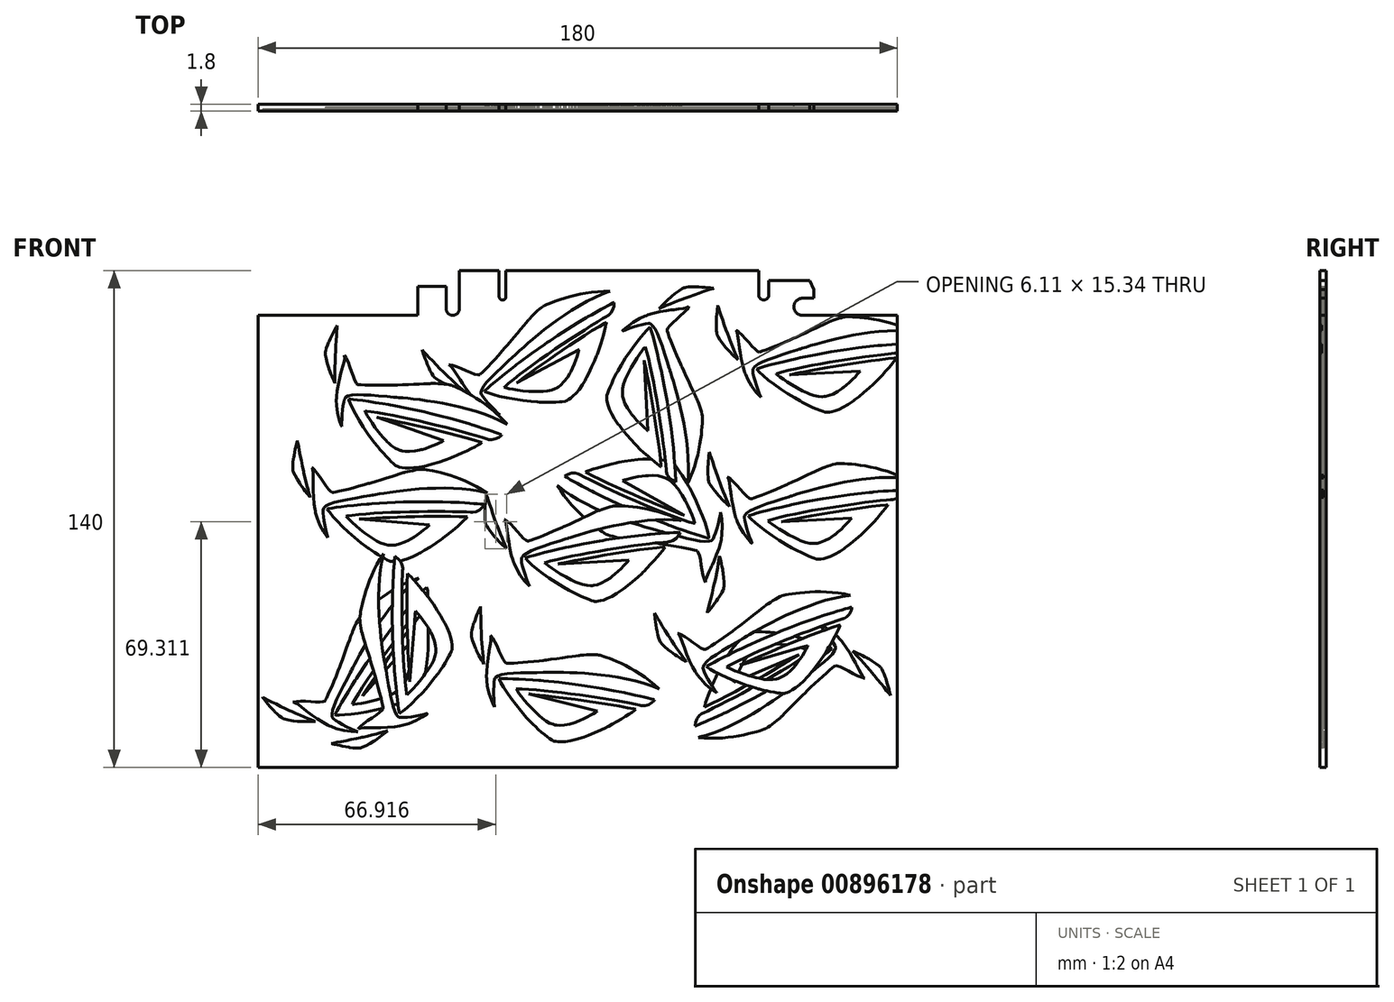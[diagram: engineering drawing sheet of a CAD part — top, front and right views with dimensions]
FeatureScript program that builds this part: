
annotation { "Feature Type Name" : "Feature", "Feature Type Description" : "" }
export const myFeature = defineFeature(function(context is Context, id is Id, definition is map)
    precondition{}
    {
        {
            var Q0;
            Q0=qCreatedBy(makeId("Front.planeOp"),FACE);
            var sketch = newSketch(context, id + "F0", { "sketchPlane" : qUnion([Q0])});
            skLineSegment(sketch, "E0", {"start": v(0, -8.2) * mm, "end": v(0, 0) * mm});
            skLineSegment(sketch, "E1", {"start": v(0, 0) * mm, "end": v(8, 0) * mm});
            skLineSegment(sketch, "E2", {"start": v(8, 0) * mm, "end": v(8, -6.35) * mm});
            skLineSegment(sketch, "E3", {"start": v(9.85, -8.2) * mm, "end": v(9.85, -8.2) * mm});
            skLineSegment(sketch, "E4", {"start": v(11.7, -6.35) * mm, "end": v(11.7, 4.4) * mm});
            skLineSegment(sketch, "E5", {"start": v(11.7, 4.4) * mm, "end": v(22.9, 4.4) * mm});
            skLineSegment(sketch, "E6", {"start": v(22.9, 4.4) * mm, "end": v(22.9, -2.95) * mm});
            skLineSegment(sketch, "E7", {"start": v(23.85, -3.9) * mm, "end": v(23.85, -3.9) * mm});
            skLineSegment(sketch, "E8", {"start": v(24.8, -2.95) * mm, "end": v(24.8, 4.4) * mm});
            skLineSegment(sketch, "E9", {"start": v(24.8, 4.4) * mm, "end": v(96, 4.4) * mm});
            skLineSegment(sketch, "E10", {"start": v(96, 4.4) * mm, "end": v(96, -2.5) * mm});
            skLineSegment(sketch, "E11", {"start": v(97.4, -3.9) * mm, "end": v(97.4, -3.9) * mm});
            skLineSegment(sketch, "E12", {"start": v(98.8, -2.5) * mm, "end": v(98.8, 1.6) * mm});
            skLineSegment(sketch, "E13", {"start": v(98.8, 1.6) * mm, "end": v(110.3, 1.6) * mm});
            skLineSegment(sketch, "E14", {"start": v(110.3, 1.6) * mm, "end": v(111.5, -0.9) * mm});
            skLineSegment(sketch, "E15", {"start": v(111.5, -0.9) * mm, "end": v(111.5, -3.4) * mm});
            skLineSegment(sketch, "E16", {"start": v(111.5, -3.4) * mm, "end": v(108.3, -3.4) * mm});
            skLineSegment(sketch, "E17", {"start": v(105.9, -5.8) * mm, "end": v(105.9, -5.8) * mm});
            skLineSegment(sketch, "E18", {"start": v(108.3, -8.2) * mm, "end": v(135, -8.2) * mm});
            skLineSegment(sketch, "E19", {"start": v(135, -8.2) * mm, "end": v(135, -135.6) * mm});
            skLineSegment(sketch, "E20", {"start": v(135, -135.6) * mm, "end": v(-45, -135.6) * mm});
            skLineSegment(sketch, "E21", {"start": v(-45, -135.6) * mm, "end": v(-45, -8.2) * mm});
            skLineSegment(sketch, "E22", {"start": v(-45, -8.2) * mm, "end": v(0, -8.2) * mm});
            skPoint(sketch, "E23.visualSharp", {"position": v(98.8, -3.9) * mm});
            skArc(sketch, "E23.filletArc", {"start": v(97.4, -3.9) * mm, "mid": v(98.39, -3.49) * mm, "end": v(98.8, -2.5) * mm});
            skPoint(sketch, "E24.visualSharp", {"position": v(96, -3.9) * mm});
            skArc(sketch, "E24.filletArc", {"start": v(96, -2.5) * mm, "mid": v(96.41, -3.49) * mm, "end": v(97.4, -3.9) * mm});
            skPoint(sketch, "E25.visualSharp", {"position": v(24.8, -3.9) * mm});
            skArc(sketch, "E25.filletArc", {"start": v(23.85, -3.9) * mm, "mid": v(24.52, -3.62) * mm, "end": v(24.8, -2.95) * mm});
            skPoint(sketch, "E26.visualSharp", {"position": v(22.9, -3.9) * mm});
            skArc(sketch, "E26.filletArc", {"start": v(22.9, -2.95) * mm, "mid": v(23.18, -3.62) * mm, "end": v(23.85, -3.9) * mm});
            skPoint(sketch, "E27.visualSharp", {"position": v(11.7, -8.2) * mm});
            skArc(sketch, "E27.filletArc", {"start": v(9.85, -8.2) * mm, "mid": v(11.16, -7.66) * mm, "end": v(11.7, -6.35) * mm});
            skPoint(sketch, "E28.visualSharp", {"position": v(8, -8.2) * mm});
            skArc(sketch, "E28.filletArc", {"start": v(8, -6.35) * mm, "mid": v(8.54, -7.66) * mm, "end": v(9.85, -8.2) * mm});
            skPoint(sketch, "E29.visualSharp", {"position": v(105.9, -3.4) * mm});
            skArc(sketch, "E29.filletArc", {"start": v(108.3, -3.4) * mm, "mid": v(106.6, -4.1) * mm, "end": v(105.9, -5.8) * mm});
            skPoint(sketch, "E30.visualSharp", {"position": v(105.9, -8.2) * mm});
            skArc(sketch, "E30.filletArc", {"start": v(105.9, -5.8) * mm, "mid": v(106.6, -7.5) * mm, "end": v(108.3, -8.2) * mm});
            skSolve(sketch);
        }
        {
            var Q0;
            Q0=makeQuery(id+"F0.imprint","IMPRINT",FACE,{"disambiguationData":[TD([[makeQuery(id+"F0.imprint","IMPRINT",EDGE,{"derivedFrom":sQuery(id+"F0.wireOp",EDGE,"E0")}),-1.0]])]});
            extrude(context, id + "F1", {"entities" : qUnion([Q0]), "depth" : 1.8 * mm, "offsetDistance" : 25 * mm});
        }
        {
            var Q0;
            Q0=makeQuery(id+"F1.opExtrude","CAP_FACE",FACE,{"disambiguationData":[OSD([sQuery(id+"F0.wireOp",EDGE,"E0"),sQuery(id+"F0.wireOp",EDGE,"E1"),sQuery(id+"F0.wireOp",EDGE,"E2"),sQuery(id+"F0.wireOp",EDGE,"E4"),sQuery(id+"F0.wireOp",EDGE,"E5"),sQuery(id+"F0.wireOp",EDGE,"E6"),sQuery(id+"F0.wireOp",EDGE,"E8"),sQuery(id+"F0.wireOp",EDGE,"E9"),sQuery(id+"F0.wireOp",EDGE,"E10"),sQuery(id+"F0.wireOp",EDGE,"E12"),sQuery(id+"F0.wireOp",EDGE,"E13"),sQuery(id+"F0.wireOp",EDGE,"E14"),sQuery(id+"F0.wireOp",EDGE,"E15"),sQuery(id+"F0.wireOp",EDGE,"E16"),sQuery(id+"F0.wireOp",EDGE,"E18"),sQuery(id+"F0.wireOp",EDGE,"E19"),sQuery(id+"F0.wireOp",EDGE,"E20"),sQuery(id+"F0.wireOp",EDGE,"E21"),sQuery(id+"F0.wireOp",EDGE,"E22"),sQuery(id+"F0.wireOp",EDGE,"E23.filletArc"),sQuery(id+"F0.wireOp",EDGE,"E24.filletArc"),sQuery(id+"F0.wireOp",EDGE,"E25.filletArc"),sQuery(id+"F0.wireOp",EDGE,"E26.filletArc"),sQuery(id+"F0.wireOp",EDGE,"E27.filletArc"),sQuery(id+"F0.wireOp",EDGE,"E28.filletArc"),sQuery(id+"F0.wireOp",EDGE,"E29.filletArc"),sQuery(id+"F0.wireOp",EDGE,"E30.filletArc")])],"isStart":false});
            var sketch = newSketch(context, id + "F2", { "sketchPlane" : qUnion([Q0])});
            skLineSegment(sketch, "E31", {"start": v(86.64, -17.14) * mm, "end": v(86.89, -17.43) * mm});
            skLineSegment(sketch, "E32", {"start": v(85.92, -16.26) * mm, "end": v(86.64, -17.14) * mm});
            skLineSegment(sketch, "E33", {"start": v(85.12, -15.18) * mm, "end": v(85.92, -16.26) * mm});
            skLineSegment(sketch, "E34", {"start": v(84.55, -14.28) * mm, "end": v(85.12, -15.18) * mm});
            skLineSegment(sketch, "E35", {"start": v(84.3, -13.81) * mm, "end": v(84.55, -14.28) * mm});
            skLineSegment(sketch, "E36", {"start": v(84.27, -13.67) * mm, "end": v(84.3, -13.81) * mm});
            skLineSegment(sketch, "E37", {"start": v(84.24, -13.55) * mm, "end": v(84.27, -13.67) * mm});
            skLineSegment(sketch, "E38", {"start": v(84.17, -13.18) * mm, "end": v(84.24, -13.55) * mm});
            skLineSegment(sketch, "E39", {"start": v(84.08, -12.47) * mm, "end": v(84.17, -13.18) * mm});
            skLineSegment(sketch, "E40", {"start": v(84.03, -11.56) * mm, "end": v(84.08, -12.47) * mm});
            skLineSegment(sketch, "E41", {"start": v(84.02, -10.76) * mm, "end": v(84.03, -11.56) * mm});
            skLineSegment(sketch, "E42", {"start": v(84.03, -10.5) * mm, "end": v(84.02, -10.76) * mm});
            skLineSegment(sketch, "E43", {"start": v(84.04, -10.27) * mm, "end": v(84.03, -10.5) * mm});
            skLineSegment(sketch, "E44", {"start": v(84.07, -9.6) * mm, "end": v(84.04, -10.27) * mm});
            skLineSegment(sketch, "E45", {"start": v(84.12, -8.71) * mm, "end": v(84.07, -9.6) * mm});
            skLineSegment(sketch, "E46", {"start": v(84.19, -7.85) * mm, "end": v(84.12, -8.71) * mm});
            skLineSegment(sketch, "E47", {"start": v(84.26, -7.06) * mm, "end": v(84.19, -7.85) * mm});
            skLineSegment(sketch, "E48", {"start": v(84.32, -6.38) * mm, "end": v(84.26, -7.06) * mm});
            skLineSegment(sketch, "E49", {"start": v(84.38, -5.84) * mm, "end": v(84.32, -6.38) * mm});
            skLineSegment(sketch, "E50", {"start": v(84.42, -5.5) * mm, "end": v(84.38, -5.84) * mm});
            skLineSegment(sketch, "E51", {"start": v(84.43, -5.37) * mm, "end": v(84.42, -5.5) * mm});
            skLineSegment(sketch, "E52", {"start": v(84.5, -5.57) * mm, "end": v(84.43, -5.37) * mm});
            skLineSegment(sketch, "E53", {"start": v(84.69, -6.14) * mm, "end": v(84.5, -5.57) * mm});
            skLineSegment(sketch, "E54", {"start": v(84.98, -7.02) * mm, "end": v(84.69, -6.14) * mm});
            skLineSegment(sketch, "E55", {"start": v(85.35, -8.13) * mm, "end": v(84.98, -7.02) * mm});
            skLineSegment(sketch, "E56", {"start": v(85.79, -9.42) * mm, "end": v(85.35, -8.13) * mm});
            skLineSegment(sketch, "E57", {"start": v(86.27, -10.83) * mm, "end": v(85.79, -9.42) * mm});
            skLineSegment(sketch, "E58", {"start": v(86.79, -12.28) * mm, "end": v(86.27, -10.83) * mm});
            skLineSegment(sketch, "E59", {"start": v(87.18, -13.36) * mm, "end": v(86.79, -12.28) * mm});
            skLineSegment(sketch, "E60", {"start": v(87.31, -13.72) * mm, "end": v(87.18, -13.36) * mm});
            skLineSegment(sketch, "E61", {"start": v(87.44, -14.08) * mm, "end": v(87.31, -13.72) * mm});
            skLineSegment(sketch, "E62", {"start": v(87.85, -15.14) * mm, "end": v(87.44, -14.08) * mm});
            skLineSegment(sketch, "E63", {"start": v(88.36, -16.46) * mm, "end": v(87.85, -15.14) * mm});
            skLineSegment(sketch, "E64", {"start": v(88.84, -17.64) * mm, "end": v(88.36, -16.46) * mm});
            skLineSegment(sketch, "E65", {"start": v(89.27, -18.67) * mm, "end": v(88.84, -17.64) * mm});
            skLineSegment(sketch, "E66", {"start": v(89.62, -19.52) * mm, "end": v(89.27, -18.67) * mm});
            skLineSegment(sketch, "E67", {"start": v(89.9, -20.16) * mm, "end": v(89.62, -19.52) * mm});
            skLineSegment(sketch, "E68", {"start": v(90.07, -20.56) * mm, "end": v(89.9, -20.16) * mm});
            skLineSegment(sketch, "E69", {"start": v(90.13, -20.7) * mm, "end": v(90.07, -20.56) * mm});
            skLineSegment(sketch, "E70", {"start": v(90.05, -20.63) * mm, "end": v(90.13, -20.7) * mm});
            skLineSegment(sketch, "E71", {"start": v(89.83, -20.42) * mm, "end": v(90.05, -20.63) * mm});
            skLineSegment(sketch, "E72", {"start": v(89.5, -20.1) * mm, "end": v(89.83, -20.42) * mm});
            skLineSegment(sketch, "E73", {"start": v(89.06, -19.69) * mm, "end": v(89.5, -20.1) * mm});
            skLineSegment(sketch, "E74", {"start": v(88.56, -19.2) * mm, "end": v(89.06, -19.69) * mm});
            skLineSegment(sketch, "E75", {"start": v(88.01, -18.64) * mm, "end": v(88.56, -19.2) * mm});
            skLineSegment(sketch, "E76", {"start": v(87.45, -18.04) * mm, "end": v(88.01, -18.64) * mm});
            skLineSegment(sketch, "E77", {"start": v(87.03, -17.58) * mm, "end": v(87.45, -18.04) * mm});
            skLineSegment(sketch, "E78", {"start": v(86.89, -17.43) * mm, "end": v(87.03, -17.58) * mm});
            skLineSegment(sketch, "E79", {"start": v(106.83, -17.95) * mm, "end": v(107.42, -17.75) * mm});
            skLineSegment(sketch, "E80", {"start": v(105.06, -18.52) * mm, "end": v(106.83, -17.95) * mm});
            skLineSegment(sketch, "E81", {"start": v(102.8, -19.24) * mm, "end": v(105.06, -18.52) * mm});
            skLineSegment(sketch, "E82", {"start": v(100.69, -19.92) * mm, "end": v(102.8, -19.24) * mm});
            skLineSegment(sketch, "E83", {"start": v(98.8, -20.59) * mm, "end": v(100.69, -19.92) * mm});
            skLineSegment(sketch, "E84", {"start": v(97.16, -21.25) * mm, "end": v(98.8, -20.59) * mm});
            skLineSegment(sketch, "E85", {"start": v(95.84, -21.91) * mm, "end": v(97.16, -21.25) * mm});
            skLineSegment(sketch, "E86", {"start": v(94.89, -22.6) * mm, "end": v(95.84, -21.91) * mm});
            skLineSegment(sketch, "E87", {"start": v(94.44, -23.13) * mm, "end": v(94.89, -22.6) * mm});
            skLineSegment(sketch, "E88", {"start": v(94.36, -23.33) * mm, "end": v(94.44, -23.13) * mm});
            skLineSegment(sketch, "E89", {"start": v(94.31, -23.44) * mm, "end": v(94.36, -23.33) * mm});
            skLineSegment(sketch, "E90", {"start": v(94.31, -23.83) * mm, "end": v(94.31, -23.44) * mm});
            skLineSegment(sketch, "E91", {"start": v(94.41, -24.61) * mm, "end": v(94.31, -23.83) * mm});
            skLineSegment(sketch, "E92", {"start": v(94.63, -25.62) * mm, "end": v(94.41, -24.61) * mm});
            skLineSegment(sketch, "E93", {"start": v(94.95, -26.77) * mm, "end": v(94.63, -25.62) * mm});
            skLineSegment(sketch, "E94", {"start": v(95.33, -27.98) * mm, "end": v(94.95, -26.77) * mm});
            skLineSegment(sketch, "E95", {"start": v(95.75, -29.18) * mm, "end": v(95.33, -27.98) * mm});
            skLineSegment(sketch, "E96", {"start": v(96.18, -30.29) * mm, "end": v(95.75, -29.18) * mm});
            skLineSegment(sketch, "E97", {"start": v(96.48, -31) * mm, "end": v(96.18, -30.29) * mm});
            skLineSegment(sketch, "E98", {"start": v(96.6, -31.24) * mm, "end": v(96.48, -31) * mm});
            skLineSegment(sketch, "E99", {"start": v(96.24, -30.91) * mm, "end": v(96.6, -31.24) * mm});
            skLineSegment(sketch, "E100", {"start": v(95.27, -29.84) * mm, "end": v(96.24, -30.91) * mm});
            skLineSegment(sketch, "E101", {"start": v(94.02, -28.15) * mm, "end": v(95.27, -29.84) * mm});
            skLineSegment(sketch, "E102", {"start": v(92.93, -26.28) * mm, "end": v(94.02, -28.15) * mm});
            skLineSegment(sketch, "E103", {"start": v(92.27, -24.86) * mm, "end": v(92.93, -26.28) * mm});
            skLineSegment(sketch, "E104", {"start": v(92.09, -24.37) * mm, "end": v(92.27, -24.86) * mm});
            skLineSegment(sketch, "E105", {"start": v(91.92, -23.9) * mm, "end": v(92.09, -24.37) * mm});
            skLineSegment(sketch, "E106", {"start": v(91.5, -22.48) * mm, "end": v(91.92, -23.9) * mm});
            skLineSegment(sketch, "E107", {"start": v(91.07, -20.55) * mm, "end": v(91.5, -22.48) * mm});
            skLineSegment(sketch, "E108", {"start": v(90.74, -18.7) * mm, "end": v(91.07, -20.55) * mm});
            skLineSegment(sketch, "E109", {"start": v(90.56, -17.46) * mm, "end": v(90.74, -18.7) * mm});
            skLineSegment(sketch, "E110", {"start": v(90.5, -17.05) * mm, "end": v(90.56, -17.46) * mm});
            skLineSegment(sketch, "E111", {"start": v(90.45, -16.6) * mm, "end": v(90.5, -17.05) * mm});
            skLineSegment(sketch, "E112", {"start": v(90.28, -15.26) * mm, "end": v(90.45, -16.6) * mm});
            skLineSegment(sketch, "E113", {"start": v(90.09, -13.9) * mm, "end": v(90.28, -15.26) * mm});
            skLineSegment(sketch, "E114", {"start": v(89.85, -12.95) * mm, "end": v(90.09, -13.9) * mm});
            skLineSegment(sketch, "E115", {"start": v(89.61, -12.5) * mm, "end": v(89.85, -12.95) * mm});
            skLineSegment(sketch, "E116", {"start": v(89.5, -12.4) * mm, "end": v(89.61, -12.5) * mm});
            skLineSegment(sketch, "E117", {"start": v(89.72, -12.49) * mm, "end": v(89.5, -12.4) * mm});
            skLineSegment(sketch, "E118", {"start": v(90.34, -12.92) * mm, "end": v(89.72, -12.49) * mm});
            skLineSegment(sketch, "E119", {"start": v(91.26, -13.75) * mm, "end": v(90.34, -12.92) * mm});
            skLineSegment(sketch, "E120", {"start": v(92.21, -14.77) * mm, "end": v(91.26, -13.75) * mm});
            skLineSegment(sketch, "E121", {"start": v(93.16, -15.85) * mm, "end": v(92.21, -14.77) * mm});
            skLineSegment(sketch, "E122", {"start": v(94.08, -16.88) * mm, "end": v(93.16, -15.85) * mm});
            skLineSegment(sketch, "E123", {"start": v(94.92, -17.75) * mm, "end": v(94.08, -16.88) * mm});
            skLineSegment(sketch, "E124", {"start": v(95.66, -18.33) * mm, "end": v(94.92, -17.75) * mm});
            skLineSegment(sketch, "E125", {"start": v(96.1, -18.53) * mm, "end": v(95.66, -18.33) * mm});
            skLineSegment(sketch, "E126", {"start": v(96.25, -18.52) * mm, "end": v(96.1, -18.53) * mm});
            skLineSegment(sketch, "E127", {"start": v(96.46, -18.46) * mm, "end": v(96.25, -18.52) * mm});
            skLineSegment(sketch, "E128", {"start": v(97.08, -18.26) * mm, "end": v(96.46, -18.46) * mm});
            skLineSegment(sketch, "E129", {"start": v(98.08, -17.91) * mm, "end": v(97.08, -18.26) * mm});
            skLineSegment(sketch, "E130", {"start": v(99.23, -17.48) * mm, "end": v(98.08, -17.91) * mm});
            skLineSegment(sketch, "E131", {"start": v(100.5, -16.97) * mm, "end": v(99.23, -17.48) * mm});
            skLineSegment(sketch, "E132", {"start": v(101.85, -16.41) * mm, "end": v(100.5, -16.97) * mm});
            skLineSegment(sketch, "E133", {"start": v(103.28, -15.81) * mm, "end": v(101.85, -16.41) * mm});
            skLineSegment(sketch, "E134", {"start": v(104.73, -15.18) * mm, "end": v(103.28, -15.81) * mm});
            skLineSegment(sketch, "E135", {"start": v(105.83, -14.69) * mm, "end": v(104.73, -15.18) * mm});
            skLineSegment(sketch, "E136", {"start": v(106.2, -14.52) * mm, "end": v(105.83, -14.69) * mm});
            skLineSegment(sketch, "E137", {"start": v(106.6, -14.34) * mm, "end": v(106.2, -14.52) * mm});
            skLineSegment(sketch, "E138", {"start": v(107.79, -13.8) * mm, "end": v(106.6, -14.34) * mm});
            skLineSegment(sketch, "E139", {"start": v(109.32, -13.1) * mm, "end": v(107.79, -13.8) * mm});
            skLineSegment(sketch, "E140", {"start": v(110.75, -12.43) * mm, "end": v(109.32, -13.1) * mm});
            skLineSegment(sketch, "E141", {"start": v(112.06, -11.81) * mm, "end": v(110.75, -12.43) * mm});
            skLineSegment(sketch, "E142", {"start": v(130.44, -19.3) * mm, "end": v(132.47, -19.06) * mm});
            skLineSegment(sketch, "E143", {"start": v(128.25, -19.57) * mm, "end": v(130.44, -19.3) * mm});
            skLineSegment(sketch, "E144", {"start": v(138.93, -16.33) * mm, "end": v(139.01, -16.1) * mm});
            skLineSegment(sketch, "E145", {"start": v(139.01, -16.1) * mm, "end": v(138.9, -16.1) * mm});
            skLineSegment(sketch, "E146", {"start": v(138.9, -16.1) * mm, "end": v(138.6, -16.1) * mm});
            skLineSegment(sketch, "E147", {"start": v(138.6, -16.1) * mm, "end": v(137.97, -16.11) * mm});
            skLineSegment(sketch, "E148", {"start": v(137.97, -16.11) * mm, "end": v(137.11, -16.15) * mm});
            skLineSegment(sketch, "E149", {"start": v(137.11, -16.15) * mm, "end": v(136.07, -16.2) * mm});
            skLineSegment(sketch, "E150", {"start": v(136.07, -16.2) * mm, "end": v(134.84, -16.28) * mm});
            skLineSegment(sketch, "E151", {"start": v(134.84, -16.28) * mm, "end": v(133.45, -16.38) * mm});
            skLineSegment(sketch, "E152", {"start": v(133.45, -16.38) * mm, "end": v(131.92, -16.51) * mm});
            skLineSegment(sketch, "E153", {"start": v(131.92, -16.51) * mm, "end": v(130.68, -16.62) * mm});
            skLineSegment(sketch, "E154", {"start": v(130.68, -16.62) * mm, "end": v(130.26, -16.66) * mm});
            skLineSegment(sketch, "E155", {"start": v(130.26, -16.66) * mm, "end": v(129.52, -16.73) * mm});
            skLineSegment(sketch, "E156", {"start": v(129.52, -16.73) * mm, "end": v(127.28, -16.97) * mm});
            skLineSegment(sketch, "E157", {"start": v(127.28, -16.97) * mm, "end": v(124.08, -17.36) * mm});
            skLineSegment(sketch, "E158", {"start": v(124.08, -17.36) * mm, "end": v(120.72, -17.82) * mm});
            skLineSegment(sketch, "E159", {"start": v(120.72, -17.82) * mm, "end": v(118.13, -18.22) * mm});
            skLineSegment(sketch, "E160", {"start": v(118.13, -18.22) * mm, "end": v(117.27, -18.36) * mm});
            skLineSegment(sketch, "E161", {"start": v(117.27, -18.36) * mm, "end": v(116.34, -18.5) * mm});
            skLineSegment(sketch, "E162", {"start": v(116.34, -18.5) * mm, "end": v(111.9, -19.31) * mm});
            skLineSegment(sketch, "E163", {"start": v(111.9, -19.31) * mm, "end": v(107.65, -20.17) * mm});
            skLineSegment(sketch, "E164", {"start": v(107.65, -20.17) * mm, "end": v(106.82, -20.35) * mm});
            skLineSegment(sketch, "E165", {"start": v(107.42, -17.75) * mm, "end": v(107.62, -17.69) * mm});
            skLineSegment(sketch, "E166", {"start": v(107.62, -17.69) * mm, "end": v(108.23, -17.49) * mm});
            skLineSegment(sketch, "E167", {"start": v(108.23, -17.49) * mm, "end": v(109.32, -17.14) * mm});
            skLineSegment(sketch, "E168", {"start": v(109.32, -17.14) * mm, "end": v(110.65, -16.73) * mm});
            skLineSegment(sketch, "E169", {"start": v(110.65, -16.73) * mm, "end": v(112.22, -16.27) * mm});
            skLineSegment(sketch, "E170", {"start": v(112.22, -16.27) * mm, "end": v(113.98, -15.78) * mm});
            skLineSegment(sketch, "E171", {"start": v(113.98, -15.78) * mm, "end": v(115.92, -15.27) * mm});
            skLineSegment(sketch, "E172", {"start": v(115.92, -15.27) * mm, "end": v(118, -14.76) * mm});
            skLineSegment(sketch, "E173", {"start": v(118, -14.76) * mm, "end": v(120.22, -14.27) * mm});
            skLineSegment(sketch, "E174", {"start": v(120.22, -14.27) * mm, "end": v(122.53, -13.8) * mm});
            skLineSegment(sketch, "E175", {"start": v(122.53, -13.8) * mm, "end": v(124.91, -13.39) * mm});
            skLineSegment(sketch, "E176", {"start": v(124.91, -13.39) * mm, "end": v(127.34, -13.03) * mm});
            skLineSegment(sketch, "E177", {"start": v(127.34, -13.03) * mm, "end": v(129.8, -12.76) * mm});
            skLineSegment(sketch, "E178", {"start": v(129.8, -12.76) * mm, "end": v(132.25, -12.58) * mm});
            skLineSegment(sketch, "E179", {"start": v(132.25, -12.58) * mm, "end": v(134.68, -12.5) * mm});
            skLineSegment(sketch, "E180", {"start": v(134.68, -12.5) * mm, "end": v(137.05, -12.56) * mm});
            skLineSegment(sketch, "E181", {"start": v(137.05, -12.56) * mm, "end": v(138.77, -12.7) * mm});
            skLineSegment(sketch, "E182", {"start": v(138.77, -12.7) * mm, "end": v(139.34, -12.76) * mm});
            skLineSegment(sketch, "E183", {"start": v(139.34, -12.76) * mm, "end": v(138.95, -12.56) * mm});
            skLineSegment(sketch, "E184", {"start": v(138.95, -12.56) * mm, "end": v(137.76, -12) * mm});
            skLineSegment(sketch, "E185", {"start": v(137.76, -12) * mm, "end": v(136.16, -11.35) * mm});
            skLineSegment(sketch, "E186", {"start": v(136.16, -11.35) * mm, "end": v(134.55, -10.79) * mm});
            skLineSegment(sketch, "E187", {"start": v(134.55, -10.79) * mm, "end": v(132.95, -10.3) * mm});
            skLineSegment(sketch, "E188", {"start": v(132.95, -10.3) * mm, "end": v(131.38, -9.9) * mm});
            skLineSegment(sketch, "E189", {"start": v(131.38, -9.9) * mm, "end": v(129.85, -9.55) * mm});
            skLineSegment(sketch, "E190", {"start": v(129.85, -9.55) * mm, "end": v(128.38, -9.27) * mm});
            skLineSegment(sketch, "E191", {"start": v(128.38, -9.27) * mm, "end": v(126.98, -9.05) * mm});
            skLineSegment(sketch, "E192", {"start": v(126.98, -9.05) * mm, "end": v(125.67, -8.89) * mm});
            skLineSegment(sketch, "E193", {"start": v(125.67, -8.89) * mm, "end": v(124.48, -8.76) * mm});
            skLineSegment(sketch, "E194", {"start": v(117.72, -9.36) * mm, "end": v(116.97, -9.63) * mm});
            skLineSegment(sketch, "E195", {"start": v(116.97, -9.63) * mm, "end": v(116.29, -9.88) * mm});
            skLineSegment(sketch, "E196", {"start": v(116.29, -9.88) * mm, "end": v(115.72, -10.1) * mm});
            skLineSegment(sketch, "E197", {"start": v(115.72, -10.1) * mm, "end": v(115.43, -10.22) * mm});
            skLineSegment(sketch, "E198", {"start": v(97.78, -22.58) * mm, "end": v(96.66, -22.9) * mm});
            skLineSegment(sketch, "E199", {"start": v(96.66, -22.9) * mm, "end": v(95.85, -23.15) * mm});
            skLineSegment(sketch, "E200", {"start": v(95.85, -23.15) * mm, "end": v(95.5, -23.27) * mm});
            skLineSegment(sketch, "E201", {"start": v(104.68, -20.84) * mm, "end": v(102.66, -21.32) * mm});
            skLineSegment(sketch, "E202", {"start": v(115.22, -10.31) * mm, "end": v(114.88, -10.47) * mm});
            skLineSegment(sketch, "E203", {"start": v(95.5, -23.27) * mm, "end": v(95.38, -23.32) * mm});
            skLineSegment(sketch, "E204", {"start": v(102.66, -21.32) * mm, "end": v(100.82, -21.78) * mm});
            skLineSegment(sketch, "E205", {"start": v(114.88, -10.47) * mm, "end": v(114.16, -10.81) * mm});
            skLineSegment(sketch, "E206", {"start": v(95.38, -23.32) * mm, "end": v(95.57, -23.55) * mm});
            skLineSegment(sketch, "E207", {"start": v(100.82, -21.78) * mm, "end": v(99.18, -22.2) * mm});
            skLineSegment(sketch, "E208", {"start": v(114.16, -10.81) * mm, "end": v(113.2, -11.27) * mm});
            skLineSegment(sketch, "E209", {"start": v(95.57, -23.55) * mm, "end": v(96.18, -24.2) * mm});
            skLineSegment(sketch, "E210", {"start": v(99.18, -22.2) * mm, "end": v(97.78, -22.58) * mm});
            skLineSegment(sketch, "E211", {"start": v(113.2, -11.27) * mm, "end": v(112.06, -11.81) * mm});
            skLineSegment(sketch, "E212", {"start": v(106.82, -20.35) * mm, "end": v(106.29, -20.47) * mm});
            skLineSegment(sketch, "E213", {"start": v(96.18, -24.2) * mm, "end": v(97.3, -25.24) * mm});
            skLineSegment(sketch, "E214", {"start": v(97.3, -25.24) * mm, "end": v(98.71, -26.4) * mm});
            skLineSegment(sketch, "E215", {"start": v(108.17, -32.63) * mm, "end": v(108.42, -32.76) * mm});
            skLineSegment(sketch, "E216", {"start": v(108.42, -32.76) * mm, "end": v(109.18, -33.15) * mm});
            skLineSegment(sketch, "E217", {"start": v(109.18, -33.15) * mm, "end": v(110.24, -33.66) * mm});
            skLineSegment(sketch, "E218", {"start": v(110.24, -33.66) * mm, "end": v(111.3, -34.15) * mm});
            skLineSegment(sketch, "E219", {"start": v(107.65, -32.35) * mm, "end": v(108.17, -32.63) * mm});
            skLineSegment(sketch, "E220", {"start": v(106.13, -31.48) * mm, "end": v(107.65, -32.35) * mm});
            skLineSegment(sketch, "E221", {"start": v(104.1, -30.23) * mm, "end": v(106.13, -31.48) * mm});
            skLineSegment(sketch, "E222", {"start": v(102.16, -28.95) * mm, "end": v(104.1, -30.23) * mm});
            skLineSegment(sketch, "E223", {"start": v(100.35, -27.66) * mm, "end": v(102.16, -28.95) * mm});
            skLineSegment(sketch, "E224", {"start": v(98.71, -26.4) * mm, "end": v(100.35, -27.66) * mm});
            skLineSegment(sketch, "E225", {"start": v(115.33, -10.26) * mm, "end": v(115.22, -10.31) * mm});
            skLineSegment(sketch, "E226", {"start": v(106.29, -20.47) * mm, "end": v(104.68, -20.84) * mm});
            skLineSegment(sketch, "E227", {"start": v(118.5, -9.11) * mm, "end": v(117.72, -9.36) * mm});
            skLineSegment(sketch, "E228", {"start": v(115.43, -10.22) * mm, "end": v(115.33, -10.26) * mm});
            skLineSegment(sketch, "E229", {"start": v(119.24, -8.89) * mm, "end": v(118.5, -9.11) * mm});
            skLineSegment(sketch, "E230", {"start": v(119.9, -8.71) * mm, "end": v(119.24, -8.89) * mm});
            skLineSegment(sketch, "E231", {"start": v(120.31, -8.63) * mm, "end": v(119.9, -8.71) * mm});
            skLineSegment(sketch, "E232", {"start": v(120.45, -8.6) * mm, "end": v(120.31, -8.63) * mm});
            skLineSegment(sketch, "E233", {"start": v(120.5, -8.6) * mm, "end": v(120.45, -8.6) * mm});
            skLineSegment(sketch, "E234", {"start": v(120.66, -8.6) * mm, "end": v(120.5, -8.6) * mm});
            skLineSegment(sketch, "E235", {"start": v(121.08, -8.59) * mm, "end": v(120.66, -8.6) * mm});
            skLineSegment(sketch, "E236", {"start": v(121.69, -8.6) * mm, "end": v(121.08, -8.59) * mm});
            skLineSegment(sketch, "E237", {"start": v(122.47, -8.62) * mm, "end": v(121.69, -8.6) * mm});
            skLineSegment(sketch, "E238", {"start": v(123.4, -8.68) * mm, "end": v(122.47, -8.62) * mm});
            skLineSegment(sketch, "E239", {"start": v(124.48, -8.76) * mm, "end": v(123.4, -8.68) * mm});
            skLineSegment(sketch, "E240", {"start": v(138.57, -17) * mm, "end": v(138.93, -16.33) * mm});
            skLineSegment(sketch, "E241", {"start": v(137.87, -17.82) * mm, "end": v(138.57, -17) * mm});
            skLineSegment(sketch, "E242", {"start": v(136.96, -18.43) * mm, "end": v(137.87, -17.82) * mm});
            skLineSegment(sketch, "E243", {"start": v(136.15, -18.7) * mm, "end": v(136.96, -18.43) * mm});
            skLineSegment(sketch, "E244", {"start": v(135.87, -18.73) * mm, "end": v(136.15, -18.7) * mm});
            skLineSegment(sketch, "E245", {"start": v(135.47, -18.76) * mm, "end": v(135.87, -18.73) * mm});
            skLineSegment(sketch, "E246", {"start": v(134.29, -18.87) * mm, "end": v(135.47, -18.76) * mm});
            skLineSegment(sketch, "E247", {"start": v(132.47, -19.06) * mm, "end": v(134.29, -18.87) * mm});
            skLineSegment(sketch, "E248", {"start": v(107.74, -24.36) * mm, "end": v(106.46, -24.62) * mm});
            skLineSegment(sketch, "E249", {"start": v(109.3, -24.06) * mm, "end": v(107.74, -24.36) * mm});
            skLineSegment(sketch, "E250", {"start": v(111.12, -23.72) * mm, "end": v(109.3, -24.06) * mm});
            skLineSegment(sketch, "E251", {"start": v(113.14, -23.34) * mm, "end": v(111.12, -23.72) * mm});
            skLineSegment(sketch, "E252", {"start": v(115.34, -22.95) * mm, "end": v(113.14, -23.34) * mm});
            skLineSegment(sketch, "E253", {"start": v(117.67, -22.54) * mm, "end": v(115.34, -22.95) * mm});
            skLineSegment(sketch, "E254", {"start": v(120.1, -22.13) * mm, "end": v(117.67, -22.54) * mm});
            skLineSegment(sketch, "E255", {"start": v(122.6, -21.73) * mm, "end": v(120.1, -22.13) * mm});
            skLineSegment(sketch, "E256", {"start": v(125.12, -21.35) * mm, "end": v(122.6, -21.73) * mm});
            skLineSegment(sketch, "E257", {"start": v(127.63, -21) * mm, "end": v(125.12, -21.35) * mm});
            skLineSegment(sketch, "E258", {"start": v(130.1, -20.69) * mm, "end": v(127.63, -21) * mm});
            skLineSegment(sketch, "E259", {"start": v(132.47, -20.42) * mm, "end": v(130.1, -20.69) * mm});
            skLineSegment(sketch, "E260", {"start": v(134.16, -20.26) * mm, "end": v(132.47, -20.42) * mm});
            skLineSegment(sketch, "E261", {"start": v(134.73, -20.22) * mm, "end": v(134.16, -20.26) * mm});
            skLineSegment(sketch, "E262", {"start": v(134.66, -20.33) * mm, "end": v(134.73, -20.22) * mm});
            skLineSegment(sketch, "E263", {"start": v(134.43, -20.67) * mm, "end": v(134.66, -20.33) * mm});
            skLineSegment(sketch, "E264", {"start": v(133.97, -21.3) * mm, "end": v(134.43, -20.67) * mm});
            skLineSegment(sketch, "E265", {"start": v(133.34, -22.08) * mm, "end": v(133.97, -21.3) * mm});
            skLineSegment(sketch, "E266", {"start": v(132.59, -22.98) * mm, "end": v(133.34, -22.08) * mm});
            skLineSegment(sketch, "E267", {"start": v(131.7, -23.98) * mm, "end": v(132.59, -22.98) * mm});
            skLineSegment(sketch, "E268", {"start": v(130.74, -25.05) * mm, "end": v(131.7, -23.98) * mm});
            skLineSegment(sketch, "E269", {"start": v(129.68, -26.16) * mm, "end": v(130.74, -25.05) * mm});
            skLineSegment(sketch, "E270", {"start": v(128.85, -27.01) * mm, "end": v(129.68, -26.16) * mm});
            skLineSegment(sketch, "E271", {"start": v(128.57, -27.3) * mm, "end": v(128.85, -27.01) * mm});
            skLineSegment(sketch, "E272", {"start": v(115.89, -35.5) * mm, "end": v(116.6, -35.37) * mm});
            skLineSegment(sketch, "E273", {"start": v(115.38, -35.54) * mm, "end": v(115.89, -35.5) * mm});
            skLineSegment(sketch, "E274", {"start": v(115.16, -35.54) * mm, "end": v(115.38, -35.54) * mm});
            skLineSegment(sketch, "E275", {"start": v(115.09, -35.53) * mm, "end": v(115.16, -35.54) * mm});
            skLineSegment(sketch, "E276", {"start": v(114.98, -35.52) * mm, "end": v(115.09, -35.53) * mm});
            skLineSegment(sketch, "E277", {"start": v(114.68, -35.45) * mm, "end": v(114.98, -35.52) * mm});
            skLineSegment(sketch, "E278", {"start": v(111.3, -34.15) * mm, "end": v(112.32, -34.58) * mm});
            skLineSegment(sketch, "E279", {"start": v(112.32, -34.58) * mm, "end": v(113.25, -34.96) * mm});
            skLineSegment(sketch, "E280", {"start": v(113.25, -34.96) * mm, "end": v(114.05, -35.25) * mm});
            skLineSegment(sketch, "E281", {"start": v(114.05, -35.25) * mm, "end": v(114.68, -35.45) * mm});
            skLineSegment(sketch, "E282", {"start": v(116.6, -35.37) * mm, "end": v(117.48, -35.12) * mm});
            skLineSegment(sketch, "E283", {"start": v(117.48, -35.12) * mm, "end": v(118.55, -34.72) * mm});
            skLineSegment(sketch, "E284", {"start": v(118.55, -34.72) * mm, "end": v(119.78, -34.14) * mm});
            skLineSegment(sketch, "E285", {"start": v(119.78, -34.14) * mm, "end": v(121.17, -33.32) * mm});
            skLineSegment(sketch, "E286", {"start": v(121.17, -33.32) * mm, "end": v(122.34, -32.54) * mm});
            skLineSegment(sketch, "E287", {"start": v(122.34, -32.54) * mm, "end": v(122.71, -32.25) * mm});
            skLineSegment(sketch, "E288", {"start": v(122.71, -32.25) * mm, "end": v(123.07, -31.98) * mm});
            skLineSegment(sketch, "E289", {"start": v(123.07, -31.98) * mm, "end": v(124.15, -31.16) * mm});
            skLineSegment(sketch, "E290", {"start": v(124.15, -31.16) * mm, "end": v(125.64, -29.95) * mm});
            skLineSegment(sketch, "E291", {"start": v(125.64, -29.95) * mm, "end": v(127.13, -28.66) * mm});
            skLineSegment(sketch, "E292", {"start": v(127.13, -28.66) * mm, "end": v(128.22, -27.64) * mm});
            skLineSegment(sketch, "E293", {"start": v(128.22, -27.64) * mm, "end": v(128.57, -27.3) * mm});
            skLineSegment(sketch, "E294", {"start": v(106.46, -24.62) * mm, "end": v(105.5, -24.8) * mm});
            skLineSegment(sketch, "E295", {"start": v(105.5, -24.8) * mm, "end": v(104.9, -24.93) * mm});
            skLineSegment(sketch, "E296", {"start": v(104.9, -24.93) * mm, "end": v(104.69, -24.98) * mm});
            skLineSegment(sketch, "E297", {"start": v(104.69, -24.98) * mm, "end": v(124.58, -23.9) * mm});
            skLineSegment(sketch, "E298", {"start": v(124.58, -23.9) * mm, "end": v(124.47, -24.01) * mm});
            skLineSegment(sketch, "E299", {"start": v(124.47, -24.01) * mm, "end": v(124.18, -24.35) * mm});
            skLineSegment(sketch, "E300", {"start": v(124.18, -24.35) * mm, "end": v(123.72, -24.87) * mm});
            skLineSegment(sketch, "E301", {"start": v(123.72, -24.87) * mm, "end": v(123.12, -25.52) * mm});
            skLineSegment(sketch, "E302", {"start": v(123.12, -25.52) * mm, "end": v(122.39, -26.27) * mm});
            skLineSegment(sketch, "E303", {"start": v(122.39, -26.27) * mm, "end": v(121.56, -27.07) * mm});
            skLineSegment(sketch, "E304", {"start": v(121.56, -27.07) * mm, "end": v(120.65, -27.88) * mm});
            skLineSegment(sketch, "E305", {"start": v(120.65, -27.88) * mm, "end": v(119.93, -28.47) * mm});
            skLineSegment(sketch, "E306", {"start": v(119.93, -28.47) * mm, "end": v(119.69, -28.66) * mm});
            skLineSegment(sketch, "E307", {"start": v(119.69, -28.66) * mm, "end": v(119.34, -28.92) * mm});
            skLineSegment(sketch, "E308", {"start": v(119.34, -28.92) * mm, "end": v(118.24, -29.65) * mm});
            skLineSegment(sketch, "E309", {"start": v(118.24, -29.65) * mm, "end": v(116.9, -30.36) * mm});
            skLineSegment(sketch, "E310", {"start": v(116.9, -30.36) * mm, "end": v(115.67, -30.81) * mm});
            skLineSegment(sketch, "E311", {"start": v(115.67, -30.81) * mm, "end": v(114.85, -31) * mm});
            skLineSegment(sketch, "E312", {"start": v(114.85, -31) * mm, "end": v(114.57, -31.04) * mm});
            skLineSegment(sketch, "E313", {"start": v(114.57, -31.04) * mm, "end": v(114.37, -31.07) * mm});
            skLineSegment(sketch, "E314", {"start": v(114.37, -31.07) * mm, "end": v(113.75, -31.1) * mm});
            skLineSegment(sketch, "E315", {"start": v(113.75, -31.1) * mm, "end": v(112.75, -31.04) * mm});
            skLineSegment(sketch, "E316", {"start": v(112.75, -31.04) * mm, "end": v(111.52, -30.78) * mm});
            skLineSegment(sketch, "E317", {"start": v(111.52, -30.78) * mm, "end": v(110.4, -30.4) * mm});
            skLineSegment(sketch, "E318", {"start": v(110.4, -30.4) * mm, "end": v(110.04, -30.24) * mm});
            skLineSegment(sketch, "E319", {"start": v(110.04, -30.24) * mm, "end": v(109.6, -30.05) * mm});
            skLineSegment(sketch, "E320", {"start": v(109.6, -30.05) * mm, "end": v(108.34, -29.45) * mm});
            skLineSegment(sketch, "E321", {"start": v(108.34, -29.45) * mm, "end": v(106.76, -28.62) * mm});
            skLineSegment(sketch, "E322", {"start": v(106.76, -28.62) * mm, "end": v(105.31, -27.79) * mm});
            skLineSegment(sketch, "E323", {"start": v(105.31, -27.79) * mm, "end": v(104.03, -26.98) * mm});
            skLineSegment(sketch, "E324", {"start": v(104.03, -26.98) * mm, "end": v(102.93, -26.23) * mm});
            skLineSegment(sketch, "E325", {"start": v(102.93, -26.23) * mm, "end": v(102.02, -25.57) * mm});
            skLineSegment(sketch, "E326", {"start": v(102.02, -25.57) * mm, "end": v(101.34, -25.03) * mm});
            skLineSegment(sketch, "E327", {"start": v(101.34, -25.03) * mm, "end": v(101, -24.75) * mm});
            skLineSegment(sketch, "E328", {"start": v(101, -24.75) * mm, "end": v(100.9, -24.65) * mm});
            skLineSegment(sketch, "E329", {"start": v(100.9, -24.65) * mm, "end": v(101.3, -24.53) * mm});
            skLineSegment(sketch, "E330", {"start": v(101.3, -24.53) * mm, "end": v(102.5, -24.18) * mm});
            skLineSegment(sketch, "E331", {"start": v(102.5, -24.18) * mm, "end": v(104.35, -23.71) * mm});
            skLineSegment(sketch, "E332", {"start": v(104.35, -23.71) * mm, "end": v(106.4, -23.24) * mm});
            skLineSegment(sketch, "E333", {"start": v(106.4, -23.24) * mm, "end": v(108.6, -22.77) * mm});
            skLineSegment(sketch, "E334", {"start": v(108.6, -22.77) * mm, "end": v(110.95, -22.3) * mm});
            skLineSegment(sketch, "E335", {"start": v(110.95, -22.3) * mm, "end": v(113.4, -21.85) * mm});
            skLineSegment(sketch, "E336", {"start": v(113.4, -21.85) * mm, "end": v(115.9, -21.41) * mm});
            skLineSegment(sketch, "E337", {"start": v(115.9, -21.41) * mm, "end": v(118.45, -21) * mm});
            skLineSegment(sketch, "E338", {"start": v(118.45, -21) * mm, "end": v(120.98, -20.6) * mm});
            skLineSegment(sketch, "E339", {"start": v(120.98, -20.6) * mm, "end": v(123.49, -20.22) * mm});
            skLineSegment(sketch, "E340", {"start": v(123.49, -20.22) * mm, "end": v(125.92, -19.88) * mm});
            skLineSegment(sketch, "E341", {"start": v(125.92, -19.88) * mm, "end": v(128.25, -19.57) * mm});
            skLineSegment(sketch, "E342", {"start": v(8.18, -27.7) * mm, "end": v(8.53, -27.85) * mm});
            skLineSegment(sketch, "E343", {"start": v(7.16, -27.2) * mm, "end": v(8.18, -27.7) * mm});
            skLineSegment(sketch, "E344", {"start": v(5.98, -26.56) * mm, "end": v(7.16, -27.2) * mm});
            skLineSegment(sketch, "E345", {"start": v(5.08, -25.99) * mm, "end": v(5.98, -26.56) * mm});
            skLineSegment(sketch, "E346", {"start": v(4.67, -25.67) * mm, "end": v(5.08, -25.99) * mm});
            skLineSegment(sketch, "E347", {"start": v(4.57, -25.55) * mm, "end": v(4.67, -25.67) * mm});
            skLineSegment(sketch, "E348", {"start": v(4.49, -25.45) * mm, "end": v(4.57, -25.55) * mm});
            skLineSegment(sketch, "E349", {"start": v(4.27, -25.15) * mm, "end": v(4.49, -25.45) * mm});
            skLineSegment(sketch, "E350", {"start": v(3.9, -24.54) * mm, "end": v(4.27, -25.15) * mm});
            skLineSegment(sketch, "E351", {"start": v(3.46, -23.74) * mm, "end": v(3.9, -24.54) * mm});
            skLineSegment(sketch, "E352", {"start": v(3.11, -23.02) * mm, "end": v(3.46, -23.74) * mm});
            skLineSegment(sketch, "E353", {"start": v(3, -22.78) * mm, "end": v(3.11, -23.02) * mm});
            skLineSegment(sketch, "E354", {"start": v(2.92, -22.57) * mm, "end": v(3, -22.78) * mm});
            skLineSegment(sketch, "E355", {"start": v(2.67, -21.96) * mm, "end": v(2.92, -22.57) * mm});
            skLineSegment(sketch, "E356", {"start": v(2.34, -21.12) * mm, "end": v(2.67, -21.96) * mm});
            skLineSegment(sketch, "E357", {"start": v(2.04, -20.32) * mm, "end": v(2.34, -21.12) * mm});
            skLineSegment(sketch, "E358", {"start": v(1.77, -19.57) * mm, "end": v(2.04, -20.32) * mm});
            skLineSegment(sketch, "E359", {"start": v(1.54, -18.92) * mm, "end": v(1.77, -19.57) * mm});
            skLineSegment(sketch, "E360", {"start": v(1.36, -18.41) * mm, "end": v(1.54, -18.92) * mm});
            skLineSegment(sketch, "E361", {"start": v(1.25, -18.08) * mm, "end": v(1.36, -18.41) * mm});
            skLineSegment(sketch, "E362", {"start": v(1.2, -17.96) * mm, "end": v(1.25, -18.08) * mm});
            skLineSegment(sketch, "E363", {"start": v(1.36, -18.12) * mm, "end": v(1.2, -17.96) * mm});
            skLineSegment(sketch, "E364", {"start": v(1.77, -18.55) * mm, "end": v(1.36, -18.12) * mm});
            skLineSegment(sketch, "E365", {"start": v(2.4, -19.22) * mm, "end": v(1.77, -18.55) * mm});
            skLineSegment(sketch, "E366", {"start": v(3.2, -20.08) * mm, "end": v(2.4, -19.22) * mm});
            skLineSegment(sketch, "E367", {"start": v(4.15, -21.06) * mm, "end": v(3.2, -20.08) * mm});
            skLineSegment(sketch, "E368", {"start": v(5.18, -22.13) * mm, "end": v(4.15, -21.06) * mm});
            skLineSegment(sketch, "E369", {"start": v(6.26, -23.23) * mm, "end": v(5.18, -22.13) * mm});
            skLineSegment(sketch, "E370", {"start": v(7.08, -24.04) * mm, "end": v(6.26, -23.23) * mm});
            skLineSegment(sketch, "E371", {"start": v(7.35, -24.31) * mm, "end": v(7.08, -24.04) * mm});
            skLineSegment(sketch, "E372", {"start": v(7.62, -24.58) * mm, "end": v(7.35, -24.31) * mm});
            skLineSegment(sketch, "E373", {"start": v(8.44, -25.37) * mm, "end": v(7.62, -24.58) * mm});
            skLineSegment(sketch, "E374", {"start": v(9.46, -26.35) * mm, "end": v(8.44, -25.37) * mm});
            skLineSegment(sketch, "E375", {"start": v(10.4, -27.22) * mm, "end": v(9.46, -26.35) * mm});
            skLineSegment(sketch, "E376", {"start": v(11.21, -27.98) * mm, "end": v(10.4, -27.22) * mm});
            skLineSegment(sketch, "E377", {"start": v(11.9, -28.6) * mm, "end": v(11.21, -27.98) * mm});
            skLineSegment(sketch, "E378", {"start": v(12.41, -29.06) * mm, "end": v(11.9, -28.6) * mm});
            skLineSegment(sketch, "E379", {"start": v(12.74, -29.35) * mm, "end": v(12.41, -29.06) * mm});
            skLineSegment(sketch, "E380", {"start": v(12.86, -29.45) * mm, "end": v(12.74, -29.35) * mm});
            skLineSegment(sketch, "E381", {"start": v(12.75, -29.42) * mm, "end": v(12.86, -29.45) * mm});
            skLineSegment(sketch, "E382", {"start": v(12.47, -29.32) * mm, "end": v(12.75, -29.42) * mm});
            skLineSegment(sketch, "E383", {"start": v(12.02, -29.18) * mm, "end": v(12.47, -29.32) * mm});
            skLineSegment(sketch, "E384", {"start": v(11.45, -28.98) * mm, "end": v(12.02, -29.18) * mm});
            skLineSegment(sketch, "E385", {"start": v(10.8, -28.75) * mm, "end": v(11.45, -28.98) * mm});
            skLineSegment(sketch, "E386", {"start": v(10.06, -28.47) * mm, "end": v(10.8, -28.75) * mm});
            skLineSegment(sketch, "E387", {"start": v(9.3, -28.17) * mm, "end": v(10.06, -28.47) * mm});
            skLineSegment(sketch, "E388", {"start": v(8.72, -27.94) * mm, "end": v(9.3, -28.17) * mm});
            skLineSegment(sketch, "E389", {"start": v(8.53, -27.85) * mm, "end": v(8.72, -27.94) * mm});
            skLineSegment(sketch, "E390", {"start": v(26.83, -19.9) * mm, "end": v(27.28, -19.47) * mm});
            skLineSegment(sketch, "E391", {"start": v(25.46, -21.16) * mm, "end": v(26.83, -19.9) * mm});
            skLineSegment(sketch, "E392", {"start": v(23.71, -22.77) * mm, "end": v(25.46, -21.16) * mm});
            skLineSegment(sketch, "E393", {"start": v(22.1, -24.28) * mm, "end": v(23.71, -22.77) * mm});
            skLineSegment(sketch, "E394", {"start": v(20.66, -25.68) * mm, "end": v(22.1, -24.28) * mm});
            skLineSegment(sketch, "E395", {"start": v(19.45, -26.97) * mm, "end": v(20.66, -25.68) * mm});
            skLineSegment(sketch, "E396", {"start": v(18.54, -28.13) * mm, "end": v(19.45, -26.97) * mm});
            skLineSegment(sketch, "E397", {"start": v(17.97, -29.16) * mm, "end": v(18.54, -28.13) * mm});
            skLineSegment(sketch, "E398", {"start": v(17.78, -29.83) * mm, "end": v(17.97, -29.16) * mm});
            skLineSegment(sketch, "E399", {"start": v(17.8, -30.05) * mm, "end": v(17.78, -29.83) * mm});
            skLineSegment(sketch, "E400", {"start": v(17.8, -30.17) * mm, "end": v(17.8, -30.05) * mm});
            skLineSegment(sketch, "E401", {"start": v(17.96, -30.51) * mm, "end": v(17.8, -30.17) * mm});
            skLineSegment(sketch, "E402", {"start": v(18.39, -31.19) * mm, "end": v(17.96, -30.51) * mm});
            skLineSegment(sketch, "E403", {"start": v(19.01, -32) * mm, "end": v(18.39, -31.19) * mm});
            skLineSegment(sketch, "E404", {"start": v(19.78, -32.9) * mm, "end": v(19.01, -32) * mm});
            skLineSegment(sketch, "E405", {"start": v(20.64, -33.84) * mm, "end": v(19.78, -32.9) * mm});
            skLineSegment(sketch, "E406", {"start": v(21.53, -34.75) * mm, "end": v(20.64, -33.84) * mm});
            skLineSegment(sketch, "E407", {"start": v(22.39, -35.58) * mm, "end": v(21.53, -34.75) * mm});
            skLineSegment(sketch, "E408", {"start": v(22.96, -36.1) * mm, "end": v(22.39, -35.58) * mm});
            skLineSegment(sketch, "E409", {"start": v(23.16, -36.26) * mm, "end": v(22.96, -36.1) * mm});
            skLineSegment(sketch, "E410", {"start": v(22.7, -36.12) * mm, "end": v(23.16, -36.26) * mm});
            skLineSegment(sketch, "E411", {"start": v(21.37, -35.56) * mm, "end": v(22.7, -36.12) * mm});
            skLineSegment(sketch, "E412", {"start": v(19.52, -34.55) * mm, "end": v(21.37, -35.56) * mm});
            skLineSegment(sketch, "E413", {"start": v(17.75, -33.32) * mm, "end": v(19.52, -34.55) * mm});
            skLineSegment(sketch, "E414", {"start": v(16.55, -32.31) * mm, "end": v(17.75, -33.32) * mm});
            skLineSegment(sketch, "E415", {"start": v(16.18, -31.94) * mm, "end": v(16.55, -32.31) * mm});
            skLineSegment(sketch, "E416", {"start": v(15.83, -31.6) * mm, "end": v(16.18, -31.94) * mm});
            skLineSegment(sketch, "E417", {"start": v(14.85, -30.48) * mm, "end": v(15.83, -31.6) * mm});
            skLineSegment(sketch, "E418", {"start": v(13.64, -28.92) * mm, "end": v(14.85, -30.48) * mm});
            skLineSegment(sketch, "E419", {"start": v(12.56, -27.38) * mm, "end": v(13.64, -28.92) * mm});
            skLineSegment(sketch, "E420", {"start": v(11.87, -26.33) * mm, "end": v(12.56, -27.38) * mm});
            skLineSegment(sketch, "E421", {"start": v(11.65, -25.98) * mm, "end": v(11.87, -26.33) * mm});
            skLineSegment(sketch, "E422", {"start": v(11.4, -25.6) * mm, "end": v(11.65, -25.98) * mm});
            skLineSegment(sketch, "E423", {"start": v(10.69, -24.46) * mm, "end": v(11.4, -25.6) * mm});
            skLineSegment(sketch, "E424", {"start": v(9.94, -23.3) * mm, "end": v(10.69, -24.46) * mm});
            skLineSegment(sketch, "E425", {"start": v(9.32, -22.54) * mm, "end": v(9.94, -23.3) * mm});
            skLineSegment(sketch, "E426", {"start": v(8.92, -22.23) * mm, "end": v(9.32, -22.54) * mm});
            skLineSegment(sketch, "E427", {"start": v(8.76, -22.19) * mm, "end": v(8.92, -22.23) * mm});
            skLineSegment(sketch, "E428", {"start": v(9, -22.18) * mm, "end": v(8.76, -22.19) * mm});
            skLineSegment(sketch, "E429", {"start": v(9.76, -22.3) * mm, "end": v(9, -22.18) * mm});
            skLineSegment(sketch, "E430", {"start": v(10.94, -22.68) * mm, "end": v(9.76, -22.3) * mm});
            skLineSegment(sketch, "E431", {"start": v(12.23, -23.2) * mm, "end": v(10.94, -22.68) * mm});
            skLineSegment(sketch, "E432", {"start": v(13.55, -23.77) * mm, "end": v(12.23, -23.2) * mm});
            skLineSegment(sketch, "E433", {"start": v(14.82, -24.32) * mm, "end": v(13.55, -23.77) * mm});
            skLineSegment(sketch, "E434", {"start": v(15.95, -24.75) * mm, "end": v(14.82, -24.32) * mm});
            skLineSegment(sketch, "E435", {"start": v(16.86, -24.97) * mm, "end": v(15.95, -24.75) * mm});
            skLineSegment(sketch, "E436", {"start": v(17.36, -24.96) * mm, "end": v(16.86, -24.97) * mm});
            skLineSegment(sketch, "E437", {"start": v(17.48, -24.89) * mm, "end": v(17.36, -24.96) * mm});
            skLineSegment(sketch, "E438", {"start": v(17.64, -24.74) * mm, "end": v(17.48, -24.89) * mm});
            skLineSegment(sketch, "E439", {"start": v(18.12, -24.3) * mm, "end": v(17.64, -24.74) * mm});
            skLineSegment(sketch, "E440", {"start": v(18.88, -23.56) * mm, "end": v(18.12, -24.3) * mm});
            skLineSegment(sketch, "E441", {"start": v(19.74, -22.68) * mm, "end": v(18.88, -23.56) * mm});
            skLineSegment(sketch, "E442", {"start": v(20.67, -21.7) * mm, "end": v(19.74, -22.68) * mm});
            skLineSegment(sketch, "E443", {"start": v(21.67, -20.6) * mm, "end": v(20.67, -21.7) * mm});
            skLineSegment(sketch, "E444", {"start": v(22.7, -19.46) * mm, "end": v(21.67, -20.6) * mm});
            skLineSegment(sketch, "E445", {"start": v(23.75, -18.27) * mm, "end": v(22.7, -19.46) * mm});
            skLineSegment(sketch, "E446", {"start": v(24.54, -17.36) * mm, "end": v(23.75, -18.27) * mm});
            skLineSegment(sketch, "E447", {"start": v(24.8, -17.06) * mm, "end": v(24.54, -17.36) * mm});
            skLineSegment(sketch, "E448", {"start": v(25.1, -16.73) * mm, "end": v(24.8, -17.06) * mm});
            skLineSegment(sketch, "E449", {"start": v(25.94, -15.74) * mm, "end": v(25.1, -16.73) * mm});
            skLineSegment(sketch, "E450", {"start": v(27.03, -14.45) * mm, "end": v(25.94, -15.74) * mm});
            skLineSegment(sketch, "E451", {"start": v(28.05, -13.23) * mm, "end": v(27.03, -14.45) * mm});
            skLineSegment(sketch, "E452", {"start": v(28.97, -12.12) * mm, "end": v(28.05, -13.23) * mm});
            skLineSegment(sketch, "E453", {"start": v(48.8, -11.13) * mm, "end": v(50.53, -10.07) * mm});
            skLineSegment(sketch, "E454", {"start": v(46.92, -12.3) * mm, "end": v(48.8, -11.13) * mm});
            skLineSegment(sketch, "E455", {"start": v(55.24, -4.87) * mm, "end": v(55.2, -4.62) * mm});
            skLineSegment(sketch, "E456", {"start": v(55.2, -4.62) * mm, "end": v(55.11, -4.66) * mm});
            skLineSegment(sketch, "E457", {"start": v(55.11, -4.66) * mm, "end": v(54.84, -4.79) * mm});
            skLineSegment(sketch, "E458", {"start": v(54.84, -4.79) * mm, "end": v(54.27, -5.07) * mm});
            skLineSegment(sketch, "E459", {"start": v(54.27, -5.07) * mm, "end": v(53.51, -5.47) * mm});
            skLineSegment(sketch, "E460", {"start": v(53.51, -5.47) * mm, "end": v(52.58, -5.96) * mm});
            skLineSegment(sketch, "E461", {"start": v(52.58, -5.96) * mm, "end": v(51.5, -6.55) * mm});
            skLineSegment(sketch, "E462", {"start": v(51.5, -6.55) * mm, "end": v(50.29, -7.23) * mm});
            skLineSegment(sketch, "E463", {"start": v(50.29, -7.23) * mm, "end": v(48.95, -7.99) * mm});
            skLineSegment(sketch, "E464", {"start": v(48.95, -7.99) * mm, "end": v(47.88, -8.62) * mm});
            skLineSegment(sketch, "E465", {"start": v(47.88, -8.62) * mm, "end": v(47.52, -8.83) * mm});
            skLineSegment(sketch, "E466", {"start": v(47.52, -8.83) * mm, "end": v(46.87, -9.2) * mm});
            skLineSegment(sketch, "E467", {"start": v(46.87, -9.2) * mm, "end": v(44.95, -10.37) * mm});
            skLineSegment(sketch, "E468", {"start": v(44.95, -10.37) * mm, "end": v(42.21, -12.07) * mm});
            skLineSegment(sketch, "E469", {"start": v(42.21, -12.07) * mm, "end": v(39.36, -13.9) * mm});
            skLineSegment(sketch, "E470", {"start": v(39.36, -13.9) * mm, "end": v(37.18, -15.36) * mm});
            skLineSegment(sketch, "E471", {"start": v(37.18, -15.36) * mm, "end": v(36.46, -15.85) * mm});
            skLineSegment(sketch, "E472", {"start": v(36.46, -15.85) * mm, "end": v(35.68, -16.39) * mm});
            skLineSegment(sketch, "E473", {"start": v(35.68, -16.39) * mm, "end": v(31.99, -19) * mm});
            skLineSegment(sketch, "E474", {"start": v(31.99, -19) * mm, "end": v(28.5, -21.56) * mm});
            skLineSegment(sketch, "E475", {"start": v(28.5, -21.56) * mm, "end": v(27.84, -22.08) * mm});
            skLineSegment(sketch, "E476", {"start": v(27.28, -19.47) * mm, "end": v(27.43, -19.32) * mm});
            skLineSegment(sketch, "E477", {"start": v(27.43, -19.32) * mm, "end": v(27.9, -18.89) * mm});
            skLineSegment(sketch, "E478", {"start": v(27.9, -18.89) * mm, "end": v(28.74, -18.11) * mm});
            skLineSegment(sketch, "E479", {"start": v(28.74, -18.11) * mm, "end": v(29.78, -17.18) * mm});
            skLineSegment(sketch, "E480", {"start": v(29.78, -17.18) * mm, "end": v(31, -16.1) * mm});
            skLineSegment(sketch, "E481", {"start": v(31, -16.1) * mm, "end": v(32.39, -14.9) * mm});
            skLineSegment(sketch, "E482", {"start": v(32.39, -14.9) * mm, "end": v(33.93, -13.63) * mm});
            skLineSegment(sketch, "E483", {"start": v(33.93, -13.63) * mm, "end": v(35.6, -12.29) * mm});
            skLineSegment(sketch, "E484", {"start": v(35.6, -12.29) * mm, "end": v(37.4, -10.9) * mm});
            skLineSegment(sketch, "E485", {"start": v(37.4, -10.9) * mm, "end": v(39.3, -9.5) * mm});
            skLineSegment(sketch, "E486", {"start": v(39.3, -9.5) * mm, "end": v(41.28, -8.12) * mm});
            skLineSegment(sketch, "E487", {"start": v(41.28, -8.12) * mm, "end": v(43.34, -6.77) * mm});
            skLineSegment(sketch, "E488", {"start": v(43.34, -6.77) * mm, "end": v(45.45, -5.48) * mm});
            skLineSegment(sketch, "E489", {"start": v(45.45, -5.48) * mm, "end": v(47.6, -4.28) * mm});
            skLineSegment(sketch, "E490", {"start": v(47.6, -4.28) * mm, "end": v(49.76, -3.2) * mm});
            skLineSegment(sketch, "E491", {"start": v(49.76, -3.2) * mm, "end": v(51.94, -2.24) * mm});
            skLineSegment(sketch, "E492", {"start": v(51.94, -2.24) * mm, "end": v(53.55, -1.63) * mm});
            skLineSegment(sketch, "E493", {"start": v(53.55, -1.63) * mm, "end": v(54.1, -1.45) * mm});
            skLineSegment(sketch, "E494", {"start": v(54.1, -1.45) * mm, "end": v(53.66, -1.44) * mm});
            skLineSegment(sketch, "E495", {"start": v(53.66, -1.44) * mm, "end": v(52.35, -1.44) * mm});
            skLineSegment(sketch, "E496", {"start": v(52.35, -1.44) * mm, "end": v(50.62, -1.52) * mm});
            skLineSegment(sketch, "E497", {"start": v(50.62, -1.52) * mm, "end": v(48.92, -1.69) * mm});
            skLineSegment(sketch, "E498", {"start": v(48.92, -1.69) * mm, "end": v(47.26, -1.93) * mm});
            skLineSegment(sketch, "E499", {"start": v(47.26, -1.93) * mm, "end": v(45.67, -2.22) * mm});
            skLineSegment(sketch, "E500", {"start": v(45.67, -2.22) * mm, "end": v(44.14, -2.56) * mm});
            skLineSegment(sketch, "E501", {"start": v(44.14, -2.56) * mm, "end": v(42.69, -2.93) * mm});
            skLineSegment(sketch, "E502", {"start": v(42.69, -2.93) * mm, "end": v(41.33, -3.32) * mm});
            skLineSegment(sketch, "E503", {"start": v(41.33, -3.32) * mm, "end": v(40.07, -3.72) * mm});
            skLineSegment(sketch, "E504", {"start": v(40.07, -3.72) * mm, "end": v(38.94, -4.11) * mm});
            skLineSegment(sketch, "E505", {"start": v(33.07, -7.51) * mm, "end": v(32.5, -8.07) * mm});
            skLineSegment(sketch, "E506", {"start": v(32.5, -8.07) * mm, "end": v(31.99, -8.59) * mm});
            skLineSegment(sketch, "E507", {"start": v(31.99, -8.59) * mm, "end": v(31.57, -9.02) * mm});
            skLineSegment(sketch, "E508", {"start": v(31.57, -9.02) * mm, "end": v(31.35, -9.26) * mm});
            skLineSegment(sketch, "E509", {"start": v(20.58, -27.92) * mm, "end": v(19.7, -28.68) * mm});
            skLineSegment(sketch, "E510", {"start": v(19.7, -28.68) * mm, "end": v(19.07, -29.25) * mm});
            skLineSegment(sketch, "E511", {"start": v(19.07, -29.25) * mm, "end": v(18.8, -29.5) * mm});
            skLineSegment(sketch, "E512", {"start": v(26.1, -23.43) * mm, "end": v(24.47, -24.71) * mm});
            skLineSegment(sketch, "E513", {"start": v(31.2, -9.43) * mm, "end": v(30.96, -9.72) * mm});
            skLineSegment(sketch, "E514", {"start": v(18.8, -29.5) * mm, "end": v(18.72, -29.6) * mm});
            skLineSegment(sketch, "E515", {"start": v(24.47, -24.71) * mm, "end": v(23, -25.9) * mm});
            skLineSegment(sketch, "E516", {"start": v(30.96, -9.72) * mm, "end": v(30.45, -10.33) * mm});
            skLineSegment(sketch, "E517", {"start": v(18.72, -29.6) * mm, "end": v(18.98, -29.73) * mm});
            skLineSegment(sketch, "E518", {"start": v(23, -25.9) * mm, "end": v(21.69, -26.99) * mm});
            skLineSegment(sketch, "E519", {"start": v(30.45, -10.33) * mm, "end": v(29.78, -11.14) * mm});
            skLineSegment(sketch, "E520", {"start": v(18.98, -29.73) * mm, "end": v(19.81, -30.06) * mm});
            skLineSegment(sketch, "E521", {"start": v(21.69, -26.99) * mm, "end": v(20.58, -27.92) * mm});
            skLineSegment(sketch, "E522", {"start": v(29.78, -11.14) * mm, "end": v(28.97, -12.12) * mm});
            skLineSegment(sketch, "E523", {"start": v(27.84, -22.08) * mm, "end": v(27.4, -22.41) * mm});
            skLineSegment(sketch, "E524", {"start": v(19.81, -30.06) * mm, "end": v(21.27, -30.53) * mm});
            skLineSegment(sketch, "E525", {"start": v(21.27, -30.53) * mm, "end": v(23.04, -31) * mm});
            skLineSegment(sketch, "E526", {"start": v(34.24, -32.63) * mm, "end": v(34.53, -32.65) * mm});
            skLineSegment(sketch, "E527", {"start": v(34.53, -32.65) * mm, "end": v(35.38, -32.68) * mm});
            skLineSegment(sketch, "E528", {"start": v(35.38, -32.68) * mm, "end": v(36.56, -32.7) * mm});
            skLineSegment(sketch, "E529", {"start": v(36.56, -32.7) * mm, "end": v(37.72, -32.69) * mm});
            skLineSegment(sketch, "E530", {"start": v(33.66, -32.6) * mm, "end": v(34.24, -32.63) * mm});
            skLineSegment(sketch, "E531", {"start": v(31.9, -32.45) * mm, "end": v(33.66, -32.6) * mm});
            skLineSegment(sketch, "E532", {"start": v(29.55, -32.18) * mm, "end": v(31.9, -32.45) * mm});
            skLineSegment(sketch, "E533", {"start": v(27.24, -31.84) * mm, "end": v(29.55, -32.18) * mm});
            skLineSegment(sketch, "E534", {"start": v(25.05, -31.43) * mm, "end": v(27.24, -31.84) * mm});
            skLineSegment(sketch, "E535", {"start": v(23.04, -31) * mm, "end": v(25.05, -31.43) * mm});
            skLineSegment(sketch, "E536", {"start": v(31.28, -9.34) * mm, "end": v(31.2, -9.43) * mm});
            skLineSegment(sketch, "E537", {"start": v(27.4, -22.41) * mm, "end": v(26.1, -23.43) * mm});
            skLineSegment(sketch, "E538", {"start": v(33.66, -6.95) * mm, "end": v(33.07, -7.51) * mm});
            skLineSegment(sketch, "E539", {"start": v(31.35, -9.26) * mm, "end": v(31.28, -9.34) * mm});
            skLineSegment(sketch, "E540", {"start": v(34.25, -6.44) * mm, "end": v(33.66, -6.95) * mm});
            skLineSegment(sketch, "E541", {"start": v(34.78, -6) * mm, "end": v(34.25, -6.44) * mm});
            skLineSegment(sketch, "E542", {"start": v(35.1, -5.75) * mm, "end": v(34.78, -6) * mm});
            skLineSegment(sketch, "E543", {"start": v(35.22, -5.68) * mm, "end": v(35.1, -5.75) * mm});
            skLineSegment(sketch, "E544", {"start": v(35.26, -5.65) * mm, "end": v(35.22, -5.68) * mm});
            skLineSegment(sketch, "E545", {"start": v(35.4, -5.57) * mm, "end": v(35.26, -5.65) * mm});
            skLineSegment(sketch, "E546", {"start": v(35.79, -5.4) * mm, "end": v(35.4, -5.57) * mm});
            skLineSegment(sketch, "E547", {"start": v(36.34, -5.14) * mm, "end": v(35.79, -5.4) * mm});
            skLineSegment(sketch, "E548", {"start": v(37.06, -4.84) * mm, "end": v(36.34, -5.14) * mm});
            skLineSegment(sketch, "E549", {"start": v(37.93, -4.49) * mm, "end": v(37.06, -4.84) * mm});
            skLineSegment(sketch, "E550", {"start": v(38.94, -4.11) * mm, "end": v(37.93, -4.49) * mm});
            skLineSegment(sketch, "E551", {"start": v(55.2, -5.63) * mm, "end": v(55.24, -4.87) * mm});
            skLineSegment(sketch, "E552", {"start": v(54.9, -6.66) * mm, "end": v(55.2, -5.63) * mm});
            skLineSegment(sketch, "E553", {"start": v(54.34, -7.6) * mm, "end": v(54.9, -6.66) * mm});
            skLineSegment(sketch, "E554", {"start": v(53.71, -8.2) * mm, "end": v(54.34, -7.6) * mm});
            skLineSegment(sketch, "E555", {"start": v(53.47, -8.33) * mm, "end": v(53.71, -8.2) * mm});
            skLineSegment(sketch, "E556", {"start": v(53.13, -8.52) * mm, "end": v(53.47, -8.33) * mm});
            skLineSegment(sketch, "E557", {"start": v(52.1, -9.13) * mm, "end": v(53.13, -8.52) * mm});
            skLineSegment(sketch, "E558", {"start": v(50.53, -10.07) * mm, "end": v(52.1, -9.13) * mm});
            skLineSegment(sketch, "E559", {"start": v(30.36, -25.32) * mm, "end": v(29.3, -26.1) * mm});
            skLineSegment(sketch, "E560", {"start": v(31.65, -24.39) * mm, "end": v(30.36, -25.32) * mm});
            skLineSegment(sketch, "E561", {"start": v(33.15, -23.31) * mm, "end": v(31.65, -24.39) * mm});
            skLineSegment(sketch, "E562", {"start": v(34.83, -22.12) * mm, "end": v(33.15, -23.31) * mm});
            skLineSegment(sketch, "E563", {"start": v(36.65, -20.83) * mm, "end": v(34.83, -22.12) * mm});
            skLineSegment(sketch, "E564", {"start": v(38.6, -19.48) * mm, "end": v(36.65, -20.83) * mm});
            skLineSegment(sketch, "E565", {"start": v(40.62, -18.08) * mm, "end": v(38.6, -19.48) * mm});
            skLineSegment(sketch, "E566", {"start": v(42.72, -16.66) * mm, "end": v(40.62, -18.08) * mm});
            skLineSegment(sketch, "E567", {"start": v(44.84, -15.25) * mm, "end": v(42.72, -16.66) * mm});
            skLineSegment(sketch, "E568", {"start": v(46.97, -13.87) * mm, "end": v(44.84, -15.25) * mm});
            skLineSegment(sketch, "E569", {"start": v(49.07, -12.55) * mm, "end": v(46.97, -13.87) * mm});
            skLineSegment(sketch, "E570", {"start": v(51.1, -11.3) * mm, "end": v(49.07, -12.55) * mm});
            skLineSegment(sketch, "E571", {"start": v(52.57, -10.44) * mm, "end": v(51.1, -11.3) * mm});
            skLineSegment(sketch, "E572", {"start": v(53.07, -10.16) * mm, "end": v(52.57, -10.44) * mm});
            skLineSegment(sketch, "E573", {"start": v(53.06, -10.3) * mm, "end": v(53.07, -10.16) * mm});
            skLineSegment(sketch, "E574", {"start": v(53, -10.7) * mm, "end": v(53.06, -10.3) * mm});
            skLineSegment(sketch, "E575", {"start": v(52.84, -11.47) * mm, "end": v(53, -10.7) * mm});
            skLineSegment(sketch, "E576", {"start": v(52.6, -12.44) * mm, "end": v(52.84, -11.47) * mm});
            skLineSegment(sketch, "E577", {"start": v(52.3, -13.57) * mm, "end": v(52.6, -12.44) * mm});
            skLineSegment(sketch, "E578", {"start": v(51.92, -14.85) * mm, "end": v(52.3, -13.57) * mm});
            skLineSegment(sketch, "E579", {"start": v(51.5, -16.23) * mm, "end": v(51.92, -14.85) * mm});
            skLineSegment(sketch, "E580", {"start": v(51, -17.68) * mm, "end": v(51.5, -16.23) * mm});
            skLineSegment(sketch, "E581", {"start": v(50.61, -18.8) * mm, "end": v(51, -17.68) * mm});
            skLineSegment(sketch, "E582", {"start": v(50.48, -19.18) * mm, "end": v(50.61, -18.8) * mm});
            skLineSegment(sketch, "E583", {"start": v(42.45, -31.97) * mm, "end": v(43.03, -31.56) * mm});
            skLineSegment(sketch, "E584", {"start": v(42.01, -32.22) * mm, "end": v(42.45, -31.97) * mm});
            skLineSegment(sketch, "E585", {"start": v(41.8, -32.32) * mm, "end": v(42.01, -32.22) * mm});
            skLineSegment(sketch, "E586", {"start": v(41.74, -32.34) * mm, "end": v(41.8, -32.32) * mm});
            skLineSegment(sketch, "E587", {"start": v(41.64, -32.38) * mm, "end": v(41.74, -32.34) * mm});
            skLineSegment(sketch, "E588", {"start": v(41.33, -32.44) * mm, "end": v(41.64, -32.38) * mm});
            skLineSegment(sketch, "E589", {"start": v(37.72, -32.69) * mm, "end": v(38.83, -32.65) * mm});
            skLineSegment(sketch, "E590", {"start": v(38.83, -32.65) * mm, "end": v(39.83, -32.6) * mm});
            skLineSegment(sketch, "E591", {"start": v(39.83, -32.6) * mm, "end": v(40.68, -32.53) * mm});
            skLineSegment(sketch, "E592", {"start": v(40.68, -32.53) * mm, "end": v(41.33, -32.44) * mm});
            skLineSegment(sketch, "E593", {"start": v(43.03, -31.56) * mm, "end": v(43.73, -30.96) * mm});
            skLineSegment(sketch, "E594", {"start": v(43.73, -30.96) * mm, "end": v(44.53, -30.15) * mm});
            skLineSegment(sketch, "E595", {"start": v(44.53, -30.15) * mm, "end": v(45.4, -29.1) * mm});
            skLineSegment(sketch, "E596", {"start": v(45.4, -29.1) * mm, "end": v(46.32, -27.77) * mm});
            skLineSegment(sketch, "E597", {"start": v(46.32, -27.77) * mm, "end": v(47.05, -26.56) * mm});
            skLineSegment(sketch, "E598", {"start": v(47.05, -26.56) * mm, "end": v(47.27, -26.15) * mm});
            skLineSegment(sketch, "E599", {"start": v(47.27, -26.15) * mm, "end": v(47.48, -25.75) * mm});
            skLineSegment(sketch, "E600", {"start": v(47.48, -25.75) * mm, "end": v(48.1, -24.55) * mm});
            skLineSegment(sketch, "E601", {"start": v(48.1, -24.55) * mm, "end": v(48.94, -22.83) * mm});
            skLineSegment(sketch, "E602", {"start": v(48.94, -22.83) * mm, "end": v(49.75, -21.02) * mm});
            skLineSegment(sketch, "E603", {"start": v(49.75, -21.02) * mm, "end": v(50.3, -19.64) * mm});
            skLineSegment(sketch, "E604", {"start": v(50.3, -19.64) * mm, "end": v(50.48, -19.18) * mm});
            skLineSegment(sketch, "E605", {"start": v(29.3, -26.1) * mm, "end": v(28.52, -26.68) * mm});
            skLineSegment(sketch, "E606", {"start": v(28.52, -26.68) * mm, "end": v(28.02, -27.04) * mm});
            skLineSegment(sketch, "E607", {"start": v(28.02, -27.04) * mm, "end": v(27.85, -27.17) * mm});
            skLineSegment(sketch, "E608", {"start": v(27.85, -27.17) * mm, "end": v(45.42, -17.78) * mm});
            skLineSegment(sketch, "E609", {"start": v(45.42, -17.78) * mm, "end": v(45.38, -17.94) * mm});
            skLineSegment(sketch, "E610", {"start": v(45.38, -17.94) * mm, "end": v(45.26, -18.37) * mm});
            skLineSegment(sketch, "E611", {"start": v(45.26, -18.37) * mm, "end": v(45.06, -19.03) * mm});
            skLineSegment(sketch, "E612", {"start": v(45.06, -19.03) * mm, "end": v(44.79, -19.88) * mm});
            skLineSegment(sketch, "E613", {"start": v(44.79, -19.88) * mm, "end": v(44.44, -20.86) * mm});
            skLineSegment(sketch, "E614", {"start": v(44.44, -20.86) * mm, "end": v(44.03, -21.94) * mm});
            skLineSegment(sketch, "E615", {"start": v(44.03, -21.94) * mm, "end": v(43.55, -23.06) * mm});
            skLineSegment(sketch, "E616", {"start": v(43.55, -23.06) * mm, "end": v(43.15, -23.9) * mm});
            skLineSegment(sketch, "E617", {"start": v(43.15, -23.9) * mm, "end": v(43, -24.17) * mm});
            skLineSegment(sketch, "E618", {"start": v(43, -24.17) * mm, "end": v(42.8, -24.56) * mm});
            skLineSegment(sketch, "E619", {"start": v(42.8, -24.56) * mm, "end": v(42.11, -25.68) * mm});
            skLineSegment(sketch, "E620", {"start": v(42.11, -25.68) * mm, "end": v(41.2, -26.89) * mm});
            skLineSegment(sketch, "E621", {"start": v(41.2, -26.89) * mm, "end": v(40.27, -27.82) * mm});
            skLineSegment(sketch, "E622", {"start": v(40.27, -27.82) * mm, "end": v(39.61, -28.34) * mm});
            skLineSegment(sketch, "E623", {"start": v(39.61, -28.34) * mm, "end": v(39.37, -28.5) * mm});
            skLineSegment(sketch, "E624", {"start": v(39.37, -28.5) * mm, "end": v(39.2, -28.6) * mm});
            skLineSegment(sketch, "E625", {"start": v(39.2, -28.6) * mm, "end": v(38.66, -28.89) * mm});
            skLineSegment(sketch, "E626", {"start": v(38.66, -28.89) * mm, "end": v(37.72, -29.26) * mm});
            skLineSegment(sketch, "E627", {"start": v(37.72, -29.26) * mm, "end": v(36.5, -29.54) * mm});
            skLineSegment(sketch, "E628", {"start": v(36.5, -29.54) * mm, "end": v(35.32, -29.67) * mm});
            skLineSegment(sketch, "E629", {"start": v(35.32, -29.67) * mm, "end": v(34.92, -29.68) * mm});
            skLineSegment(sketch, "E630", {"start": v(34.92, -29.68) * mm, "end": v(34.46, -29.7) * mm});
            skLineSegment(sketch, "E631", {"start": v(34.46, -29.7) * mm, "end": v(33.05, -29.68) * mm});
            skLineSegment(sketch, "E632", {"start": v(33.05, -29.68) * mm, "end": v(31.27, -29.6) * mm});
            skLineSegment(sketch, "E633", {"start": v(31.27, -29.6) * mm, "end": v(29.6, -29.45) * mm});
            skLineSegment(sketch, "E634", {"start": v(29.6, -29.45) * mm, "end": v(28.1, -29.26) * mm});
            skLineSegment(sketch, "E635", {"start": v(28.1, -29.26) * mm, "end": v(26.79, -29.05) * mm});
            skLineSegment(sketch, "E636", {"start": v(26.79, -29.05) * mm, "end": v(25.69, -28.84) * mm});
            skLineSegment(sketch, "E637", {"start": v(25.69, -28.84) * mm, "end": v(24.84, -28.64) * mm});
            skLineSegment(sketch, "E638", {"start": v(24.84, -28.64) * mm, "end": v(24.42, -28.53) * mm});
            skLineSegment(sketch, "E639", {"start": v(24.42, -28.53) * mm, "end": v(24.28, -28.48) * mm});
            skLineSegment(sketch, "E640", {"start": v(24.28, -28.48) * mm, "end": v(24.59, -28.2) * mm});
            skLineSegment(sketch, "E641", {"start": v(24.59, -28.2) * mm, "end": v(25.54, -27.38) * mm});
            skLineSegment(sketch, "E642", {"start": v(25.54, -27.38) * mm, "end": v(27.01, -26.17) * mm});
            skLineSegment(sketch, "E643", {"start": v(27.01, -26.17) * mm, "end": v(28.67, -24.87) * mm});
            skLineSegment(sketch, "E644", {"start": v(28.67, -24.87) * mm, "end": v(30.48, -23.51) * mm});
            skLineSegment(sketch, "E645", {"start": v(30.48, -23.51) * mm, "end": v(32.4, -22.1) * mm});
            skLineSegment(sketch, "E646", {"start": v(32.4, -22.1) * mm, "end": v(34.43, -20.66) * mm});
            skLineSegment(sketch, "E647", {"start": v(34.43, -20.66) * mm, "end": v(36.52, -19.2) * mm});
            skLineSegment(sketch, "E648", {"start": v(36.52, -19.2) * mm, "end": v(38.64, -17.75) * mm});
            skLineSegment(sketch, "E649", {"start": v(38.64, -17.75) * mm, "end": v(40.77, -16.31) * mm});
            skLineSegment(sketch, "E650", {"start": v(40.77, -16.31) * mm, "end": v(42.88, -14.92) * mm});
            skLineSegment(sketch, "E651", {"start": v(42.88, -14.92) * mm, "end": v(44.94, -13.58) * mm});
            skLineSegment(sketch, "E652", {"start": v(44.94, -13.58) * mm, "end": v(46.92, -12.3) * mm});
            skLineSegment(sketch, "E653", {"start": v(-33.33, -55.43) * mm, "end": v(-33.11, -55.75) * mm});
            skLineSegment(sketch, "E654", {"start": v(-33.92, -54.46) * mm, "end": v(-33.33, -55.43) * mm});
            skLineSegment(sketch, "E655", {"start": v(-34.56, -53.28) * mm, "end": v(-33.92, -54.46) * mm});
            skLineSegment(sketch, "E656", {"start": v(-35, -52.31) * mm, "end": v(-34.56, -53.28) * mm});
            skLineSegment(sketch, "E657", {"start": v(-35.18, -51.81) * mm, "end": v(-35, -52.31) * mm});
            skLineSegment(sketch, "E658", {"start": v(-35.2, -51.66) * mm, "end": v(-35.18, -51.81) * mm});
            skLineSegment(sketch, "E659", {"start": v(-35.22, -51.54) * mm, "end": v(-35.2, -51.66) * mm});
            skLineSegment(sketch, "E660", {"start": v(-35.23, -51.17) * mm, "end": v(-35.22, -51.54) * mm});
            skLineSegment(sketch, "E661", {"start": v(-35.22, -50.45) * mm, "end": v(-35.23, -51.17) * mm});
            skLineSegment(sketch, "E662", {"start": v(-35.15, -49.54) * mm, "end": v(-35.22, -50.45) * mm});
            skLineSegment(sketch, "E663", {"start": v(-35.05, -48.75) * mm, "end": v(-35.15, -49.54) * mm});
            skLineSegment(sketch, "E664", {"start": v(-35, -48.49) * mm, "end": v(-35.05, -48.75) * mm});
            skLineSegment(sketch, "E665", {"start": v(-34.97, -48.27) * mm, "end": v(-35, -48.49) * mm});
            skLineSegment(sketch, "E666", {"start": v(-34.85, -47.61) * mm, "end": v(-34.97, -48.27) * mm});
            skLineSegment(sketch, "E667", {"start": v(-34.68, -46.74) * mm, "end": v(-34.85, -47.61) * mm});
            skLineSegment(sketch, "E668", {"start": v(-34.5, -45.9) * mm, "end": v(-34.68, -46.74) * mm});
            skLineSegment(sketch, "E669", {"start": v(-34.32, -45.12) * mm, "end": v(-34.5, -45.9) * mm});
            skLineSegment(sketch, "E670", {"start": v(-34.16, -44.45) * mm, "end": v(-34.32, -45.12) * mm});
            skLineSegment(sketch, "E671", {"start": v(-34.03, -43.93) * mm, "end": v(-34.16, -44.45) * mm});
            skLineSegment(sketch, "E672", {"start": v(-33.94, -43.58) * mm, "end": v(-34.03, -43.93) * mm});
            skLineSegment(sketch, "E673", {"start": v(-33.91, -43.46) * mm, "end": v(-33.94, -43.58) * mm});
            skLineSegment(sketch, "E674", {"start": v(-33.88, -43.67) * mm, "end": v(-33.91, -43.46) * mm});
            skLineSegment(sketch, "E675", {"start": v(-33.77, -44.27) * mm, "end": v(-33.88, -43.67) * mm});
            skLineSegment(sketch, "E676", {"start": v(-33.6, -45.17) * mm, "end": v(-33.77, -44.27) * mm});
            skLineSegment(sketch, "E677", {"start": v(-33.38, -46.33) * mm, "end": v(-33.6, -45.17) * mm});
            skLineSegment(sketch, "E678", {"start": v(-33.12, -47.66) * mm, "end": v(-33.38, -46.33) * mm});
            skLineSegment(sketch, "E679", {"start": v(-32.83, -49.12) * mm, "end": v(-33.12, -47.66) * mm});
            skLineSegment(sketch, "E680", {"start": v(-32.52, -50.63) * mm, "end": v(-32.83, -49.12) * mm});
            skLineSegment(sketch, "E681", {"start": v(-32.28, -51.76) * mm, "end": v(-32.52, -50.63) * mm});
            skLineSegment(sketch, "E682", {"start": v(-32.2, -52.13) * mm, "end": v(-32.28, -51.76) * mm});
            skLineSegment(sketch, "E683", {"start": v(-32.11, -52.5) * mm, "end": v(-32.2, -52.13) * mm});
            skLineSegment(sketch, "E684", {"start": v(-31.85, -53.6) * mm, "end": v(-32.11, -52.5) * mm});
            skLineSegment(sketch, "E685", {"start": v(-31.52, -54.98) * mm, "end": v(-31.85, -53.6) * mm});
            skLineSegment(sketch, "E686", {"start": v(-31.2, -56.22) * mm, "end": v(-31.52, -54.98) * mm});
            skLineSegment(sketch, "E687", {"start": v(-30.93, -57.3) * mm, "end": v(-31.2, -56.22) * mm});
            skLineSegment(sketch, "E688", {"start": v(-30.7, -58.19) * mm, "end": v(-30.93, -57.3) * mm});
            skLineSegment(sketch, "E689", {"start": v(-30.5, -58.86) * mm, "end": v(-30.7, -58.19) * mm});
            skLineSegment(sketch, "E690", {"start": v(-30.39, -59.28) * mm, "end": v(-30.5, -58.86) * mm});
            skLineSegment(sketch, "E691", {"start": v(-30.34, -59.43) * mm, "end": v(-30.39, -59.28) * mm});
            skLineSegment(sketch, "E692", {"start": v(-30.41, -59.35) * mm, "end": v(-30.34, -59.43) * mm});
            skLineSegment(sketch, "E693", {"start": v(-30.6, -59.11) * mm, "end": v(-30.41, -59.35) * mm});
            skLineSegment(sketch, "E694", {"start": v(-30.9, -58.75) * mm, "end": v(-30.6, -59.11) * mm});
            skLineSegment(sketch, "E695", {"start": v(-31.27, -58.28) * mm, "end": v(-30.9, -58.75) * mm});
            skLineSegment(sketch, "E696", {"start": v(-31.7, -57.72) * mm, "end": v(-31.27, -58.28) * mm});
            skLineSegment(sketch, "E697", {"start": v(-32.16, -57.1) * mm, "end": v(-31.7, -57.72) * mm});
            skLineSegment(sketch, "E698", {"start": v(-32.64, -56.43) * mm, "end": v(-32.16, -57.1) * mm});
            skLineSegment(sketch, "E699", {"start": v(-33, -55.92) * mm, "end": v(-32.64, -56.43) * mm});
            skLineSegment(sketch, "E700", {"start": v(-33.11, -55.75) * mm, "end": v(-33, -55.92) * mm});
            skLineSegment(sketch, "E701", {"start": v(-13.43, -58.96) * mm, "end": v(-12.82, -58.85) * mm});
            skLineSegment(sketch, "E702", {"start": v(-15.26, -59.29) * mm, "end": v(-13.43, -58.96) * mm});
            skLineSegment(sketch, "E703", {"start": v(-17.6, -59.7) * mm, "end": v(-15.26, -59.29) * mm});
            skLineSegment(sketch, "E704", {"start": v(-19.78, -60.09) * mm, "end": v(-17.6, -59.7) * mm});
            skLineSegment(sketch, "E705", {"start": v(-21.75, -60.49) * mm, "end": v(-19.78, -60.09) * mm});
            skLineSegment(sketch, "E706", {"start": v(-23.46, -60.92) * mm, "end": v(-21.75, -60.49) * mm});
            skLineSegment(sketch, "E707", {"start": v(-24.85, -61.4) * mm, "end": v(-23.46, -60.92) * mm});
            skLineSegment(sketch, "E708", {"start": v(-25.89, -61.96) * mm, "end": v(-24.85, -61.4) * mm});
            skLineSegment(sketch, "E709", {"start": v(-26.4, -62.42) * mm, "end": v(-25.89, -61.96) * mm});
            skLineSegment(sketch, "E710", {"start": v(-26.52, -62.6) * mm, "end": v(-26.4, -62.42) * mm});
            skLineSegment(sketch, "E711", {"start": v(-26.57, -62.71) * mm, "end": v(-26.52, -62.6) * mm});
            skLineSegment(sketch, "E712", {"start": v(-26.63, -63.1) * mm, "end": v(-26.57, -62.71) * mm});
            skLineSegment(sketch, "E713", {"start": v(-26.63, -63.89) * mm, "end": v(-26.63, -63.1) * mm});
            skLineSegment(sketch, "E714", {"start": v(-26.55, -64.91) * mm, "end": v(-26.63, -63.89) * mm});
            skLineSegment(sketch, "E715", {"start": v(-26.4, -66.09) * mm, "end": v(-26.55, -64.91) * mm});
            skLineSegment(sketch, "E716", {"start": v(-26.18, -67.34) * mm, "end": v(-26.4, -66.09) * mm});
            skLineSegment(sketch, "E717", {"start": v(-25.93, -68.59) * mm, "end": v(-26.18, -67.34) * mm});
            skLineSegment(sketch, "E718", {"start": v(-25.65, -69.75) * mm, "end": v(-25.93, -68.59) * mm});
            skLineSegment(sketch, "E719", {"start": v(-25.45, -70.5) * mm, "end": v(-25.65, -69.75) * mm});
            skLineSegment(sketch, "E720", {"start": v(-25.37, -70.74) * mm, "end": v(-25.45, -70.5) * mm});
            skLineSegment(sketch, "E721", {"start": v(-25.68, -70.37) * mm, "end": v(-25.37, -70.74) * mm});
            skLineSegment(sketch, "E722", {"start": v(-26.5, -69.18) * mm, "end": v(-25.68, -70.37) * mm});
            skLineSegment(sketch, "E723", {"start": v(-27.5, -67.33) * mm, "end": v(-26.5, -69.18) * mm});
            skLineSegment(sketch, "E724", {"start": v(-28.33, -65.34) * mm, "end": v(-27.5, -67.33) * mm});
            skLineSegment(sketch, "E725", {"start": v(-28.8, -63.84) * mm, "end": v(-28.33, -65.34) * mm});
            skLineSegment(sketch, "E726", {"start": v(-28.9, -63.33) * mm, "end": v(-28.8, -63.84) * mm});
            skLineSegment(sketch, "E727", {"start": v(-29, -62.84) * mm, "end": v(-28.9, -63.33) * mm});
            skLineSegment(sketch, "E728", {"start": v(-29.23, -61.38) * mm, "end": v(-29, -62.84) * mm});
            skLineSegment(sketch, "E729", {"start": v(-29.4, -59.4) * mm, "end": v(-29.23, -61.38) * mm});
            skLineSegment(sketch, "E730", {"start": v(-29.47, -57.53) * mm, "end": v(-29.4, -59.4) * mm});
            skLineSegment(sketch, "E731", {"start": v(-29.48, -56.28) * mm, "end": v(-29.47, -57.53) * mm});
            skLineSegment(sketch, "E732", {"start": v(-29.48, -55.86) * mm, "end": v(-29.48, -56.28) * mm});
            skLineSegment(sketch, "E733", {"start": v(-29.48, -55.4) * mm, "end": v(-29.48, -55.86) * mm});
            skLineSegment(sketch, "E734", {"start": v(-29.46, -54.06) * mm, "end": v(-29.48, -55.4) * mm});
            skLineSegment(sketch, "E735", {"start": v(-29.47, -52.69) * mm, "end": v(-29.46, -54.06) * mm});
            skLineSegment(sketch, "E736", {"start": v(-29.57, -51.71) * mm, "end": v(-29.47, -52.69) * mm});
            skLineSegment(sketch, "E737", {"start": v(-29.75, -51.23) * mm, "end": v(-29.57, -51.71) * mm});
            skLineSegment(sketch, "E738", {"start": v(-29.85, -51.1) * mm, "end": v(-29.75, -51.23) * mm});
            skLineSegment(sketch, "E739", {"start": v(-29.64, -51.24) * mm, "end": v(-29.85, -51.1) * mm});
            skLineSegment(sketch, "E740", {"start": v(-29.09, -51.75) * mm, "end": v(-29.64, -51.24) * mm});
            skLineSegment(sketch, "E741", {"start": v(-28.29, -52.7) * mm, "end": v(-29.09, -51.75) * mm});
            skLineSegment(sketch, "E742", {"start": v(-27.48, -53.83) * mm, "end": v(-28.29, -52.7) * mm});
            skLineSegment(sketch, "E743", {"start": v(-26.68, -55.03) * mm, "end": v(-27.48, -53.83) * mm});
            skLineSegment(sketch, "E744", {"start": v(-25.92, -56.18) * mm, "end": v(-26.68, -55.03) * mm});
            skLineSegment(sketch, "E745", {"start": v(-25.2, -57.15) * mm, "end": v(-25.92, -56.18) * mm});
            skLineSegment(sketch, "E746", {"start": v(-24.55, -57.83) * mm, "end": v(-25.2, -57.15) * mm});
            skLineSegment(sketch, "E747", {"start": v(-24.13, -58.1) * mm, "end": v(-24.55, -57.83) * mm});
            skLineSegment(sketch, "E748", {"start": v(-23.99, -58.1) * mm, "end": v(-24.13, -58.1) * mm});
            skLineSegment(sketch, "E749", {"start": v(-23.77, -58.07) * mm, "end": v(-23.99, -58.1) * mm});
            skLineSegment(sketch, "E750", {"start": v(-23.13, -57.95) * mm, "end": v(-23.77, -58.07) * mm});
            skLineSegment(sketch, "E751", {"start": v(-22.1, -57.74) * mm, "end": v(-23.13, -57.95) * mm});
            skLineSegment(sketch, "E752", {"start": v(-20.9, -57.47) * mm, "end": v(-22.1, -57.74) * mm});
            skLineSegment(sketch, "E753", {"start": v(-19.57, -57.14) * mm, "end": v(-20.9, -57.47) * mm});
            skLineSegment(sketch, "E754", {"start": v(-18.15, -56.77) * mm, "end": v(-19.57, -57.14) * mm});
            skLineSegment(sketch, "E755", {"start": v(-16.66, -56.36) * mm, "end": v(-18.15, -56.77) * mm});
            skLineSegment(sketch, "E756", {"start": v(-15.13, -55.93) * mm, "end": v(-16.66, -56.36) * mm});
            skLineSegment(sketch, "E757", {"start": v(-13.97, -55.6) * mm, "end": v(-15.13, -55.93) * mm});
            skLineSegment(sketch, "E758", {"start": v(-13.59, -55.48) * mm, "end": v(-13.97, -55.6) * mm});
            skLineSegment(sketch, "E759", {"start": v(-13.17, -55.36) * mm, "end": v(-13.59, -55.48) * mm});
            skLineSegment(sketch, "E760", {"start": v(-11.92, -54.99) * mm, "end": v(-13.17, -55.36) * mm});
            skLineSegment(sketch, "E761", {"start": v(-10.3, -54.5) * mm, "end": v(-11.92, -54.99) * mm});
            skLineSegment(sketch, "E762", {"start": v(-8.8, -54.02) * mm, "end": v(-10.3, -54.5) * mm});
            skLineSegment(sketch, "E763", {"start": v(-7.41, -53.6) * mm, "end": v(-8.8, -54.02) * mm});
            skLineSegment(sketch, "E764", {"start": v(9.78, -63.5) * mm, "end": v(11.82, -63.53) * mm});
            skLineSegment(sketch, "E765", {"start": v(7.57, -63.47) * mm, "end": v(9.78, -63.5) * mm});
            skLineSegment(sketch, "E766", {"start": v(18.6, -61.71) * mm, "end": v(18.7, -61.49) * mm});
            skLineSegment(sketch, "E767", {"start": v(18.7, -61.49) * mm, "end": v(18.6, -61.47) * mm});
            skLineSegment(sketch, "E768", {"start": v(18.6, -61.47) * mm, "end": v(18.3, -61.43) * mm});
            skLineSegment(sketch, "E769", {"start": v(18.3, -61.43) * mm, "end": v(17.67, -61.36) * mm});
            skLineSegment(sketch, "E770", {"start": v(17.67, -61.36) * mm, "end": v(16.82, -61.28) * mm});
            skLineSegment(sketch, "E771", {"start": v(16.82, -61.28) * mm, "end": v(15.77, -61.2) * mm});
            skLineSegment(sketch, "E772", {"start": v(15.77, -61.2) * mm, "end": v(14.55, -61.1) * mm});
            skLineSegment(sketch, "E773", {"start": v(14.55, -61.1) * mm, "end": v(13.16, -61.02) * mm});
            skLineSegment(sketch, "E774", {"start": v(13.16, -61.02) * mm, "end": v(11.62, -60.94) * mm});
            skLineSegment(sketch, "E775", {"start": v(11.62, -60.94) * mm, "end": v(10.38, -60.88) * mm});
            skLineSegment(sketch, "E776", {"start": v(10.38, -60.88) * mm, "end": v(9.96, -60.86) * mm});
            skLineSegment(sketch, "E777", {"start": v(9.96, -60.86) * mm, "end": v(9.21, -60.83) * mm});
            skLineSegment(sketch, "E778", {"start": v(9.21, -60.83) * mm, "end": v(6.97, -60.77) * mm});
            skLineSegment(sketch, "E779", {"start": v(6.97, -60.77) * mm, "end": v(3.74, -60.72) * mm});
            skLineSegment(sketch, "E780", {"start": v(3.74, -60.72) * mm, "end": v(0.35, -60.72) * mm});
            skLineSegment(sketch, "E781", {"start": v(0.35, -60.72) * mm, "end": v(-2.26, -60.76) * mm});
            skLineSegment(sketch, "E782", {"start": v(-2.26, -60.76) * mm, "end": v(-3.14, -60.78) * mm});
            skLineSegment(sketch, "E783", {"start": v(-3.14, -60.78) * mm, "end": v(-4.08, -60.8) * mm});
            skLineSegment(sketch, "E784", {"start": v(-4.08, -60.8) * mm, "end": v(-8.6, -61) * mm});
            skLineSegment(sketch, "E785", {"start": v(-8.6, -61) * mm, "end": v(-12.92, -61.28) * mm});
            skLineSegment(sketch, "E786", {"start": v(-12.92, -61.28) * mm, "end": v(-13.76, -61.35) * mm});
            skLineSegment(sketch, "E787", {"start": v(-12.82, -58.85) * mm, "end": v(-12.6, -58.81) * mm});
            skLineSegment(sketch, "E788", {"start": v(-12.6, -58.81) * mm, "end": v(-11.98, -58.7) * mm});
            skLineSegment(sketch, "E789", {"start": v(-11.98, -58.7) * mm, "end": v(-10.86, -58.5) * mm});
            skLineSegment(sketch, "E790", {"start": v(-10.86, -58.5) * mm, "end": v(-9.47, -58.28) * mm});
            skLineSegment(sketch, "E791", {"start": v(-9.47, -58.28) * mm, "end": v(-7.86, -58.03) * mm});
            skLineSegment(sketch, "E792", {"start": v(-7.86, -58.03) * mm, "end": v(-6.05, -57.78) * mm});
            skLineSegment(sketch, "E793", {"start": v(-6.05, -57.78) * mm, "end": v(-4.06, -57.54) * mm});
            skLineSegment(sketch, "E794", {"start": v(-4.06, -57.54) * mm, "end": v(-1.92, -57.32) * mm});
            skLineSegment(sketch, "E795", {"start": v(-1.92, -57.32) * mm, "end": v(0.33, -57.13) * mm});
            skLineSegment(sketch, "E796", {"start": v(0.33, -57.13) * mm, "end": v(2.69, -56.98) * mm});
            skLineSegment(sketch, "E797", {"start": v(2.69, -56.98) * mm, "end": v(5.1, -56.9) * mm});
            skLineSegment(sketch, "E798", {"start": v(5.1, -56.9) * mm, "end": v(7.56, -56.87) * mm});
            skLineSegment(sketch, "E799", {"start": v(7.56, -56.87) * mm, "end": v(10.03, -56.93) * mm});
            skLineSegment(sketch, "E800", {"start": v(10.03, -56.93) * mm, "end": v(12.49, -57.08) * mm});
            skLineSegment(sketch, "E801", {"start": v(12.49, -57.08) * mm, "end": v(14.9, -57.34) * mm});
            skLineSegment(sketch, "E802", {"start": v(14.9, -57.34) * mm, "end": v(17.24, -57.72) * mm});
            skLineSegment(sketch, "E803", {"start": v(17.24, -57.72) * mm, "end": v(18.93, -58.08) * mm});
            skLineSegment(sketch, "E804", {"start": v(18.93, -58.08) * mm, "end": v(19.49, -58.23) * mm});
            skLineSegment(sketch, "E805", {"start": v(19.49, -58.23) * mm, "end": v(19.13, -57.98) * mm});
            skLineSegment(sketch, "E806", {"start": v(19.13, -57.98) * mm, "end": v(18.02, -57.27) * mm});
            skLineSegment(sketch, "E807", {"start": v(18.02, -57.27) * mm, "end": v(16.52, -56.4) * mm});
            skLineSegment(sketch, "E808", {"start": v(16.52, -56.4) * mm, "end": v(15, -55.62) * mm});
            skLineSegment(sketch, "E809", {"start": v(15, -55.62) * mm, "end": v(13.49, -54.92) * mm});
            skLineSegment(sketch, "E810", {"start": v(13.49, -54.92) * mm, "end": v(11.98, -54.3) * mm});
            skLineSegment(sketch, "E811", {"start": v(11.98, -54.3) * mm, "end": v(10.51, -53.76) * mm});
            skLineSegment(sketch, "E812", {"start": v(10.51, -53.76) * mm, "end": v(9.1, -53.29) * mm});
            skLineSegment(sketch, "E813", {"start": v(9.1, -53.29) * mm, "end": v(7.74, -52.88) * mm});
            skLineSegment(sketch, "E814", {"start": v(7.74, -52.88) * mm, "end": v(6.47, -52.54) * mm});
            skLineSegment(sketch, "E815", {"start": v(6.47, -52.54) * mm, "end": v(5.3, -52.25) * mm});
            skLineSegment(sketch, "E816", {"start": v(-1.47, -51.93) * mm, "end": v(-2.25, -52.1) * mm});
            skLineSegment(sketch, "E817", {"start": v(-2.25, -52.1) * mm, "end": v(-2.96, -52.25) * mm});
            skLineSegment(sketch, "E818", {"start": v(-2.96, -52.25) * mm, "end": v(-3.55, -52.39) * mm});
            skLineSegment(sketch, "E819", {"start": v(-3.55, -52.39) * mm, "end": v(-3.86, -52.47) * mm});
            skLineSegment(sketch, "E820", {"start": v(-23.02, -62.33) * mm, "end": v(-24.18, -62.5) * mm});
            skLineSegment(sketch, "E821", {"start": v(-24.18, -62.5) * mm, "end": v(-25.02, -62.63) * mm});
            skLineSegment(sketch, "E822", {"start": v(-25.02, -62.63) * mm, "end": v(-25.38, -62.7) * mm});
            skLineSegment(sketch, "E823", {"start": v(-15.95, -61.54) * mm, "end": v(-18.01, -61.74) * mm});
            skLineSegment(sketch, "E824", {"start": v(-4.08, -52.54) * mm, "end": v(-4.44, -52.65) * mm});
            skLineSegment(sketch, "E825", {"start": v(-25.38, -62.7) * mm, "end": v(-25.5, -62.73) * mm});
            skLineSegment(sketch, "E826", {"start": v(-18.01, -61.74) * mm, "end": v(-19.9, -61.94) * mm});
            skLineSegment(sketch, "E827", {"start": v(-4.44, -52.65) * mm, "end": v(-5.2, -52.89) * mm});
            skLineSegment(sketch, "E828", {"start": v(-25.5, -62.73) * mm, "end": v(-25.35, -62.99) * mm});
            skLineSegment(sketch, "E829", {"start": v(-19.9, -61.94) * mm, "end": v(-21.59, -62.14) * mm});
            skLineSegment(sketch, "E830", {"start": v(-5.2, -52.89) * mm, "end": v(-6.2, -53.2) * mm});
            skLineSegment(sketch, "E831", {"start": v(-25.35, -62.99) * mm, "end": v(-24.83, -63.7) * mm});
            skLineSegment(sketch, "E832", {"start": v(-21.59, -62.14) * mm, "end": v(-23.02, -62.33) * mm});
            skLineSegment(sketch, "E833", {"start": v(-6.2, -53.2) * mm, "end": v(-7.41, -53.6) * mm});
            skLineSegment(sketch, "E834", {"start": v(-13.76, -61.35) * mm, "end": v(-14.3, -61.4) * mm});
            skLineSegment(sketch, "E835", {"start": v(-24.83, -63.7) * mm, "end": v(-23.85, -64.9) * mm});
            skLineSegment(sketch, "E836", {"start": v(-23.85, -64.9) * mm, "end": v(-22.62, -66.24) * mm});
            skLineSegment(sketch, "E837", {"start": v(-14.09, -73.7) * mm, "end": v(-13.86, -73.86) * mm});
            skLineSegment(sketch, "E838", {"start": v(-13.86, -73.86) * mm, "end": v(-13.16, -74.35) * mm});
            skLineSegment(sketch, "E839", {"start": v(-13.16, -74.35) * mm, "end": v(-12.18, -75) * mm});
            skLineSegment(sketch, "E840", {"start": v(-12.18, -75) * mm, "end": v(-11.2, -75.62) * mm});
            skLineSegment(sketch, "E841", {"start": v(-14.56, -73.34) * mm, "end": v(-14.09, -73.7) * mm});
            skLineSegment(sketch, "E842", {"start": v(-15.96, -72.27) * mm, "end": v(-14.56, -73.34) * mm});
            skLineSegment(sketch, "E843", {"start": v(-17.8, -70.77) * mm, "end": v(-15.96, -72.27) * mm});
            skLineSegment(sketch, "E844", {"start": v(-19.54, -69.23) * mm, "end": v(-17.8, -70.77) * mm});
            skLineSegment(sketch, "E845", {"start": v(-21.16, -67.7) * mm, "end": v(-19.54, -69.23) * mm});
            skLineSegment(sketch, "E846", {"start": v(-22.62, -66.24) * mm, "end": v(-21.16, -67.7) * mm});
            skLineSegment(sketch, "E847", {"start": v(-3.97, -52.5) * mm, "end": v(-4.08, -52.54) * mm});
            skLineSegment(sketch, "E848", {"start": v(-14.3, -61.4) * mm, "end": v(-15.95, -61.54) * mm});
            skLineSegment(sketch, "E849", {"start": v(-0.67, -51.79) * mm, "end": v(-1.47, -51.93) * mm});
            skLineSegment(sketch, "E850", {"start": v(-3.86, -52.47) * mm, "end": v(-3.97, -52.5) * mm});
            skLineSegment(sketch, "E851", {"start": v(0.1, -51.67) * mm, "end": v(-0.67, -51.79) * mm});
            skLineSegment(sketch, "E852", {"start": v(0.78, -51.58) * mm, "end": v(0.1, -51.67) * mm});
            skLineSegment(sketch, "E853", {"start": v(1.2, -51.55) * mm, "end": v(0.78, -51.58) * mm});
            skLineSegment(sketch, "E854", {"start": v(1.33, -51.55) * mm, "end": v(1.2, -51.55) * mm});
            skLineSegment(sketch, "E855", {"start": v(1.38, -51.55) * mm, "end": v(1.33, -51.55) * mm});
            skLineSegment(sketch, "E856", {"start": v(1.54, -51.57) * mm, "end": v(1.38, -51.55) * mm});
            skLineSegment(sketch, "E857", {"start": v(1.96, -51.62) * mm, "end": v(1.54, -51.57) * mm});
            skLineSegment(sketch, "E858", {"start": v(2.56, -51.71) * mm, "end": v(1.96, -51.62) * mm});
            skLineSegment(sketch, "E859", {"start": v(3.33, -51.84) * mm, "end": v(2.56, -51.71) * mm});
            skLineSegment(sketch, "E860", {"start": v(4.25, -52.02) * mm, "end": v(3.33, -51.84) * mm});
            skLineSegment(sketch, "E861", {"start": v(5.3, -52.25) * mm, "end": v(4.25, -52.02) * mm});
            skLineSegment(sketch, "E862", {"start": v(18.14, -62.33) * mm, "end": v(18.6, -61.71) * mm});
            skLineSegment(sketch, "E863", {"start": v(17.35, -63.05) * mm, "end": v(18.14, -62.33) * mm});
            skLineSegment(sketch, "E864", {"start": v(16.36, -63.53) * mm, "end": v(17.35, -63.05) * mm});
            skLineSegment(sketch, "E865", {"start": v(15.51, -63.68) * mm, "end": v(16.36, -63.53) * mm});
            skLineSegment(sketch, "E866", {"start": v(15.24, -63.67) * mm, "end": v(15.51, -63.68) * mm});
            skLineSegment(sketch, "E867", {"start": v(14.84, -63.65) * mm, "end": v(15.24, -63.67) * mm});
            skLineSegment(sketch, "E868", {"start": v(13.65, -63.6) * mm, "end": v(14.84, -63.65) * mm});
            skLineSegment(sketch, "E869", {"start": v(11.82, -63.53) * mm, "end": v(13.65, -63.6) * mm});
            skLineSegment(sketch, "E870", {"start": v(-13.4, -65.44) * mm, "end": v(-14.7, -65.52) * mm});
            skLineSegment(sketch, "E871", {"start": v(-11.8, -65.35) * mm, "end": v(-13.4, -65.44) * mm});
            skLineSegment(sketch, "E872", {"start": v(-9.96, -65.26) * mm, "end": v(-11.8, -65.35) * mm});
            skLineSegment(sketch, "E873", {"start": v(-7.9, -65.16) * mm, "end": v(-9.96, -65.26) * mm});
            skLineSegment(sketch, "E874", {"start": v(-5.68, -65.07) * mm, "end": v(-7.9, -65.16) * mm});
            skLineSegment(sketch, "E875", {"start": v(-3.3, -64.98) * mm, "end": v(-5.68, -65.07) * mm});
            skLineSegment(sketch, "E876", {"start": v(-0.84, -64.9) * mm, "end": v(-3.3, -64.98) * mm});
            skLineSegment(sketch, "E877", {"start": v(1.68, -64.85) * mm, "end": v(-0.84, -64.9) * mm});
            skLineSegment(sketch, "E878", {"start": v(4.23, -64.81) * mm, "end": v(1.68, -64.85) * mm});
            skLineSegment(sketch, "E879", {"start": v(6.77, -64.8) * mm, "end": v(4.23, -64.81) * mm});
            skLineSegment(sketch, "E880", {"start": v(9.25, -64.83) * mm, "end": v(6.77, -64.8) * mm});
            skLineSegment(sketch, "E881", {"start": v(11.64, -64.89) * mm, "end": v(9.25, -64.83) * mm});
            skLineSegment(sketch, "E882", {"start": v(13.34, -64.96) * mm, "end": v(11.64, -64.89) * mm});
            skLineSegment(sketch, "E883", {"start": v(13.9, -64.99) * mm, "end": v(13.34, -64.96) * mm});
            skLineSegment(sketch, "E884", {"start": v(13.82, -65.1) * mm, "end": v(13.9, -64.99) * mm});
            skLineSegment(sketch, "E885", {"start": v(13.55, -65.4) * mm, "end": v(13.82, -65.1) * mm});
            skLineSegment(sketch, "E886", {"start": v(13, -65.97) * mm, "end": v(13.55, -65.4) * mm});
            skLineSegment(sketch, "E887", {"start": v(12.28, -66.65) * mm, "end": v(13, -65.97) * mm});
            skLineSegment(sketch, "E888", {"start": v(11.4, -67.44) * mm, "end": v(12.28, -66.65) * mm});
            skLineSegment(sketch, "E889", {"start": v(10.4, -68.3) * mm, "end": v(11.4, -67.44) * mm});
            skLineSegment(sketch, "E890", {"start": v(9.3, -69.24) * mm, "end": v(10.4, -68.3) * mm});
            skLineSegment(sketch, "E891", {"start": v(8.1, -70.2) * mm, "end": v(9.3, -69.24) * mm});
            skLineSegment(sketch, "E892", {"start": v(7.16, -70.93) * mm, "end": v(8.1, -70.2) * mm});
            skLineSegment(sketch, "E893", {"start": v(6.85, -71.17) * mm, "end": v(7.16, -70.93) * mm});
            skLineSegment(sketch, "E894", {"start": v(-6.83, -77.57) * mm, "end": v(-6.12, -77.54) * mm});
            skLineSegment(sketch, "E895", {"start": v(-7.34, -77.55) * mm, "end": v(-6.83, -77.57) * mm});
            skLineSegment(sketch, "E896", {"start": v(-7.56, -77.52) * mm, "end": v(-7.34, -77.55) * mm});
            skLineSegment(sketch, "E897", {"start": v(-7.63, -77.5) * mm, "end": v(-7.56, -77.52) * mm});
            skLineSegment(sketch, "E898", {"start": v(-7.73, -77.48) * mm, "end": v(-7.63, -77.5) * mm});
            skLineSegment(sketch, "E899", {"start": v(-8.03, -77.36) * mm, "end": v(-7.73, -77.48) * mm});
            skLineSegment(sketch, "E900", {"start": v(-11.2, -75.62) * mm, "end": v(-10.25, -76.19) * mm});
            skLineSegment(sketch, "E901", {"start": v(-10.25, -76.19) * mm, "end": v(-9.37, -76.68) * mm});
            skLineSegment(sketch, "E902", {"start": v(-9.37, -76.68) * mm, "end": v(-8.62, -77.08) * mm});
            skLineSegment(sketch, "E903", {"start": v(-8.62, -77.08) * mm, "end": v(-8.03, -77.36) * mm});
            skLineSegment(sketch, "E904", {"start": v(-6.12, -77.54) * mm, "end": v(-5.2, -77.42) * mm});
            skLineSegment(sketch, "E905", {"start": v(-5.2, -77.42) * mm, "end": v(-4.1, -77.17) * mm});
            skLineSegment(sketch, "E906", {"start": v(-4.1, -77.17) * mm, "end": v(-2.79, -76.76) * mm});
            skLineSegment(sketch, "E907", {"start": v(-2.79, -76.76) * mm, "end": v(-1.3, -76.14) * mm});
            skLineSegment(sketch, "E908", {"start": v(-1.3, -76.14) * mm, "end": v(-0.04, -75.52) * mm});
            skLineSegment(sketch, "E909", {"start": v(-0.04, -75.52) * mm, "end": v(0.37, -75.29) * mm});
            skLineSegment(sketch, "E910", {"start": v(0.37, -75.29) * mm, "end": v(0.76, -75.07) * mm});
            skLineSegment(sketch, "E911", {"start": v(0.76, -75.07) * mm, "end": v(1.94, -74.4) * mm});
            skLineSegment(sketch, "E912", {"start": v(1.94, -74.4) * mm, "end": v(3.58, -73.4) * mm});
            skLineSegment(sketch, "E913", {"start": v(3.58, -73.4) * mm, "end": v(5.23, -72.32) * mm});
            skLineSegment(sketch, "E914", {"start": v(5.23, -72.32) * mm, "end": v(6.45, -71.47) * mm});
            skLineSegment(sketch, "E915", {"start": v(6.45, -71.47) * mm, "end": v(6.85, -71.17) * mm});
            skLineSegment(sketch, "E916", {"start": v(-14.7, -65.52) * mm, "end": v(-15.68, -65.58) * mm});
            skLineSegment(sketch, "E917", {"start": v(-15.68, -65.58) * mm, "end": v(-16.3, -65.62) * mm});
            skLineSegment(sketch, "E918", {"start": v(-16.3, -65.62) * mm, "end": v(-16.5, -65.64) * mm});
            skLineSegment(sketch, "E919", {"start": v(-16.5, -65.64) * mm, "end": v(3.35, -67.26) * mm});
            skLineSegment(sketch, "E920", {"start": v(3.35, -67.26) * mm, "end": v(3.23, -67.36) * mm});
            skLineSegment(sketch, "E921", {"start": v(3.23, -67.36) * mm, "end": v(2.9, -67.66) * mm});
            skLineSegment(sketch, "E922", {"start": v(2.9, -67.66) * mm, "end": v(2.37, -68.11) * mm});
            skLineSegment(sketch, "E923", {"start": v(2.37, -68.11) * mm, "end": v(1.68, -68.67) * mm});
            skLineSegment(sketch, "E924", {"start": v(1.68, -68.67) * mm, "end": v(0.86, -69.32) * mm});
            skLineSegment(sketch, "E925", {"start": v(0.86, -69.32) * mm, "end": v(-0.07, -70) * mm});
            skLineSegment(sketch, "E926", {"start": v(-0.07, -70) * mm, "end": v(-1.08, -70.67) * mm});
            skLineSegment(sketch, "E927", {"start": v(-1.08, -70.67) * mm, "end": v(-1.87, -71.16) * mm});
            skLineSegment(sketch, "E928", {"start": v(-1.87, -71.16) * mm, "end": v(-2.14, -71.32) * mm});
            skLineSegment(sketch, "E929", {"start": v(-2.14, -71.32) * mm, "end": v(-2.52, -71.53) * mm});
            skLineSegment(sketch, "E930", {"start": v(-2.52, -71.53) * mm, "end": v(-3.7, -72.1) * mm});
            skLineSegment(sketch, "E931", {"start": v(-3.7, -72.1) * mm, "end": v(-5.13, -72.62) * mm});
            skLineSegment(sketch, "E932", {"start": v(-5.13, -72.62) * mm, "end": v(-6.41, -72.9) * mm});
            skLineSegment(sketch, "E933", {"start": v(-6.41, -72.9) * mm, "end": v(-7.25, -72.99) * mm});
            skLineSegment(sketch, "E934", {"start": v(-7.25, -72.99) * mm, "end": v(-7.53, -72.99) * mm});
            skLineSegment(sketch, "E935", {"start": v(-7.53, -72.99) * mm, "end": v(-7.74, -72.98) * mm});
            skLineSegment(sketch, "E936", {"start": v(-7.74, -72.98) * mm, "end": v(-8.35, -72.93) * mm});
            skLineSegment(sketch, "E937", {"start": v(-8.35, -72.93) * mm, "end": v(-9.34, -72.73) * mm});
            skLineSegment(sketch, "E938", {"start": v(-9.34, -72.73) * mm, "end": v(-10.52, -72.3) * mm});
            skLineSegment(sketch, "E939", {"start": v(-10.52, -72.3) * mm, "end": v(-11.58, -71.78) * mm});
            skLineSegment(sketch, "E940", {"start": v(-11.58, -71.78) * mm, "end": v(-11.92, -71.58) * mm});
            skLineSegment(sketch, "E941", {"start": v(-11.92, -71.58) * mm, "end": v(-12.32, -71.33) * mm});
            skLineSegment(sketch, "E942", {"start": v(-12.32, -71.33) * mm, "end": v(-13.5, -70.56) * mm});
            skLineSegment(sketch, "E943", {"start": v(-13.5, -70.56) * mm, "end": v(-14.95, -69.53) * mm});
            skLineSegment(sketch, "E944", {"start": v(-14.95, -69.53) * mm, "end": v(-16.26, -68.5) * mm});
            skLineSegment(sketch, "E945", {"start": v(-16.26, -68.5) * mm, "end": v(-17.43, -67.53) * mm});
            skLineSegment(sketch, "E946", {"start": v(-17.43, -67.53) * mm, "end": v(-18.42, -66.64) * mm});
            skLineSegment(sketch, "E947", {"start": v(-18.42, -66.64) * mm, "end": v(-19.23, -65.86) * mm});
            skLineSegment(sketch, "E948", {"start": v(-19.23, -65.86) * mm, "end": v(-19.83, -65.24) * mm});
            skLineSegment(sketch, "E949", {"start": v(-19.83, -65.24) * mm, "end": v(-20.13, -64.91) * mm});
            skLineSegment(sketch, "E950", {"start": v(-20.13, -64.91) * mm, "end": v(-20.22, -64.8) * mm});
            skLineSegment(sketch, "E951", {"start": v(-20.22, -64.8) * mm, "end": v(-19.8, -64.73) * mm});
            skLineSegment(sketch, "E952", {"start": v(-19.8, -64.73) * mm, "end": v(-18.56, -64.56) * mm});
            skLineSegment(sketch, "E953", {"start": v(-18.56, -64.56) * mm, "end": v(-16.66, -64.34) * mm});
            skLineSegment(sketch, "E954", {"start": v(-16.66, -64.34) * mm, "end": v(-14.57, -64.15) * mm});
            skLineSegment(sketch, "E955", {"start": v(-14.57, -64.15) * mm, "end": v(-12.32, -63.98) * mm});
            skLineSegment(sketch, "E956", {"start": v(-12.32, -63.98) * mm, "end": v(-9.93, -63.84) * mm});
            skLineSegment(sketch, "E957", {"start": v(-9.93, -63.84) * mm, "end": v(-7.45, -63.72) * mm});
            skLineSegment(sketch, "E958", {"start": v(-7.45, -63.72) * mm, "end": v(-4.9, -63.63) * mm});
            skLineSegment(sketch, "E959", {"start": v(-4.9, -63.63) * mm, "end": v(-2.33, -63.55) * mm});
            skLineSegment(sketch, "E960", {"start": v(-2.33, -63.55) * mm, "end": v(0.24, -63.5) * mm});
            skLineSegment(sketch, "E961", {"start": v(0.24, -63.5) * mm, "end": v(2.77, -63.47) * mm});
            skLineSegment(sketch, "E962", {"start": v(2.77, -63.47) * mm, "end": v(5.22, -63.46) * mm});
            skLineSegment(sketch, "E963", {"start": v(5.22, -63.46) * mm, "end": v(7.57, -63.47) * mm});
            skLineSegment(sketch, "E964", {"start": v(85.99, -80.92) * mm, "end": v(85.93, -80.54) * mm});
            skLineSegment(sketch, "E965", {"start": v(86.12, -82.05) * mm, "end": v(85.99, -80.92) * mm});
            skLineSegment(sketch, "E966", {"start": v(86.2, -83.39) * mm, "end": v(86.12, -82.05) * mm});
            skLineSegment(sketch, "E967", {"start": v(86.2, -84.45) * mm, "end": v(86.2, -83.39) * mm});
            skLineSegment(sketch, "E968", {"start": v(86.15, -84.98) * mm, "end": v(86.2, -84.45) * mm});
            skLineSegment(sketch, "E969", {"start": v(86.1, -85.12) * mm, "end": v(86.15, -84.98) * mm});
            skLineSegment(sketch, "E970", {"start": v(86.06, -85.24) * mm, "end": v(86.1, -85.12) * mm});
            skLineSegment(sketch, "E971", {"start": v(85.92, -85.58) * mm, "end": v(86.06, -85.24) * mm});
            skLineSegment(sketch, "E972", {"start": v(85.61, -86.23) * mm, "end": v(85.92, -85.58) * mm});
            skLineSegment(sketch, "E973", {"start": v(85.17, -87.02) * mm, "end": v(85.61, -86.23) * mm});
            skLineSegment(sketch, "E974", {"start": v(84.74, -87.7) * mm, "end": v(85.17, -87.02) * mm});
            skLineSegment(sketch, "E975", {"start": v(84.59, -87.92) * mm, "end": v(84.74, -87.7) * mm});
            skLineSegment(sketch, "E976", {"start": v(84.46, -88.1) * mm, "end": v(84.59, -87.92) * mm});
            skLineSegment(sketch, "E977", {"start": v(84.08, -88.65) * mm, "end": v(84.46, -88.1) * mm});
            skLineSegment(sketch, "E978", {"start": v(83.55, -89.37) * mm, "end": v(84.08, -88.65) * mm});
            skLineSegment(sketch, "E979", {"start": v(83.03, -90.06) * mm, "end": v(83.55, -89.37) * mm});
            skLineSegment(sketch, "E980", {"start": v(82.54, -90.69) * mm, "end": v(83.03, -90.06) * mm});
            skLineSegment(sketch, "E981", {"start": v(82.12, -91.22) * mm, "end": v(82.54, -90.69) * mm});
            skLineSegment(sketch, "E982", {"start": v(81.78, -91.65) * mm, "end": v(82.12, -91.22) * mm});
            skLineSegment(sketch, "E983", {"start": v(81.56, -91.92) * mm, "end": v(81.78, -91.65) * mm});
            skLineSegment(sketch, "E984", {"start": v(81.48, -92.02) * mm, "end": v(81.56, -91.92) * mm});
            skLineSegment(sketch, "E985", {"start": v(81.53, -91.8) * mm, "end": v(81.48, -92.02) * mm});
            skLineSegment(sketch, "E986", {"start": v(81.68, -91.23) * mm, "end": v(81.53, -91.8) * mm});
            skLineSegment(sketch, "E987", {"start": v(81.91, -90.34) * mm, "end": v(81.68, -91.23) * mm});
            skLineSegment(sketch, "E988", {"start": v(82.2, -89.2) * mm, "end": v(81.91, -90.34) * mm});
            skLineSegment(sketch, "E989", {"start": v(82.53, -87.87) * mm, "end": v(82.2, -89.2) * mm});
            skLineSegment(sketch, "E990", {"start": v(82.88, -86.43) * mm, "end": v(82.53, -87.87) * mm});
            skLineSegment(sketch, "E991", {"start": v(83.23, -84.93) * mm, "end": v(82.88, -86.43) * mm});
            skLineSegment(sketch, "E992", {"start": v(83.49, -83.8) * mm, "end": v(83.23, -84.93) * mm});
            skLineSegment(sketch, "E993", {"start": v(83.57, -83.43) * mm, "end": v(83.49, -83.8) * mm});
            skLineSegment(sketch, "E994", {"start": v(83.65, -83.06) * mm, "end": v(83.57, -83.43) * mm});
            skLineSegment(sketch, "E995", {"start": v(83.89, -81.95) * mm, "end": v(83.65, -83.06) * mm});
            skLineSegment(sketch, "E996", {"start": v(84.16, -80.56) * mm, "end": v(83.89, -81.95) * mm});
            skLineSegment(sketch, "E997", {"start": v(84.4, -79.3) * mm, "end": v(84.16, -80.56) * mm});
            skLineSegment(sketch, "E998", {"start": v(84.6, -78.2) * mm, "end": v(84.4, -79.3) * mm});
            skLineSegment(sketch, "E999", {"start": v(84.76, -77.3) * mm, "end": v(84.6, -78.2) * mm});
            skLineSegment(sketch, "E1000", {"start": v(84.87, -76.62) * mm, "end": v(84.76, -77.3) * mm});
            skLineSegment(sketch, "E1001", {"start": v(84.94, -76.18) * mm, "end": v(84.87, -76.62) * mm});
            skLineSegment(sketch, "E1002", {"start": v(84.97, -76.03) * mm, "end": v(84.94, -76.18) * mm});
            skLineSegment(sketch, "E1003", {"start": v(85, -76.14) * mm, "end": v(84.97, -76.03) * mm});
            skLineSegment(sketch, "E1004", {"start": v(85.07, -76.43) * mm, "end": v(85, -76.14) * mm});
            skLineSegment(sketch, "E1005", {"start": v(85.18, -76.88) * mm, "end": v(85.07, -76.43) * mm});
            skLineSegment(sketch, "E1006", {"start": v(85.32, -77.47) * mm, "end": v(85.18, -76.88) * mm});
            skLineSegment(sketch, "E1007", {"start": v(85.48, -78.15) * mm, "end": v(85.32, -77.47) * mm});
            skLineSegment(sketch, "E1008", {"start": v(85.64, -78.91) * mm, "end": v(85.48, -78.15) * mm});
            skLineSegment(sketch, "E1009", {"start": v(85.8, -79.72) * mm, "end": v(85.64, -78.91) * mm});
            skLineSegment(sketch, "E1010", {"start": v(85.9, -80.33) * mm, "end": v(85.8, -79.72) * mm});
            skLineSegment(sketch, "E1011", {"start": v(85.93, -80.54) * mm, "end": v(85.9, -80.33) * mm});
            skLineSegment(sketch, "E1012", {"start": v(69.43, -69.33) * mm, "end": v(68.83, -69.17) * mm});
            skLineSegment(sketch, "E1013", {"start": v(71.23, -69.8) * mm, "end": v(69.43, -69.33) * mm});
            skLineSegment(sketch, "E1014", {"start": v(73.52, -70.42) * mm, "end": v(71.23, -69.8) * mm});
            skLineSegment(sketch, "E1015", {"start": v(75.66, -70.98) * mm, "end": v(73.52, -70.42) * mm});
            skLineSegment(sketch, "E1016", {"start": v(77.62, -71.45) * mm, "end": v(75.66, -70.98) * mm});
            skLineSegment(sketch, "E1017", {"start": v(79.35, -71.78) * mm, "end": v(77.62, -71.45) * mm});
            skLineSegment(sketch, "E1018", {"start": v(80.82, -71.93) * mm, "end": v(79.35, -71.78) * mm});
            skLineSegment(sketch, "E1019", {"start": v(82, -71.86) * mm, "end": v(80.82, -71.93) * mm});
            skLineSegment(sketch, "E1020", {"start": v(82.66, -71.66) * mm, "end": v(82, -71.86) * mm});
            skLineSegment(sketch, "E1021", {"start": v(82.83, -71.54) * mm, "end": v(82.66, -71.66) * mm});
            skLineSegment(sketch, "E1022", {"start": v(82.93, -71.47) * mm, "end": v(82.83, -71.54) * mm});
            skLineSegment(sketch, "E1023", {"start": v(83.14, -71.15) * mm, "end": v(82.93, -71.47) * mm});
            skLineSegment(sketch, "E1024", {"start": v(83.48, -70.43) * mm, "end": v(83.14, -71.15) * mm});
            skLineSegment(sketch, "E1025", {"start": v(83.84, -69.46) * mm, "end": v(83.48, -70.43) * mm});
            skLineSegment(sketch, "E1026", {"start": v(84.19, -68.33) * mm, "end": v(83.84, -69.46) * mm});
            skLineSegment(sketch, "E1027", {"start": v(84.52, -67.1) * mm, "end": v(84.19, -68.33) * mm});
            skLineSegment(sketch, "E1028", {"start": v(84.82, -65.87) * mm, "end": v(84.52, -67.1) * mm});
            skLineSegment(sketch, "E1029", {"start": v(85.06, -64.7) * mm, "end": v(84.82, -65.87) * mm});
            skLineSegment(sketch, "E1030", {"start": v(85.19, -63.94) * mm, "end": v(85.06, -64.7) * mm});
            skLineSegment(sketch, "E1031", {"start": v(85.22, -63.68) * mm, "end": v(85.19, -63.94) * mm});
            skLineSegment(sketch, "E1032", {"start": v(85.35, -64.14) * mm, "end": v(85.22, -63.68) * mm});
            skLineSegment(sketch, "E1033", {"start": v(85.58, -65.57) * mm, "end": v(85.35, -64.14) * mm});
            skLineSegment(sketch, "E1034", {"start": v(85.72, -67.67) * mm, "end": v(85.58, -65.57) * mm});
            skLineSegment(sketch, "E1035", {"start": v(85.63, -69.82) * mm, "end": v(85.72, -67.67) * mm});
            skLineSegment(sketch, "E1036", {"start": v(85.42, -71.38) * mm, "end": v(85.63, -69.82) * mm});
            skLineSegment(sketch, "E1037", {"start": v(85.3, -71.9) * mm, "end": v(85.42, -71.38) * mm});
            skLineSegment(sketch, "E1038", {"start": v(85.2, -72.37) * mm, "end": v(85.3, -71.9) * mm});
            skLineSegment(sketch, "E1039", {"start": v(84.77, -73.8) * mm, "end": v(85.2, -72.37) * mm});
            skLineSegment(sketch, "E1040", {"start": v(84.1, -75.66) * mm, "end": v(84.77, -73.8) * mm});
            skLineSegment(sketch, "E1041", {"start": v(83.37, -77.39) * mm, "end": v(84.1, -75.66) * mm});
            skLineSegment(sketch, "E1042", {"start": v(82.86, -78.53) * mm, "end": v(83.37, -77.39) * mm});
            skLineSegment(sketch, "E1043", {"start": v(82.68, -78.9) * mm, "end": v(82.86, -78.53) * mm});
            skLineSegment(sketch, "E1044", {"start": v(82.49, -79.31) * mm, "end": v(82.68, -78.9) * mm});
            skLineSegment(sketch, "E1045", {"start": v(81.9, -80.53) * mm, "end": v(82.49, -79.31) * mm});
            skLineSegment(sketch, "E1046", {"start": v(81.33, -81.78) * mm, "end": v(81.9, -80.53) * mm});
            skLineSegment(sketch, "E1047", {"start": v(81.02, -82.7) * mm, "end": v(81.33, -81.78) * mm});
            skLineSegment(sketch, "E1048", {"start": v(80.97, -83.22) * mm, "end": v(81.02, -82.7) * mm});
            skLineSegment(sketch, "E1049", {"start": v(81.02, -83.37) * mm, "end": v(80.97, -83.22) * mm});
            skLineSegment(sketch, "E1050", {"start": v(80.88, -83.17) * mm, "end": v(81.02, -83.37) * mm});
            skLineSegment(sketch, "E1051", {"start": v(80.6, -82.47) * mm, "end": v(80.88, -83.17) * mm});
            skLineSegment(sketch, "E1052", {"start": v(80.27, -81.27) * mm, "end": v(80.6, -82.47) * mm});
            skLineSegment(sketch, "E1053", {"start": v(80.01, -79.9) * mm, "end": v(80.27, -81.27) * mm});
            skLineSegment(sketch, "E1054", {"start": v(79.8, -78.48) * mm, "end": v(80.01, -79.9) * mm});
            skLineSegment(sketch, "E1055", {"start": v(79.58, -77.11) * mm, "end": v(79.8, -78.48) * mm});
            skLineSegment(sketch, "E1056", {"start": v(79.34, -75.93) * mm, "end": v(79.58, -77.11) * mm});
            skLineSegment(sketch, "E1057", {"start": v(79.04, -75.04) * mm, "end": v(79.34, -75.93) * mm});
            skLineSegment(sketch, "E1058", {"start": v(78.77, -74.63) * mm, "end": v(79.04, -75.04) * mm});
            skLineSegment(sketch, "E1059", {"start": v(78.64, -74.56) * mm, "end": v(78.77, -74.63) * mm});
            skLineSegment(sketch, "E1060", {"start": v(78.43, -74.5) * mm, "end": v(78.64, -74.56) * mm});
            skLineSegment(sketch, "E1061", {"start": v(77.8, -74.33) * mm, "end": v(78.43, -74.5) * mm});
            skLineSegment(sketch, "E1062", {"start": v(76.77, -74.09) * mm, "end": v(77.8, -74.33) * mm});
            skLineSegment(sketch, "E1063", {"start": v(75.57, -73.83) * mm, "end": v(76.77, -74.09) * mm});
            skLineSegment(sketch, "E1064", {"start": v(74.23, -73.57) * mm, "end": v(75.57, -73.83) * mm});
            skLineSegment(sketch, "E1065", {"start": v(72.79, -73.3) * mm, "end": v(74.23, -73.57) * mm});
            skLineSegment(sketch, "E1066", {"start": v(71.27, -73.05) * mm, "end": v(72.79, -73.3) * mm});
            skLineSegment(sketch, "E1067", {"start": v(69.7, -72.8) * mm, "end": v(71.27, -73.05) * mm});
            skLineSegment(sketch, "E1068", {"start": v(68.5, -72.61) * mm, "end": v(69.7, -72.8) * mm});
            skLineSegment(sketch, "E1069", {"start": v(68.1, -72.55) * mm, "end": v(68.5, -72.61) * mm});
            skLineSegment(sketch, "E1070", {"start": v(67.68, -72.49) * mm, "end": v(68.1, -72.55) * mm});
            skLineSegment(sketch, "E1071", {"start": v(66.39, -72.3) * mm, "end": v(67.68, -72.49) * mm});
            skLineSegment(sketch, "E1072", {"start": v(64.72, -72.07) * mm, "end": v(66.39, -72.3) * mm});
            skLineSegment(sketch, "E1073", {"start": v(63.15, -71.85) * mm, "end": v(64.72, -72.07) * mm});
            skLineSegment(sketch, "E1074", {"start": v(61.71, -71.67) * mm, "end": v(63.15, -71.85) * mm});
            skLineSegment(sketch, "E1075", {"start": v(50.29, -55.44) * mm, "end": v(48.46, -54.54) * mm});
            skLineSegment(sketch, "E1076", {"start": v(52.28, -56.4) * mm, "end": v(50.29, -55.44) * mm});
            skLineSegment(sketch, "E1077", {"start": v(41.55, -53.34) * mm, "end": v(41.35, -53.5) * mm});
            skLineSegment(sketch, "E1078", {"start": v(41.35, -53.5) * mm, "end": v(41.43, -53.56) * mm});
            skLineSegment(sketch, "E1079", {"start": v(41.43, -53.56) * mm, "end": v(41.7, -53.72) * mm});
            skLineSegment(sketch, "E1080", {"start": v(41.7, -53.72) * mm, "end": v(42.24, -54.05) * mm});
            skLineSegment(sketch, "E1081", {"start": v(42.24, -54.05) * mm, "end": v(42.97, -54.48) * mm});
            skLineSegment(sketch, "E1082", {"start": v(42.97, -54.48) * mm, "end": v(43.89, -55) * mm});
            skLineSegment(sketch, "E1083", {"start": v(43.89, -55) * mm, "end": v(44.96, -55.6) * mm});
            skLineSegment(sketch, "E1084", {"start": v(44.96, -55.6) * mm, "end": v(46.19, -56.26) * mm});
            skLineSegment(sketch, "E1085", {"start": v(46.19, -56.26) * mm, "end": v(47.54, -56.98) * mm});
            skLineSegment(sketch, "E1086", {"start": v(47.54, -56.98) * mm, "end": v(48.65, -57.56) * mm});
            skLineSegment(sketch, "E1087", {"start": v(48.65, -57.56) * mm, "end": v(49.02, -57.75) * mm});
            skLineSegment(sketch, "E1088", {"start": v(49.02, -57.75) * mm, "end": v(49.68, -58.1) * mm});
            skLineSegment(sketch, "E1089", {"start": v(49.68, -58.1) * mm, "end": v(51.7, -59.1) * mm});
            skLineSegment(sketch, "E1090", {"start": v(51.7, -59.1) * mm, "end": v(54.6, -60.5) * mm});
            skLineSegment(sketch, "E1091", {"start": v(54.6, -60.5) * mm, "end": v(57.67, -61.93) * mm});
            skLineSegment(sketch, "E1092", {"start": v(57.67, -61.93) * mm, "end": v(60.06, -63) * mm});
            skLineSegment(sketch, "E1093", {"start": v(60.06, -63) * mm, "end": v(60.86, -63.34) * mm});
            skLineSegment(sketch, "E1094", {"start": v(60.86, -63.34) * mm, "end": v(61.73, -63.72) * mm});
            skLineSegment(sketch, "E1095", {"start": v(61.73, -63.72) * mm, "end": v(65.9, -65.45) * mm});
            skLineSegment(sketch, "E1096", {"start": v(65.9, -65.45) * mm, "end": v(69.94, -67.01) * mm});
            skLineSegment(sketch, "E1097", {"start": v(69.94, -67.01) * mm, "end": v(70.73, -67.3) * mm});
            skLineSegment(sketch, "E1098", {"start": v(68.83, -69.17) * mm, "end": v(68.62, -69.12) * mm});
            skLineSegment(sketch, "E1099", {"start": v(68.62, -69.12) * mm, "end": v(68, -68.96) * mm});
            skLineSegment(sketch, "E1100", {"start": v(68, -68.96) * mm, "end": v(66.9, -68.66) * mm});
            skLineSegment(sketch, "E1101", {"start": v(66.9, -68.66) * mm, "end": v(65.56, -68.29) * mm});
            skLineSegment(sketch, "E1102", {"start": v(65.56, -68.29) * mm, "end": v(64, -67.83) * mm});
            skLineSegment(sketch, "E1103", {"start": v(64, -67.83) * mm, "end": v(62.24, -67.29) * mm});
            skLineSegment(sketch, "E1104", {"start": v(62.24, -67.29) * mm, "end": v(60.34, -66.67) * mm});
            skLineSegment(sketch, "E1105", {"start": v(60.34, -66.67) * mm, "end": v(58.3, -65.97) * mm});
            skLineSegment(sketch, "E1106", {"start": v(58.3, -65.97) * mm, "end": v(56.18, -65.2) * mm});
            skLineSegment(sketch, "E1107", {"start": v(56.18, -65.2) * mm, "end": v(53.98, -64.33) * mm});
            skLineSegment(sketch, "E1108", {"start": v(53.98, -64.33) * mm, "end": v(51.75, -63.4) * mm});
            skLineSegment(sketch, "E1109", {"start": v(51.75, -63.4) * mm, "end": v(49.51, -62.38) * mm});
            skLineSegment(sketch, "E1110", {"start": v(49.51, -62.38) * mm, "end": v(47.3, -61.29) * mm});
            skLineSegment(sketch, "E1111", {"start": v(47.3, -61.29) * mm, "end": v(45.14, -60.11) * mm});
            skLineSegment(sketch, "E1112", {"start": v(45.14, -60.11) * mm, "end": v(43.06, -58.86) * mm});
            skLineSegment(sketch, "E1113", {"start": v(43.06, -58.86) * mm, "end": v(41.1, -57.53) * mm});
            skLineSegment(sketch, "E1114", {"start": v(41.1, -57.53) * mm, "end": v(39.71, -56.5) * mm});
            skLineSegment(sketch, "E1115", {"start": v(39.71, -56.5) * mm, "end": v(39.27, -56.12) * mm});
            skLineSegment(sketch, "E1116", {"start": v(39.27, -56.12) * mm, "end": v(39.49, -56.5) * mm});
            skLineSegment(sketch, "E1117", {"start": v(39.49, -56.5) * mm, "end": v(40.2, -57.61) * mm});
            skLineSegment(sketch, "E1118", {"start": v(40.2, -57.61) * mm, "end": v(41.19, -59.03) * mm});
            skLineSegment(sketch, "E1119", {"start": v(41.19, -59.03) * mm, "end": v(42.24, -60.38) * mm});
            skLineSegment(sketch, "E1120", {"start": v(42.24, -60.38) * mm, "end": v(43.32, -61.65) * mm});
            skLineSegment(sketch, "E1121", {"start": v(43.32, -61.65) * mm, "end": v(44.42, -62.85) * mm});
            skLineSegment(sketch, "E1122", {"start": v(44.42, -62.85) * mm, "end": v(45.52, -63.96) * mm});
            skLineSegment(sketch, "E1123", {"start": v(45.52, -63.96) * mm, "end": v(46.61, -64.99) * mm});
            skLineSegment(sketch, "E1124", {"start": v(46.61, -64.99) * mm, "end": v(47.67, -65.92) * mm});
            skLineSegment(sketch, "E1125", {"start": v(47.67, -65.92) * mm, "end": v(48.68, -66.77) * mm});
            skLineSegment(sketch, "E1126", {"start": v(48.68, -66.77) * mm, "end": v(49.62, -67.52) * mm});
            skLineSegment(sketch, "E1127", {"start": v(55.62, -70.66) * mm, "end": v(56.4, -70.85) * mm});
            skLineSegment(sketch, "E1128", {"start": v(56.4, -70.85) * mm, "end": v(57.11, -71) * mm});
            skLineSegment(sketch, "E1129", {"start": v(57.11, -71) * mm, "end": v(57.7, -71.13) * mm});
            skLineSegment(sketch, "E1130", {"start": v(57.7, -71.13) * mm, "end": v(58.02, -71.19) * mm});
            skLineSegment(sketch, "E1131", {"start": v(79.55, -70.32) * mm, "end": v(80.67, -70.66) * mm});
            skLineSegment(sketch, "E1132", {"start": v(80.67, -70.66) * mm, "end": v(81.48, -70.89) * mm});
            skLineSegment(sketch, "E1133", {"start": v(81.48, -70.89) * mm, "end": v(81.84, -70.97) * mm});
            skLineSegment(sketch, "E1134", {"start": v(72.8, -68.06) * mm, "end": v(74.76, -68.74) * mm});
            skLineSegment(sketch, "E1135", {"start": v(58.25, -71.22) * mm, "end": v(58.62, -71.27) * mm});
            skLineSegment(sketch, "E1136", {"start": v(81.84, -70.97) * mm, "end": v(81.96, -71) * mm});
            skLineSegment(sketch, "E1137", {"start": v(74.76, -68.74) * mm, "end": v(76.56, -69.35) * mm});
            skLineSegment(sketch, "E1138", {"start": v(58.62, -71.27) * mm, "end": v(59.4, -71.37) * mm});
            skLineSegment(sketch, "E1139", {"start": v(81.96, -71) * mm, "end": v(81.93, -70.7) * mm});
            skLineSegment(sketch, "E1140", {"start": v(76.56, -69.35) * mm, "end": v(78.17, -69.88) * mm});
            skLineSegment(sketch, "E1141", {"start": v(59.4, -71.37) * mm, "end": v(60.45, -71.5) * mm});
            skLineSegment(sketch, "E1142", {"start": v(81.93, -70.7) * mm, "end": v(81.77, -69.83) * mm});
            skLineSegment(sketch, "E1143", {"start": v(78.17, -69.88) * mm, "end": v(79.55, -70.32) * mm});
            skLineSegment(sketch, "E1144", {"start": v(60.45, -71.5) * mm, "end": v(61.71, -71.67) * mm});
            skLineSegment(sketch, "E1145", {"start": v(70.73, -67.3) * mm, "end": v(71.25, -67.5) * mm});
            skLineSegment(sketch, "E1146", {"start": v(81.77, -69.83) * mm, "end": v(81.38, -68.34) * mm});
            skLineSegment(sketch, "E1147", {"start": v(81.38, -68.34) * mm, "end": v(80.83, -66.6) * mm});
            skLineSegment(sketch, "E1148", {"start": v(76.23, -56.25) * mm, "end": v(76.1, -56) * mm});
            skLineSegment(sketch, "E1149", {"start": v(76.1, -56) * mm, "end": v(75.66, -55.26) * mm});
            skLineSegment(sketch, "E1150", {"start": v(75.66, -55.26) * mm, "end": v(75.05, -54.26) * mm});
            skLineSegment(sketch, "E1151", {"start": v(75.05, -54.26) * mm, "end": v(74.42, -53.28) * mm});
            skLineSegment(sketch, "E1152", {"start": v(76.52, -56.76) * mm, "end": v(76.23, -56.25) * mm});
            skLineSegment(sketch, "E1153", {"start": v(77.33, -58.33) * mm, "end": v(76.52, -56.76) * mm});
            skLineSegment(sketch, "E1154", {"start": v(78.36, -60.46) * mm, "end": v(77.33, -58.33) * mm});
            skLineSegment(sketch, "E1155", {"start": v(79.3, -62.6) * mm, "end": v(78.36, -60.46) * mm});
            skLineSegment(sketch, "E1156", {"start": v(80.13, -64.66) * mm, "end": v(79.3, -62.6) * mm});
            skLineSegment(sketch, "E1157", {"start": v(80.83, -66.6) * mm, "end": v(80.13, -64.66) * mm});
            skLineSegment(sketch, "E1158", {"start": v(58.13, -71.2) * mm, "end": v(58.25, -71.22) * mm});
            skLineSegment(sketch, "E1159", {"start": v(71.25, -67.5) * mm, "end": v(72.8, -68.06) * mm});
            skLineSegment(sketch, "E1160", {"start": v(54.84, -70.46) * mm, "end": v(55.62, -70.66) * mm});
            skLineSegment(sketch, "E1161", {"start": v(58.02, -71.19) * mm, "end": v(58.13, -71.2) * mm});
            skLineSegment(sketch, "E1162", {"start": v(54.09, -70.25) * mm, "end": v(54.84, -70.46) * mm});
            skLineSegment(sketch, "E1163", {"start": v(53.43, -70.03) * mm, "end": v(54.09, -70.25) * mm});
            skLineSegment(sketch, "E1164", {"start": v(53.05, -69.89) * mm, "end": v(53.43, -70.03) * mm});
            skLineSegment(sketch, "E1165", {"start": v(52.93, -69.83) * mm, "end": v(53.05, -69.89) * mm});
            skLineSegment(sketch, "E1166", {"start": v(52.88, -69.8) * mm, "end": v(52.93, -69.83) * mm});
            skLineSegment(sketch, "E1167", {"start": v(52.74, -69.72) * mm, "end": v(52.88, -69.8) * mm});
            skLineSegment(sketch, "E1168", {"start": v(52.38, -69.5) * mm, "end": v(52.74, -69.72) * mm});
            skLineSegment(sketch, "E1169", {"start": v(51.87, -69.17) * mm, "end": v(52.38, -69.5) * mm});
            skLineSegment(sketch, "E1170", {"start": v(51.23, -68.72) * mm, "end": v(51.87, -69.17) * mm});
            skLineSegment(sketch, "E1171", {"start": v(50.48, -68.17) * mm, "end": v(51.23, -68.72) * mm});
            skLineSegment(sketch, "E1172", {"start": v(49.62, -67.52) * mm, "end": v(50.48, -68.17) * mm});
            skLineSegment(sketch, "E1173", {"start": v(42.22, -52.97) * mm, "end": v(41.55, -53.34) * mm});
            skLineSegment(sketch, "E1174", {"start": v(43.24, -52.66) * mm, "end": v(42.22, -52.97) * mm});
            skLineSegment(sketch, "E1175", {"start": v(44.34, -52.64) * mm, "end": v(43.24, -52.66) * mm});
            skLineSegment(sketch, "E1176", {"start": v(45.17, -52.85) * mm, "end": v(44.34, -52.64) * mm});
            skLineSegment(sketch, "E1177", {"start": v(45.42, -52.98) * mm, "end": v(45.17, -52.85) * mm});
            skLineSegment(sketch, "E1178", {"start": v(45.77, -53.17) * mm, "end": v(45.42, -52.98) * mm});
            skLineSegment(sketch, "E1179", {"start": v(46.82, -53.72) * mm, "end": v(45.77, -53.17) * mm});
            skLineSegment(sketch, "E1180", {"start": v(48.46, -54.54) * mm, "end": v(46.82, -53.72) * mm});
            skLineSegment(sketch, "E1181", {"start": v(72.13, -63.44) * mm, "end": v(73.34, -63.92) * mm});
            skLineSegment(sketch, "E1182", {"start": v(70.65, -62.85) * mm, "end": v(72.13, -63.44) * mm});
            skLineSegment(sketch, "E1183", {"start": v(68.94, -62.16) * mm, "end": v(70.65, -62.85) * mm});
            skLineSegment(sketch, "E1184", {"start": v(67.03, -61.38) * mm, "end": v(68.94, -62.16) * mm});
            skLineSegment(sketch, "E1185", {"start": v(64.97, -60.53) * mm, "end": v(67.03, -61.38) * mm});
            skLineSegment(sketch, "E1186", {"start": v(62.79, -59.6) * mm, "end": v(64.97, -60.53) * mm});
            skLineSegment(sketch, "E1187", {"start": v(60.52, -58.64) * mm, "end": v(62.79, -59.6) * mm});
            skLineSegment(sketch, "E1188", {"start": v(58.2, -57.62) * mm, "end": v(60.52, -58.64) * mm});
            skLineSegment(sketch, "E1189", {"start": v(55.88, -56.58) * mm, "end": v(58.2, -57.62) * mm});
            skLineSegment(sketch, "E1190", {"start": v(53.58, -55.52) * mm, "end": v(55.88, -56.58) * mm});
            skLineSegment(sketch, "E1191", {"start": v(51.34, -54.45) * mm, "end": v(53.58, -55.52) * mm});
            skLineSegment(sketch, "E1192", {"start": v(49.2, -53.4) * mm, "end": v(51.34, -54.45) * mm});
            skLineSegment(sketch, "E1193", {"start": v(47.68, -52.61) * mm, "end": v(49.2, -53.4) * mm});
            skLineSegment(sketch, "E1194", {"start": v(47.18, -52.35) * mm, "end": v(47.68, -52.61) * mm});
            skLineSegment(sketch, "E1195", {"start": v(47.3, -52.28) * mm, "end": v(47.18, -52.35) * mm});
            skLineSegment(sketch, "E1196", {"start": v(47.67, -52.12) * mm, "end": v(47.3, -52.28) * mm});
            skLineSegment(sketch, "E1197", {"start": v(48.4, -51.84) * mm, "end": v(47.67, -52.12) * mm});
            skLineSegment(sketch, "E1198", {"start": v(49.35, -51.52) * mm, "end": v(48.4, -51.84) * mm});
            skLineSegment(sketch, "E1199", {"start": v(50.48, -51.18) * mm, "end": v(49.35, -51.52) * mm});
            skLineSegment(sketch, "E1200", {"start": v(51.75, -50.81) * mm, "end": v(50.48, -51.18) * mm});
            skLineSegment(sketch, "E1201", {"start": v(53.15, -50.44) * mm, "end": v(51.75, -50.81) * mm});
            skLineSegment(sketch, "E1202", {"start": v(54.64, -50.07) * mm, "end": v(53.15, -50.44) * mm});
            skLineSegment(sketch, "E1203", {"start": v(55.8, -49.8) * mm, "end": v(54.64, -50.07) * mm});
            skLineSegment(sketch, "E1204", {"start": v(56.18, -49.72) * mm, "end": v(55.8, -49.8) * mm});
            skLineSegment(sketch, "E1205", {"start": v(71.29, -49.67) * mm, "end": v(70.63, -49.4) * mm});
            skLineSegment(sketch, "E1206", {"start": v(71.74, -49.9) * mm, "end": v(71.29, -49.67) * mm});
            skLineSegment(sketch, "E1207", {"start": v(71.92, -50.03) * mm, "end": v(71.74, -49.9) * mm});
            skLineSegment(sketch, "E1208", {"start": v(71.98, -50.07) * mm, "end": v(71.92, -50.03) * mm});
            skLineSegment(sketch, "E1209", {"start": v(72.07, -50.13) * mm, "end": v(71.98, -50.07) * mm});
            skLineSegment(sketch, "E1210", {"start": v(72.28, -50.36) * mm, "end": v(72.07, -50.13) * mm});
            skLineSegment(sketch, "E1211", {"start": v(74.42, -53.28) * mm, "end": v(73.8, -52.37) * mm});
            skLineSegment(sketch, "E1212", {"start": v(73.8, -52.37) * mm, "end": v(73.22, -51.55) * mm});
            skLineSegment(sketch, "E1213", {"start": v(73.22, -51.55) * mm, "end": v(72.7, -50.87) * mm});
            skLineSegment(sketch, "E1214", {"start": v(72.7, -50.87) * mm, "end": v(72.28, -50.36) * mm});
            skLineSegment(sketch, "E1215", {"start": v(70.63, -49.4) * mm, "end": v(69.75, -49.12) * mm});
            skLineSegment(sketch, "E1216", {"start": v(69.75, -49.12) * mm, "end": v(68.63, -48.88) * mm});
            skLineSegment(sketch, "E1217", {"start": v(68.63, -48.88) * mm, "end": v(67.28, -48.7) * mm});
            skLineSegment(sketch, "E1218", {"start": v(67.28, -48.7) * mm, "end": v(65.67, -48.64) * mm});
            skLineSegment(sketch, "E1219", {"start": v(65.67, -48.64) * mm, "end": v(64.26, -48.67) * mm});
            skLineSegment(sketch, "E1220", {"start": v(64.26, -48.67) * mm, "end": v(63.8, -48.7) * mm});
            skLineSegment(sketch, "E1221", {"start": v(63.8, -48.7) * mm, "end": v(63.34, -48.74) * mm});
            skLineSegment(sketch, "E1222", {"start": v(63.34, -48.74) * mm, "end": v(62, -48.86) * mm});
            skLineSegment(sketch, "E1223", {"start": v(62, -48.86) * mm, "end": v(60.09, -49.07) * mm});
            skLineSegment(sketch, "E1224", {"start": v(60.09, -49.07) * mm, "end": v(58.13, -49.35) * mm});
            skLineSegment(sketch, "E1225", {"start": v(58.13, -49.35) * mm, "end": v(56.67, -49.61) * mm});
            skLineSegment(sketch, "E1226", {"start": v(56.67, -49.61) * mm, "end": v(56.18, -49.72) * mm});
            skLineSegment(sketch, "E1227", {"start": v(73.34, -63.92) * mm, "end": v(74.26, -64.27) * mm});
            skLineSegment(sketch, "E1228", {"start": v(74.26, -64.27) * mm, "end": v(74.83, -64.5) * mm});
            skLineSegment(sketch, "E1229", {"start": v(74.83, -64.5) * mm, "end": v(75.03, -64.57) * mm});
            skLineSegment(sketch, "E1230", {"start": v(75.03, -64.57) * mm, "end": v(57.7, -54.74) * mm});
            skLineSegment(sketch, "E1231", {"start": v(57.7, -54.74) * mm, "end": v(57.86, -54.7) * mm});
            skLineSegment(sketch, "E1232", {"start": v(57.86, -54.7) * mm, "end": v(58.3, -54.56) * mm});
            skLineSegment(sketch, "E1233", {"start": v(58.3, -54.56) * mm, "end": v(58.96, -54.38) * mm});
            skLineSegment(sketch, "E1234", {"start": v(58.96, -54.38) * mm, "end": v(59.82, -54.15) * mm});
            skLineSegment(sketch, "E1235", {"start": v(59.82, -54.15) * mm, "end": v(60.84, -53.92) * mm});
            skLineSegment(sketch, "E1236", {"start": v(60.84, -53.92) * mm, "end": v(61.97, -53.7) * mm});
            skLineSegment(sketch, "E1237", {"start": v(61.97, -53.7) * mm, "end": v(63.17, -53.5) * mm});
            skLineSegment(sketch, "E1238", {"start": v(63.17, -53.5) * mm, "end": v(64.1, -53.4) * mm});
            skLineSegment(sketch, "E1239", {"start": v(64.1, -53.4) * mm, "end": v(64.4, -53.37) * mm});
            skLineSegment(sketch, "E1240", {"start": v(64.4, -53.37) * mm, "end": v(64.84, -53.33) * mm});
            skLineSegment(sketch, "E1241", {"start": v(64.84, -53.33) * mm, "end": v(66.15, -53.32) * mm});
            skLineSegment(sketch, "E1242", {"start": v(66.15, -53.32) * mm, "end": v(67.66, -53.45) * mm});
            skLineSegment(sketch, "E1243", {"start": v(67.66, -53.45) * mm, "end": v(68.94, -53.73) * mm});
            skLineSegment(sketch, "E1244", {"start": v(68.94, -53.73) * mm, "end": v(69.74, -54) * mm});
            skLineSegment(sketch, "E1245", {"start": v(69.74, -54) * mm, "end": v(70, -54.13) * mm});
            skLineSegment(sketch, "E1246", {"start": v(70, -54.13) * mm, "end": v(70.18, -54.22) * mm});
            skLineSegment(sketch, "E1247", {"start": v(70.18, -54.22) * mm, "end": v(70.7, -54.52) * mm});
            skLineSegment(sketch, "E1248", {"start": v(70.7, -54.52) * mm, "end": v(71.52, -55.12) * mm});
            skLineSegment(sketch, "E1249", {"start": v(71.52, -55.12) * mm, "end": v(72.42, -56) * mm});
            skLineSegment(sketch, "E1250", {"start": v(72.42, -56) * mm, "end": v(73.16, -56.93) * mm});
            skLineSegment(sketch, "E1251", {"start": v(73.16, -56.93) * mm, "end": v(73.37, -57.25) * mm});
            skLineSegment(sketch, "E1252", {"start": v(73.37, -57.25) * mm, "end": v(73.64, -57.64) * mm});
            skLineSegment(sketch, "E1253", {"start": v(73.64, -57.64) * mm, "end": v(74.38, -58.84) * mm});
            skLineSegment(sketch, "E1254", {"start": v(74.38, -58.84) * mm, "end": v(75.26, -60.39) * mm});
            skLineSegment(sketch, "E1255", {"start": v(75.26, -60.39) * mm, "end": v(76.02, -61.87) * mm});
            skLineSegment(sketch, "E1256", {"start": v(76.02, -61.87) * mm, "end": v(76.67, -63.24) * mm});
            skLineSegment(sketch, "E1257", {"start": v(76.67, -63.24) * mm, "end": v(77.19, -64.47) * mm});
            skLineSegment(sketch, "E1258", {"start": v(77.19, -64.47) * mm, "end": v(77.6, -65.51) * mm});
            skLineSegment(sketch, "E1259", {"start": v(77.6, -65.51) * mm, "end": v(77.88, -66.33) * mm});
            skLineSegment(sketch, "E1260", {"start": v(77.88, -66.33) * mm, "end": v(78.01, -66.75) * mm});
            skLineSegment(sketch, "E1261", {"start": v(78.01, -66.75) * mm, "end": v(78.05, -66.9) * mm});
            skLineSegment(sketch, "E1262", {"start": v(78.05, -66.9) * mm, "end": v(77.64, -66.78) * mm});
            skLineSegment(sketch, "E1263", {"start": v(77.64, -66.78) * mm, "end": v(76.44, -66.42) * mm});
            skLineSegment(sketch, "E1264", {"start": v(76.44, -66.42) * mm, "end": v(74.63, -65.82) * mm});
            skLineSegment(sketch, "E1265", {"start": v(74.63, -65.82) * mm, "end": v(72.65, -65.1) * mm});
            skLineSegment(sketch, "E1266", {"start": v(72.65, -65.1) * mm, "end": v(70.54, -64.3) * mm});
            skLineSegment(sketch, "E1267", {"start": v(70.54, -64.3) * mm, "end": v(68.31, -63.43) * mm});
            skLineSegment(sketch, "E1268", {"start": v(68.31, -63.43) * mm, "end": v(66.01, -62.5) * mm});
            skLineSegment(sketch, "E1269", {"start": v(66.01, -62.5) * mm, "end": v(63.67, -61.5) * mm});
            skLineSegment(sketch, "E1270", {"start": v(63.67, -61.5) * mm, "end": v(61.3, -60.49) * mm});
            skLineSegment(sketch, "E1271", {"start": v(61.3, -60.49) * mm, "end": v(58.95, -59.45) * mm});
            skLineSegment(sketch, "E1272", {"start": v(58.95, -59.45) * mm, "end": v(56.64, -58.42) * mm});
            skLineSegment(sketch, "E1273", {"start": v(56.64, -58.42) * mm, "end": v(54.4, -57.4) * mm});
            skLineSegment(sketch, "E1274", {"start": v(54.4, -57.4) * mm, "end": v(52.28, -56.4) * mm});
            skLineSegment(sketch, "E1275", {"start": v(16.28, -102.07) * mm, "end": v(16.44, -102.42) * mm});
            skLineSegment(sketch, "E1276", {"start": v(15.86, -101.01) * mm, "end": v(16.28, -102.07) * mm});
            skLineSegment(sketch, "E1277", {"start": v(15.41, -99.74) * mm, "end": v(15.86, -101.01) * mm});
            skLineSegment(sketch, "E1278", {"start": v(15.14, -98.72) * mm, "end": v(15.41, -99.74) * mm});
            skLineSegment(sketch, "E1279", {"start": v(15.04, -98.2) * mm, "end": v(15.14, -98.72) * mm});
            skLineSegment(sketch, "E1280", {"start": v(15.05, -98.05) * mm, "end": v(15.04, -98.2) * mm});
            skLineSegment(sketch, "E1281", {"start": v(15.05, -97.92) * mm, "end": v(15.05, -98.05) * mm});
            skLineSegment(sketch, "E1282", {"start": v(15.1, -97.55) * mm, "end": v(15.05, -97.92) * mm});
            skLineSegment(sketch, "E1283", {"start": v(15.23, -96.85) * mm, "end": v(15.1, -97.55) * mm});
            skLineSegment(sketch, "E1284", {"start": v(15.44, -95.96) * mm, "end": v(15.23, -96.85) * mm});
            skLineSegment(sketch, "E1285", {"start": v(15.67, -95.2) * mm, "end": v(15.44, -95.96) * mm});
            skLineSegment(sketch, "E1286", {"start": v(15.76, -94.94) * mm, "end": v(15.67, -95.2) * mm});
            skLineSegment(sketch, "E1287", {"start": v(15.83, -94.73) * mm, "end": v(15.76, -94.94) * mm});
            skLineSegment(sketch, "E1288", {"start": v(16.06, -94.1) * mm, "end": v(15.83, -94.73) * mm});
            skLineSegment(sketch, "E1289", {"start": v(16.37, -93.27) * mm, "end": v(16.06, -94.1) * mm});
            skLineSegment(sketch, "E1290", {"start": v(16.7, -92.47) * mm, "end": v(16.37, -93.27) * mm});
            skLineSegment(sketch, "E1291", {"start": v(17, -91.73) * mm, "end": v(16.7, -92.47) * mm});
            skLineSegment(sketch, "E1292", {"start": v(17.26, -91.1) * mm, "end": v(17, -91.73) * mm});
            skLineSegment(sketch, "E1293", {"start": v(17.47, -90.6) * mm, "end": v(17.26, -91.1) * mm});
            skLineSegment(sketch, "E1294", {"start": v(17.61, -90.28) * mm, "end": v(17.47, -90.6) * mm});
            skLineSegment(sketch, "E1295", {"start": v(17.66, -90.17) * mm, "end": v(17.61, -90.28) * mm});
            skLineSegment(sketch, "E1296", {"start": v(17.66, -90.38) * mm, "end": v(17.66, -90.17) * mm});
            skLineSegment(sketch, "E1297", {"start": v(17.67, -90.98) * mm, "end": v(17.66, -90.38) * mm});
            skLineSegment(sketch, "E1298", {"start": v(17.7, -91.9) * mm, "end": v(17.67, -90.98) * mm});
            skLineSegment(sketch, "E1299", {"start": v(17.72, -93.08) * mm, "end": v(17.7, -91.9) * mm});
            skLineSegment(sketch, "E1300", {"start": v(17.75, -94.44) * mm, "end": v(17.72, -93.08) * mm});
            skLineSegment(sketch, "E1301", {"start": v(17.8, -95.93) * mm, "end": v(17.75, -94.44) * mm});
            skLineSegment(sketch, "E1302", {"start": v(17.86, -97.47) * mm, "end": v(17.8, -95.93) * mm});
            skLineSegment(sketch, "E1303", {"start": v(17.92, -98.62) * mm, "end": v(17.86, -97.47) * mm});
            skLineSegment(sketch, "E1304", {"start": v(17.94, -99) * mm, "end": v(17.92, -98.62) * mm});
            skLineSegment(sketch, "E1305", {"start": v(17.96, -99.38) * mm, "end": v(17.94, -99) * mm});
            skLineSegment(sketch, "E1306", {"start": v(18.03, -100.51) * mm, "end": v(17.96, -99.38) * mm});
            skLineSegment(sketch, "E1307", {"start": v(18.14, -101.92) * mm, "end": v(18.03, -100.51) * mm});
            skLineSegment(sketch, "E1308", {"start": v(18.24, -103.2) * mm, "end": v(18.14, -101.92) * mm});
            skLineSegment(sketch, "E1309", {"start": v(18.34, -104.3) * mm, "end": v(18.24, -103.2) * mm});
            skLineSegment(sketch, "E1310", {"start": v(18.43, -105.22) * mm, "end": v(18.34, -104.3) * mm});
            skLineSegment(sketch, "E1311", {"start": v(18.5, -105.91) * mm, "end": v(18.43, -105.22) * mm});
            skLineSegment(sketch, "E1312", {"start": v(18.55, -106.35) * mm, "end": v(18.5, -105.91) * mm});
            skLineSegment(sketch, "E1313", {"start": v(18.57, -106.5) * mm, "end": v(18.55, -106.35) * mm});
            skLineSegment(sketch, "E1314", {"start": v(18.52, -106.4) * mm, "end": v(18.57, -106.5) * mm});
            skLineSegment(sketch, "E1315", {"start": v(18.37, -106.15) * mm, "end": v(18.52, -106.4) * mm});
            skLineSegment(sketch, "E1316", {"start": v(18.14, -105.74) * mm, "end": v(18.37, -106.15) * mm});
            skLineSegment(sketch, "E1317", {"start": v(17.85, -105.22) * mm, "end": v(18.14, -105.74) * mm});
            skLineSegment(sketch, "E1318", {"start": v(17.51, -104.6) * mm, "end": v(17.85, -105.22) * mm});
            skLineSegment(sketch, "E1319", {"start": v(17.16, -103.9) * mm, "end": v(17.51, -104.6) * mm});
            skLineSegment(sketch, "E1320", {"start": v(16.8, -103.17) * mm, "end": v(17.16, -103.9) * mm});
            skLineSegment(sketch, "E1321", {"start": v(16.53, -102.6) * mm, "end": v(16.8, -103.17) * mm});
            skLineSegment(sketch, "E1322", {"start": v(16.44, -102.42) * mm, "end": v(16.53, -102.6) * mm});
            skLineSegment(sketch, "E1323", {"start": v(35.34, -108.81) * mm, "end": v(35.96, -108.8) * mm});
            skLineSegment(sketch, "E1324", {"start": v(33.47, -108.83) * mm, "end": v(35.34, -108.81) * mm});
            skLineSegment(sketch, "E1325", {"start": v(31.1, -108.85) * mm, "end": v(33.47, -108.83) * mm});
            skLineSegment(sketch, "E1326", {"start": v(28.89, -108.88) * mm, "end": v(31.1, -108.85) * mm});
            skLineSegment(sketch, "E1327", {"start": v(26.88, -108.95) * mm, "end": v(28.89, -108.88) * mm});
            skLineSegment(sketch, "E1328", {"start": v(25.12, -109.1) * mm, "end": v(26.88, -108.95) * mm});
            skLineSegment(sketch, "E1329", {"start": v(23.67, -109.35) * mm, "end": v(25.12, -109.1) * mm});
            skLineSegment(sketch, "E1330", {"start": v(22.55, -109.73) * mm, "end": v(23.67, -109.35) * mm});
            skLineSegment(sketch, "E1331", {"start": v(21.97, -110.1) * mm, "end": v(22.55, -109.73) * mm});
            skLineSegment(sketch, "E1332", {"start": v(21.83, -110.26) * mm, "end": v(21.97, -110.1) * mm});
            skLineSegment(sketch, "E1333", {"start": v(21.75, -110.36) * mm, "end": v(21.83, -110.26) * mm});
            skLineSegment(sketch, "E1334", {"start": v(21.64, -110.72) * mm, "end": v(21.75, -110.36) * mm});
            skLineSegment(sketch, "E1335", {"start": v(21.5, -111.5) * mm, "end": v(21.64, -110.72) * mm});
            skLineSegment(sketch, "E1336", {"start": v(21.42, -112.53) * mm, "end": v(21.5, -111.5) * mm});
            skLineSegment(sketch, "E1337", {"start": v(21.38, -113.72) * mm, "end": v(21.42, -112.53) * mm});
            skLineSegment(sketch, "E1338", {"start": v(21.39, -114.99) * mm, "end": v(21.38, -113.72) * mm});
            skLineSegment(sketch, "E1339", {"start": v(21.43, -116.26) * mm, "end": v(21.39, -114.99) * mm});
            skLineSegment(sketch, "E1340", {"start": v(21.51, -117.45) * mm, "end": v(21.43, -116.26) * mm});
            skLineSegment(sketch, "E1341", {"start": v(21.6, -118.22) * mm, "end": v(21.51, -117.45) * mm});
            skLineSegment(sketch, "E1342", {"start": v(21.63, -118.47) * mm, "end": v(21.6, -118.22) * mm});
            skLineSegment(sketch, "E1343", {"start": v(21.38, -118.06) * mm, "end": v(21.63, -118.47) * mm});
            skLineSegment(sketch, "E1344", {"start": v(20.77, -116.75) * mm, "end": v(21.38, -118.06) * mm});
            skLineSegment(sketch, "E1345", {"start": v(20.08, -114.76) * mm, "end": v(20.77, -116.75) * mm});
            skLineSegment(sketch, "E1346", {"start": v(19.6, -112.66) * mm, "end": v(20.08, -114.76) * mm});
            skLineSegment(sketch, "E1347", {"start": v(19.38, -111.1) * mm, "end": v(19.6, -112.66) * mm});
            skLineSegment(sketch, "E1348", {"start": v(19.36, -110.58) * mm, "end": v(19.38, -111.1) * mm});
            skLineSegment(sketch, "E1349", {"start": v(19.33, -110.09) * mm, "end": v(19.36, -110.58) * mm});
            skLineSegment(sketch, "E1350", {"start": v(19.36, -108.6) * mm, "end": v(19.33, -110.09) * mm});
            skLineSegment(sketch, "E1351", {"start": v(19.5, -106.63) * mm, "end": v(19.36, -108.6) * mm});
            skLineSegment(sketch, "E1352", {"start": v(19.74, -104.77) * mm, "end": v(19.5, -106.63) * mm});
            skLineSegment(sketch, "E1353", {"start": v(19.94, -103.53) * mm, "end": v(19.74, -104.77) * mm});
            skLineSegment(sketch, "E1354", {"start": v(20, -103.12) * mm, "end": v(19.94, -103.53) * mm});
            skLineSegment(sketch, "E1355", {"start": v(20.08, -102.68) * mm, "end": v(20, -103.12) * mm});
            skLineSegment(sketch, "E1356", {"start": v(20.32, -101.35) * mm, "end": v(20.08, -102.68) * mm});
            skLineSegment(sketch, "E1357", {"start": v(20.54, -100) * mm, "end": v(20.32, -101.35) * mm});
            skLineSegment(sketch, "E1358", {"start": v(20.6, -99.02) * mm, "end": v(20.54, -100) * mm});
            skLineSegment(sketch, "E1359", {"start": v(20.5, -98.5) * mm, "end": v(20.6, -99.02) * mm});
            skLineSegment(sketch, "E1360", {"start": v(20.42, -98.37) * mm, "end": v(20.5, -98.5) * mm});
            skLineSegment(sketch, "E1361", {"start": v(20.6, -98.53) * mm, "end": v(20.42, -98.37) * mm});
            skLineSegment(sketch, "E1362", {"start": v(21.07, -99.13) * mm, "end": v(20.6, -98.53) * mm});
            skLineSegment(sketch, "E1363", {"start": v(21.7, -100.2) * mm, "end": v(21.07, -99.13) * mm});
            skLineSegment(sketch, "E1364", {"start": v(22.31, -101.45) * mm, "end": v(21.7, -100.2) * mm});
            skLineSegment(sketch, "E1365", {"start": v(22.9, -102.76) * mm, "end": v(22.31, -101.45) * mm});
            skLineSegment(sketch, "E1366", {"start": v(23.47, -104.02) * mm, "end": v(22.9, -102.76) * mm});
            skLineSegment(sketch, "E1367", {"start": v(24.02, -105.1) * mm, "end": v(23.47, -104.02) * mm});
            skLineSegment(sketch, "E1368", {"start": v(24.55, -105.87) * mm, "end": v(24.02, -105.1) * mm});
            skLineSegment(sketch, "E1369", {"start": v(24.92, -106.2) * mm, "end": v(24.55, -105.87) * mm});
            skLineSegment(sketch, "E1370", {"start": v(25.06, -106.23) * mm, "end": v(24.92, -106.2) * mm});
            skLineSegment(sketch, "E1371", {"start": v(25.28, -106.23) * mm, "end": v(25.06, -106.23) * mm});
            skLineSegment(sketch, "E1372", {"start": v(25.93, -106.23) * mm, "end": v(25.28, -106.23) * mm});
            skLineSegment(sketch, "E1373", {"start": v(26.99, -106.19) * mm, "end": v(25.93, -106.23) * mm});
            skLineSegment(sketch, "E1374", {"start": v(28.21, -106.11) * mm, "end": v(26.99, -106.19) * mm});
            skLineSegment(sketch, "E1375", {"start": v(29.57, -106) * mm, "end": v(28.21, -106.11) * mm});
            skLineSegment(sketch, "E1376", {"start": v(31.04, -105.87) * mm, "end": v(29.57, -106) * mm});
            skLineSegment(sketch, "E1377", {"start": v(32.57, -105.72) * mm, "end": v(31.04, -105.87) * mm});
            skLineSegment(sketch, "E1378", {"start": v(34.15, -105.54) * mm, "end": v(32.57, -105.72) * mm});
            skLineSegment(sketch, "E1379", {"start": v(35.35, -105.4) * mm, "end": v(34.15, -105.54) * mm});
            skLineSegment(sketch, "E1380", {"start": v(35.75, -105.35) * mm, "end": v(35.35, -105.4) * mm});
            skLineSegment(sketch, "E1381", {"start": v(36.18, -105.3) * mm, "end": v(35.75, -105.35) * mm});
            skLineSegment(sketch, "E1382", {"start": v(37.47, -105.13) * mm, "end": v(36.18, -105.3) * mm});
            skLineSegment(sketch, "E1383", {"start": v(39.14, -104.91) * mm, "end": v(37.47, -105.13) * mm});
            skLineSegment(sketch, "E1384", {"start": v(40.71, -104.7) * mm, "end": v(39.14, -104.91) * mm});
            skLineSegment(sketch, "E1385", {"start": v(42.15, -104.5) * mm, "end": v(40.71, -104.7) * mm});
            skLineSegment(sketch, "E1386", {"start": v(57.5, -117.07) * mm, "end": v(59.5, -117.45) * mm});
            skLineSegment(sketch, "E1387", {"start": v(55.32, -116.69) * mm, "end": v(57.5, -117.07) * mm});
            skLineSegment(sketch, "E1388", {"start": v(66.48, -116.76) * mm, "end": v(66.63, -116.56) * mm});
            skLineSegment(sketch, "E1389", {"start": v(66.63, -116.56) * mm, "end": v(66.53, -116.52) * mm});
            skLineSegment(sketch, "E1390", {"start": v(66.53, -116.52) * mm, "end": v(66.24, -116.43) * mm});
            skLineSegment(sketch, "E1391", {"start": v(66.24, -116.43) * mm, "end": v(65.62, -116.26) * mm});
            skLineSegment(sketch, "E1392", {"start": v(65.62, -116.26) * mm, "end": v(64.8, -116.04) * mm});
            skLineSegment(sketch, "E1393", {"start": v(64.8, -116.04) * mm, "end": v(63.78, -115.79) * mm});
            skLineSegment(sketch, "E1394", {"start": v(63.78, -115.79) * mm, "end": v(62.58, -115.5) * mm});
            skLineSegment(sketch, "E1395", {"start": v(62.58, -115.5) * mm, "end": v(61.23, -115.19) * mm});
            skLineSegment(sketch, "E1396", {"start": v(61.23, -115.19) * mm, "end": v(59.73, -114.85) * mm});
            skLineSegment(sketch, "E1397", {"start": v(59.73, -114.85) * mm, "end": v(58.5, -114.6) * mm});
            skLineSegment(sketch, "E1398", {"start": v(58.5, -114.6) * mm, "end": v(58.1, -114.5) * mm});
            skLineSegment(sketch, "E1399", {"start": v(58.1, -114.5) * mm, "end": v(57.37, -114.36) * mm});
            skLineSegment(sketch, "E1400", {"start": v(57.37, -114.36) * mm, "end": v(55.16, -113.93) * mm});
            skLineSegment(sketch, "E1401", {"start": v(55.16, -113.93) * mm, "end": v(51.99, -113.35) * mm});
            skLineSegment(sketch, "E1402", {"start": v(51.99, -113.35) * mm, "end": v(48.64, -112.8) * mm});
            skLineSegment(sketch, "E1403", {"start": v(48.64, -112.8) * mm, "end": v(46.05, -112.4) * mm});
            skLineSegment(sketch, "E1404", {"start": v(46.05, -112.4) * mm, "end": v(45.2, -112.29) * mm});
            skLineSegment(sketch, "E1405", {"start": v(45.2, -112.29) * mm, "end": v(44.26, -112.16) * mm});
            skLineSegment(sketch, "E1406", {"start": v(44.26, -112.16) * mm, "end": v(39.77, -111.6) * mm});
            skLineSegment(sketch, "E1407", {"start": v(39.77, -111.6) * mm, "end": v(35.46, -111.18) * mm});
            skLineSegment(sketch, "E1408", {"start": v(35.46, -111.18) * mm, "end": v(34.62, -111.1) * mm});
            skLineSegment(sketch, "E1409", {"start": v(35.96, -108.8) * mm, "end": v(36.17, -108.8) * mm});
            skLineSegment(sketch, "E1410", {"start": v(36.17, -108.8) * mm, "end": v(36.8, -108.78) * mm});
            skLineSegment(sketch, "E1411", {"start": v(36.8, -108.78) * mm, "end": v(37.95, -108.77) * mm});
            skLineSegment(sketch, "E1412", {"start": v(37.95, -108.77) * mm, "end": v(39.35, -108.78) * mm});
            skLineSegment(sketch, "E1413", {"start": v(39.35, -108.78) * mm, "end": v(40.98, -108.8) * mm});
            skLineSegment(sketch, "E1414", {"start": v(40.98, -108.8) * mm, "end": v(42.8, -108.85) * mm});
            skLineSegment(sketch, "E1415", {"start": v(42.8, -108.85) * mm, "end": v(44.8, -108.94) * mm});
            skLineSegment(sketch, "E1416", {"start": v(44.8, -108.94) * mm, "end": v(46.95, -109.07) * mm});
            skLineSegment(sketch, "E1417", {"start": v(46.95, -109.07) * mm, "end": v(49.21, -109.25) * mm});
            skLineSegment(sketch, "E1418", {"start": v(49.21, -109.25) * mm, "end": v(51.56, -109.5) * mm});
            skLineSegment(sketch, "E1419", {"start": v(51.56, -109.5) * mm, "end": v(53.96, -109.8) * mm});
            skLineSegment(sketch, "E1420", {"start": v(53.96, -109.8) * mm, "end": v(56.39, -110.18) * mm});
            skLineSegment(sketch, "E1421", {"start": v(56.39, -110.18) * mm, "end": v(58.81, -110.64) * mm});
            skLineSegment(sketch, "E1422", {"start": v(58.81, -110.64) * mm, "end": v(61.2, -111.2) * mm});
            skLineSegment(sketch, "E1423", {"start": v(61.2, -111.2) * mm, "end": v(63.55, -111.84) * mm});
            skLineSegment(sketch, "E1424", {"start": v(63.55, -111.84) * mm, "end": v(65.8, -112.6) * mm});
            skLineSegment(sketch, "E1425", {"start": v(65.8, -112.6) * mm, "end": v(67.4, -113.23) * mm});
            skLineSegment(sketch, "E1426", {"start": v(67.4, -113.23) * mm, "end": v(67.93, -113.47) * mm});
            skLineSegment(sketch, "E1427", {"start": v(67.93, -113.47) * mm, "end": v(67.62, -113.16) * mm});
            skLineSegment(sketch, "E1428", {"start": v(67.62, -113.16) * mm, "end": v(66.64, -112.28) * mm});
            skLineSegment(sketch, "E1429", {"start": v(66.64, -112.28) * mm, "end": v(65.3, -111.18) * mm});
            skLineSegment(sketch, "E1430", {"start": v(65.3, -111.18) * mm, "end": v(63.93, -110.16) * mm});
            skLineSegment(sketch, "E1431", {"start": v(63.93, -110.16) * mm, "end": v(62.55, -109.23) * mm});
            skLineSegment(sketch, "E1432", {"start": v(62.55, -109.23) * mm, "end": v(61.17, -108.37) * mm});
            skLineSegment(sketch, "E1433", {"start": v(61.17, -108.37) * mm, "end": v(59.8, -107.6) * mm});
            skLineSegment(sketch, "E1434", {"start": v(59.8, -107.6) * mm, "end": v(58.48, -106.9) * mm});
            skLineSegment(sketch, "E1435", {"start": v(58.48, -106.9) * mm, "end": v(57.21, -106.27) * mm});
            skLineSegment(sketch, "E1436", {"start": v(57.21, -106.27) * mm, "end": v(56.02, -105.72) * mm});
            skLineSegment(sketch, "E1437", {"start": v(56.02, -105.72) * mm, "end": v(54.9, -105.25) * mm});
            skLineSegment(sketch, "E1438", {"start": v(48.28, -103.83) * mm, "end": v(47.48, -103.86) * mm});
            skLineSegment(sketch, "E1439", {"start": v(47.48, -103.86) * mm, "end": v(46.76, -103.9) * mm});
            skLineSegment(sketch, "E1440", {"start": v(46.76, -103.9) * mm, "end": v(46.15, -103.94) * mm});
            skLineSegment(sketch, "E1441", {"start": v(46.15, -103.94) * mm, "end": v(45.83, -103.97) * mm});
            skLineSegment(sketch, "E1442", {"start": v(25.32, -110.56) * mm, "end": v(24.15, -110.53) * mm});
            skLineSegment(sketch, "E1443", {"start": v(24.15, -110.53) * mm, "end": v(23.3, -110.53) * mm});
            skLineSegment(sketch, "E1444", {"start": v(23.3, -110.53) * mm, "end": v(22.94, -110.54) * mm});
            skLineSegment(sketch, "E1445", {"start": v(32.42, -110.94) * mm, "end": v(30.36, -110.8) * mm});
            skLineSegment(sketch, "E1446", {"start": v(45.6, -104) * mm, "end": v(45.23, -104.05) * mm});
            skLineSegment(sketch, "E1447", {"start": v(22.94, -110.54) * mm, "end": v(22.81, -110.55) * mm});
            skLineSegment(sketch, "E1448", {"start": v(30.36, -110.8) * mm, "end": v(28.46, -110.69) * mm});
            skLineSegment(sketch, "E1449", {"start": v(45.23, -104.05) * mm, "end": v(44.45, -104.16) * mm});
            skLineSegment(sketch, "E1450", {"start": v(22.81, -110.55) * mm, "end": v(22.92, -110.83) * mm});
            skLineSegment(sketch, "E1451", {"start": v(28.46, -110.69) * mm, "end": v(26.77, -110.6) * mm});
            skLineSegment(sketch, "E1452", {"start": v(44.45, -104.16) * mm, "end": v(43.4, -104.31) * mm});
            skLineSegment(sketch, "E1453", {"start": v(22.92, -110.83) * mm, "end": v(23.31, -111.63) * mm});
            skLineSegment(sketch, "E1454", {"start": v(26.77, -110.6) * mm, "end": v(25.32, -110.56) * mm});
            skLineSegment(sketch, "E1455", {"start": v(43.4, -104.31) * mm, "end": v(42.15, -104.5) * mm});
            skLineSegment(sketch, "E1456", {"start": v(34.62, -111.1) * mm, "end": v(34.07, -111.06) * mm});
            skLineSegment(sketch, "E1457", {"start": v(23.31, -111.63) * mm, "end": v(24.08, -112.96) * mm});
            skLineSegment(sketch, "E1458", {"start": v(24.08, -112.96) * mm, "end": v(25.08, -114.49) * mm});
            skLineSegment(sketch, "E1459", {"start": v(32.28, -123.23) * mm, "end": v(32.48, -123.43) * mm});
            skLineSegment(sketch, "E1460", {"start": v(32.48, -123.43) * mm, "end": v(33.09, -124.03) * mm});
            skLineSegment(sketch, "E1461", {"start": v(33.09, -124.03) * mm, "end": v(33.95, -124.83) * mm});
            skLineSegment(sketch, "E1462", {"start": v(33.95, -124.83) * mm, "end": v(34.82, -125.6) * mm});
            skLineSegment(sketch, "E1463", {"start": v(31.86, -122.81) * mm, "end": v(32.28, -123.23) * mm});
            skLineSegment(sketch, "E1464", {"start": v(30.66, -121.52) * mm, "end": v(31.86, -122.81) * mm});
            skLineSegment(sketch, "E1465", {"start": v(29.1, -119.74) * mm, "end": v(30.66, -121.52) * mm});
            skLineSegment(sketch, "E1466", {"start": v(27.63, -117.94) * mm, "end": v(29.1, -119.74) * mm});
            skLineSegment(sketch, "E1467", {"start": v(26.27, -116.17) * mm, "end": v(27.63, -117.94) * mm});
            skLineSegment(sketch, "E1468", {"start": v(25.08, -114.49) * mm, "end": v(26.27, -116.17) * mm});
            skLineSegment(sketch, "E1469", {"start": v(45.73, -103.98) * mm, "end": v(45.6, -104) * mm});
            skLineSegment(sketch, "E1470", {"start": v(34.07, -111.06) * mm, "end": v(32.42, -110.94) * mm});
            skLineSegment(sketch, "E1471", {"start": v(49.1, -103.82) * mm, "end": v(48.28, -103.83) * mm});
            skLineSegment(sketch, "E1472", {"start": v(45.83, -103.97) * mm, "end": v(45.73, -103.98) * mm});
            skLineSegment(sketch, "E1473", {"start": v(49.87, -103.82) * mm, "end": v(49.1, -103.82) * mm});
            skLineSegment(sketch, "E1474", {"start": v(50.56, -103.85) * mm, "end": v(49.87, -103.82) * mm});
            skLineSegment(sketch, "E1475", {"start": v(50.97, -103.9) * mm, "end": v(50.56, -103.85) * mm});
            skLineSegment(sketch, "E1476", {"start": v(51.1, -103.91) * mm, "end": v(50.97, -103.9) * mm});
            skLineSegment(sketch, "E1477", {"start": v(51.16, -103.92) * mm, "end": v(51.1, -103.91) * mm});
            skLineSegment(sketch, "E1478", {"start": v(51.32, -103.97) * mm, "end": v(51.16, -103.92) * mm});
            skLineSegment(sketch, "E1479", {"start": v(51.72, -104.08) * mm, "end": v(51.32, -103.97) * mm});
            skLineSegment(sketch, "E1480", {"start": v(52.3, -104.27) * mm, "end": v(51.72, -104.08) * mm});
            skLineSegment(sketch, "E1481", {"start": v(53.03, -104.53) * mm, "end": v(52.3, -104.27) * mm});
            skLineSegment(sketch, "E1482", {"start": v(53.9, -104.85) * mm, "end": v(53.03, -104.53) * mm});
            skLineSegment(sketch, "E1483", {"start": v(54.9, -105.25) * mm, "end": v(53.9, -104.85) * mm});
            skLineSegment(sketch, "E1484", {"start": v(65.93, -117.3) * mm, "end": v(66.48, -116.76) * mm});
            skLineSegment(sketch, "E1485", {"start": v(65.03, -117.87) * mm, "end": v(65.93, -117.3) * mm});
            skLineSegment(sketch, "E1486", {"start": v(63.98, -118.18) * mm, "end": v(65.03, -117.87) * mm});
            skLineSegment(sketch, "E1487", {"start": v(63.12, -118.2) * mm, "end": v(63.98, -118.18) * mm});
            skLineSegment(sketch, "E1488", {"start": v(62.85, -118.14) * mm, "end": v(63.12, -118.2) * mm});
            skLineSegment(sketch, "E1489", {"start": v(62.46, -118.05) * mm, "end": v(62.85, -118.14) * mm});
            skLineSegment(sketch, "E1490", {"start": v(61.3, -117.8) * mm, "end": v(62.46, -118.05) * mm});
            skLineSegment(sketch, "E1491", {"start": v(59.5, -117.45) * mm, "end": v(61.3, -117.8) * mm});
            skLineSegment(sketch, "E1492", {"start": v(34.31, -115.2) * mm, "end": v(33.01, -115.07) * mm});
            skLineSegment(sketch, "E1493", {"start": v(35.9, -115.38) * mm, "end": v(34.31, -115.2) * mm});
            skLineSegment(sketch, "E1494", {"start": v(37.73, -115.59) * mm, "end": v(35.9, -115.38) * mm});
            skLineSegment(sketch, "E1495", {"start": v(39.77, -115.83) * mm, "end": v(37.73, -115.59) * mm});
            skLineSegment(sketch, "E1496", {"start": v(41.99, -116.1) * mm, "end": v(39.77, -115.83) * mm});
            skLineSegment(sketch, "E1497", {"start": v(44.33, -116.4) * mm, "end": v(41.99, -116.1) * mm});
            skLineSegment(sketch, "E1498", {"start": v(46.78, -116.73) * mm, "end": v(44.33, -116.4) * mm});
            skLineSegment(sketch, "E1499", {"start": v(49.28, -117.09) * mm, "end": v(46.78, -116.73) * mm});
            skLineSegment(sketch, "E1500", {"start": v(51.8, -117.47) * mm, "end": v(49.28, -117.09) * mm});
            skLineSegment(sketch, "E1501", {"start": v(54.3, -117.88) * mm, "end": v(51.8, -117.47) * mm});
            skLineSegment(sketch, "E1502", {"start": v(56.75, -118.3) * mm, "end": v(54.3, -117.88) * mm});
            skLineSegment(sketch, "E1503", {"start": v(59.1, -118.75) * mm, "end": v(56.75, -118.3) * mm});
            skLineSegment(sketch, "E1504", {"start": v(60.76, -119.1) * mm, "end": v(59.1, -118.75) * mm});
            skLineSegment(sketch, "E1505", {"start": v(61.32, -119.22) * mm, "end": v(60.76, -119.1) * mm});
            skLineSegment(sketch, "E1506", {"start": v(61.22, -119.32) * mm, "end": v(61.32, -119.22) * mm});
            skLineSegment(sketch, "E1507", {"start": v(60.9, -119.58) * mm, "end": v(61.22, -119.32) * mm});
            skLineSegment(sketch, "E1508", {"start": v(60.27, -120.04) * mm, "end": v(60.9, -119.58) * mm});
            skLineSegment(sketch, "E1509", {"start": v(59.44, -120.6) * mm, "end": v(60.27, -120.04) * mm});
            skLineSegment(sketch, "E1510", {"start": v(58.45, -121.23) * mm, "end": v(59.44, -120.6) * mm});
            skLineSegment(sketch, "E1511", {"start": v(57.32, -121.93) * mm, "end": v(58.45, -121.23) * mm});
            skLineSegment(sketch, "E1512", {"start": v(56.07, -122.66) * mm, "end": v(57.32, -121.93) * mm});
            skLineSegment(sketch, "E1513", {"start": v(54.74, -123.41) * mm, "end": v(56.07, -122.66) * mm});
            skLineSegment(sketch, "E1514", {"start": v(53.7, -123.98) * mm, "end": v(54.74, -123.41) * mm});
            skLineSegment(sketch, "E1515", {"start": v(53.34, -124.17) * mm, "end": v(53.7, -123.98) * mm});
            skLineSegment(sketch, "E1516", {"start": v(38.8, -128.25) * mm, "end": v(39.5, -128.33) * mm});
            skLineSegment(sketch, "E1517", {"start": v(38.3, -128.14) * mm, "end": v(38.8, -128.25) * mm});
            skLineSegment(sketch, "E1518", {"start": v(38.1, -128.08) * mm, "end": v(38.3, -128.14) * mm});
            skLineSegment(sketch, "E1519", {"start": v(38.02, -128.05) * mm, "end": v(38.1, -128.08) * mm});
            skLineSegment(sketch, "E1520", {"start": v(37.93, -128.01) * mm, "end": v(38.02, -128.05) * mm});
            skLineSegment(sketch, "E1521", {"start": v(37.66, -127.85) * mm, "end": v(37.93, -128.01) * mm});
            skLineSegment(sketch, "E1522", {"start": v(34.82, -125.6) * mm, "end": v(35.66, -126.32) * mm});
            skLineSegment(sketch, "E1523", {"start": v(35.66, -126.32) * mm, "end": v(36.44, -126.95) * mm});
            skLineSegment(sketch, "E1524", {"start": v(36.44, -126.95) * mm, "end": v(37.11, -127.47) * mm});
            skLineSegment(sketch, "E1525", {"start": v(37.11, -127.47) * mm, "end": v(37.66, -127.85) * mm});
            skLineSegment(sketch, "E1526", {"start": v(39.5, -128.33) * mm, "end": v(40.43, -128.36) * mm});
            skLineSegment(sketch, "E1527", {"start": v(40.43, -128.36) * mm, "end": v(41.57, -128.3) * mm});
            skLineSegment(sketch, "E1528", {"start": v(41.57, -128.3) * mm, "end": v(42.92, -128.1) * mm});
            skLineSegment(sketch, "E1529", {"start": v(42.92, -128.1) * mm, "end": v(44.5, -127.74) * mm});
            skLineSegment(sketch, "E1530", {"start": v(44.5, -127.74) * mm, "end": v(45.84, -127.33) * mm});
            skLineSegment(sketch, "E1531", {"start": v(45.84, -127.33) * mm, "end": v(46.28, -127.17) * mm});
            skLineSegment(sketch, "E1532", {"start": v(46.28, -127.17) * mm, "end": v(46.7, -127.02) * mm});
            skLineSegment(sketch, "E1533", {"start": v(46.7, -127.02) * mm, "end": v(47.97, -126.55) * mm});
            skLineSegment(sketch, "E1534", {"start": v(47.97, -126.55) * mm, "end": v(49.75, -125.84) * mm});
            skLineSegment(sketch, "E1535", {"start": v(49.75, -125.84) * mm, "end": v(51.56, -125.04) * mm});
            skLineSegment(sketch, "E1536", {"start": v(51.56, -125.04) * mm, "end": v(52.9, -124.4) * mm});
            skLineSegment(sketch, "E1537", {"start": v(52.9, -124.4) * mm, "end": v(53.34, -124.17) * mm});
            skLineSegment(sketch, "E1538", {"start": v(33.01, -115.07) * mm, "end": v(32.04, -114.97) * mm});
            skLineSegment(sketch, "E1539", {"start": v(32.04, -114.97) * mm, "end": v(31.42, -114.9) * mm});
            skLineSegment(sketch, "E1540", {"start": v(31.42, -114.9) * mm, "end": v(31.21, -114.89) * mm});
            skLineSegment(sketch, "E1541", {"start": v(31.21, -114.89) * mm, "end": v(50.53, -119.73) * mm});
            skLineSegment(sketch, "E1542", {"start": v(50.53, -119.73) * mm, "end": v(50.4, -119.82) * mm});
            skLineSegment(sketch, "E1543", {"start": v(50.4, -119.82) * mm, "end": v(50.02, -120.06) * mm});
            skLineSegment(sketch, "E1544", {"start": v(50.02, -120.06) * mm, "end": v(49.42, -120.42) * mm});
            skLineSegment(sketch, "E1545", {"start": v(49.42, -120.42) * mm, "end": v(48.65, -120.86) * mm});
            skLineSegment(sketch, "E1546", {"start": v(48.65, -120.86) * mm, "end": v(47.74, -121.36) * mm});
            skLineSegment(sketch, "E1547", {"start": v(47.74, -121.36) * mm, "end": v(46.7, -121.88) * mm});
            skLineSegment(sketch, "E1548", {"start": v(46.7, -121.88) * mm, "end": v(45.6, -122.38) * mm});
            skLineSegment(sketch, "E1549", {"start": v(45.6, -122.38) * mm, "end": v(44.74, -122.74) * mm});
            skLineSegment(sketch, "E1550", {"start": v(44.74, -122.74) * mm, "end": v(44.45, -122.84) * mm});
            skLineSegment(sketch, "E1551", {"start": v(44.45, -122.84) * mm, "end": v(44.04, -123) * mm});
            skLineSegment(sketch, "E1552", {"start": v(44.04, -123) * mm, "end": v(42.78, -123.36) * mm});
            skLineSegment(sketch, "E1553", {"start": v(42.78, -123.36) * mm, "end": v(41.29, -123.64) * mm});
            skLineSegment(sketch, "E1554", {"start": v(41.29, -123.64) * mm, "end": v(39.98, -123.71) * mm});
            skLineSegment(sketch, "E1555", {"start": v(39.98, -123.71) * mm, "end": v(39.13, -123.66) * mm});
            skLineSegment(sketch, "E1556", {"start": v(39.13, -123.66) * mm, "end": v(38.86, -123.6) * mm});
            skLineSegment(sketch, "E1557", {"start": v(38.86, -123.6) * mm, "end": v(38.66, -123.57) * mm});
            skLineSegment(sketch, "E1558", {"start": v(38.66, -123.57) * mm, "end": v(38.06, -123.42) * mm});
            skLineSegment(sketch, "E1559", {"start": v(38.06, -123.42) * mm, "end": v(37.12, -123.06) * mm});
            skLineSegment(sketch, "E1560", {"start": v(37.12, -123.06) * mm, "end": v(36.02, -122.45) * mm});
            skLineSegment(sketch, "E1561", {"start": v(36.02, -122.45) * mm, "end": v(35.06, -121.76) * mm});
            skLineSegment(sketch, "E1562", {"start": v(35.06, -121.76) * mm, "end": v(34.76, -121.5) * mm});
            skLineSegment(sketch, "E1563", {"start": v(34.76, -121.5) * mm, "end": v(34.4, -121.2) * mm});
            skLineSegment(sketch, "E1564", {"start": v(34.4, -121.2) * mm, "end": v(33.37, -120.24) * mm});
            skLineSegment(sketch, "E1565", {"start": v(33.37, -120.24) * mm, "end": v(32.1, -118.98) * mm});
            skLineSegment(sketch, "E1566", {"start": v(32.1, -118.98) * mm, "end": v(30.98, -117.76) * mm});
            skLineSegment(sketch, "E1567", {"start": v(30.98, -117.76) * mm, "end": v(30, -116.6) * mm});
            skLineSegment(sketch, "E1568", {"start": v(30, -116.6) * mm, "end": v(29.16, -115.57) * mm});
            skLineSegment(sketch, "E1569", {"start": v(29.16, -115.57) * mm, "end": v(28.49, -114.67) * mm});
            skLineSegment(sketch, "E1570", {"start": v(28.49, -114.67) * mm, "end": v(28, -113.95) * mm});
            skLineSegment(sketch, "E1571", {"start": v(28, -113.95) * mm, "end": v(27.75, -113.58) * mm});
            skLineSegment(sketch, "E1572", {"start": v(27.75, -113.58) * mm, "end": v(27.68, -113.46) * mm});
            skLineSegment(sketch, "E1573", {"start": v(27.68, -113.46) * mm, "end": v(28.1, -113.46) * mm});
            skLineSegment(sketch, "E1574", {"start": v(28.1, -113.46) * mm, "end": v(29.36, -113.49) * mm});
            skLineSegment(sketch, "E1575", {"start": v(29.36, -113.49) * mm, "end": v(31.26, -113.58) * mm});
            skLineSegment(sketch, "E1576", {"start": v(31.26, -113.58) * mm, "end": v(33.36, -113.74) * mm});
            skLineSegment(sketch, "E1577", {"start": v(33.36, -113.74) * mm, "end": v(35.61, -113.94) * mm});
            skLineSegment(sketch, "E1578", {"start": v(35.61, -113.94) * mm, "end": v(37.99, -114.2) * mm});
            skLineSegment(sketch, "E1579", {"start": v(37.99, -114.2) * mm, "end": v(40.45, -114.48) * mm});
            skLineSegment(sketch, "E1580", {"start": v(40.45, -114.48) * mm, "end": v(42.98, -114.8) * mm});
            skLineSegment(sketch, "E1581", {"start": v(42.98, -114.8) * mm, "end": v(45.53, -115.15) * mm});
            skLineSegment(sketch, "E1582", {"start": v(45.53, -115.15) * mm, "end": v(48.07, -115.52) * mm});
            skLineSegment(sketch, "E1583", {"start": v(48.07, -115.52) * mm, "end": v(50.57, -115.9) * mm});
            skLineSegment(sketch, "E1584", {"start": v(50.57, -115.9) * mm, "end": v(53, -116.3) * mm});
            skLineSegment(sketch, "E1585", {"start": v(53, -116.3) * mm, "end": v(55.32, -116.69) * mm});
            skLineSegment(sketch, "E1586", {"start": v(-33.87, -122.57) * mm, "end": v(-33.49, -122.6) * mm});
            skLineSegment(sketch, "E1587", {"start": v(-35, -122.45) * mm, "end": v(-33.87, -122.57) * mm});
            skLineSegment(sketch, "E1588", {"start": v(-36.33, -122.25) * mm, "end": v(-35, -122.45) * mm});
            skLineSegment(sketch, "E1589", {"start": v(-37.37, -122.02) * mm, "end": v(-36.33, -122.25) * mm});
            skLineSegment(sketch, "E1590", {"start": v(-37.87, -121.86) * mm, "end": v(-37.37, -122.02) * mm});
            skLineSegment(sketch, "E1591", {"start": v(-38, -121.78) * mm, "end": v(-37.87, -121.86) * mm});
            skLineSegment(sketch, "E1592", {"start": v(-38.1, -121.72) * mm, "end": v(-38, -121.78) * mm});
            skLineSegment(sketch, "E1593", {"start": v(-38.41, -121.5) * mm, "end": v(-38.1, -121.72) * mm});
            skLineSegment(sketch, "E1594", {"start": v(-38.98, -121.07) * mm, "end": v(-38.41, -121.5) * mm});
            skLineSegment(sketch, "E1595", {"start": v(-39.66, -120.46) * mm, "end": v(-38.98, -121.07) * mm});
            skLineSegment(sketch, "E1596", {"start": v(-40.23, -119.9) * mm, "end": v(-39.66, -120.46) * mm});
            skLineSegment(sketch, "E1597", {"start": v(-40.41, -119.7) * mm, "end": v(-40.23, -119.9) * mm});
            skLineSegment(sketch, "E1598", {"start": v(-40.57, -119.55) * mm, "end": v(-40.41, -119.7) * mm});
            skLineSegment(sketch, "E1599", {"start": v(-41.01, -119.06) * mm, "end": v(-40.57, -119.55) * mm});
            skLineSegment(sketch, "E1600", {"start": v(-41.6, -118.39) * mm, "end": v(-41.01, -119.06) * mm});
            skLineSegment(sketch, "E1601", {"start": v(-42.17, -117.73) * mm, "end": v(-41.6, -118.39) * mm});
            skLineSegment(sketch, "E1602", {"start": v(-42.68, -117.12) * mm, "end": v(-42.17, -117.73) * mm});
            skLineSegment(sketch, "E1603", {"start": v(-43.12, -116.6) * mm, "end": v(-42.68, -117.12) * mm});
            skLineSegment(sketch, "E1604", {"start": v(-43.45, -116.17) * mm, "end": v(-43.12, -116.6) * mm});
            skLineSegment(sketch, "E1605", {"start": v(-43.67, -115.9) * mm, "end": v(-43.45, -116.17) * mm});
            skLineSegment(sketch, "E1606", {"start": v(-43.75, -115.8) * mm, "end": v(-43.67, -115.9) * mm});
            skLineSegment(sketch, "E1607", {"start": v(-43.56, -115.9) * mm, "end": v(-43.75, -115.8) * mm});
            skLineSegment(sketch, "E1608", {"start": v(-43.03, -116.17) * mm, "end": v(-43.56, -115.9) * mm});
            skLineSegment(sketch, "E1609", {"start": v(-42.2, -116.58) * mm, "end": v(-43.03, -116.17) * mm});
            skLineSegment(sketch, "E1610", {"start": v(-41.15, -117.1) * mm, "end": v(-42.2, -116.58) * mm});
            skLineSegment(sketch, "E1611", {"start": v(-39.93, -117.7) * mm, "end": v(-41.15, -117.1) * mm});
            skLineSegment(sketch, "E1612", {"start": v(-38.6, -118.36) * mm, "end": v(-39.93, -117.7) * mm});
            skLineSegment(sketch, "E1613", {"start": v(-37.2, -119.02) * mm, "end": v(-38.6, -118.36) * mm});
            skLineSegment(sketch, "E1614", {"start": v(-36.16, -119.51) * mm, "end": v(-37.2, -119.02) * mm});
            skLineSegment(sketch, "E1615", {"start": v(-35.8, -119.67) * mm, "end": v(-36.16, -119.51) * mm});
            skLineSegment(sketch, "E1616", {"start": v(-35.46, -119.83) * mm, "end": v(-35.8, -119.67) * mm});
            skLineSegment(sketch, "E1617", {"start": v(-34.43, -120.3) * mm, "end": v(-35.46, -119.83) * mm});
            skLineSegment(sketch, "E1618", {"start": v(-33.13, -120.86) * mm, "end": v(-34.43, -120.3) * mm});
            skLineSegment(sketch, "E1619", {"start": v(-31.96, -121.36) * mm, "end": v(-33.13, -120.86) * mm});
            skLineSegment(sketch, "E1620", {"start": v(-30.93, -121.79) * mm, "end": v(-31.96, -121.36) * mm});
            skLineSegment(sketch, "E1621", {"start": v(-30.07, -122.14) * mm, "end": v(-30.93, -121.79) * mm});
            skLineSegment(sketch, "E1622", {"start": v(-29.43, -122.4) * mm, "end": v(-30.07, -122.14) * mm});
            skLineSegment(sketch, "E1623", {"start": v(-29.02, -122.56) * mm, "end": v(-29.43, -122.4) * mm});
            skLineSegment(sketch, "E1624", {"start": v(-28.88, -122.61) * mm, "end": v(-29.02, -122.56) * mm});
            skLineSegment(sketch, "E1625", {"start": v(-28.99, -122.62) * mm, "end": v(-28.88, -122.61) * mm});
            skLineSegment(sketch, "E1626", {"start": v(-29.29, -122.63) * mm, "end": v(-28.99, -122.62) * mm});
            skLineSegment(sketch, "E1627", {"start": v(-29.76, -122.64) * mm, "end": v(-29.29, -122.63) * mm});
            skLineSegment(sketch, "E1628", {"start": v(-30.36, -122.65) * mm, "end": v(-29.76, -122.64) * mm});
            skLineSegment(sketch, "E1629", {"start": v(-31.06, -122.66) * mm, "end": v(-30.36, -122.65) * mm});
            skLineSegment(sketch, "E1630", {"start": v(-31.84, -122.65) * mm, "end": v(-31.06, -122.66) * mm});
            skLineSegment(sketch, "E1631", {"start": v(-32.66, -122.63) * mm, "end": v(-31.84, -122.65) * mm});
            skLineSegment(sketch, "E1632", {"start": v(-33.28, -122.6) * mm, "end": v(-32.66, -122.63) * mm});
            skLineSegment(sketch, "E1633", {"start": v(-33.49, -122.6) * mm, "end": v(-33.28, -122.6) * mm});
            skLineSegment(sketch, "E1634", {"start": v(-19.02, -108.86) * mm, "end": v(-18.74, -108.3) * mm});
            skLineSegment(sketch, "E1635", {"start": v(-19.87, -110.52) * mm, "end": v(-19.02, -108.86) * mm});
            skLineSegment(sketch, "E1636", {"start": v(-20.96, -112.62) * mm, "end": v(-19.87, -110.52) * mm});
            skLineSegment(sketch, "E1637", {"start": v(-21.97, -114.6) * mm, "end": v(-20.96, -112.62) * mm});
            skLineSegment(sketch, "E1638", {"start": v(-22.84, -116.4) * mm, "end": v(-21.97, -114.6) * mm});
            skLineSegment(sketch, "E1639", {"start": v(-23.53, -118.03) * mm, "end": v(-22.84, -116.4) * mm});
            skLineSegment(sketch, "E1640", {"start": v(-23.99, -119.43) * mm, "end": v(-23.53, -118.03) * mm});
            skLineSegment(sketch, "E1641", {"start": v(-24.17, -120.6) * mm, "end": v(-23.99, -119.43) * mm});
            skLineSegment(sketch, "E1642", {"start": v(-24.12, -121.28) * mm, "end": v(-24.17, -120.6) * mm});
            skLineSegment(sketch, "E1643", {"start": v(-24.03, -121.48) * mm, "end": v(-24.12, -121.28) * mm});
            skLineSegment(sketch, "E1644", {"start": v(-23.99, -121.6) * mm, "end": v(-24.03, -121.48) * mm});
            skLineSegment(sketch, "E1645", {"start": v(-23.72, -121.87) * mm, "end": v(-23.99, -121.6) * mm});
            skLineSegment(sketch, "E1646", {"start": v(-23.09, -122.35) * mm, "end": v(-23.72, -121.87) * mm});
            skLineSegment(sketch, "E1647", {"start": v(-22.22, -122.9) * mm, "end": v(-23.09, -122.35) * mm});
            skLineSegment(sketch, "E1648", {"start": v(-21.18, -123.5) * mm, "end": v(-22.22, -122.9) * mm});
            skLineSegment(sketch, "E1649", {"start": v(-20.06, -124.08) * mm, "end": v(-21.18, -123.5) * mm});
            skLineSegment(sketch, "E1650", {"start": v(-18.91, -124.63) * mm, "end": v(-20.06, -124.08) * mm});
            skLineSegment(sketch, "E1651", {"start": v(-17.82, -125.11) * mm, "end": v(-18.91, -124.63) * mm});
            skLineSegment(sketch, "E1652", {"start": v(-17.1, -125.4) * mm, "end": v(-17.82, -125.11) * mm});
            skLineSegment(sketch, "E1653", {"start": v(-16.86, -125.5) * mm, "end": v(-17.1, -125.4) * mm});
            skLineSegment(sketch, "E1654", {"start": v(-17.34, -125.52) * mm, "end": v(-16.86, -125.5) * mm});
            skLineSegment(sketch, "E1655", {"start": v(-18.79, -125.44) * mm, "end": v(-17.34, -125.52) * mm});
            skLineSegment(sketch, "E1656", {"start": v(-20.87, -125.13) * mm, "end": v(-18.79, -125.44) * mm});
            skLineSegment(sketch, "E1657", {"start": v(-22.95, -124.58) * mm, "end": v(-20.87, -125.13) * mm});
            skLineSegment(sketch, "E1658", {"start": v(-24.43, -124.04) * mm, "end": v(-22.95, -124.58) * mm});
            skLineSegment(sketch, "E1659", {"start": v(-24.9, -123.82) * mm, "end": v(-24.43, -124.04) * mm});
            skLineSegment(sketch, "E1660", {"start": v(-25.35, -123.61) * mm, "end": v(-24.9, -123.82) * mm});
            skLineSegment(sketch, "E1661", {"start": v(-26.65, -122.9) * mm, "end": v(-25.35, -123.61) * mm});
            skLineSegment(sketch, "E1662", {"start": v(-28.33, -121.84) * mm, "end": v(-26.65, -122.9) * mm});
            skLineSegment(sketch, "E1663", {"start": v(-29.86, -120.77) * mm, "end": v(-28.33, -121.84) * mm});
            skLineSegment(sketch, "E1664", {"start": v(-30.87, -120.02) * mm, "end": v(-29.86, -120.77) * mm});
            skLineSegment(sketch, "E1665", {"start": v(-31.2, -119.76) * mm, "end": v(-30.87, -120.02) * mm});
            skLineSegment(sketch, "E1666", {"start": v(-31.56, -119.5) * mm, "end": v(-31.2, -119.76) * mm});
            skLineSegment(sketch, "E1667", {"start": v(-32.62, -118.66) * mm, "end": v(-31.56, -119.5) * mm});
            skLineSegment(sketch, "E1668", {"start": v(-33.72, -117.84) * mm, "end": v(-32.62, -118.66) * mm});
            skLineSegment(sketch, "E1669", {"start": v(-34.56, -117.33) * mm, "end": v(-33.72, -117.84) * mm});
            skLineSegment(sketch, "E1670", {"start": v(-35.05, -117.17) * mm, "end": v(-34.56, -117.33) * mm});
            skLineSegment(sketch, "E1671", {"start": v(-35.2, -117.19) * mm, "end": v(-35.05, -117.17) * mm});
            skLineSegment(sketch, "E1672", {"start": v(-34.98, -117.1) * mm, "end": v(-35.2, -117.19) * mm});
            skLineSegment(sketch, "E1673", {"start": v(-34.23, -116.96) * mm, "end": v(-34.98, -117.1) * mm});
            skLineSegment(sketch, "E1674", {"start": v(-33, -116.9) * mm, "end": v(-34.23, -116.96) * mm});
            skLineSegment(sketch, "E1675", {"start": v(-31.6, -116.95) * mm, "end": v(-33, -116.9) * mm});
            skLineSegment(sketch, "E1676", {"start": v(-30.17, -117.04) * mm, "end": v(-31.6, -116.95) * mm});
            skLineSegment(sketch, "E1677", {"start": v(-28.79, -117.12) * mm, "end": v(-30.17, -117.04) * mm});
            skLineSegment(sketch, "E1678", {"start": v(-27.58, -117.14) * mm, "end": v(-28.79, -117.12) * mm});
            skLineSegment(sketch, "E1679", {"start": v(-26.65, -117.03) * mm, "end": v(-27.58, -117.14) * mm});
            skLineSegment(sketch, "E1680", {"start": v(-26.19, -116.85) * mm, "end": v(-26.65, -117.03) * mm});
            skLineSegment(sketch, "E1681", {"start": v(-26.1, -116.74) * mm, "end": v(-26.19, -116.85) * mm});
            skLineSegment(sketch, "E1682", {"start": v(-25.99, -116.55) * mm, "end": v(-26.1, -116.74) * mm});
            skLineSegment(sketch, "E1683", {"start": v(-25.7, -115.98) * mm, "end": v(-25.99, -116.55) * mm});
            skLineSegment(sketch, "E1684", {"start": v(-25.23, -115.02) * mm, "end": v(-25.7, -115.98) * mm});
            skLineSegment(sketch, "E1685", {"start": v(-24.73, -113.9) * mm, "end": v(-25.23, -115.02) * mm});
            skLineSegment(sketch, "E1686", {"start": v(-24.19, -112.65) * mm, "end": v(-24.73, -113.9) * mm});
            skLineSegment(sketch, "E1687", {"start": v(-23.62, -111.3) * mm, "end": v(-24.19, -112.65) * mm});
            skLineSegment(sketch, "E1688", {"start": v(-23.04, -109.86) * mm, "end": v(-23.62, -111.3) * mm});
            skLineSegment(sketch, "E1689", {"start": v(-22.46, -108.38) * mm, "end": v(-23.04, -109.86) * mm});
            skLineSegment(sketch, "E1690", {"start": v(-22.03, -107.26) * mm, "end": v(-22.46, -108.38) * mm});
            skLineSegment(sketch, "E1691", {"start": v(-21.89, -106.88) * mm, "end": v(-22.03, -107.26) * mm});
            skLineSegment(sketch, "E1692", {"start": v(-21.73, -106.47) * mm, "end": v(-21.89, -106.88) * mm});
            skLineSegment(sketch, "E1693", {"start": v(-21.27, -105.25) * mm, "end": v(-21.73, -106.47) * mm});
            skLineSegment(sketch, "E1694", {"start": v(-20.7, -103.67) * mm, "end": v(-21.27, -105.25) * mm});
            skLineSegment(sketch, "E1695", {"start": v(-20.15, -102.18) * mm, "end": v(-20.7, -103.67) * mm});
            skLineSegment(sketch, "E1696", {"start": v(-19.66, -100.82) * mm, "end": v(-20.15, -102.18) * mm});
            skLineSegment(sketch, "E1697", {"start": v(-1.37, -93.11) * mm, "end": v(-0.1, -91.51) * mm});
            skLineSegment(sketch, "E1698", {"start": v(-2.73, -94.86) * mm, "end": v(-1.37, -93.11) * mm});
            skLineSegment(sketch, "E1699", {"start": v(2.54, -85.02) * mm, "end": v(2.43, -84.8) * mm});
            skLineSegment(sketch, "E1700", {"start": v(2.43, -84.8) * mm, "end": v(2.35, -84.86) * mm});
            skLineSegment(sketch, "E1701", {"start": v(2.35, -84.86) * mm, "end": v(2.14, -85.08) * mm});
            skLineSegment(sketch, "E1702", {"start": v(2.14, -85.08) * mm, "end": v(1.7, -85.54) * mm});
            skLineSegment(sketch, "E1703", {"start": v(1.7, -85.54) * mm, "end": v(1.12, -86.17) * mm});
            skLineSegment(sketch, "E1704", {"start": v(1.12, -86.17) * mm, "end": v(0.42, -86.95) * mm});
            skLineSegment(sketch, "E1705", {"start": v(0.42, -86.95) * mm, "end": v(-0.4, -87.88) * mm});
            skLineSegment(sketch, "E1706", {"start": v(-0.4, -87.88) * mm, "end": v(-1.3, -88.93) * mm});
            skLineSegment(sketch, "E1707", {"start": v(-1.3, -88.93) * mm, "end": v(-2.3, -90.1) * mm});
            skLineSegment(sketch, "E1708", {"start": v(-2.3, -90.1) * mm, "end": v(-3.1, -91.06) * mm});
            skLineSegment(sketch, "E1709", {"start": v(-3.1, -91.06) * mm, "end": v(-3.36, -91.38) * mm});
            skLineSegment(sketch, "E1710", {"start": v(-3.36, -91.38) * mm, "end": v(-3.84, -91.96) * mm});
            skLineSegment(sketch, "E1711", {"start": v(-3.84, -91.96) * mm, "end": v(-5.25, -93.7) * mm});
            skLineSegment(sketch, "E1712", {"start": v(-5.25, -93.7) * mm, "end": v(-7.24, -96.24) * mm});
            skLineSegment(sketch, "E1713", {"start": v(-7.24, -96.24) * mm, "end": v(-9.29, -98.94) * mm});
            skLineSegment(sketch, "E1714", {"start": v(-9.29, -98.94) * mm, "end": v(-10.84, -101.05) * mm});
            skLineSegment(sketch, "E1715", {"start": v(-10.84, -101.05) * mm, "end": v(-11.35, -101.76) * mm});
            skLineSegment(sketch, "E1716", {"start": v(-11.35, -101.76) * mm, "end": v(-11.9, -102.53) * mm});
            skLineSegment(sketch, "E1717", {"start": v(-11.9, -102.53) * mm, "end": v(-14.48, -106.24) * mm});
            skLineSegment(sketch, "E1718", {"start": v(-14.48, -106.24) * mm, "end": v(-16.87, -109.85) * mm});
            skLineSegment(sketch, "E1719", {"start": v(-16.87, -109.85) * mm, "end": v(-17.32, -110.56) * mm});
            skLineSegment(sketch, "E1720", {"start": v(-18.74, -108.3) * mm, "end": v(-18.64, -108.11) * mm});
            skLineSegment(sketch, "E1721", {"start": v(-18.64, -108.11) * mm, "end": v(-18.35, -107.54) * mm});
            skLineSegment(sketch, "E1722", {"start": v(-18.35, -107.54) * mm, "end": v(-17.83, -106.53) * mm});
            skLineSegment(sketch, "E1723", {"start": v(-17.83, -106.53) * mm, "end": v(-17.18, -105.3) * mm});
            skLineSegment(sketch, "E1724", {"start": v(-17.18, -105.3) * mm, "end": v(-16.4, -103.86) * mm});
            skLineSegment(sketch, "E1725", {"start": v(-16.4, -103.86) * mm, "end": v(-15.5, -102.27) * mm});
            skLineSegment(sketch, "E1726", {"start": v(-15.5, -102.27) * mm, "end": v(-14.49, -100.54) * mm});
            skLineSegment(sketch, "E1727", {"start": v(-14.49, -100.54) * mm, "end": v(-13.37, -98.7) * mm});
            skLineSegment(sketch, "E1728", {"start": v(-13.37, -98.7) * mm, "end": v(-12.16, -96.79) * mm});
            skLineSegment(sketch, "E1729", {"start": v(-12.16, -96.79) * mm, "end": v(-10.85, -94.83) * mm});
            skLineSegment(sketch, "E1730", {"start": v(-10.85, -94.83) * mm, "end": v(-9.46, -92.85) * mm});
            skLineSegment(sketch, "E1731", {"start": v(-9.46, -92.85) * mm, "end": v(-7.99, -90.88) * mm});
            skLineSegment(sketch, "E1732", {"start": v(-7.99, -90.88) * mm, "end": v(-6.45, -88.94) * mm});
            skLineSegment(sketch, "E1733", {"start": v(-6.45, -88.94) * mm, "end": v(-4.84, -87.08) * mm});
            skLineSegment(sketch, "E1734", {"start": v(-4.84, -87.08) * mm, "end": v(-3.18, -85.32) * mm});
            skLineSegment(sketch, "E1735", {"start": v(-3.18, -85.32) * mm, "end": v(-1.46, -83.68) * mm});
            skLineSegment(sketch, "E1736", {"start": v(-1.46, -83.68) * mm, "end": v(-0.15, -82.55) * mm});
            skLineSegment(sketch, "E1737", {"start": v(-0.15, -82.55) * mm, "end": v(0.3, -82.2) * mm});
            skLineSegment(sketch, "E1738", {"start": v(0.3, -82.2) * mm, "end": v(-0.11, -82.33) * mm});
            skLineSegment(sketch, "E1739", {"start": v(-0.11, -82.33) * mm, "end": v(-1.35, -82.79) * mm});
            skLineSegment(sketch, "E1740", {"start": v(-1.35, -82.79) * mm, "end": v(-2.94, -83.46) * mm});
            skLineSegment(sketch, "E1741", {"start": v(-2.94, -83.46) * mm, "end": v(-4.48, -84.2) * mm});
            skLineSegment(sketch, "E1742", {"start": v(-4.48, -84.2) * mm, "end": v(-5.96, -84.98) * mm});
            skLineSegment(sketch, "E1743", {"start": v(-5.96, -84.98) * mm, "end": v(-7.36, -85.8) * mm});
            skLineSegment(sketch, "E1744", {"start": v(-7.36, -85.8) * mm, "end": v(-8.68, -86.64) * mm});
            skLineSegment(sketch, "E1745", {"start": v(-8.68, -86.64) * mm, "end": v(-9.92, -87.49) * mm});
            skLineSegment(sketch, "E1746", {"start": v(-9.92, -87.49) * mm, "end": v(-11.06, -88.32) * mm});
            skLineSegment(sketch, "E1747", {"start": v(-11.06, -88.32) * mm, "end": v(-12.1, -89.12) * mm});
            skLineSegment(sketch, "E1748", {"start": v(-12.1, -89.12) * mm, "end": v(-13.04, -89.88) * mm});
            skLineSegment(sketch, "E1749", {"start": v(-17.39, -95.08) * mm, "end": v(-17.73, -95.8) * mm});
            skLineSegment(sketch, "E1750", {"start": v(-17.73, -95.8) * mm, "end": v(-18.04, -96.46) * mm});
            skLineSegment(sketch, "E1751", {"start": v(-18.04, -96.46) * mm, "end": v(-18.28, -97.02) * mm});
            skLineSegment(sketch, "E1752", {"start": v(-18.28, -97.02) * mm, "end": v(-18.4, -97.31) * mm});
            skLineSegment(sketch, "E1753", {"start": v(-22.14, -118.53) * mm, "end": v(-22.71, -119.55) * mm});
            skLineSegment(sketch, "E1754", {"start": v(-22.71, -119.55) * mm, "end": v(-23.1, -120.3) * mm});
            skLineSegment(sketch, "E1755", {"start": v(-23.1, -120.3) * mm, "end": v(-23.27, -120.63) * mm});
            skLineSegment(sketch, "E1756", {"start": v(-18.5, -112.43) * mm, "end": v(-19.58, -114.19) * mm});
            skLineSegment(sketch, "E1757", {"start": v(-18.49, -97.53) * mm, "end": v(-18.61, -97.88) * mm});
            skLineSegment(sketch, "E1758", {"start": v(-23.27, -120.63) * mm, "end": v(-23.31, -120.75) * mm});
            skLineSegment(sketch, "E1759", {"start": v(-19.58, -114.19) * mm, "end": v(-20.56, -115.82) * mm});
            skLineSegment(sketch, "E1760", {"start": v(-18.61, -97.88) * mm, "end": v(-18.88, -98.63) * mm});
            skLineSegment(sketch, "E1761", {"start": v(-23.31, -120.75) * mm, "end": v(-23.02, -120.78) * mm});
            skLineSegment(sketch, "E1762", {"start": v(-20.56, -115.82) * mm, "end": v(-21.42, -117.28) * mm});
            skLineSegment(sketch, "E1763", {"start": v(-18.88, -98.63) * mm, "end": v(-19.23, -99.62) * mm});
            skLineSegment(sketch, "E1764", {"start": v(-23.02, -120.78) * mm, "end": v(-22.13, -120.8) * mm});
            skLineSegment(sketch, "E1765", {"start": v(-21.42, -117.28) * mm, "end": v(-22.14, -118.53) * mm});
            skLineSegment(sketch, "E1766", {"start": v(-19.23, -99.62) * mm, "end": v(-19.66, -100.82) * mm});
            skLineSegment(sketch, "E1767", {"start": v(-17.32, -110.56) * mm, "end": v(-17.62, -111.03) * mm});
            skLineSegment(sketch, "E1768", {"start": v(-22.13, -120.8) * mm, "end": v(-20.6, -120.75) * mm});
            skLineSegment(sketch, "E1769", {"start": v(-20.6, -120.75) * mm, "end": v(-18.78, -120.58) * mm});
            skLineSegment(sketch, "E1770", {"start": v(-7.69, -118.3) * mm, "end": v(-7.42, -118.2) * mm});
            skLineSegment(sketch, "E1771", {"start": v(-7.42, -118.2) * mm, "end": v(-6.6, -117.94) * mm});
            skLineSegment(sketch, "E1772", {"start": v(-6.6, -117.94) * mm, "end": v(-5.5, -117.56) * mm});
            skLineSegment(sketch, "E1773", {"start": v(-5.5, -117.56) * mm, "end": v(-4.4, -117.15) * mm});
            skLineSegment(sketch, "E1774", {"start": v(-8.25, -118.46) * mm, "end": v(-7.69, -118.3) * mm});
            skLineSegment(sketch, "E1775", {"start": v(-9.95, -118.92) * mm, "end": v(-8.25, -118.46) * mm});
            skLineSegment(sketch, "E1776", {"start": v(-12.26, -119.47) * mm, "end": v(-9.95, -118.92) * mm});
            skLineSegment(sketch, "E1777", {"start": v(-14.54, -119.93) * mm, "end": v(-12.26, -119.47) * mm});
            skLineSegment(sketch, "E1778", {"start": v(-16.74, -120.3) * mm, "end": v(-14.54, -119.93) * mm});
            skLineSegment(sketch, "E1779", {"start": v(-18.78, -120.58) * mm, "end": v(-16.74, -120.3) * mm});
            skLineSegment(sketch, "E1780", {"start": v(-18.44, -97.41) * mm, "end": v(-18.49, -97.53) * mm});
            skLineSegment(sketch, "E1781", {"start": v(-17.62, -111.03) * mm, "end": v(-18.5, -112.43) * mm});
            skLineSegment(sketch, "E1782", {"start": v(-17.02, -94.36) * mm, "end": v(-17.39, -95.08) * mm});
            skLineSegment(sketch, "E1783", {"start": v(-18.4, -97.31) * mm, "end": v(-18.44, -97.41) * mm});
            skLineSegment(sketch, "E1784", {"start": v(-16.65, -93.67) * mm, "end": v(-17.02, -94.36) * mm});
            skLineSegment(sketch, "E1785", {"start": v(-16.3, -93.08) * mm, "end": v(-16.65, -93.67) * mm});
            skLineSegment(sketch, "E1786", {"start": v(-16.08, -92.73) * mm, "end": v(-16.3, -93.08) * mm});
            skLineSegment(sketch, "E1787", {"start": v(-16, -92.62) * mm, "end": v(-16.08, -92.73) * mm});
            skLineSegment(sketch, "E1788", {"start": v(-15.96, -92.58) * mm, "end": v(-16, -92.62) * mm});
            skLineSegment(sketch, "E1789", {"start": v(-15.85, -92.46) * mm, "end": v(-15.96, -92.58) * mm});
            skLineSegment(sketch, "E1790", {"start": v(-15.56, -92.16) * mm, "end": v(-15.85, -92.46) * mm});
            skLineSegment(sketch, "E1791", {"start": v(-15.12, -91.74) * mm, "end": v(-15.56, -92.16) * mm});
            skLineSegment(sketch, "E1792", {"start": v(-14.55, -91.2) * mm, "end": v(-15.12, -91.74) * mm});
            skLineSegment(sketch, "E1793", {"start": v(-13.86, -90.58) * mm, "end": v(-14.55, -91.2) * mm});
            skLineSegment(sketch, "E1794", {"start": v(-13.04, -89.88) * mm, "end": v(-13.86, -90.58) * mm});
            skLineSegment(sketch, "E1795", {"start": v(2.76, -85.75) * mm, "end": v(2.54, -85.02) * mm});
            skLineSegment(sketch, "E1796", {"start": v(2.84, -86.82) * mm, "end": v(2.76, -85.75) * mm});
            skLineSegment(sketch, "E1797", {"start": v(2.63, -87.9) * mm, "end": v(2.84, -86.82) * mm});
            skLineSegment(sketch, "E1798", {"start": v(2.24, -88.66) * mm, "end": v(2.63, -87.9) * mm});
            skLineSegment(sketch, "E1799", {"start": v(2.06, -88.87) * mm, "end": v(2.24, -88.66) * mm});
            skLineSegment(sketch, "E1800", {"start": v(1.8, -89.18) * mm, "end": v(2.06, -88.87) * mm});
            skLineSegment(sketch, "E1801", {"start": v(1.05, -90.1) * mm, "end": v(1.8, -89.18) * mm});
            skLineSegment(sketch, "E1802", {"start": v(-0.1, -91.51) * mm, "end": v(1.05, -90.1) * mm});
            skLineSegment(sketch, "E1803", {"start": v(-13.84, -112.75) * mm, "end": v(-14.56, -113.83) * mm});
            skLineSegment(sketch, "E1804", {"start": v(-12.94, -111.43) * mm, "end": v(-13.84, -112.75) * mm});
            skLineSegment(sketch, "E1805", {"start": v(-11.9, -109.9) * mm, "end": v(-12.94, -111.43) * mm});
            skLineSegment(sketch, "E1806", {"start": v(-10.74, -108.2) * mm, "end": v(-11.9, -109.9) * mm});
            skLineSegment(sketch, "E1807", {"start": v(-9.47, -106.37) * mm, "end": v(-10.74, -108.2) * mm});
            skLineSegment(sketch, "E1808", {"start": v(-8.1, -104.44) * mm, "end": v(-9.47, -106.37) * mm});
            skLineSegment(sketch, "E1809", {"start": v(-6.68, -102.43) * mm, "end": v(-8.1, -104.44) * mm});
            skLineSegment(sketch, "E1810", {"start": v(-5.2, -100.38) * mm, "end": v(-6.68, -102.43) * mm});
            skLineSegment(sketch, "E1811", {"start": v(-3.68, -98.33) * mm, "end": v(-5.2, -100.38) * mm});
            skLineSegment(sketch, "E1812", {"start": v(-2.15, -96.3) * mm, "end": v(-3.68, -98.33) * mm});
            skLineSegment(sketch, "E1813", {"start": v(-0.63, -94.35) * mm, "end": v(-2.15, -96.3) * mm});
            skLineSegment(sketch, "E1814", {"start": v(0.86, -92.48) * mm, "end": v(-0.63, -94.35) * mm});
            skLineSegment(sketch, "E1815", {"start": v(1.94, -91.17) * mm, "end": v(0.86, -92.48) * mm});
            skLineSegment(sketch, "E1816", {"start": v(2.31, -90.73) * mm, "end": v(1.94, -91.17) * mm});
            skLineSegment(sketch, "E1817", {"start": v(2.35, -90.86) * mm, "end": v(2.31, -90.73) * mm});
            skLineSegment(sketch, "E1818", {"start": v(2.43, -91.27) * mm, "end": v(2.35, -90.86) * mm});
            skLineSegment(sketch, "E1819", {"start": v(2.54, -92.04) * mm, "end": v(2.43, -91.27) * mm});
            skLineSegment(sketch, "E1820", {"start": v(2.65, -93.03) * mm, "end": v(2.54, -92.04) * mm});
            skLineSegment(sketch, "E1821", {"start": v(2.75, -94.2) * mm, "end": v(2.65, -93.03) * mm});
            skLineSegment(sketch, "E1822", {"start": v(2.84, -95.53) * mm, "end": v(2.75, -94.2) * mm});
            skLineSegment(sketch, "E1823", {"start": v(2.9, -96.97) * mm, "end": v(2.84, -95.53) * mm});
            skLineSegment(sketch, "E1824", {"start": v(2.95, -98.5) * mm, "end": v(2.9, -96.97) * mm});
            skLineSegment(sketch, "E1825", {"start": v(2.96, -99.7) * mm, "end": v(2.95, -98.5) * mm});
            skLineSegment(sketch, "E1826", {"start": v(2.96, -100.1) * mm, "end": v(2.96, -99.7) * mm});
            skLineSegment(sketch, "E1827", {"start": v(-0.2, -114.86) * mm, "end": v(0.2, -114.27) * mm});
            skLineSegment(sketch, "E1828", {"start": v(-0.53, -115.25) * mm, "end": v(-0.2, -114.86) * mm});
            skLineSegment(sketch, "E1829", {"start": v(-0.7, -115.4) * mm, "end": v(-0.53, -115.25) * mm});
            skLineSegment(sketch, "E1830", {"start": v(-0.75, -115.45) * mm, "end": v(-0.7, -115.4) * mm});
            skLineSegment(sketch, "E1831", {"start": v(-0.83, -115.52) * mm, "end": v(-0.75, -115.45) * mm});
            skLineSegment(sketch, "E1832", {"start": v(-1.1, -115.68) * mm, "end": v(-0.83, -115.52) * mm});
            skLineSegment(sketch, "E1833", {"start": v(-4.4, -117.15) * mm, "end": v(-3.38, -116.74) * mm});
            skLineSegment(sketch, "E1834", {"start": v(-3.38, -116.74) * mm, "end": v(-2.46, -116.35) * mm});
            skLineSegment(sketch, "E1835", {"start": v(-2.46, -116.35) * mm, "end": v(-1.68, -115.99) * mm});
            skLineSegment(sketch, "E1836", {"start": v(-1.68, -115.99) * mm, "end": v(-1.1, -115.68) * mm});
            skLineSegment(sketch, "E1837", {"start": v(0.2, -114.27) * mm, "end": v(0.65, -113.47) * mm});
            skLineSegment(sketch, "E1838", {"start": v(0.65, -113.47) * mm, "end": v(1.13, -112.43) * mm});
            skLineSegment(sketch, "E1839", {"start": v(1.13, -112.43) * mm, "end": v(1.59, -111.15) * mm});
            skLineSegment(sketch, "E1840", {"start": v(1.59, -111.15) * mm, "end": v(2, -109.59) * mm});
            skLineSegment(sketch, "E1841", {"start": v(2, -109.59) * mm, "end": v(2.26, -108.2) * mm});
            skLineSegment(sketch, "E1842", {"start": v(2.26, -108.2) * mm, "end": v(2.33, -107.74) * mm});
            skLineSegment(sketch, "E1843", {"start": v(2.33, -107.74) * mm, "end": v(2.4, -107.3) * mm});
            skLineSegment(sketch, "E1844", {"start": v(2.4, -107.3) * mm, "end": v(2.56, -105.95) * mm});
            skLineSegment(sketch, "E1845", {"start": v(2.56, -105.95) * mm, "end": v(2.77, -104.05) * mm});
            skLineSegment(sketch, "E1846", {"start": v(2.77, -104.05) * mm, "end": v(2.9, -102.07) * mm});
            skLineSegment(sketch, "E1847", {"start": v(2.9, -102.07) * mm, "end": v(2.96, -100.59) * mm});
            skLineSegment(sketch, "E1848", {"start": v(2.96, -100.59) * mm, "end": v(2.96, -100.1) * mm});
            skLineSegment(sketch, "E1849", {"start": v(-14.56, -113.83) * mm, "end": v(-15.1, -114.65) * mm});
            skLineSegment(sketch, "E1850", {"start": v(-15.1, -114.65) * mm, "end": v(-15.45, -115.16) * mm});
            skLineSegment(sketch, "E1851", {"start": v(-15.45, -115.16) * mm, "end": v(-15.56, -115.34) * mm});
            skLineSegment(sketch, "E1852", {"start": v(-15.56, -115.34) * mm, "end": v(-2.27, -100.51) * mm});
            skLineSegment(sketch, "E1853", {"start": v(-2.27, -100.51) * mm, "end": v(-2.25, -100.67) * mm});
            skLineSegment(sketch, "E1854", {"start": v(-2.25, -100.67) * mm, "end": v(-2.22, -101.12) * mm});
            skLineSegment(sketch, "E1855", {"start": v(-2.22, -101.12) * mm, "end": v(-2.18, -101.8) * mm});
            skLineSegment(sketch, "E1856", {"start": v(-2.18, -101.8) * mm, "end": v(-2.15, -102.7) * mm});
            skLineSegment(sketch, "E1857", {"start": v(-2.15, -102.7) * mm, "end": v(-2.13, -103.74) * mm});
            skLineSegment(sketch, "E1858", {"start": v(-2.13, -103.74) * mm, "end": v(-2.16, -104.9) * mm});
            skLineSegment(sketch, "E1859", {"start": v(-2.16, -104.9) * mm, "end": v(-2.23, -106.1) * mm});
            skLineSegment(sketch, "E1860", {"start": v(-2.23, -106.1) * mm, "end": v(-2.31, -107.03) * mm});
            skLineSegment(sketch, "E1861", {"start": v(-2.31, -107.03) * mm, "end": v(-2.35, -107.34) * mm});
            skLineSegment(sketch, "E1862", {"start": v(-2.35, -107.34) * mm, "end": v(-2.41, -107.77) * mm});
            skLineSegment(sketch, "E1863", {"start": v(-2.41, -107.77) * mm, "end": v(-2.68, -109.06) * mm});
            skLineSegment(sketch, "E1864", {"start": v(-2.68, -109.06) * mm, "end": v(-3.12, -110.51) * mm});
            skLineSegment(sketch, "E1865", {"start": v(-3.12, -110.51) * mm, "end": v(-3.67, -111.7) * mm});
            skLineSegment(sketch, "E1866", {"start": v(-3.67, -111.7) * mm, "end": v(-4.11, -112.42) * mm});
            skLineSegment(sketch, "E1867", {"start": v(-4.11, -112.42) * mm, "end": v(-4.29, -112.64) * mm});
            skLineSegment(sketch, "E1868", {"start": v(-4.29, -112.64) * mm, "end": v(-4.41, -112.8) * mm});
            skLineSegment(sketch, "E1869", {"start": v(-4.41, -112.8) * mm, "end": v(-4.82, -113.26) * mm});
            skLineSegment(sketch, "E1870", {"start": v(-4.82, -113.26) * mm, "end": v(-5.58, -113.93) * mm});
            skLineSegment(sketch, "E1871", {"start": v(-5.58, -113.93) * mm, "end": v(-6.63, -114.62) * mm});
            skLineSegment(sketch, "E1872", {"start": v(-6.63, -114.62) * mm, "end": v(-7.7, -115.14) * mm});
            skLineSegment(sketch, "E1873", {"start": v(-7.7, -115.14) * mm, "end": v(-8.06, -115.28) * mm});
            skLineSegment(sketch, "E1874", {"start": v(-8.06, -115.28) * mm, "end": v(-8.5, -115.45) * mm});
            skLineSegment(sketch, "E1875", {"start": v(-8.5, -115.45) * mm, "end": v(-9.82, -115.92) * mm});
            skLineSegment(sketch, "E1876", {"start": v(-9.82, -115.92) * mm, "end": v(-11.53, -116.46) * mm});
            skLineSegment(sketch, "E1877", {"start": v(-11.53, -116.46) * mm, "end": v(-13.14, -116.89) * mm});
            skLineSegment(sketch, "E1878", {"start": v(-13.14, -116.89) * mm, "end": v(-14.61, -117.22) * mm});
            skLineSegment(sketch, "E1879", {"start": v(-14.61, -117.22) * mm, "end": v(-15.92, -117.47) * mm});
            skLineSegment(sketch, "E1880", {"start": v(-15.92, -117.47) * mm, "end": v(-17.03, -117.65) * mm});
            skLineSegment(sketch, "E1881", {"start": v(-17.03, -117.65) * mm, "end": v(-17.9, -117.75) * mm});
            skLineSegment(sketch, "E1882", {"start": v(-17.9, -117.75) * mm, "end": v(-18.33, -117.8) * mm});
            skLineSegment(sketch, "E1883", {"start": v(-18.33, -117.8) * mm, "end": v(-18.48, -117.8) * mm});
            skLineSegment(sketch, "E1884", {"start": v(-18.48, -117.8) * mm, "end": v(-18.28, -117.43) * mm});
            skLineSegment(sketch, "E1885", {"start": v(-18.28, -117.43) * mm, "end": v(-17.67, -116.33) * mm});
            skLineSegment(sketch, "E1886", {"start": v(-17.67, -116.33) * mm, "end": v(-16.7, -114.69) * mm});
            skLineSegment(sketch, "E1887", {"start": v(-16.7, -114.69) * mm, "end": v(-15.58, -112.9) * mm});
            skLineSegment(sketch, "E1888", {"start": v(-15.58, -112.9) * mm, "end": v(-14.35, -111) * mm});
            skLineSegment(sketch, "E1889", {"start": v(-14.35, -111) * mm, "end": v(-13.02, -109.02) * mm});
            skLineSegment(sketch, "E1890", {"start": v(-13.02, -109.02) * mm, "end": v(-11.61, -106.97) * mm});
            skLineSegment(sketch, "E1891", {"start": v(-11.61, -106.97) * mm, "end": v(-10.15, -104.9) * mm});
            skLineSegment(sketch, "E1892", {"start": v(-10.15, -104.9) * mm, "end": v(-8.65, -102.8) * mm});
            skLineSegment(sketch, "E1893", {"start": v(-8.65, -102.8) * mm, "end": v(-7.14, -100.72) * mm});
            skLineSegment(sketch, "E1894", {"start": v(-7.14, -100.72) * mm, "end": v(-5.63, -98.69) * mm});
            skLineSegment(sketch, "E1895", {"start": v(-5.63, -98.69) * mm, "end": v(-4.16, -96.72) * mm});
            skLineSegment(sketch, "E1896", {"start": v(-4.16, -96.72) * mm, "end": v(-2.73, -94.86) * mm});
            skLineSegment(sketch, "E1897", {"start": v(126.96, -104.97) * mm, "end": v(126.62, -104.78) * mm});
            skLineSegment(sketch, "E1898", {"start": v(127.93, -105.55) * mm, "end": v(126.96, -104.97) * mm});
            skLineSegment(sketch, "E1899", {"start": v(129.05, -106.3) * mm, "end": v(127.93, -105.55) * mm});
            skLineSegment(sketch, "E1900", {"start": v(129.9, -106.94) * mm, "end": v(129.05, -106.3) * mm});
            skLineSegment(sketch, "E1901", {"start": v(130.28, -107.3) * mm, "end": v(129.9, -106.94) * mm});
            skLineSegment(sketch, "E1902", {"start": v(130.37, -107.42) * mm, "end": v(130.28, -107.3) * mm});
            skLineSegment(sketch, "E1903", {"start": v(130.44, -107.53) * mm, "end": v(130.37, -107.42) * mm});
            skLineSegment(sketch, "E1904", {"start": v(130.63, -107.85) * mm, "end": v(130.44, -107.53) * mm});
            skLineSegment(sketch, "E1905", {"start": v(130.96, -108.49) * mm, "end": v(130.63, -107.85) * mm});
            skLineSegment(sketch, "E1906", {"start": v(131.32, -109.32) * mm, "end": v(130.96, -108.49) * mm});
            skLineSegment(sketch, "E1907", {"start": v(131.6, -110.07) * mm, "end": v(131.32, -109.32) * mm});
            skLineSegment(sketch, "E1908", {"start": v(131.68, -110.32) * mm, "end": v(131.6, -110.07) * mm});
            skLineSegment(sketch, "E1909", {"start": v(131.75, -110.53) * mm, "end": v(131.68, -110.32) * mm});
            skLineSegment(sketch, "E1910", {"start": v(131.95, -111.17) * mm, "end": v(131.75, -110.53) * mm});
            skLineSegment(sketch, "E1911", {"start": v(132.2, -112.03) * mm, "end": v(131.95, -111.17) * mm});
            skLineSegment(sketch, "E1912", {"start": v(132.44, -112.86) * mm, "end": v(132.2, -112.03) * mm});
            skLineSegment(sketch, "E1913", {"start": v(132.64, -113.63) * mm, "end": v(132.44, -112.86) * mm});
            skLineSegment(sketch, "E1914", {"start": v(132.81, -114.3) * mm, "end": v(132.64, -113.63) * mm});
            skLineSegment(sketch, "E1915", {"start": v(132.94, -114.81) * mm, "end": v(132.81, -114.3) * mm});
            skLineSegment(sketch, "E1916", {"start": v(133.03, -115.16) * mm, "end": v(132.94, -114.81) * mm});
            skLineSegment(sketch, "E1917", {"start": v(133.05, -115.28) * mm, "end": v(133.03, -115.16) * mm});
            skLineSegment(sketch, "E1918", {"start": v(132.92, -115.1) * mm, "end": v(133.05, -115.28) * mm});
            skLineSegment(sketch, "E1919", {"start": v(132.55, -114.64) * mm, "end": v(132.92, -115.1) * mm});
            skLineSegment(sketch, "E1920", {"start": v(131.98, -113.91) * mm, "end": v(132.55, -114.64) * mm});
            skLineSegment(sketch, "E1921", {"start": v(131.25, -113) * mm, "end": v(131.98, -113.91) * mm});
            skLineSegment(sketch, "E1922", {"start": v(130.4, -111.93) * mm, "end": v(131.25, -113) * mm});
            skLineSegment(sketch, "E1923", {"start": v(129.46, -110.78) * mm, "end": v(130.4, -111.93) * mm});
            skLineSegment(sketch, "E1924", {"start": v(128.48, -109.59) * mm, "end": v(129.46, -110.78) * mm});
            skLineSegment(sketch, "E1925", {"start": v(127.74, -108.7) * mm, "end": v(128.48, -109.59) * mm});
            skLineSegment(sketch, "E1926", {"start": v(127.5, -108.41) * mm, "end": v(127.74, -108.7) * mm});
            skLineSegment(sketch, "E1927", {"start": v(127.25, -108.12) * mm, "end": v(127.5, -108.41) * mm});
            skLineSegment(sketch, "E1928", {"start": v(126.5, -107.26) * mm, "end": v(127.25, -108.12) * mm});
            skLineSegment(sketch, "E1929", {"start": v(125.57, -106.2) * mm, "end": v(126.5, -107.26) * mm});
            skLineSegment(sketch, "E1930", {"start": v(124.71, -105.25) * mm, "end": v(125.57, -106.2) * mm});
            skLineSegment(sketch, "E1931", {"start": v(123.96, -104.43) * mm, "end": v(124.71, -105.25) * mm});
            skLineSegment(sketch, "E1932", {"start": v(123.34, -103.75) * mm, "end": v(123.96, -104.43) * mm});
            skLineSegment(sketch, "E1933", {"start": v(122.86, -103.25) * mm, "end": v(123.34, -103.75) * mm});
            skLineSegment(sketch, "E1934", {"start": v(122.56, -102.93) * mm, "end": v(122.86, -103.25) * mm});
            skLineSegment(sketch, "E1935", {"start": v(122.45, -102.82) * mm, "end": v(122.56, -102.93) * mm});
            skLineSegment(sketch, "E1936", {"start": v(122.55, -102.86) * mm, "end": v(122.45, -102.82) * mm});
            skLineSegment(sketch, "E1937", {"start": v(122.83, -102.98) * mm, "end": v(122.55, -102.86) * mm});
            skLineSegment(sketch, "E1938", {"start": v(123.26, -103.16) * mm, "end": v(122.83, -102.98) * mm});
            skLineSegment(sketch, "E1939", {"start": v(123.8, -103.4) * mm, "end": v(123.26, -103.16) * mm});
            skLineSegment(sketch, "E1940", {"start": v(124.45, -103.7) * mm, "end": v(123.8, -103.4) * mm});
            skLineSegment(sketch, "E1941", {"start": v(125.15, -104.03) * mm, "end": v(124.45, -103.7) * mm});
            skLineSegment(sketch, "E1942", {"start": v(125.89, -104.4) * mm, "end": v(125.15, -104.03) * mm});
            skLineSegment(sketch, "E1943", {"start": v(126.44, -104.69) * mm, "end": v(125.89, -104.4) * mm});
            skLineSegment(sketch, "E1944", {"start": v(126.62, -104.78) * mm, "end": v(126.44, -104.69) * mm});
            skLineSegment(sketch, "E1945", {"start": v(107.7, -111.12) * mm, "end": v(107.22, -111.5) * mm});
            skLineSegment(sketch, "E1946", {"start": v(109.18, -109.97) * mm, "end": v(107.7, -111.12) * mm});
            skLineSegment(sketch, "E1947", {"start": v(111.06, -108.52) * mm, "end": v(109.18, -109.97) * mm});
            skLineSegment(sketch, "E1948", {"start": v(112.8, -107.16) * mm, "end": v(111.06, -108.52) * mm});
            skLineSegment(sketch, "E1949", {"start": v(114.36, -105.89) * mm, "end": v(112.8, -107.16) * mm});
            skLineSegment(sketch, "E1950", {"start": v(115.67, -104.7) * mm, "end": v(114.36, -105.89) * mm});
            skLineSegment(sketch, "E1951", {"start": v(116.68, -103.63) * mm, "end": v(115.67, -104.7) * mm});
            skLineSegment(sketch, "E1952", {"start": v(117.33, -102.66) * mm, "end": v(116.68, -103.63) * mm});
            skLineSegment(sketch, "E1953", {"start": v(117.58, -102) * mm, "end": v(117.33, -102.66) * mm});
            skLineSegment(sketch, "E1954", {"start": v(117.58, -101.8) * mm, "end": v(117.58, -102) * mm});
            skLineSegment(sketch, "E1955", {"start": v(117.59, -101.67) * mm, "end": v(117.58, -101.8) * mm});
            skLineSegment(sketch, "E1956", {"start": v(117.46, -101.3) * mm, "end": v(117.59, -101.67) * mm});
            skLineSegment(sketch, "E1957", {"start": v(117.1, -100.6) * mm, "end": v(117.46, -101.3) * mm});
            skLineSegment(sketch, "E1958", {"start": v(116.54, -99.74) * mm, "end": v(117.1, -100.6) * mm});
            skLineSegment(sketch, "E1959", {"start": v(115.85, -98.77) * mm, "end": v(116.54, -99.74) * mm});
            skLineSegment(sketch, "E1960", {"start": v(115.08, -97.76) * mm, "end": v(115.85, -98.77) * mm});
            skLineSegment(sketch, "E1961", {"start": v(114.28, -96.78) * mm, "end": v(115.08, -97.76) * mm});
            skLineSegment(sketch, "E1962", {"start": v(113.5, -95.88) * mm, "end": v(114.28, -96.78) * mm});
            skLineSegment(sketch, "E1963", {"start": v(112.96, -95.31) * mm, "end": v(113.5, -95.88) * mm});
            skLineSegment(sketch, "E1964", {"start": v(112.78, -95.13) * mm, "end": v(112.96, -95.31) * mm});
            skLineSegment(sketch, "E1965", {"start": v(113.23, -95.31) * mm, "end": v(112.78, -95.13) * mm});
            skLineSegment(sketch, "E1966", {"start": v(114.5, -95.99) * mm, "end": v(113.23, -95.31) * mm});
            skLineSegment(sketch, "E1967", {"start": v(116.26, -97.15) * mm, "end": v(114.5, -95.99) * mm});
            skLineSegment(sketch, "E1968", {"start": v(117.92, -98.53) * mm, "end": v(116.26, -97.15) * mm});
            skLineSegment(sketch, "E1969", {"start": v(119.03, -99.64) * mm, "end": v(117.92, -98.53) * mm});
            skLineSegment(sketch, "E1970", {"start": v(119.36, -100.04) * mm, "end": v(119.03, -99.64) * mm});
            skLineSegment(sketch, "E1971", {"start": v(119.68, -100.42) * mm, "end": v(119.36, -100.04) * mm});
            skLineSegment(sketch, "E1972", {"start": v(120.56, -101.62) * mm, "end": v(119.68, -100.42) * mm});
            skLineSegment(sketch, "E1973", {"start": v(121.63, -103.28) * mm, "end": v(120.56, -101.62) * mm});
            skLineSegment(sketch, "E1974", {"start": v(122.57, -104.9) * mm, "end": v(121.63, -103.28) * mm});
            skLineSegment(sketch, "E1975", {"start": v(123.16, -106) * mm, "end": v(122.57, -104.9) * mm});
            skLineSegment(sketch, "E1976", {"start": v(123.35, -106.38) * mm, "end": v(123.16, -106) * mm});
            skLineSegment(sketch, "E1977", {"start": v(123.56, -106.78) * mm, "end": v(123.35, -106.38) * mm});
            skLineSegment(sketch, "E1978", {"start": v(124.18, -107.98) * mm, "end": v(123.56, -106.78) * mm});
            skLineSegment(sketch, "E1979", {"start": v(124.82, -109.2) * mm, "end": v(124.18, -107.98) * mm});
            skLineSegment(sketch, "E1980", {"start": v(125.37, -110) * mm, "end": v(124.82, -109.2) * mm});
            skLineSegment(sketch, "E1981", {"start": v(125.75, -110.35) * mm, "end": v(125.37, -110) * mm});
            skLineSegment(sketch, "E1982", {"start": v(125.9, -110.4) * mm, "end": v(125.75, -110.35) * mm});
            skLineSegment(sketch, "E1983", {"start": v(125.65, -110.4) * mm, "end": v(125.9, -110.4) * mm});
            skLineSegment(sketch, "E1984", {"start": v(124.92, -110.2) * mm, "end": v(125.65, -110.4) * mm});
            skLineSegment(sketch, "E1985", {"start": v(123.77, -109.73) * mm, "end": v(124.92, -110.2) * mm});
            skLineSegment(sketch, "E1986", {"start": v(122.53, -109.1) * mm, "end": v(123.77, -109.73) * mm});
            skLineSegment(sketch, "E1987", {"start": v(121.27, -108.41) * mm, "end": v(122.53, -109.1) * mm});
            skLineSegment(sketch, "E1988", {"start": v(120.05, -107.76) * mm, "end": v(121.27, -108.41) * mm});
            skLineSegment(sketch, "E1989", {"start": v(118.96, -107.23) * mm, "end": v(120.05, -107.76) * mm});
            skLineSegment(sketch, "E1990", {"start": v(118.07, -106.93) * mm, "end": v(118.96, -107.23) * mm});
            skLineSegment(sketch, "E1991", {"start": v(117.58, -106.9) * mm, "end": v(118.07, -106.93) * mm});
            skLineSegment(sketch, "E1992", {"start": v(117.45, -106.96) * mm, "end": v(117.58, -106.9) * mm});
            skLineSegment(sketch, "E1993", {"start": v(117.28, -107.09) * mm, "end": v(117.45, -106.96) * mm});
            skLineSegment(sketch, "E1994", {"start": v(116.76, -107.48) * mm, "end": v(117.28, -107.09) * mm});
            skLineSegment(sketch, "E1995", {"start": v(115.94, -108.16) * mm, "end": v(116.76, -107.48) * mm});
            skLineSegment(sketch, "E1996", {"start": v(115, -108.96) * mm, "end": v(115.94, -108.16) * mm});
            skLineSegment(sketch, "E1997", {"start": v(114, -109.86) * mm, "end": v(115, -108.96) * mm});
            skLineSegment(sketch, "E1998", {"start": v(112.9, -110.86) * mm, "end": v(114, -109.86) * mm});
            skLineSegment(sketch, "E1999", {"start": v(111.78, -111.9) * mm, "end": v(112.9, -110.86) * mm});
            skLineSegment(sketch, "E2000", {"start": v(110.62, -113) * mm, "end": v(111.78, -111.9) * mm});
            skLineSegment(sketch, "E2001", {"start": v(109.76, -113.84) * mm, "end": v(110.62, -113) * mm});
            skLineSegment(sketch, "E2002", {"start": v(109.47, -114.12) * mm, "end": v(109.76, -113.84) * mm});
            skLineSegment(sketch, "E2003", {"start": v(109.16, -114.42) * mm, "end": v(109.47, -114.12) * mm});
            skLineSegment(sketch, "E2004", {"start": v(108.22, -115.34) * mm, "end": v(109.16, -114.42) * mm});
            skLineSegment(sketch, "E2005", {"start": v(107.03, -116.52) * mm, "end": v(108.22, -115.34) * mm});
            skLineSegment(sketch, "E2006", {"start": v(105.9, -117.65) * mm, "end": v(107.03, -116.52) * mm});
            skLineSegment(sketch, "E2007", {"start": v(104.89, -118.67) * mm, "end": v(105.9, -117.65) * mm});
            skLineSegment(sketch, "E2008", {"start": v(85.06, -117.93) * mm, "end": v(83.24, -118.84) * mm});
            skLineSegment(sketch, "E2009", {"start": v(87.03, -116.92) * mm, "end": v(85.06, -117.93) * mm});
            skLineSegment(sketch, "E2010", {"start": v(78.1, -123.61) * mm, "end": v(78.1, -123.86) * mm});
            skLineSegment(sketch, "E2011", {"start": v(78.1, -123.86) * mm, "end": v(78.2, -123.83) * mm});
            skLineSegment(sketch, "E2012", {"start": v(78.2, -123.83) * mm, "end": v(78.48, -123.73) * mm});
            skLineSegment(sketch, "E2013", {"start": v(78.48, -123.73) * mm, "end": v(79.07, -123.5) * mm});
            skLineSegment(sketch, "E2014", {"start": v(79.07, -123.5) * mm, "end": v(79.86, -123.17) * mm});
            skLineSegment(sketch, "E2015", {"start": v(79.86, -123.17) * mm, "end": v(80.83, -122.75) * mm});
            skLineSegment(sketch, "E2016", {"start": v(80.83, -122.75) * mm, "end": v(81.96, -122.26) * mm});
            skLineSegment(sketch, "E2017", {"start": v(81.96, -122.26) * mm, "end": v(83.23, -121.69) * mm});
            skLineSegment(sketch, "E2018", {"start": v(83.23, -121.69) * mm, "end": v(84.62, -121.05) * mm});
            skLineSegment(sketch, "E2019", {"start": v(84.62, -121.05) * mm, "end": v(85.75, -120.52) * mm});
            skLineSegment(sketch, "E2020", {"start": v(85.75, -120.52) * mm, "end": v(86.13, -120.34) * mm});
            skLineSegment(sketch, "E2021", {"start": v(86.13, -120.34) * mm, "end": v(86.8, -120.02) * mm});
            skLineSegment(sketch, "E2022", {"start": v(86.8, -120.02) * mm, "end": v(88.82, -119.03) * mm});
            skLineSegment(sketch, "E2023", {"start": v(88.82, -119.03) * mm, "end": v(91.7, -117.57) * mm});
            skLineSegment(sketch, "E2024", {"start": v(91.7, -117.57) * mm, "end": v(94.7, -115.99) * mm});
            skLineSegment(sketch, "E2025", {"start": v(94.7, -115.99) * mm, "end": v(97, -114.73) * mm});
            skLineSegment(sketch, "E2026", {"start": v(97, -114.73) * mm, "end": v(97.75, -114.3) * mm});
            skLineSegment(sketch, "E2027", {"start": v(97.75, -114.3) * mm, "end": v(98.58, -113.84) * mm});
            skLineSegment(sketch, "E2028", {"start": v(98.58, -113.84) * mm, "end": v(102.48, -111.57) * mm});
            skLineSegment(sketch, "E2029", {"start": v(102.48, -111.57) * mm, "end": v(106.17, -109.3) * mm});
            skLineSegment(sketch, "E2030", {"start": v(106.17, -109.3) * mm, "end": v(106.89, -108.85) * mm});
            skLineSegment(sketch, "E2031", {"start": v(107.22, -111.5) * mm, "end": v(107.05, -111.63) * mm});
            skLineSegment(sketch, "E2032", {"start": v(107.05, -111.63) * mm, "end": v(106.55, -112.03) * mm});
            skLineSegment(sketch, "E2033", {"start": v(106.55, -112.03) * mm, "end": v(105.64, -112.72) * mm});
            skLineSegment(sketch, "E2034", {"start": v(105.64, -112.72) * mm, "end": v(104.53, -113.57) * mm});
            skLineSegment(sketch, "E2035", {"start": v(104.53, -113.57) * mm, "end": v(103.22, -114.53) * mm});
            skLineSegment(sketch, "E2036", {"start": v(103.22, -114.53) * mm, "end": v(101.73, -115.6) * mm});
            skLineSegment(sketch, "E2037", {"start": v(101.73, -115.6) * mm, "end": v(100.08, -116.74) * mm});
            skLineSegment(sketch, "E2038", {"start": v(100.08, -116.74) * mm, "end": v(98.3, -117.93) * mm});
            skLineSegment(sketch, "E2039", {"start": v(98.3, -117.93) * mm, "end": v(96.39, -119.15) * mm});
            skLineSegment(sketch, "E2040", {"start": v(96.39, -119.15) * mm, "end": v(94.37, -120.38) * mm});
            skLineSegment(sketch, "E2041", {"start": v(94.37, -120.38) * mm, "end": v(92.28, -121.59) * mm});
            skLineSegment(sketch, "E2042", {"start": v(92.28, -121.59) * mm, "end": v(90.11, -122.75) * mm});
            skLineSegment(sketch, "E2043", {"start": v(90.11, -122.75) * mm, "end": v(87.9, -123.85) * mm});
            skLineSegment(sketch, "E2044", {"start": v(87.9, -123.85) * mm, "end": v(85.65, -124.86) * mm});
            skLineSegment(sketch, "E2045", {"start": v(85.65, -124.86) * mm, "end": v(83.4, -125.75) * mm});
            skLineSegment(sketch, "E2046", {"start": v(83.4, -125.75) * mm, "end": v(81.15, -126.51) * mm});
            skLineSegment(sketch, "E2047", {"start": v(81.15, -126.51) * mm, "end": v(79.49, -126.98) * mm});
            skLineSegment(sketch, "E2048", {"start": v(79.49, -126.98) * mm, "end": v(78.93, -127.11) * mm});
            skLineSegment(sketch, "E2049", {"start": v(78.93, -127.11) * mm, "end": v(79.36, -127.16) * mm});
            skLineSegment(sketch, "E2050", {"start": v(79.36, -127.16) * mm, "end": v(80.67, -127.28) * mm});
            skLineSegment(sketch, "E2051", {"start": v(80.67, -127.28) * mm, "end": v(82.4, -127.34) * mm});
            skLineSegment(sketch, "E2052", {"start": v(82.4, -127.34) * mm, "end": v(84.1, -127.33) * mm});
            skLineSegment(sketch, "E2053", {"start": v(84.1, -127.33) * mm, "end": v(85.78, -127.24) * mm});
            skLineSegment(sketch, "E2054", {"start": v(85.78, -127.24) * mm, "end": v(87.4, -127.08) * mm});
            skLineSegment(sketch, "E2055", {"start": v(87.4, -127.08) * mm, "end": v(88.95, -126.88) * mm});
            skLineSegment(sketch, "E2056", {"start": v(88.95, -126.88) * mm, "end": v(90.43, -126.64) * mm});
            skLineSegment(sketch, "E2057", {"start": v(90.43, -126.64) * mm, "end": v(91.81, -126.36) * mm});
            skLineSegment(sketch, "E2058", {"start": v(91.81, -126.36) * mm, "end": v(93.1, -126.08) * mm});
            skLineSegment(sketch, "E2059", {"start": v(93.1, -126.08) * mm, "end": v(94.26, -125.78) * mm});
            skLineSegment(sketch, "E2060", {"start": v(100.4, -122.9) * mm, "end": v(101.02, -122.4) * mm});
            skLineSegment(sketch, "E2061", {"start": v(101.02, -122.4) * mm, "end": v(101.58, -121.93) * mm});
            skLineSegment(sketch, "E2062", {"start": v(101.58, -121.93) * mm, "end": v(102.03, -121.54) * mm});
            skLineSegment(sketch, "E2063", {"start": v(102.03, -121.54) * mm, "end": v(102.27, -121.32) * mm});
            skLineSegment(sketch, "E2064", {"start": v(114.63, -103.67) * mm, "end": v(115.57, -102.98) * mm});
            skLineSegment(sketch, "E2065", {"start": v(115.57, -102.98) * mm, "end": v(116.25, -102.47) * mm});
            skLineSegment(sketch, "E2066", {"start": v(116.25, -102.47) * mm, "end": v(116.54, -102.24) * mm});
            skLineSegment(sketch, "E2067", {"start": v(108.74, -107.66) * mm, "end": v(110.47, -106.52) * mm});
            skLineSegment(sketch, "E2068", {"start": v(102.44, -121.16) * mm, "end": v(102.7, -120.9) * mm});
            skLineSegment(sketch, "E2069", {"start": v(116.54, -102.24) * mm, "end": v(116.62, -102.16) * mm});
            skLineSegment(sketch, "E2070", {"start": v(110.47, -106.52) * mm, "end": v(112.05, -105.46) * mm});
            skLineSegment(sketch, "E2071", {"start": v(102.7, -120.9) * mm, "end": v(103.26, -120.33) * mm});
            skLineSegment(sketch, "E2072", {"start": v(116.62, -102.16) * mm, "end": v(116.37, -102) * mm});
            skLineSegment(sketch, "E2073", {"start": v(112.05, -105.46) * mm, "end": v(113.44, -104.5) * mm});
            skLineSegment(sketch, "E2074", {"start": v(103.26, -120.33) * mm, "end": v(104, -119.58) * mm});
            skLineSegment(sketch, "E2075", {"start": v(116.37, -102) * mm, "end": v(115.58, -101.6) * mm});
            skLineSegment(sketch, "E2076", {"start": v(113.44, -104.5) * mm, "end": v(114.63, -103.67) * mm});
            skLineSegment(sketch, "E2077", {"start": v(104, -119.58) * mm, "end": v(104.89, -118.67) * mm});
            skLineSegment(sketch, "E2078", {"start": v(106.89, -108.85) * mm, "end": v(107.35, -108.56) * mm});
            skLineSegment(sketch, "E2079", {"start": v(115.58, -101.6) * mm, "end": v(114.16, -101) * mm});
            skLineSegment(sketch, "E2080", {"start": v(114.16, -101) * mm, "end": v(112.44, -100.4) * mm});
            skLineSegment(sketch, "E2081", {"start": v(101.42, -97.78) * mm, "end": v(101.14, -97.74) * mm});
            skLineSegment(sketch, "E2082", {"start": v(101.14, -97.74) * mm, "end": v(100.3, -97.63) * mm});
            skLineSegment(sketch, "E2083", {"start": v(100.3, -97.63) * mm, "end": v(99.12, -97.52) * mm});
            skLineSegment(sketch, "E2084", {"start": v(99.12, -97.52) * mm, "end": v(97.96, -97.42) * mm});
            skLineSegment(sketch, "E2085", {"start": v(102, -97.86) * mm, "end": v(101.42, -97.78) * mm});
            skLineSegment(sketch, "E2086", {"start": v(103.74, -98.16) * mm, "end": v(102, -97.86) * mm});
            skLineSegment(sketch, "E2087", {"start": v(106.06, -98.64) * mm, "end": v(103.74, -98.16) * mm});
            skLineSegment(sketch, "E2088", {"start": v(108.33, -99.19) * mm, "end": v(106.06, -98.64) * mm});
            skLineSegment(sketch, "E2089", {"start": v(110.48, -99.78) * mm, "end": v(108.33, -99.19) * mm});
            skLineSegment(sketch, "E2090", {"start": v(112.44, -100.4) * mm, "end": v(110.48, -99.78) * mm});
            skLineSegment(sketch, "E2091", {"start": v(102.35, -121.24) * mm, "end": v(102.44, -121.16) * mm});
            skLineSegment(sketch, "E2092", {"start": v(107.35, -108.56) * mm, "end": v(108.74, -107.66) * mm});
            skLineSegment(sketch, "E2093", {"start": v(99.76, -123.41) * mm, "end": v(100.4, -122.9) * mm});
            skLineSegment(sketch, "E2094", {"start": v(102.27, -121.32) * mm, "end": v(102.35, -121.24) * mm});
            skLineSegment(sketch, "E2095", {"start": v(99.14, -123.88) * mm, "end": v(99.76, -123.41) * mm});
            skLineSegment(sketch, "E2096", {"start": v(98.57, -124.27) * mm, "end": v(99.14, -123.88) * mm});
            skLineSegment(sketch, "E2097", {"start": v(98.22, -124.49) * mm, "end": v(98.57, -124.27) * mm});
            skLineSegment(sketch, "E2098", {"start": v(98.1, -124.55) * mm, "end": v(98.22, -124.49) * mm});
            skLineSegment(sketch, "E2099", {"start": v(98.06, -124.57) * mm, "end": v(98.1, -124.55) * mm});
            skLineSegment(sketch, "E2100", {"start": v(97.9, -124.64) * mm, "end": v(98.06, -124.57) * mm});
            skLineSegment(sketch, "E2101", {"start": v(97.51, -124.78) * mm, "end": v(97.9, -124.64) * mm});
            skLineSegment(sketch, "E2102", {"start": v(96.94, -124.98) * mm, "end": v(97.51, -124.78) * mm});
            skLineSegment(sketch, "E2103", {"start": v(96.2, -125.23) * mm, "end": v(96.94, -124.98) * mm});
            skLineSegment(sketch, "E2104", {"start": v(95.3, -125.5) * mm, "end": v(96.2, -125.23) * mm});
            skLineSegment(sketch, "E2105", {"start": v(94.26, -125.78) * mm, "end": v(95.3, -125.5) * mm});
            skLineSegment(sketch, "E2106", {"start": v(78.2, -122.86) * mm, "end": v(78.1, -123.61) * mm});
            skLineSegment(sketch, "E2107", {"start": v(78.58, -121.85) * mm, "end": v(78.2, -122.86) * mm});
            skLineSegment(sketch, "E2108", {"start": v(79.22, -120.96) * mm, "end": v(78.58, -121.85) * mm});
            skLineSegment(sketch, "E2109", {"start": v(79.9, -120.43) * mm, "end": v(79.22, -120.96) * mm});
            skLineSegment(sketch, "E2110", {"start": v(80.15, -120.32) * mm, "end": v(79.9, -120.43) * mm});
            skLineSegment(sketch, "E2111", {"start": v(80.51, -120.15) * mm, "end": v(80.15, -120.32) * mm});
            skLineSegment(sketch, "E2112", {"start": v(81.6, -119.64) * mm, "end": v(80.51, -120.15) * mm});
            skLineSegment(sketch, "E2113", {"start": v(83.24, -118.84) * mm, "end": v(81.6, -119.64) * mm});
            skLineSegment(sketch, "E2114", {"start": v(104.65, -105.4) * mm, "end": v(105.77, -104.72) * mm});
            skLineSegment(sketch, "E2115", {"start": v(103.29, -106.22) * mm, "end": v(104.65, -105.4) * mm});
            skLineSegment(sketch, "E2116", {"start": v(101.7, -107.16) * mm, "end": v(103.29, -106.22) * mm});
            skLineSegment(sketch, "E2117", {"start": v(99.93, -108.2) * mm, "end": v(101.7, -107.16) * mm});
            skLineSegment(sketch, "E2118", {"start": v(98, -109.33) * mm, "end": v(99.93, -108.2) * mm});
            skLineSegment(sketch, "E2119", {"start": v(95.95, -110.5) * mm, "end": v(98, -109.33) * mm});
            skLineSegment(sketch, "E2120", {"start": v(93.8, -111.72) * mm, "end": v(95.95, -110.5) * mm});
            skLineSegment(sketch, "E2121", {"start": v(91.6, -112.95) * mm, "end": v(93.8, -111.72) * mm});
            skLineSegment(sketch, "E2122", {"start": v(89.36, -114.17) * mm, "end": v(91.6, -112.95) * mm});
            skLineSegment(sketch, "E2123", {"start": v(87.12, -115.36) * mm, "end": v(89.36, -114.17) * mm});
            skLineSegment(sketch, "E2124", {"start": v(84.9, -116.5) * mm, "end": v(87.12, -115.36) * mm});
            skLineSegment(sketch, "E2125", {"start": v(82.77, -117.56) * mm, "end": v(84.9, -116.5) * mm});
            skLineSegment(sketch, "E2126", {"start": v(81.23, -118.3) * mm, "end": v(82.77, -117.56) * mm});
            skLineSegment(sketch, "E2127", {"start": v(80.72, -118.53) * mm, "end": v(81.23, -118.3) * mm});
            skLineSegment(sketch, "E2128", {"start": v(80.74, -118.4) * mm, "end": v(80.72, -118.53) * mm});
            skLineSegment(sketch, "E2129", {"start": v(80.83, -118) * mm, "end": v(80.74, -118.4) * mm});
            skLineSegment(sketch, "E2130", {"start": v(81.06, -117.24) * mm, "end": v(80.83, -118) * mm});
            skLineSegment(sketch, "E2131", {"start": v(81.38, -116.3) * mm, "end": v(81.06, -117.24) * mm});
            skLineSegment(sketch, "E2132", {"start": v(81.78, -115.2) * mm, "end": v(81.38, -116.3) * mm});
            skLineSegment(sketch, "E2133", {"start": v(82.26, -113.96) * mm, "end": v(81.78, -115.2) * mm});
            skLineSegment(sketch, "E2134", {"start": v(82.81, -112.62) * mm, "end": v(82.26, -113.96) * mm});
            skLineSegment(sketch, "E2135", {"start": v(83.42, -111.22) * mm, "end": v(82.81, -112.62) * mm});
            skLineSegment(sketch, "E2136", {"start": v(83.91, -110.13) * mm, "end": v(83.42, -111.22) * mm});
            skLineSegment(sketch, "E2137", {"start": v(84.08, -109.77) * mm, "end": v(83.91, -110.13) * mm});
            skLineSegment(sketch, "E2138", {"start": v(93.2, -97.73) * mm, "end": v(92.58, -98.09) * mm});
            skLineSegment(sketch, "E2139", {"start": v(93.65, -97.51) * mm, "end": v(93.2, -97.73) * mm});
            skLineSegment(sketch, "E2140", {"start": v(93.86, -97.44) * mm, "end": v(93.65, -97.51) * mm});
            skLineSegment(sketch, "E2141", {"start": v(93.93, -97.42) * mm, "end": v(93.86, -97.44) * mm});
            skLineSegment(sketch, "E2142", {"start": v(94.03, -97.39) * mm, "end": v(93.93, -97.42) * mm});
            skLineSegment(sketch, "E2143", {"start": v(94.35, -97.36) * mm, "end": v(94.03, -97.39) * mm});
            skLineSegment(sketch, "E2144", {"start": v(97.96, -97.42) * mm, "end": v(96.86, -97.36) * mm});
            skLineSegment(sketch, "E2145", {"start": v(96.86, -97.36) * mm, "end": v(95.86, -97.33) * mm});
            skLineSegment(sketch, "E2146", {"start": v(95.86, -97.33) * mm, "end": v(95, -97.33) * mm});
            skLineSegment(sketch, "E2147", {"start": v(95, -97.33) * mm, "end": v(94.35, -97.36) * mm});
            skLineSegment(sketch, "E2148", {"start": v(92.58, -98.09) * mm, "end": v(91.82, -98.62) * mm});
            skLineSegment(sketch, "E2149", {"start": v(91.82, -98.62) * mm, "end": v(90.96, -99.36) * mm});
            skLineSegment(sketch, "E2150", {"start": v(90.96, -99.36) * mm, "end": v(90, -100.33) * mm});
            skLineSegment(sketch, "E2151", {"start": v(90, -100.33) * mm, "end": v(88.97, -101.57) * mm});
            skLineSegment(sketch, "E2152", {"start": v(88.97, -101.57) * mm, "end": v(88.14, -102.71) * mm});
            skLineSegment(sketch, "E2153", {"start": v(88.14, -102.71) * mm, "end": v(87.89, -103.1) * mm});
            skLineSegment(sketch, "E2154", {"start": v(87.89, -103.1) * mm, "end": v(87.64, -103.48) * mm});
            skLineSegment(sketch, "E2155", {"start": v(87.64, -103.48) * mm, "end": v(86.92, -104.63) * mm});
            skLineSegment(sketch, "E2156", {"start": v(86.92, -104.63) * mm, "end": v(85.93, -106.27) * mm});
            skLineSegment(sketch, "E2157", {"start": v(85.93, -106.27) * mm, "end": v(84.97, -108) * mm});
            skLineSegment(sketch, "E2158", {"start": v(84.97, -108) * mm, "end": v(84.29, -109.32) * mm});
            skLineSegment(sketch, "E2159", {"start": v(84.29, -109.32) * mm, "end": v(84.08, -109.77) * mm});
            skLineSegment(sketch, "E2160", {"start": v(105.77, -104.72) * mm, "end": v(106.6, -104.21) * mm});
            skLineSegment(sketch, "E2161", {"start": v(106.6, -104.21) * mm, "end": v(107.13, -103.9) * mm});
            skLineSegment(sketch, "E2162", {"start": v(107.13, -103.9) * mm, "end": v(107.32, -103.78) * mm});
            skLineSegment(sketch, "E2163", {"start": v(107.32, -103.78) * mm, "end": v(89, -111.6) * mm});
            skLineSegment(sketch, "E2164", {"start": v(89, -111.6) * mm, "end": v(89.05, -111.45) * mm});
            skLineSegment(sketch, "E2165", {"start": v(89.05, -111.45) * mm, "end": v(89.21, -111.03) * mm});
            skLineSegment(sketch, "E2166", {"start": v(89.21, -111.03) * mm, "end": v(89.47, -110.39) * mm});
            skLineSegment(sketch, "E2167", {"start": v(89.47, -110.39) * mm, "end": v(89.81, -109.57) * mm});
            skLineSegment(sketch, "E2168", {"start": v(89.81, -109.57) * mm, "end": v(90.24, -108.62) * mm});
            skLineSegment(sketch, "E2169", {"start": v(90.24, -108.62) * mm, "end": v(90.75, -107.58) * mm});
            skLineSegment(sketch, "E2170", {"start": v(90.75, -107.58) * mm, "end": v(91.32, -106.51) * mm});
            skLineSegment(sketch, "E2171", {"start": v(91.32, -106.51) * mm, "end": v(91.8, -105.7) * mm});
            skLineSegment(sketch, "E2172", {"start": v(91.8, -105.7) * mm, "end": v(91.96, -105.45) * mm});
            skLineSegment(sketch, "E2173", {"start": v(91.96, -105.45) * mm, "end": v(92.2, -105.08) * mm});
            skLineSegment(sketch, "E2174", {"start": v(92.2, -105.08) * mm, "end": v(92.98, -104.03) * mm});
            skLineSegment(sketch, "E2175", {"start": v(92.98, -104.03) * mm, "end": v(94, -102.9) * mm});
            skLineSegment(sketch, "E2176", {"start": v(94, -102.9) * mm, "end": v(95, -102.05) * mm});
            skLineSegment(sketch, "E2177", {"start": v(95, -102.05) * mm, "end": v(95.7, -101.59) * mm});
            skLineSegment(sketch, "E2178", {"start": v(95.7, -101.59) * mm, "end": v(95.95, -101.46) * mm});
            skLineSegment(sketch, "E2179", {"start": v(95.95, -101.46) * mm, "end": v(96.14, -101.37) * mm});
            skLineSegment(sketch, "E2180", {"start": v(96.14, -101.37) * mm, "end": v(96.7, -101.13) * mm});
            skLineSegment(sketch, "E2181", {"start": v(96.7, -101.13) * mm, "end": v(97.67, -100.84) * mm});
            skLineSegment(sketch, "E2182", {"start": v(97.67, -100.84) * mm, "end": v(98.91, -100.66) * mm});
            skLineSegment(sketch, "E2183", {"start": v(98.91, -100.66) * mm, "end": v(100.1, -100.64) * mm});
            skLineSegment(sketch, "E2184", {"start": v(100.1, -100.64) * mm, "end": v(100.49, -100.66) * mm});
            skLineSegment(sketch, "E2185", {"start": v(100.49, -100.66) * mm, "end": v(100.96, -100.69) * mm});
            skLineSegment(sketch, "E2186", {"start": v(100.96, -100.69) * mm, "end": v(102.36, -100.82) * mm});
            skLineSegment(sketch, "E2187", {"start": v(102.36, -100.82) * mm, "end": v(104.13, -101.06) * mm});
            skLineSegment(sketch, "E2188", {"start": v(104.13, -101.06) * mm, "end": v(105.77, -101.35) * mm});
            skLineSegment(sketch, "E2189", {"start": v(105.77, -101.35) * mm, "end": v(107.25, -101.67) * mm});
            skLineSegment(sketch, "E2190", {"start": v(107.25, -101.67) * mm, "end": v(108.54, -102) * mm});
            skLineSegment(sketch, "E2191", {"start": v(108.54, -102) * mm, "end": v(109.62, -102.3) * mm});
            skLineSegment(sketch, "E2192", {"start": v(109.62, -102.3) * mm, "end": v(110.44, -102.58) * mm});
            skLineSegment(sketch, "E2193", {"start": v(110.44, -102.58) * mm, "end": v(110.86, -102.73) * mm});
            skLineSegment(sketch, "E2194", {"start": v(110.86, -102.73) * mm, "end": v(111, -102.78) * mm});
            skLineSegment(sketch, "E2195", {"start": v(111, -102.78) * mm, "end": v(110.66, -103.04) * mm});
            skLineSegment(sketch, "E2196", {"start": v(110.66, -103.04) * mm, "end": v(109.64, -103.78) * mm});
            skLineSegment(sketch, "E2197", {"start": v(109.64, -103.78) * mm, "end": v(108.06, -104.85) * mm});
            skLineSegment(sketch, "E2198", {"start": v(108.06, -104.85) * mm, "end": v(106.3, -106) * mm});
            skLineSegment(sketch, "E2199", {"start": v(106.3, -106) * mm, "end": v(104.38, -107.2) * mm});
            skLineSegment(sketch, "E2200", {"start": v(104.38, -107.2) * mm, "end": v(102.34, -108.43) * mm});
            skLineSegment(sketch, "E2201", {"start": v(102.34, -108.43) * mm, "end": v(100.2, -109.7) * mm});
            skLineSegment(sketch, "E2202", {"start": v(100.2, -109.7) * mm, "end": v(98, -110.96) * mm});
            skLineSegment(sketch, "E2203", {"start": v(98, -110.96) * mm, "end": v(95.75, -112.23) * mm});
            skLineSegment(sketch, "E2204", {"start": v(95.75, -112.23) * mm, "end": v(93.5, -113.47) * mm});
            skLineSegment(sketch, "E2205", {"start": v(93.5, -113.47) * mm, "end": v(91.28, -114.68) * mm});
            skLineSegment(sketch, "E2206", {"start": v(91.28, -114.68) * mm, "end": v(89.1, -115.83) * mm});
            skLineSegment(sketch, "E2207", {"start": v(89.1, -115.83) * mm, "end": v(87.03, -116.92) * mm});
            skSolve(sketch);
        }
        {
            var Q0;
            Q0 = qSketchRegion(id + "F2", true);
            extrude(context, id + "F3", {"entities" : qUnion([Q0]), "operationType" : NewBodyOperationType.REMOVE, "oppositeDirection" : true, "depth" : 0.5 * mm, "offsetDistance" : 25 * mm});
        }
        {
            var Q0;
            Q0=makeQuery(id+"F1.opExtrude","CAP_FACE",FACE,{"disambiguationData":[OSD([sQuery(id+"F0.wireOp",EDGE,"E0"),sQuery(id+"F0.wireOp",EDGE,"E1"),sQuery(id+"F0.wireOp",EDGE,"E2"),sQuery(id+"F0.wireOp",EDGE,"E4"),sQuery(id+"F0.wireOp",EDGE,"E5"),sQuery(id+"F0.wireOp",EDGE,"E6"),sQuery(id+"F0.wireOp",EDGE,"E8"),sQuery(id+"F0.wireOp",EDGE,"E9"),sQuery(id+"F0.wireOp",EDGE,"E10"),sQuery(id+"F0.wireOp",EDGE,"E12"),sQuery(id+"F0.wireOp",EDGE,"E13"),sQuery(id+"F0.wireOp",EDGE,"E14"),sQuery(id+"F0.wireOp",EDGE,"E15"),sQuery(id+"F0.wireOp",EDGE,"E16"),sQuery(id+"F0.wireOp",EDGE,"E18"),sQuery(id+"F0.wireOp",EDGE,"E19"),sQuery(id+"F0.wireOp",EDGE,"E20"),sQuery(id+"F0.wireOp",EDGE,"E21"),sQuery(id+"F0.wireOp",EDGE,"E22"),sQuery(id+"F0.wireOp",EDGE,"E23.filletArc"),sQuery(id+"F0.wireOp",EDGE,"E24.filletArc"),sQuery(id+"F0.wireOp",EDGE,"E25.filletArc"),sQuery(id+"F0.wireOp",EDGE,"E26.filletArc"),sQuery(id+"F0.wireOp",EDGE,"E27.filletArc"),sQuery(id+"F0.wireOp",EDGE,"E28.filletArc"),sQuery(id+"F0.wireOp",EDGE,"E29.filletArc"),sQuery(id+"F0.wireOp",EDGE,"E30.filletArc")])],"isStart":false});
            var sketch = newSketch(context, id + "F4", { "sketchPlane" : qUnion([Q0])});
            skLineSegment(sketch, "E2208", {"start": v(-25.19, -22.76) * mm, "end": v(-25.06, -23.11) * mm});
            skLineSegment(sketch, "E2209", {"start": v(-25.51, -21.66) * mm, "end": v(-25.19, -22.76) * mm});
            skLineSegment(sketch, "E2210", {"start": v(-25.83, -20.36) * mm, "end": v(-25.51, -21.66) * mm});
            skLineSegment(sketch, "E2211", {"start": v(-26.01, -19.31) * mm, "end": v(-25.83, -20.36) * mm});
            skLineSegment(sketch, "E2212", {"start": v(-26.06, -18.79) * mm, "end": v(-26.01, -19.31) * mm});
            skLineSegment(sketch, "E2213", {"start": v(-26.04, -18.63) * mm, "end": v(-26.06, -18.79) * mm});
            skLineSegment(sketch, "E2214", {"start": v(-26.02, -18.51) * mm, "end": v(-26.04, -18.63) * mm});
            skLineSegment(sketch, "E2215", {"start": v(-25.95, -18.15) * mm, "end": v(-26.02, -18.51) * mm});
            skLineSegment(sketch, "E2216", {"start": v(-25.75, -17.46) * mm, "end": v(-25.95, -18.15) * mm});
            skLineSegment(sketch, "E2217", {"start": v(-25.46, -16.6) * mm, "end": v(-25.75, -17.46) * mm});
            skLineSegment(sketch, "E2218", {"start": v(-25.16, -15.86) * mm, "end": v(-25.46, -16.6) * mm});
            skLineSegment(sketch, "E2219", {"start": v(-25.05, -15.61) * mm, "end": v(-25.16, -15.86) * mm});
            skLineSegment(sketch, "E2220", {"start": v(-24.95, -15.4) * mm, "end": v(-25.05, -15.61) * mm});
            skLineSegment(sketch, "E2221", {"start": v(-24.67, -14.8) * mm, "end": v(-24.95, -15.4) * mm});
            skLineSegment(sketch, "E2222", {"start": v(-24.28, -14) * mm, "end": v(-24.67, -14.8) * mm});
            skLineSegment(sketch, "E2223", {"start": v(-23.89, -13.24) * mm, "end": v(-24.28, -14) * mm});
            skLineSegment(sketch, "E2224", {"start": v(-23.52, -12.53) * mm, "end": v(-23.89, -13.24) * mm});
            skLineSegment(sketch, "E2225", {"start": v(-23.2, -11.93) * mm, "end": v(-23.52, -12.53) * mm});
            skLineSegment(sketch, "E2226", {"start": v(-22.94, -11.45) * mm, "end": v(-23.2, -11.93) * mm});
            skLineSegment(sketch, "E2227", {"start": v(-22.77, -11.14) * mm, "end": v(-22.94, -11.45) * mm});
            skLineSegment(sketch, "E2228", {"start": v(-22.7, -11.03) * mm, "end": v(-22.77, -11.14) * mm});
            skLineSegment(sketch, "E2229", {"start": v(-22.72, -11.25) * mm, "end": v(-22.7, -11.03) * mm});
            skLineSegment(sketch, "E2230", {"start": v(-22.77, -11.85) * mm, "end": v(-22.72, -11.25) * mm});
            skLineSegment(sketch, "E2231", {"start": v(-22.84, -12.76) * mm, "end": v(-22.77, -11.85) * mm});
            skLineSegment(sketch, "E2232", {"start": v(-22.92, -13.94) * mm, "end": v(-22.84, -12.76) * mm});
            skLineSegment(sketch, "E2233", {"start": v(-23.01, -15.3) * mm, "end": v(-22.92, -13.94) * mm});
            skLineSegment(sketch, "E2234", {"start": v(-23.1, -16.78) * mm, "end": v(-23.01, -15.3) * mm});
            skLineSegment(sketch, "E2235", {"start": v(-23.18, -18.32) * mm, "end": v(-23.1, -16.78) * mm});
            skLineSegment(sketch, "E2236", {"start": v(-23.24, -19.47) * mm, "end": v(-23.18, -18.32) * mm});
            skLineSegment(sketch, "E2237", {"start": v(-23.25, -19.85) * mm, "end": v(-23.24, -19.47) * mm});
            skLineSegment(sketch, "E2238", {"start": v(-23.27, -20.23) * mm, "end": v(-23.25, -19.85) * mm});
            skLineSegment(sketch, "E2239", {"start": v(-23.3, -21.37) * mm, "end": v(-23.27, -20.23) * mm});
            skLineSegment(sketch, "E2240", {"start": v(-23.33, -22.78) * mm, "end": v(-23.3, -21.37) * mm});
            skLineSegment(sketch, "E2241", {"start": v(-23.34, -24.06) * mm, "end": v(-23.33, -22.78) * mm});
            skLineSegment(sketch, "E2242", {"start": v(-23.35, -25.18) * mm, "end": v(-23.34, -24.06) * mm});
            skLineSegment(sketch, "E2243", {"start": v(-23.34, -26.1) * mm, "end": v(-23.35, -25.18) * mm});
            skLineSegment(sketch, "E2244", {"start": v(-23.33, -26.79) * mm, "end": v(-23.34, -26.1) * mm});
            skLineSegment(sketch, "E2245", {"start": v(-23.33, -27.23) * mm, "end": v(-23.33, -26.79) * mm});
            skLineSegment(sketch, "E2246", {"start": v(-23.32, -27.38) * mm, "end": v(-23.33, -27.23) * mm});
            skLineSegment(sketch, "E2247", {"start": v(-23.37, -27.28) * mm, "end": v(-23.32, -27.38) * mm});
            skLineSegment(sketch, "E2248", {"start": v(-23.5, -27) * mm, "end": v(-23.37, -27.28) * mm});
            skLineSegment(sketch, "E2249", {"start": v(-23.68, -26.58) * mm, "end": v(-23.5, -27) * mm});
            skLineSegment(sketch, "E2250", {"start": v(-23.92, -26.03) * mm, "end": v(-23.68, -26.58) * mm});
            skLineSegment(sketch, "E2251", {"start": v(-24.2, -25.38) * mm, "end": v(-23.92, -26.03) * mm});
            skLineSegment(sketch, "E2252", {"start": v(-24.49, -24.66) * mm, "end": v(-24.2, -25.38) * mm});
            skLineSegment(sketch, "E2253", {"start": v(-24.78, -23.9) * mm, "end": v(-24.49, -24.66) * mm});
            skLineSegment(sketch, "E2254", {"start": v(-25, -23.31) * mm, "end": v(-24.78, -23.9) * mm});
            skLineSegment(sketch, "E2255", {"start": v(-25.06, -23.11) * mm, "end": v(-25, -23.31) * mm});
            skLineSegment(sketch, "E2256", {"start": v(-6.84, -31.24) * mm, "end": v(-6.22, -31.29) * mm});
            skLineSegment(sketch, "E2257", {"start": v(-8.7, -31.09) * mm, "end": v(-6.84, -31.24) * mm});
            skLineSegment(sketch, "E2258", {"start": v(-11.07, -30.89) * mm, "end": v(-8.7, -31.09) * mm});
            skLineSegment(sketch, "E2259", {"start": v(-13.27, -30.7) * mm, "end": v(-11.07, -30.89) * mm});
            skLineSegment(sketch, "E2260", {"start": v(-15.28, -30.6) * mm, "end": v(-13.27, -30.7) * mm});
            skLineSegment(sketch, "E2261", {"start": v(-17.04, -30.58) * mm, "end": v(-15.28, -30.6) * mm});
            skLineSegment(sketch, "E2262", {"start": v(-18.52, -30.69) * mm, "end": v(-17.04, -30.58) * mm});
            skLineSegment(sketch, "E2263", {"start": v(-19.66, -30.96) * mm, "end": v(-18.52, -30.69) * mm});
            skLineSegment(sketch, "E2264", {"start": v(-20.28, -31.28) * mm, "end": v(-19.66, -30.96) * mm});
            skLineSegment(sketch, "E2265", {"start": v(-20.43, -31.43) * mm, "end": v(-20.28, -31.28) * mm});
            skLineSegment(sketch, "E2266", {"start": v(-20.51, -31.52) * mm, "end": v(-20.43, -31.43) * mm});
            skLineSegment(sketch, "E2267", {"start": v(-20.66, -31.87) * mm, "end": v(-20.51, -31.52) * mm});
            skLineSegment(sketch, "E2268", {"start": v(-20.87, -32.64) * mm, "end": v(-20.66, -31.87) * mm});
            skLineSegment(sketch, "E2269", {"start": v(-21.05, -33.65) * mm, "end": v(-20.87, -32.64) * mm});
            skLineSegment(sketch, "E2270", {"start": v(-21.2, -34.83) * mm, "end": v(-21.05, -33.65) * mm});
            skLineSegment(sketch, "E2271", {"start": v(-21.3, -36.1) * mm, "end": v(-21.2, -34.83) * mm});
            skLineSegment(sketch, "E2272", {"start": v(-21.38, -37.36) * mm, "end": v(-21.3, -36.1) * mm});
            skLineSegment(sketch, "E2273", {"start": v(-21.41, -38.55) * mm, "end": v(-21.38, -37.36) * mm});
            skLineSegment(sketch, "E2274", {"start": v(-21.4, -39.33) * mm, "end": v(-21.41, -38.55) * mm});
            skLineSegment(sketch, "E2275", {"start": v(-21.4, -39.59) * mm, "end": v(-21.4, -39.33) * mm});
            skLineSegment(sketch, "E2276", {"start": v(-21.6, -39.15) * mm, "end": v(-21.4, -39.59) * mm});
            skLineSegment(sketch, "E2277", {"start": v(-22.08, -37.79) * mm, "end": v(-21.6, -39.15) * mm});
            skLineSegment(sketch, "E2278", {"start": v(-22.59, -35.75) * mm, "end": v(-22.08, -37.79) * mm});
            skLineSegment(sketch, "E2279", {"start": v(-22.88, -33.6) * mm, "end": v(-22.59, -35.75) * mm});
            skLineSegment(sketch, "E2280", {"start": v(-22.94, -32.04) * mm, "end": v(-22.88, -33.6) * mm});
            skLineSegment(sketch, "E2281", {"start": v(-22.92, -31.52) * mm, "end": v(-22.94, -32.04) * mm});
            skLineSegment(sketch, "E2282", {"start": v(-22.9, -31.02) * mm, "end": v(-22.92, -31.52) * mm});
            skLineSegment(sketch, "E2283", {"start": v(-22.74, -29.55) * mm, "end": v(-22.9, -31.02) * mm});
            skLineSegment(sketch, "E2284", {"start": v(-22.4, -27.6) * mm, "end": v(-22.74, -29.55) * mm});
            skLineSegment(sketch, "E2285", {"start": v(-22, -25.77) * mm, "end": v(-22.4, -27.6) * mm});
            skLineSegment(sketch, "E2286", {"start": v(-21.68, -24.55) * mm, "end": v(-22, -25.77) * mm});
            skLineSegment(sketch, "E2287", {"start": v(-21.58, -24.15) * mm, "end": v(-21.68, -24.55) * mm});
            skLineSegment(sketch, "E2288", {"start": v(-21.46, -23.71) * mm, "end": v(-21.58, -24.15) * mm});
            skLineSegment(sketch, "E2289", {"start": v(-21.1, -22.41) * mm, "end": v(-21.46, -23.71) * mm});
            skLineSegment(sketch, "E2290", {"start": v(-20.76, -21.09) * mm, "end": v(-21.1, -22.41) * mm});
            skLineSegment(sketch, "E2291", {"start": v(-20.61, -20.12) * mm, "end": v(-20.76, -21.09) * mm});
            skLineSegment(sketch, "E2292", {"start": v(-20.66, -19.6) * mm, "end": v(-20.61, -20.12) * mm});
            skLineSegment(sketch, "E2293", {"start": v(-20.73, -19.46) * mm, "end": v(-20.66, -19.6) * mm});
            skLineSegment(sketch, "E2294", {"start": v(-20.56, -19.64) * mm, "end": v(-20.73, -19.46) * mm});
            skLineSegment(sketch, "E2295", {"start": v(-20.15, -20.28) * mm, "end": v(-20.56, -19.64) * mm});
            skLineSegment(sketch, "E2296", {"start": v(-19.62, -21.4) * mm, "end": v(-20.15, -20.28) * mm});
            skLineSegment(sketch, "E2297", {"start": v(-19.13, -22.7) * mm, "end": v(-19.62, -21.4) * mm});
            skLineSegment(sketch, "E2298", {"start": v(-18.66, -24.06) * mm, "end": v(-19.13, -22.7) * mm});
            skLineSegment(sketch, "E2299", {"start": v(-18.21, -25.37) * mm, "end": v(-18.66, -24.06) * mm});
            skLineSegment(sketch, "E2300", {"start": v(-17.77, -26.5) * mm, "end": v(-18.21, -25.37) * mm});
            skLineSegment(sketch, "E2301", {"start": v(-17.31, -27.31) * mm, "end": v(-17.77, -26.5) * mm});
            skLineSegment(sketch, "E2302", {"start": v(-16.97, -27.67) * mm, "end": v(-17.31, -27.31) * mm});
            skLineSegment(sketch, "E2303", {"start": v(-16.84, -27.71) * mm, "end": v(-16.97, -27.67) * mm});
            skLineSegment(sketch, "E2304", {"start": v(-16.62, -27.74) * mm, "end": v(-16.84, -27.71) * mm});
            skLineSegment(sketch, "E2305", {"start": v(-15.97, -27.8) * mm, "end": v(-16.62, -27.74) * mm});
            skLineSegment(sketch, "E2306", {"start": v(-14.91, -27.85) * mm, "end": v(-15.97, -27.8) * mm});
            skLineSegment(sketch, "E2307", {"start": v(-13.68, -27.9) * mm, "end": v(-14.91, -27.85) * mm});
            skLineSegment(sketch, "E2308", {"start": v(-12.32, -27.91) * mm, "end": v(-13.68, -27.9) * mm});
            skLineSegment(sketch, "E2309", {"start": v(-10.85, -27.92) * mm, "end": v(-12.32, -27.91) * mm});
            skLineSegment(sketch, "E2310", {"start": v(-9.3, -27.9) * mm, "end": v(-10.85, -27.92) * mm});
            skLineSegment(sketch, "E2311", {"start": v(-7.72, -27.88) * mm, "end": v(-9.3, -27.9) * mm});
            skLineSegment(sketch, "E2312", {"start": v(-6.51, -27.85) * mm, "end": v(-7.72, -27.88) * mm});
            skLineSegment(sketch, "E2313", {"start": v(-6.11, -27.84) * mm, "end": v(-6.51, -27.85) * mm});
            skLineSegment(sketch, "E2314", {"start": v(-5.68, -27.82) * mm, "end": v(-6.11, -27.84) * mm});
            skLineSegment(sketch, "E2315", {"start": v(-4.37, -27.78) * mm, "end": v(-5.68, -27.82) * mm});
            skLineSegment(sketch, "E2316", {"start": v(-2.7, -27.71) * mm, "end": v(-4.37, -27.78) * mm});
            skLineSegment(sketch, "E2317", {"start": v(-1.1, -27.65) * mm, "end": v(-2.7, -27.71) * mm});
            skLineSegment(sketch, "E2318", {"start": v(0.34, -27.58) * mm, "end": v(-1.1, -27.65) * mm});
            skLineSegment(sketch, "E2319", {"start": v(14.45, -41.53) * mm, "end": v(16.4, -42.1) * mm});
            skLineSegment(sketch, "E2320", {"start": v(12.32, -40.95) * mm, "end": v(14.45, -41.53) * mm});
            skLineSegment(sketch, "E2321", {"start": v(23.42, -42.06) * mm, "end": v(23.59, -41.87) * mm});
            skLineSegment(sketch, "E2322", {"start": v(23.59, -41.87) * mm, "end": v(23.5, -41.83) * mm});
            skLineSegment(sketch, "E2323", {"start": v(23.5, -41.83) * mm, "end": v(23.21, -41.71) * mm});
            skLineSegment(sketch, "E2324", {"start": v(23.21, -41.71) * mm, "end": v(22.62, -41.48) * mm});
            skLineSegment(sketch, "E2325", {"start": v(22.62, -41.48) * mm, "end": v(21.82, -41.2) * mm});
            skLineSegment(sketch, "E2326", {"start": v(21.82, -41.2) * mm, "end": v(20.82, -40.84) * mm});
            skLineSegment(sketch, "E2327", {"start": v(20.82, -40.84) * mm, "end": v(19.66, -40.44) * mm});
            skLineSegment(sketch, "E2328", {"start": v(19.66, -40.44) * mm, "end": v(18.34, -40) * mm});
            skLineSegment(sketch, "E2329", {"start": v(18.34, -40) * mm, "end": v(16.88, -39.53) * mm});
            skLineSegment(sketch, "E2330", {"start": v(16.88, -39.53) * mm, "end": v(15.69, -39.16) * mm});
            skLineSegment(sketch, "E2331", {"start": v(15.69, -39.16) * mm, "end": v(15.3, -39.04) * mm});
            skLineSegment(sketch, "E2332", {"start": v(15.3, -39.04) * mm, "end": v(14.57, -38.82) * mm});
            skLineSegment(sketch, "E2333", {"start": v(14.57, -38.82) * mm, "end": v(12.42, -38.18) * mm});
            skLineSegment(sketch, "E2334", {"start": v(12.42, -38.18) * mm, "end": v(9.31, -37.31) * mm});
            skLineSegment(sketch, "E2335", {"start": v(9.31, -37.31) * mm, "end": v(6.03, -36.45) * mm});
            skLineSegment(sketch, "E2336", {"start": v(6.03, -36.45) * mm, "end": v(3.5, -35.82) * mm});
            skLineSegment(sketch, "E2337", {"start": v(3.5, -35.82) * mm, "end": v(2.64, -35.62) * mm});
            skLineSegment(sketch, "E2338", {"start": v(2.64, -35.62) * mm, "end": v(1.72, -35.4) * mm});
            skLineSegment(sketch, "E2339", {"start": v(1.72, -35.4) * mm, "end": v(-2.7, -34.44) * mm});
            skLineSegment(sketch, "E2340", {"start": v(-2.7, -34.44) * mm, "end": v(-6.94, -33.6) * mm});
            skLineSegment(sketch, "E2341", {"start": v(-6.94, -33.6) * mm, "end": v(-7.77, -33.46) * mm});
            skLineSegment(sketch, "E2342", {"start": v(-6.22, -31.29) * mm, "end": v(-6.01, -31.3) * mm});
            skLineSegment(sketch, "E2343", {"start": v(-6.01, -31.3) * mm, "end": v(-5.38, -31.35) * mm});
            skLineSegment(sketch, "E2344", {"start": v(-5.38, -31.35) * mm, "end": v(-4.24, -31.45) * mm});
            skLineSegment(sketch, "E2345", {"start": v(-4.24, -31.45) * mm, "end": v(-2.85, -31.58) * mm});
            skLineSegment(sketch, "E2346", {"start": v(-2.85, -31.58) * mm, "end": v(-1.23, -31.76) * mm});
            skLineSegment(sketch, "E2347", {"start": v(-1.23, -31.76) * mm, "end": v(0.59, -31.98) * mm});
            skLineSegment(sketch, "E2348", {"start": v(0.59, -31.98) * mm, "end": v(2.57, -32.25) * mm});
            skLineSegment(sketch, "E2349", {"start": v(2.57, -32.25) * mm, "end": v(4.7, -32.58) * mm});
            skLineSegment(sketch, "E2350", {"start": v(4.7, -32.58) * mm, "end": v(6.93, -32.97) * mm});
            skLineSegment(sketch, "E2351", {"start": v(6.93, -32.97) * mm, "end": v(9.24, -33.43) * mm});
            skLineSegment(sketch, "E2352", {"start": v(9.24, -33.43) * mm, "end": v(11.6, -33.96) * mm});
            skLineSegment(sketch, "E2353", {"start": v(11.6, -33.96) * mm, "end": v(13.99, -34.57) * mm});
            skLineSegment(sketch, "E2354", {"start": v(13.99, -34.57) * mm, "end": v(16.36, -35.25) * mm});
            skLineSegment(sketch, "E2355", {"start": v(16.36, -35.25) * mm, "end": v(18.7, -36.03) * mm});
            skLineSegment(sketch, "E2356", {"start": v(18.7, -36.03) * mm, "end": v(20.96, -36.9) * mm});
            skLineSegment(sketch, "E2357", {"start": v(20.96, -36.9) * mm, "end": v(23.13, -37.85) * mm});
            skLineSegment(sketch, "E2358", {"start": v(23.13, -37.85) * mm, "end": v(24.67, -38.63) * mm});
            skLineSegment(sketch, "E2359", {"start": v(24.67, -38.63) * mm, "end": v(25.17, -38.92) * mm});
            skLineSegment(sketch, "E2360", {"start": v(25.17, -38.92) * mm, "end": v(24.89, -38.58) * mm});
            skLineSegment(sketch, "E2361", {"start": v(24.89, -38.58) * mm, "end": v(24, -37.62) * mm});
            skLineSegment(sketch, "E2362", {"start": v(24, -37.62) * mm, "end": v(22.77, -36.4) * mm});
            skLineSegment(sketch, "E2363", {"start": v(22.77, -36.4) * mm, "end": v(21.5, -35.25) * mm});
            skLineSegment(sketch, "E2364", {"start": v(21.5, -35.25) * mm, "end": v(20.21, -34.2) * mm});
            skLineSegment(sketch, "E2365", {"start": v(20.21, -34.2) * mm, "end": v(18.91, -33.21) * mm});
            skLineSegment(sketch, "E2366", {"start": v(18.91, -33.21) * mm, "end": v(17.63, -32.3) * mm});
            skLineSegment(sketch, "E2367", {"start": v(17.63, -32.3) * mm, "end": v(16.38, -31.5) * mm});
            skLineSegment(sketch, "E2368", {"start": v(16.38, -31.5) * mm, "end": v(15.17, -30.75) * mm});
            skLineSegment(sketch, "E2369", {"start": v(15.17, -30.75) * mm, "end": v(14.03, -30.1) * mm});
            skLineSegment(sketch, "E2370", {"start": v(14.03, -30.1) * mm, "end": v(12.97, -29.52) * mm});
            skLineSegment(sketch, "E2371", {"start": v(6.5, -27.49) * mm, "end": v(5.71, -27.44) * mm});
            skLineSegment(sketch, "E2372", {"start": v(5.71, -27.44) * mm, "end": v(4.98, -27.41) * mm});
            skLineSegment(sketch, "E2373", {"start": v(4.98, -27.41) * mm, "end": v(4.38, -27.4) * mm});
            skLineSegment(sketch, "E2374", {"start": v(4.38, -27.4) * mm, "end": v(4.06, -27.4) * mm});
            skLineSegment(sketch, "E2375", {"start": v(-16.98, -32.05) * mm, "end": v(-18.14, -31.91) * mm});
            skLineSegment(sketch, "E2376", {"start": v(-18.14, -31.91) * mm, "end": v(-18.99, -31.83) * mm});
            skLineSegment(sketch, "E2377", {"start": v(-18.99, -31.83) * mm, "end": v(-19.35, -31.8) * mm});
            skLineSegment(sketch, "E2378", {"start": v(-9.94, -33.09) * mm, "end": v(-11.99, -32.76) * mm});
            skLineSegment(sketch, "E2379", {"start": v(3.83, -27.4) * mm, "end": v(3.45, -27.42) * mm});
            skLineSegment(sketch, "E2380", {"start": v(-19.35, -31.8) * mm, "end": v(-19.47, -31.81) * mm});
            skLineSegment(sketch, "E2381", {"start": v(-11.99, -32.76) * mm, "end": v(-13.87, -32.47) * mm});
            skLineSegment(sketch, "E2382", {"start": v(3.45, -27.42) * mm, "end": v(2.66, -27.46) * mm});
            skLineSegment(sketch, "E2383", {"start": v(-19.47, -31.81) * mm, "end": v(-19.4, -32.1) * mm});
            skLineSegment(sketch, "E2384", {"start": v(-13.87, -32.47) * mm, "end": v(-15.54, -32.23) * mm});
            skLineSegment(sketch, "E2385", {"start": v(2.66, -27.46) * mm, "end": v(1.6, -27.52) * mm});
            skLineSegment(sketch, "E2386", {"start": v(-19.4, -32.1) * mm, "end": v(-19.08, -32.92) * mm});
            skLineSegment(sketch, "E2387", {"start": v(-15.54, -32.23) * mm, "end": v(-16.98, -32.05) * mm});
            skLineSegment(sketch, "E2388", {"start": v(1.6, -27.52) * mm, "end": v(0.34, -27.58) * mm});
            skLineSegment(sketch, "E2389", {"start": v(-7.77, -33.46) * mm, "end": v(-8.31, -33.36) * mm});
            skLineSegment(sketch, "E2390", {"start": v(-19.08, -32.92) * mm, "end": v(-18.44, -34.32) * mm});
            skLineSegment(sketch, "E2391", {"start": v(-18.44, -34.32) * mm, "end": v(-17.59, -35.94) * mm});
            skLineSegment(sketch, "E2392", {"start": v(-11.24, -45.31) * mm, "end": v(-11.06, -45.53) * mm});
            skLineSegment(sketch, "E2393", {"start": v(-11.06, -45.53) * mm, "end": v(-10.5, -46.19) * mm});
            skLineSegment(sketch, "E2394", {"start": v(-10.5, -46.19) * mm, "end": v(-9.72, -47.06) * mm});
            skLineSegment(sketch, "E2395", {"start": v(-9.72, -47.06) * mm, "end": v(-8.93, -47.91) * mm});
            skLineSegment(sketch, "E2396", {"start": v(-11.6, -44.86) * mm, "end": v(-11.24, -45.31) * mm});
            skLineSegment(sketch, "E2397", {"start": v(-12.68, -43.46) * mm, "end": v(-11.6, -44.86) * mm});
            skLineSegment(sketch, "E2398", {"start": v(-14.07, -41.54) * mm, "end": v(-12.68, -43.46) * mm});
            skLineSegment(sketch, "E2399", {"start": v(-15.37, -39.6) * mm, "end": v(-14.07, -41.54) * mm});
            skLineSegment(sketch, "E2400", {"start": v(-16.55, -37.72) * mm, "end": v(-15.37, -39.6) * mm});
            skLineSegment(sketch, "E2401", {"start": v(-17.59, -35.94) * mm, "end": v(-16.55, -37.72) * mm});
            skLineSegment(sketch, "E2402", {"start": v(3.95, -27.4) * mm, "end": v(3.83, -27.4) * mm});
            skLineSegment(sketch, "E2403", {"start": v(-8.31, -33.36) * mm, "end": v(-9.94, -33.09) * mm});
            skLineSegment(sketch, "E2404", {"start": v(7.32, -27.55) * mm, "end": v(6.5, -27.49) * mm});
            skLineSegment(sketch, "E2405", {"start": v(4.06, -27.4) * mm, "end": v(3.95, -27.4) * mm});
            skLineSegment(sketch, "E2406", {"start": v(8.1, -27.63) * mm, "end": v(7.32, -27.55) * mm});
            skLineSegment(sketch, "E2407", {"start": v(8.78, -27.72) * mm, "end": v(8.1, -27.63) * mm});
            skLineSegment(sketch, "E2408", {"start": v(9.18, -27.8) * mm, "end": v(8.78, -27.72) * mm});
            skLineSegment(sketch, "E2409", {"start": v(9.31, -27.84) * mm, "end": v(9.18, -27.8) * mm});
            skLineSegment(sketch, "E2410", {"start": v(9.36, -27.85) * mm, "end": v(9.31, -27.84) * mm});
            skLineSegment(sketch, "E2411", {"start": v(9.52, -27.9) * mm, "end": v(9.36, -27.85) * mm});
            skLineSegment(sketch, "E2412", {"start": v(9.9, -28.06) * mm, "end": v(9.52, -27.9) * mm});
            skLineSegment(sketch, "E2413", {"start": v(10.46, -28.3) * mm, "end": v(9.9, -28.06) * mm});
            skLineSegment(sketch, "E2414", {"start": v(11.17, -28.63) * mm, "end": v(10.46, -28.3) * mm});
            skLineSegment(sketch, "E2415", {"start": v(12.02, -29.03) * mm, "end": v(11.17, -28.63) * mm});
            skLineSegment(sketch, "E2416", {"start": v(12.97, -29.52) * mm, "end": v(12.02, -29.03) * mm});
            skLineSegment(sketch, "E2417", {"start": v(22.83, -42.54) * mm, "end": v(23.42, -42.06) * mm});
            skLineSegment(sketch, "E2418", {"start": v(21.87, -43.03) * mm, "end": v(22.83, -42.54) * mm});
            skLineSegment(sketch, "E2419", {"start": v(20.8, -43.24) * mm, "end": v(21.87, -43.03) * mm});
            skLineSegment(sketch, "E2420", {"start": v(19.94, -43.18) * mm, "end": v(20.8, -43.24) * mm});
            skLineSegment(sketch, "E2421", {"start": v(19.68, -43.1) * mm, "end": v(19.94, -43.18) * mm});
            skLineSegment(sketch, "E2422", {"start": v(19.3, -42.97) * mm, "end": v(19.68, -43.1) * mm});
            skLineSegment(sketch, "E2423", {"start": v(18.16, -42.62) * mm, "end": v(19.3, -42.97) * mm});
            skLineSegment(sketch, "E2424", {"start": v(16.4, -42.1) * mm, "end": v(18.16, -42.62) * mm});
            skLineSegment(sketch, "E2425", {"start": v(-8.46, -37.52) * mm, "end": v(-9.74, -37.26) * mm});
            skLineSegment(sketch, "E2426", {"start": v(-6.9, -37.84) * mm, "end": v(-8.46, -37.52) * mm});
            skLineSegment(sketch, "E2427", {"start": v(-5.1, -38.21) * mm, "end": v(-6.9, -37.84) * mm});
            skLineSegment(sketch, "E2428", {"start": v(-3.08, -38.64) * mm, "end": v(-5.1, -38.21) * mm});
            skLineSegment(sketch, "E2429", {"start": v(-0.9, -39.12) * mm, "end": v(-3.08, -38.64) * mm});
            skLineSegment(sketch, "E2430", {"start": v(1.4, -39.64) * mm, "end": v(-0.9, -39.12) * mm});
            skLineSegment(sketch, "E2431", {"start": v(3.8, -40.2) * mm, "end": v(1.4, -39.64) * mm});
            skLineSegment(sketch, "E2432", {"start": v(6.27, -40.78) * mm, "end": v(3.8, -40.2) * mm});
            skLineSegment(sketch, "E2433", {"start": v(8.74, -41.4) * mm, "end": v(6.27, -40.78) * mm});
            skLineSegment(sketch, "E2434", {"start": v(11.2, -42.04) * mm, "end": v(8.74, -41.4) * mm});
            skLineSegment(sketch, "E2435", {"start": v(13.59, -42.7) * mm, "end": v(11.2, -42.04) * mm});
            skLineSegment(sketch, "E2436", {"start": v(15.89, -43.36) * mm, "end": v(13.59, -42.7) * mm});
            skLineSegment(sketch, "E2437", {"start": v(17.51, -43.86) * mm, "end": v(15.89, -43.36) * mm});
            skLineSegment(sketch, "E2438", {"start": v(18.05, -44.03) * mm, "end": v(17.51, -43.86) * mm});
            skLineSegment(sketch, "E2439", {"start": v(17.94, -44.12) * mm, "end": v(18.05, -44.03) * mm});
            skLineSegment(sketch, "E2440", {"start": v(17.6, -44.34) * mm, "end": v(17.94, -44.12) * mm});
            skLineSegment(sketch, "E2441", {"start": v(16.93, -44.75) * mm, "end": v(17.6, -44.34) * mm});
            skLineSegment(sketch, "E2442", {"start": v(16.06, -45.23) * mm, "end": v(16.93, -44.75) * mm});
            skLineSegment(sketch, "E2443", {"start": v(15.01, -45.77) * mm, "end": v(16.06, -45.23) * mm});
            skLineSegment(sketch, "E2444", {"start": v(13.82, -46.35) * mm, "end": v(15.01, -45.77) * mm});
            skLineSegment(sketch, "E2445", {"start": v(12.51, -46.96) * mm, "end": v(13.82, -46.35) * mm});
            skLineSegment(sketch, "E2446", {"start": v(11.11, -47.59) * mm, "end": v(12.51, -46.96) * mm});
            skLineSegment(sketch, "E2447", {"start": v(10.02, -48.06) * mm, "end": v(11.11, -47.59) * mm});
            skLineSegment(sketch, "E2448", {"start": v(9.65, -48.2) * mm, "end": v(10.02, -48.06) * mm});
            skLineSegment(sketch, "E2449", {"start": v(-5.2, -50.92) * mm, "end": v(-4.5, -51.07) * mm});
            skLineSegment(sketch, "E2450", {"start": v(-5.69, -50.76) * mm, "end": v(-5.2, -50.92) * mm});
            skLineSegment(sketch, "E2451", {"start": v(-5.9, -50.68) * mm, "end": v(-5.69, -50.76) * mm});
            skLineSegment(sketch, "E2452", {"start": v(-5.96, -50.65) * mm, "end": v(-5.9, -50.68) * mm});
            skLineSegment(sketch, "E2453", {"start": v(-6.05, -50.6) * mm, "end": v(-5.96, -50.65) * mm});
            skLineSegment(sketch, "E2454", {"start": v(-6.3, -50.41) * mm, "end": v(-6.05, -50.6) * mm});
            skLineSegment(sketch, "E2455", {"start": v(-8.93, -47.91) * mm, "end": v(-8.16, -48.7) * mm});
            skLineSegment(sketch, "E2456", {"start": v(-8.16, -48.7) * mm, "end": v(-7.44, -49.4) * mm});
            skLineSegment(sketch, "E2457", {"start": v(-7.44, -49.4) * mm, "end": v(-6.81, -49.99) * mm});
            skLineSegment(sketch, "E2458", {"start": v(-6.81, -49.99) * mm, "end": v(-6.3, -50.41) * mm});
            skLineSegment(sketch, "E2459", {"start": v(-4.5, -51.07) * mm, "end": v(-3.6, -51.18) * mm});
            skLineSegment(sketch, "E2460", {"start": v(-3.6, -51.18) * mm, "end": v(-2.46, -51.23) * mm});
            skLineSegment(sketch, "E2461", {"start": v(-2.46, -51.23) * mm, "end": v(-1.1, -51.16) * mm});
            skLineSegment(sketch, "E2462", {"start": v(-1.1, -51.16) * mm, "end": v(0.5, -50.94) * mm});
            skLineSegment(sketch, "E2463", {"start": v(0.5, -50.94) * mm, "end": v(1.89, -50.66) * mm});
            skLineSegment(sketch, "E2464", {"start": v(1.89, -50.66) * mm, "end": v(2.34, -50.54) * mm});
            skLineSegment(sketch, "E2465", {"start": v(2.34, -50.54) * mm, "end": v(2.78, -50.43) * mm});
            skLineSegment(sketch, "E2466", {"start": v(2.78, -50.43) * mm, "end": v(4.08, -50.08) * mm});
            skLineSegment(sketch, "E2467", {"start": v(4.08, -50.08) * mm, "end": v(5.92, -49.54) * mm});
            skLineSegment(sketch, "E2468", {"start": v(5.92, -49.54) * mm, "end": v(7.8, -48.91) * mm});
            skLineSegment(sketch, "E2469", {"start": v(7.8, -48.91) * mm, "end": v(9.2, -48.4) * mm});
            skLineSegment(sketch, "E2470", {"start": v(9.2, -48.4) * mm, "end": v(9.65, -48.2) * mm});
            skLineSegment(sketch, "E2471", {"start": v(-9.74, -37.26) * mm, "end": v(-10.7, -37.07) * mm});
            skLineSegment(sketch, "E2472", {"start": v(-10.7, -37.07) * mm, "end": v(-11.3, -36.95) * mm});
            skLineSegment(sketch, "E2473", {"start": v(-11.3, -36.95) * mm, "end": v(-11.52, -36.91) * mm});
            skLineSegment(sketch, "E2474", {"start": v(-11.52, -36.91) * mm, "end": v(7.27, -43.53) * mm});
            skLineSegment(sketch, "E2475", {"start": v(7.27, -43.53) * mm, "end": v(7.12, -43.6) * mm});
            skLineSegment(sketch, "E2476", {"start": v(7.12, -43.6) * mm, "end": v(6.72, -43.8) * mm});
            skLineSegment(sketch, "E2477", {"start": v(6.72, -43.8) * mm, "end": v(6.1, -44.11) * mm});
            skLineSegment(sketch, "E2478", {"start": v(6.1, -44.11) * mm, "end": v(5.3, -44.48) * mm});
            skLineSegment(sketch, "E2479", {"start": v(5.3, -44.48) * mm, "end": v(4.33, -44.9) * mm});
            skLineSegment(sketch, "E2480", {"start": v(4.33, -44.9) * mm, "end": v(3.26, -45.31) * mm});
            skLineSegment(sketch, "E2481", {"start": v(3.26, -45.31) * mm, "end": v(2.11, -45.71) * mm});
            skLineSegment(sketch, "E2482", {"start": v(2.11, -45.71) * mm, "end": v(1.22, -45.98) * mm});
            skLineSegment(sketch, "E2483", {"start": v(1.22, -45.98) * mm, "end": v(0.92, -46.06) * mm});
            skLineSegment(sketch, "E2484", {"start": v(0.92, -46.06) * mm, "end": v(0.5, -46.17) * mm});
            skLineSegment(sketch, "E2485", {"start": v(0.5, -46.17) * mm, "end": v(-0.79, -46.42) * mm});
            skLineSegment(sketch, "E2486", {"start": v(-0.79, -46.42) * mm, "end": v(-2.3, -46.56) * mm});
            skLineSegment(sketch, "E2487", {"start": v(-2.3, -46.56) * mm, "end": v(-3.61, -46.51) * mm});
            skLineSegment(sketch, "E2488", {"start": v(-3.61, -46.51) * mm, "end": v(-4.45, -46.38) * mm});
            skLineSegment(sketch, "E2489", {"start": v(-4.45, -46.38) * mm, "end": v(-4.72, -46.3) * mm});
            skLineSegment(sketch, "E2490", {"start": v(-4.72, -46.3) * mm, "end": v(-4.91, -46.25) * mm});
            skLineSegment(sketch, "E2491", {"start": v(-4.91, -46.25) * mm, "end": v(-5.5, -46.04) * mm});
            skLineSegment(sketch, "E2492", {"start": v(-5.5, -46.04) * mm, "end": v(-6.4, -45.6) * mm});
            skLineSegment(sketch, "E2493", {"start": v(-6.4, -45.6) * mm, "end": v(-7.44, -44.89) * mm});
            skLineSegment(sketch, "E2494", {"start": v(-7.44, -44.89) * mm, "end": v(-8.33, -44.1) * mm});
            skLineSegment(sketch, "E2495", {"start": v(-8.33, -44.1) * mm, "end": v(-8.6, -43.82) * mm});
            skLineSegment(sketch, "E2496", {"start": v(-8.6, -43.82) * mm, "end": v(-8.92, -43.49) * mm});
            skLineSegment(sketch, "E2497", {"start": v(-8.92, -43.49) * mm, "end": v(-9.86, -42.44) * mm});
            skLineSegment(sketch, "E2498", {"start": v(-9.86, -42.44) * mm, "end": v(-11, -41.07) * mm});
            skLineSegment(sketch, "E2499", {"start": v(-11, -41.07) * mm, "end": v(-12.02, -39.74) * mm});
            skLineSegment(sketch, "E2500", {"start": v(-12.02, -39.74) * mm, "end": v(-12.9, -38.5) * mm});
            skLineSegment(sketch, "E2501", {"start": v(-12.9, -38.5) * mm, "end": v(-13.63, -37.4) * mm});
            skLineSegment(sketch, "E2502", {"start": v(-13.63, -37.4) * mm, "end": v(-14.2, -36.44) * mm});
            skLineSegment(sketch, "E2503", {"start": v(-14.2, -36.44) * mm, "end": v(-14.64, -35.68) * mm});
            skLineSegment(sketch, "E2504", {"start": v(-14.64, -35.68) * mm, "end": v(-14.84, -35.29) * mm});
            skLineSegment(sketch, "E2505", {"start": v(-14.84, -35.29) * mm, "end": v(-14.9, -35.16) * mm});
            skLineSegment(sketch, "E2506", {"start": v(-14.9, -35.16) * mm, "end": v(-14.48, -35.2) * mm});
            skLineSegment(sketch, "E2507", {"start": v(-14.48, -35.2) * mm, "end": v(-13.23, -35.34) * mm});
            skLineSegment(sketch, "E2508", {"start": v(-13.23, -35.34) * mm, "end": v(-11.34, -35.61) * mm});
            skLineSegment(sketch, "E2509", {"start": v(-11.34, -35.61) * mm, "end": v(-9.27, -35.96) * mm});
            skLineSegment(sketch, "E2510", {"start": v(-9.27, -35.96) * mm, "end": v(-7.05, -36.38) * mm});
            skLineSegment(sketch, "E2511", {"start": v(-7.05, -36.38) * mm, "end": v(-4.7, -36.85) * mm});
            skLineSegment(sketch, "E2512", {"start": v(-4.7, -36.85) * mm, "end": v(-2.28, -37.36) * mm});
            skLineSegment(sketch, "E2513", {"start": v(-2.28, -37.36) * mm, "end": v(0.2, -37.92) * mm});
            skLineSegment(sketch, "E2514", {"start": v(0.2, -37.92) * mm, "end": v(2.72, -38.5) * mm});
            skLineSegment(sketch, "E2515", {"start": v(2.72, -38.5) * mm, "end": v(5.21, -39.11) * mm});
            skLineSegment(sketch, "E2516", {"start": v(5.21, -39.11) * mm, "end": v(7.67, -39.73) * mm});
            skLineSegment(sketch, "E2517", {"start": v(7.67, -39.73) * mm, "end": v(10.05, -40.34) * mm});
            skLineSegment(sketch, "E2518", {"start": v(10.05, -40.34) * mm, "end": v(12.32, -40.95) * mm});
            skLineSegment(sketch, "E2519", {"start": v(71.4, -103.09) * mm, "end": v(71.7, -103.3) * mm});
            skLineSegment(sketch, "E2520", {"start": v(70.5, -102.39) * mm, "end": v(71.4, -103.09) * mm});
            skLineSegment(sketch, "E2521", {"start": v(69.47, -101.5) * mm, "end": v(70.5, -102.39) * mm});
            skLineSegment(sketch, "E2522", {"start": v(68.72, -100.76) * mm, "end": v(69.47, -101.5) * mm});
            skLineSegment(sketch, "E2523", {"start": v(68.38, -100.36) * mm, "end": v(68.72, -100.76) * mm});
            skLineSegment(sketch, "E2524", {"start": v(68.3, -100.22) * mm, "end": v(68.38, -100.36) * mm});
            skLineSegment(sketch, "E2525", {"start": v(68.25, -100.11) * mm, "end": v(68.3, -100.22) * mm});
            skLineSegment(sketch, "E2526", {"start": v(68.1, -99.77) * mm, "end": v(68.25, -100.11) * mm});
            skLineSegment(sketch, "E2527", {"start": v(67.86, -99.1) * mm, "end": v(68.1, -99.77) * mm});
            skLineSegment(sketch, "E2528", {"start": v(67.6, -98.22) * mm, "end": v(67.86, -99.1) * mm});
            skLineSegment(sketch, "E2529", {"start": v(67.42, -97.44) * mm, "end": v(67.6, -98.22) * mm});
            skLineSegment(sketch, "E2530", {"start": v(67.37, -97.18) * mm, "end": v(67.42, -97.44) * mm});
            skLineSegment(sketch, "E2531", {"start": v(67.33, -96.96) * mm, "end": v(67.37, -97.18) * mm});
            skLineSegment(sketch, "E2532", {"start": v(67.2, -96.31) * mm, "end": v(67.33, -96.96) * mm});
            skLineSegment(sketch, "E2533", {"start": v(67.06, -95.43) * mm, "end": v(67.2, -96.31) * mm});
            skLineSegment(sketch, "E2534", {"start": v(66.94, -94.57) * mm, "end": v(67.06, -95.43) * mm});
            skLineSegment(sketch, "E2535", {"start": v(66.83, -93.79) * mm, "end": v(66.94, -94.57) * mm});
            skLineSegment(sketch, "E2536", {"start": v(66.74, -93.1) * mm, "end": v(66.83, -93.79) * mm});
            skLineSegment(sketch, "E2537", {"start": v(66.68, -92.57) * mm, "end": v(66.74, -93.1) * mm});
            skLineSegment(sketch, "E2538", {"start": v(66.64, -92.22) * mm, "end": v(66.68, -92.57) * mm});
            skLineSegment(sketch, "E2539", {"start": v(66.62, -92.1) * mm, "end": v(66.64, -92.22) * mm});
            skLineSegment(sketch, "E2540", {"start": v(66.73, -92.28) * mm, "end": v(66.62, -92.1) * mm});
            skLineSegment(sketch, "E2541", {"start": v(67.04, -92.8) * mm, "end": v(66.73, -92.28) * mm});
            skLineSegment(sketch, "E2542", {"start": v(67.52, -93.58) * mm, "end": v(67.04, -92.8) * mm});
            skLineSegment(sketch, "E2543", {"start": v(68.13, -94.59) * mm, "end": v(67.52, -93.58) * mm});
            skLineSegment(sketch, "E2544", {"start": v(68.84, -95.75) * mm, "end": v(68.13, -94.59) * mm});
            skLineSegment(sketch, "E2545", {"start": v(69.63, -97) * mm, "end": v(68.84, -95.75) * mm});
            skLineSegment(sketch, "E2546", {"start": v(70.45, -98.31) * mm, "end": v(69.63, -97) * mm});
            skLineSegment(sketch, "E2547", {"start": v(71.08, -99.28) * mm, "end": v(70.45, -98.31) * mm});
            skLineSegment(sketch, "E2548", {"start": v(71.29, -99.6) * mm, "end": v(71.08, -99.28) * mm});
            skLineSegment(sketch, "E2549", {"start": v(71.5, -99.92) * mm, "end": v(71.29, -99.6) * mm});
            skLineSegment(sketch, "E2550", {"start": v(72.13, -100.86) * mm, "end": v(71.5, -99.92) * mm});
            skLineSegment(sketch, "E2551", {"start": v(72.92, -102.03) * mm, "end": v(72.13, -100.86) * mm});
            skLineSegment(sketch, "E2552", {"start": v(73.65, -103.08) * mm, "end": v(72.92, -102.03) * mm});
            skLineSegment(sketch, "E2553", {"start": v(74.3, -104) * mm, "end": v(73.65, -103.08) * mm});
            skLineSegment(sketch, "E2554", {"start": v(74.83, -104.74) * mm, "end": v(74.3, -104) * mm});
            skLineSegment(sketch, "E2555", {"start": v(75.24, -105.3) * mm, "end": v(74.83, -104.74) * mm});
            skLineSegment(sketch, "E2556", {"start": v(75.5, -105.66) * mm, "end": v(75.24, -105.3) * mm});
            skLineSegment(sketch, "E2557", {"start": v(75.59, -105.78) * mm, "end": v(75.5, -105.66) * mm});
            skLineSegment(sketch, "E2558", {"start": v(75.5, -105.73) * mm, "end": v(75.59, -105.78) * mm});
            skLineSegment(sketch, "E2559", {"start": v(75.23, -105.57) * mm, "end": v(75.5, -105.73) * mm});
            skLineSegment(sketch, "E2560", {"start": v(74.83, -105.34) * mm, "end": v(75.23, -105.57) * mm});
            skLineSegment(sketch, "E2561", {"start": v(74.32, -105.03) * mm, "end": v(74.83, -105.34) * mm});
            skLineSegment(sketch, "E2562", {"start": v(73.72, -104.66) * mm, "end": v(74.32, -105.03) * mm});
            skLineSegment(sketch, "E2563", {"start": v(73.06, -104.24) * mm, "end": v(73.72, -104.66) * mm});
            skLineSegment(sketch, "E2564", {"start": v(72.38, -103.78) * mm, "end": v(73.06, -104.24) * mm});
            skLineSegment(sketch, "E2565", {"start": v(71.87, -103.43) * mm, "end": v(72.38, -103.78) * mm});
            skLineSegment(sketch, "E2566", {"start": v(71.7, -103.3) * mm, "end": v(71.87, -103.43) * mm});
            skLineSegment(sketch, "E2567", {"start": v(91.26, -99.38) * mm, "end": v(91.8, -99.06) * mm});
            skLineSegment(sketch, "E2568", {"start": v(89.65, -100.34) * mm, "end": v(91.26, -99.38) * mm});
            skLineSegment(sketch, "E2569", {"start": v(87.6, -101.54) * mm, "end": v(89.65, -100.34) * mm});
            skLineSegment(sketch, "E2570", {"start": v(85.7, -102.67) * mm, "end": v(87.6, -101.54) * mm});
            skLineSegment(sketch, "E2571", {"start": v(84, -103.74) * mm, "end": v(85.7, -102.67) * mm});
            skLineSegment(sketch, "E2572", {"start": v(82.56, -104.75) * mm, "end": v(84, -103.74) * mm});
            skLineSegment(sketch, "E2573", {"start": v(81.42, -105.7) * mm, "end": v(82.56, -104.75) * mm});
            skLineSegment(sketch, "E2574", {"start": v(80.65, -106.58) * mm, "end": v(81.42, -105.7) * mm});
            skLineSegment(sketch, "E2575", {"start": v(80.33, -107.19) * mm, "end": v(80.65, -106.58) * mm});
            skLineSegment(sketch, "E2576", {"start": v(80.3, -107.4) * mm, "end": v(80.33, -107.19) * mm});
            skLineSegment(sketch, "E2577", {"start": v(80.27, -107.52) * mm, "end": v(80.3, -107.4) * mm});
            skLineSegment(sketch, "E2578", {"start": v(80.36, -107.9) * mm, "end": v(80.27, -107.52) * mm});
            skLineSegment(sketch, "E2579", {"start": v(80.63, -108.64) * mm, "end": v(80.36, -107.9) * mm});
            skLineSegment(sketch, "E2580", {"start": v(81.07, -109.57) * mm, "end": v(80.63, -108.64) * mm});
            skLineSegment(sketch, "E2581", {"start": v(81.63, -110.62) * mm, "end": v(81.07, -109.57) * mm});
            skLineSegment(sketch, "E2582", {"start": v(82.28, -111.72) * mm, "end": v(81.63, -110.62) * mm});
            skLineSegment(sketch, "E2583", {"start": v(82.95, -112.8) * mm, "end": v(82.28, -111.72) * mm});
            skLineSegment(sketch, "E2584", {"start": v(83.62, -113.78) * mm, "end": v(82.95, -112.8) * mm});
            skLineSegment(sketch, "E2585", {"start": v(84.07, -114.4) * mm, "end": v(83.62, -113.78) * mm});
            skLineSegment(sketch, "E2586", {"start": v(84.23, -114.61) * mm, "end": v(84.07, -114.4) * mm});
            skLineSegment(sketch, "E2587", {"start": v(83.8, -114.38) * mm, "end": v(84.23, -114.61) * mm});
            skLineSegment(sketch, "E2588", {"start": v(82.63, -113.55) * mm, "end": v(83.8, -114.38) * mm});
            skLineSegment(sketch, "E2589", {"start": v(81.03, -112.17) * mm, "end": v(82.63, -113.55) * mm});
            skLineSegment(sketch, "E2590", {"start": v(79.56, -110.6) * mm, "end": v(81.03, -112.17) * mm});
            skLineSegment(sketch, "E2591", {"start": v(78.6, -109.36) * mm, "end": v(79.56, -110.6) * mm});
            skLineSegment(sketch, "E2592", {"start": v(78.31, -108.92) * mm, "end": v(78.6, -109.36) * mm});
            skLineSegment(sketch, "E2593", {"start": v(78.04, -108.5) * mm, "end": v(78.31, -108.92) * mm});
            skLineSegment(sketch, "E2594", {"start": v(77.32, -107.2) * mm, "end": v(78.04, -108.5) * mm});
            skLineSegment(sketch, "E2595", {"start": v(76.47, -105.42) * mm, "end": v(77.32, -107.2) * mm});
            skLineSegment(sketch, "E2596", {"start": v(75.74, -103.7) * mm, "end": v(76.47, -105.42) * mm});
            skLineSegment(sketch, "E2597", {"start": v(75.29, -102.52) * mm, "end": v(75.74, -103.7) * mm});
            skLineSegment(sketch, "E2598", {"start": v(75.14, -102.13) * mm, "end": v(75.29, -102.52) * mm});
            skLineSegment(sketch, "E2599", {"start": v(74.98, -101.71) * mm, "end": v(75.14, -102.13) * mm});
            skLineSegment(sketch, "E2600", {"start": v(74.52, -100.44) * mm, "end": v(74.98, -101.71) * mm});
            skLineSegment(sketch, "E2601", {"start": v(74.03, -99.16) * mm, "end": v(74.52, -100.44) * mm});
            skLineSegment(sketch, "E2602", {"start": v(73.6, -98.29) * mm, "end": v(74.03, -99.16) * mm});
            skLineSegment(sketch, "E2603", {"start": v(73.26, -97.9) * mm, "end": v(73.6, -98.29) * mm});
            skLineSegment(sketch, "E2604", {"start": v(73.12, -97.82) * mm, "end": v(73.26, -97.9) * mm});
            skLineSegment(sketch, "E2605", {"start": v(73.36, -97.86) * mm, "end": v(73.12, -97.82) * mm});
            skLineSegment(sketch, "E2606", {"start": v(74.06, -98.15) * mm, "end": v(73.36, -97.86) * mm});
            skLineSegment(sketch, "E2607", {"start": v(75.14, -98.75) * mm, "end": v(74.06, -98.15) * mm});
            skLineSegment(sketch, "E2608", {"start": v(76.3, -99.53) * mm, "end": v(75.14, -98.75) * mm});
            skLineSegment(sketch, "E2609", {"start": v(77.47, -100.38) * mm, "end": v(76.3, -99.53) * mm});
            skLineSegment(sketch, "E2610", {"start": v(78.59, -101.18) * mm, "end": v(77.47, -100.38) * mm});
            skLineSegment(sketch, "E2611", {"start": v(79.6, -101.84) * mm, "end": v(78.59, -101.18) * mm});
            skLineSegment(sketch, "E2612", {"start": v(80.45, -102.24) * mm, "end": v(79.6, -101.84) * mm});
            skLineSegment(sketch, "E2613", {"start": v(80.93, -102.34) * mm, "end": v(80.45, -102.24) * mm});
            skLineSegment(sketch, "E2614", {"start": v(81.07, -102.3) * mm, "end": v(80.93, -102.34) * mm});
            skLineSegment(sketch, "E2615", {"start": v(81.26, -102.19) * mm, "end": v(81.07, -102.3) * mm});
            skLineSegment(sketch, "E2616", {"start": v(81.82, -101.86) * mm, "end": v(81.26, -102.19) * mm});
            skLineSegment(sketch, "E2617", {"start": v(82.72, -101.3) * mm, "end": v(81.82, -101.86) * mm});
            skLineSegment(sketch, "E2618", {"start": v(83.74, -100.61) * mm, "end": v(82.72, -101.3) * mm});
            skLineSegment(sketch, "E2619", {"start": v(84.87, -99.84) * mm, "end": v(83.74, -100.61) * mm});
            skLineSegment(sketch, "E2620", {"start": v(86.06, -99) * mm, "end": v(84.87, -99.84) * mm});
            skLineSegment(sketch, "E2621", {"start": v(87.32, -98.09) * mm, "end": v(86.06, -99) * mm});
            skLineSegment(sketch, "E2622", {"start": v(88.6, -97.15) * mm, "end": v(87.32, -98.09) * mm});
            skLineSegment(sketch, "E2623", {"start": v(89.56, -96.42) * mm, "end": v(88.6, -97.15) * mm});
            skLineSegment(sketch, "E2624", {"start": v(89.88, -96.18) * mm, "end": v(89.56, -96.42) * mm});
            skLineSegment(sketch, "E2625", {"start": v(90.23, -95.92) * mm, "end": v(89.88, -96.18) * mm});
            skLineSegment(sketch, "E2626", {"start": v(91.27, -95.13) * mm, "end": v(90.23, -95.92) * mm});
            skLineSegment(sketch, "E2627", {"start": v(92.6, -94.1) * mm, "end": v(91.27, -95.13) * mm});
            skLineSegment(sketch, "E2628", {"start": v(93.85, -93.13) * mm, "end": v(92.6, -94.1) * mm});
            skLineSegment(sketch, "E2629", {"start": v(95, -92.24) * mm, "end": v(93.85, -93.13) * mm});
            skLineSegment(sketch, "E2630", {"start": v(114.58, -95.44) * mm, "end": v(116.5, -94.77) * mm});
            skLineSegment(sketch, "E2631", {"start": v(112.5, -96.2) * mm, "end": v(114.58, -95.44) * mm});
            skLineSegment(sketch, "E2632", {"start": v(122.2, -90.67) * mm, "end": v(122.22, -90.43) * mm});
            skLineSegment(sketch, "E2633", {"start": v(122.22, -90.43) * mm, "end": v(122.12, -90.44) * mm});
            skLineSegment(sketch, "E2634", {"start": v(122.12, -90.44) * mm, "end": v(121.83, -90.51) * mm});
            skLineSegment(sketch, "E2635", {"start": v(121.83, -90.51) * mm, "end": v(121.2, -90.67) * mm});
            skLineSegment(sketch, "E2636", {"start": v(121.2, -90.67) * mm, "end": v(120.38, -90.9) * mm});
            skLineSegment(sketch, "E2637", {"start": v(120.38, -90.9) * mm, "end": v(119.37, -91.19) * mm});
            skLineSegment(sketch, "E2638", {"start": v(119.37, -91.19) * mm, "end": v(118.2, -91.54) * mm});
            skLineSegment(sketch, "E2639", {"start": v(118.2, -91.54) * mm, "end": v(116.86, -91.94) * mm});
            skLineSegment(sketch, "E2640", {"start": v(116.86, -91.94) * mm, "end": v(115.4, -92.4) * mm});
            skLineSegment(sketch, "E2641", {"start": v(115.4, -92.4) * mm, "end": v(114.21, -92.79) * mm});
            skLineSegment(sketch, "E2642", {"start": v(114.21, -92.79) * mm, "end": v(113.82, -92.92) * mm});
            skLineSegment(sketch, "E2643", {"start": v(113.82, -92.92) * mm, "end": v(113.1, -93.16) * mm});
            skLineSegment(sketch, "E2644", {"start": v(113.1, -93.16) * mm, "end": v(110.98, -93.89) * mm});
            skLineSegment(sketch, "E2645", {"start": v(110.98, -93.89) * mm, "end": v(107.95, -94.98) * mm});
            skLineSegment(sketch, "E2646", {"start": v(107.95, -94.98) * mm, "end": v(104.77, -96.17) * mm});
            skLineSegment(sketch, "E2647", {"start": v(104.77, -96.17) * mm, "end": v(102.34, -97.13) * mm});
            skLineSegment(sketch, "E2648", {"start": v(102.34, -97.13) * mm, "end": v(101.53, -97.46) * mm});
            skLineSegment(sketch, "E2649", {"start": v(101.53, -97.46) * mm, "end": v(100.65, -97.82) * mm});
            skLineSegment(sketch, "E2650", {"start": v(100.65, -97.82) * mm, "end": v(96.5, -99.59) * mm});
            skLineSegment(sketch, "E2651", {"start": v(96.5, -99.59) * mm, "end": v(92.55, -101.37) * mm});
            skLineSegment(sketch, "E2652", {"start": v(92.55, -101.37) * mm, "end": v(91.79, -101.73) * mm});
            skLineSegment(sketch, "E2653", {"start": v(91.8, -99.06) * mm, "end": v(91.97, -98.95) * mm});
            skLineSegment(sketch, "E2654", {"start": v(91.97, -98.95) * mm, "end": v(92.52, -98.62) * mm});
            skLineSegment(sketch, "E2655", {"start": v(92.52, -98.62) * mm, "end": v(93.5, -98.04) * mm});
            skLineSegment(sketch, "E2656", {"start": v(93.5, -98.04) * mm, "end": v(94.71, -97.35) * mm});
            skLineSegment(sketch, "E2657", {"start": v(94.71, -97.35) * mm, "end": v(96.14, -96.55) * mm});
            skLineSegment(sketch, "E2658", {"start": v(96.14, -96.55) * mm, "end": v(97.75, -95.68) * mm});
            skLineSegment(sketch, "E2659", {"start": v(97.75, -95.68) * mm, "end": v(99.52, -94.75) * mm});
            skLineSegment(sketch, "E2660", {"start": v(99.52, -94.75) * mm, "end": v(101.44, -93.8) * mm});
            skLineSegment(sketch, "E2661", {"start": v(101.44, -93.8) * mm, "end": v(103.5, -92.82) * mm});
            skLineSegment(sketch, "E2662", {"start": v(103.5, -92.82) * mm, "end": v(105.64, -91.85) * mm});
            skLineSegment(sketch, "E2663", {"start": v(105.64, -91.85) * mm, "end": v(107.87, -90.92) * mm});
            skLineSegment(sketch, "E2664", {"start": v(107.87, -90.92) * mm, "end": v(110.16, -90.03) * mm});
            skLineSegment(sketch, "E2665", {"start": v(110.16, -90.03) * mm, "end": v(112.5, -89.22) * mm});
            skLineSegment(sketch, "E2666", {"start": v(112.5, -89.22) * mm, "end": v(114.85, -88.5) * mm});
            skLineSegment(sketch, "E2667", {"start": v(114.85, -88.5) * mm, "end": v(117.2, -87.89) * mm});
            skLineSegment(sketch, "E2668", {"start": v(117.2, -87.89) * mm, "end": v(119.52, -87.42) * mm});
            skLineSegment(sketch, "E2669", {"start": v(119.52, -87.42) * mm, "end": v(121.23, -87.16) * mm});
            skLineSegment(sketch, "E2670", {"start": v(121.23, -87.16) * mm, "end": v(121.8, -87.1) * mm});
            skLineSegment(sketch, "E2671", {"start": v(121.8, -87.1) * mm, "end": v(121.38, -87) * mm});
            skLineSegment(sketch, "E2672", {"start": v(121.38, -87) * mm, "end": v(120.1, -86.72) * mm});
            skLineSegment(sketch, "E2673", {"start": v(120.1, -86.72) * mm, "end": v(118.39, -86.43) * mm});
            skLineSegment(sketch, "E2674", {"start": v(118.39, -86.43) * mm, "end": v(116.69, -86.24) * mm});
            skLineSegment(sketch, "E2675", {"start": v(116.69, -86.24) * mm, "end": v(115.02, -86.12) * mm});
            skLineSegment(sketch, "E2676", {"start": v(115.02, -86.12) * mm, "end": v(113.4, -86.07) * mm});
            skLineSegment(sketch, "E2677", {"start": v(113.4, -86.07) * mm, "end": v(111.83, -86.08) * mm});
            skLineSegment(sketch, "E2678", {"start": v(111.83, -86.08) * mm, "end": v(110.34, -86.14) * mm});
            skLineSegment(sketch, "E2679", {"start": v(110.34, -86.14) * mm, "end": v(108.93, -86.23) * mm});
            skLineSegment(sketch, "E2680", {"start": v(108.93, -86.23) * mm, "end": v(107.62, -86.36) * mm});
            skLineSegment(sketch, "E2681", {"start": v(107.62, -86.36) * mm, "end": v(106.42, -86.5) * mm});
            skLineSegment(sketch, "E2682", {"start": v(99.97, -88.6) * mm, "end": v(99.3, -89.02) * mm});
            skLineSegment(sketch, "E2683", {"start": v(99.3, -89.02) * mm, "end": v(98.68, -89.41) * mm});
            skLineSegment(sketch, "E2684", {"start": v(98.68, -89.41) * mm, "end": v(98.18, -89.75) * mm});
            skLineSegment(sketch, "E2685", {"start": v(98.18, -89.75) * mm, "end": v(97.92, -89.94) * mm});
            skLineSegment(sketch, "E2686", {"start": v(83.46, -105.91) * mm, "end": v(82.44, -106.47) * mm});
            skLineSegment(sketch, "E2687", {"start": v(82.44, -106.47) * mm, "end": v(81.7, -106.9) * mm});
            skLineSegment(sketch, "E2688", {"start": v(81.7, -106.9) * mm, "end": v(81.39, -107.09) * mm});
            skLineSegment(sketch, "E2689", {"start": v(89.8, -102.68) * mm, "end": v(87.94, -103.6) * mm});
            skLineSegment(sketch, "E2690", {"start": v(97.74, -90.08) * mm, "end": v(97.44, -90.3) * mm});
            skLineSegment(sketch, "E2691", {"start": v(81.39, -107.09) * mm, "end": v(81.3, -107.16) * mm});
            skLineSegment(sketch, "E2692", {"start": v(87.94, -103.6) * mm, "end": v(86.25, -104.45) * mm});
            skLineSegment(sketch, "E2693", {"start": v(97.44, -90.3) * mm, "end": v(96.82, -90.8) * mm});
            skLineSegment(sketch, "E2694", {"start": v(81.3, -107.16) * mm, "end": v(81.52, -107.35) * mm});
            skLineSegment(sketch, "E2695", {"start": v(86.25, -104.45) * mm, "end": v(84.74, -105.23) * mm});
            skLineSegment(sketch, "E2696", {"start": v(96.82, -90.8) * mm, "end": v(96, -91.45) * mm});
            skLineSegment(sketch, "E2697", {"start": v(81.52, -107.35) * mm, "end": v(82.26, -107.84) * mm});
            skLineSegment(sketch, "E2698", {"start": v(84.74, -105.23) * mm, "end": v(83.46, -105.91) * mm});
            skLineSegment(sketch, "E2699", {"start": v(96, -91.45) * mm, "end": v(95, -92.24) * mm});
            skLineSegment(sketch, "E2700", {"start": v(91.79, -101.73) * mm, "end": v(91.29, -101.97) * mm});
            skLineSegment(sketch, "E2701", {"start": v(82.26, -107.84) * mm, "end": v(83.59, -108.6) * mm});
            skLineSegment(sketch, "E2702", {"start": v(83.59, -108.6) * mm, "end": v(85.22, -109.43) * mm});
            skLineSegment(sketch, "E2703", {"start": v(95.83, -113.4) * mm, "end": v(96.1, -113.47) * mm});
            skLineSegment(sketch, "E2704", {"start": v(96.1, -113.47) * mm, "end": v(96.93, -113.68) * mm});
            skLineSegment(sketch, "E2705", {"start": v(96.93, -113.68) * mm, "end": v(98.08, -113.95) * mm});
            skLineSegment(sketch, "E2706", {"start": v(98.08, -113.95) * mm, "end": v(99.22, -114.18) * mm});
            skLineSegment(sketch, "E2707", {"start": v(95.26, -113.24) * mm, "end": v(95.83, -113.4) * mm});
            skLineSegment(sketch, "E2708", {"start": v(93.58, -112.73) * mm, "end": v(95.26, -113.24) * mm});
            skLineSegment(sketch, "E2709", {"start": v(91.33, -111.97) * mm, "end": v(93.58, -112.73) * mm});
            skLineSegment(sketch, "E2710", {"start": v(89.15, -111.14) * mm, "end": v(91.33, -111.97) * mm});
            skLineSegment(sketch, "E2711", {"start": v(87.1, -110.29) * mm, "end": v(89.15, -111.14) * mm});
            skLineSegment(sketch, "E2712", {"start": v(85.22, -109.43) * mm, "end": v(87.1, -110.29) * mm});
            skLineSegment(sketch, "E2713", {"start": v(97.84, -90) * mm, "end": v(97.74, -90.08) * mm});
            skLineSegment(sketch, "E2714", {"start": v(91.29, -101.97) * mm, "end": v(89.8, -102.68) * mm});
            skLineSegment(sketch, "E2715", {"start": v(100.67, -88.17) * mm, "end": v(99.97, -88.6) * mm});
            skLineSegment(sketch, "E2716", {"start": v(97.92, -89.94) * mm, "end": v(97.84, -90) * mm});
            skLineSegment(sketch, "E2717", {"start": v(101.35, -87.79) * mm, "end": v(100.67, -88.17) * mm});
            skLineSegment(sketch, "E2718", {"start": v(101.96, -87.47) * mm, "end": v(101.35, -87.79) * mm});
            skLineSegment(sketch, "E2719", {"start": v(102.33, -87.3) * mm, "end": v(101.96, -87.47) * mm});
            skLineSegment(sketch, "E2720", {"start": v(102.46, -87.25) * mm, "end": v(102.33, -87.3) * mm});
            skLineSegment(sketch, "E2721", {"start": v(102.5, -87.23) * mm, "end": v(102.46, -87.25) * mm});
            skLineSegment(sketch, "E2722", {"start": v(102.66, -87.2) * mm, "end": v(102.5, -87.23) * mm});
            skLineSegment(sketch, "E2723", {"start": v(103.07, -87.1) * mm, "end": v(102.66, -87.2) * mm});
            skLineSegment(sketch, "E2724", {"start": v(103.67, -86.96) * mm, "end": v(103.07, -87.1) * mm});
            skLineSegment(sketch, "E2725", {"start": v(104.43, -86.82) * mm, "end": v(103.67, -86.96) * mm});
            skLineSegment(sketch, "E2726", {"start": v(105.35, -86.66) * mm, "end": v(104.43, -86.82) * mm});
            skLineSegment(sketch, "E2727", {"start": v(106.42, -86.5) * mm, "end": v(105.35, -86.66) * mm});
            skLineSegment(sketch, "E2728", {"start": v(122, -91.41) * mm, "end": v(122.2, -90.67) * mm});
            skLineSegment(sketch, "E2729", {"start": v(121.5, -92.36) * mm, "end": v(122, -91.41) * mm});
            skLineSegment(sketch, "E2730", {"start": v(120.74, -93.16) * mm, "end": v(121.5, -92.36) * mm});
            skLineSegment(sketch, "E2731", {"start": v(120, -93.6) * mm, "end": v(120.74, -93.16) * mm});
            skLineSegment(sketch, "E2732", {"start": v(119.74, -93.69) * mm, "end": v(120, -93.6) * mm});
            skLineSegment(sketch, "E2733", {"start": v(119.36, -93.8) * mm, "end": v(119.74, -93.69) * mm});
            skLineSegment(sketch, "E2734", {"start": v(118.23, -94.18) * mm, "end": v(119.36, -93.8) * mm});
            skLineSegment(sketch, "E2735", {"start": v(116.5, -94.77) * mm, "end": v(118.23, -94.18) * mm});
            skLineSegment(sketch, "E2736", {"start": v(93.57, -105.44) * mm, "end": v(92.38, -105.97) * mm});
            skLineSegment(sketch, "E2737", {"start": v(95.03, -104.8) * mm, "end": v(93.57, -105.44) * mm});
            skLineSegment(sketch, "E2738", {"start": v(96.72, -104.05) * mm, "end": v(95.03, -104.8) * mm});
            skLineSegment(sketch, "E2739", {"start": v(98.61, -103.24) * mm, "end": v(96.72, -104.05) * mm});
            skLineSegment(sketch, "E2740", {"start": v(100.66, -102.36) * mm, "end": v(98.61, -103.24) * mm});
            skLineSegment(sketch, "E2741", {"start": v(102.85, -101.45) * mm, "end": v(100.66, -102.36) * mm});
            skLineSegment(sketch, "E2742", {"start": v(105.13, -100.51) * mm, "end": v(102.85, -101.45) * mm});
            skLineSegment(sketch, "E2743", {"start": v(107.47, -99.57) * mm, "end": v(105.13, -100.51) * mm});
            skLineSegment(sketch, "E2744", {"start": v(109.84, -98.64) * mm, "end": v(107.47, -99.57) * mm});
            skLineSegment(sketch, "E2745", {"start": v(112.21, -97.74) * mm, "end": v(109.84, -98.64) * mm});
            skLineSegment(sketch, "E2746", {"start": v(114.55, -96.88) * mm, "end": v(112.21, -97.74) * mm});
            skLineSegment(sketch, "E2747", {"start": v(116.8, -96.1) * mm, "end": v(114.55, -96.88) * mm});
            skLineSegment(sketch, "E2748", {"start": v(118.42, -95.56) * mm, "end": v(116.8, -96.1) * mm});
            skLineSegment(sketch, "E2749", {"start": v(118.96, -95.4) * mm, "end": v(118.42, -95.56) * mm});
            skLineSegment(sketch, "E2750", {"start": v(118.92, -95.52) * mm, "end": v(118.96, -95.4) * mm});
            skLineSegment(sketch, "E2751", {"start": v(118.78, -95.9) * mm, "end": v(118.92, -95.52) * mm});
            skLineSegment(sketch, "E2752", {"start": v(118.46, -96.62) * mm, "end": v(118.78, -95.9) * mm});
            skLineSegment(sketch, "E2753", {"start": v(118.03, -97.52) * mm, "end": v(118.46, -96.62) * mm});
            skLineSegment(sketch, "E2754", {"start": v(117.49, -98.57) * mm, "end": v(118.03, -97.52) * mm});
            skLineSegment(sketch, "E2755", {"start": v(116.85, -99.73) * mm, "end": v(117.49, -98.57) * mm});
            skLineSegment(sketch, "E2756", {"start": v(116.14, -101) * mm, "end": v(116.85, -99.73) * mm});
            skLineSegment(sketch, "E2757", {"start": v(115.36, -102.31) * mm, "end": v(116.14, -101) * mm});
            skLineSegment(sketch, "E2758", {"start": v(114.74, -103.33) * mm, "end": v(115.36, -102.31) * mm});
            skLineSegment(sketch, "E2759", {"start": v(114.53, -103.66) * mm, "end": v(114.74, -103.33) * mm});
            skLineSegment(sketch, "E2760", {"start": v(103.99, -114.47) * mm, "end": v(104.64, -114.2) * mm});
            skLineSegment(sketch, "E2761", {"start": v(103.5, -114.63) * mm, "end": v(103.99, -114.47) * mm});
            skLineSegment(sketch, "E2762", {"start": v(103.29, -114.68) * mm, "end": v(103.5, -114.63) * mm});
            skLineSegment(sketch, "E2763", {"start": v(103.22, -114.7) * mm, "end": v(103.29, -114.68) * mm});
            skLineSegment(sketch, "E2764", {"start": v(103.11, -114.7) * mm, "end": v(103.22, -114.7) * mm});
            skLineSegment(sketch, "E2765", {"start": v(102.8, -114.7) * mm, "end": v(103.11, -114.7) * mm});
            skLineSegment(sketch, "E2766", {"start": v(99.22, -114.18) * mm, "end": v(100.3, -114.38) * mm});
            skLineSegment(sketch, "E2767", {"start": v(100.3, -114.38) * mm, "end": v(101.3, -114.54) * mm});
            skLineSegment(sketch, "E2768", {"start": v(101.3, -114.54) * mm, "end": v(102.14, -114.65) * mm});
            skLineSegment(sketch, "E2769", {"start": v(102.14, -114.65) * mm, "end": v(102.8, -114.7) * mm});
            skLineSegment(sketch, "E2770", {"start": v(104.64, -114.2) * mm, "end": v(105.46, -113.76) * mm});
            skLineSegment(sketch, "E2771", {"start": v(105.46, -113.76) * mm, "end": v(106.4, -113.13) * mm});
            skLineSegment(sketch, "E2772", {"start": v(106.4, -113.13) * mm, "end": v(107.48, -112.29) * mm});
            skLineSegment(sketch, "E2773", {"start": v(107.48, -112.29) * mm, "end": v(108.66, -111.19) * mm});
            skLineSegment(sketch, "E2774", {"start": v(108.66, -111.19) * mm, "end": v(109.62, -110.16) * mm});
            skLineSegment(sketch, "E2775", {"start": v(109.62, -110.16) * mm, "end": v(109.92, -109.8) * mm});
            skLineSegment(sketch, "E2776", {"start": v(109.92, -109.8) * mm, "end": v(110.21, -109.46) * mm});
            skLineSegment(sketch, "E2777", {"start": v(110.21, -109.46) * mm, "end": v(111.07, -108.41) * mm});
            skLineSegment(sketch, "E2778", {"start": v(111.07, -108.41) * mm, "end": v(112.26, -106.9) * mm});
            skLineSegment(sketch, "E2779", {"start": v(112.26, -106.9) * mm, "end": v(113.43, -105.31) * mm});
            skLineSegment(sketch, "E2780", {"start": v(113.43, -105.31) * mm, "end": v(114.27, -104.08) * mm});
            skLineSegment(sketch, "E2781", {"start": v(114.27, -104.08) * mm, "end": v(114.53, -103.66) * mm});
            skLineSegment(sketch, "E2782", {"start": v(92.38, -105.97) * mm, "end": v(91.48, -106.37) * mm});
            skLineSegment(sketch, "E2783", {"start": v(91.48, -106.37) * mm, "end": v(90.92, -106.62) * mm});
            skLineSegment(sketch, "E2784", {"start": v(90.92, -106.62) * mm, "end": v(90.73, -106.71) * mm});
            skLineSegment(sketch, "E2785", {"start": v(90.73, -106.71) * mm, "end": v(109.88, -101.23) * mm});
            skLineSegment(sketch, "E2786", {"start": v(109.88, -101.23) * mm, "end": v(109.8, -101.38) * mm});
            skLineSegment(sketch, "E2787", {"start": v(109.8, -101.38) * mm, "end": v(109.6, -101.77) * mm});
            skLineSegment(sketch, "E2788", {"start": v(109.6, -101.77) * mm, "end": v(109.26, -102.38) * mm});
            skLineSegment(sketch, "E2789", {"start": v(109.26, -102.38) * mm, "end": v(108.82, -103.15) * mm});
            skLineSegment(sketch, "E2790", {"start": v(108.82, -103.15) * mm, "end": v(108.27, -104.04) * mm});
            skLineSegment(sketch, "E2791", {"start": v(108.27, -104.04) * mm, "end": v(107.64, -105) * mm});
            skLineSegment(sketch, "E2792", {"start": v(107.64, -105) * mm, "end": v(106.94, -106) * mm});
            skLineSegment(sketch, "E2793", {"start": v(106.94, -106) * mm, "end": v(106.37, -106.73) * mm});
            skLineSegment(sketch, "E2794", {"start": v(106.37, -106.73) * mm, "end": v(106.17, -106.97) * mm});
            skLineSegment(sketch, "E2795", {"start": v(106.17, -106.97) * mm, "end": v(105.9, -107.3) * mm});
            skLineSegment(sketch, "E2796", {"start": v(105.9, -107.3) * mm, "end": v(104.98, -108.25) * mm});
            skLineSegment(sketch, "E2797", {"start": v(104.98, -108.25) * mm, "end": v(103.83, -109.24) * mm});
            skLineSegment(sketch, "E2798", {"start": v(103.83, -109.24) * mm, "end": v(102.74, -109.96) * mm});
            skLineSegment(sketch, "E2799", {"start": v(102.74, -109.96) * mm, "end": v(101.98, -110.33) * mm});
            skLineSegment(sketch, "E2800", {"start": v(101.98, -110.33) * mm, "end": v(101.71, -110.43) * mm});
            skLineSegment(sketch, "E2801", {"start": v(101.71, -110.43) * mm, "end": v(101.52, -110.5) * mm});
            skLineSegment(sketch, "E2802", {"start": v(101.52, -110.5) * mm, "end": v(100.93, -110.67) * mm});
            skLineSegment(sketch, "E2803", {"start": v(100.93, -110.67) * mm, "end": v(99.93, -110.83) * mm});
            skLineSegment(sketch, "E2804", {"start": v(99.93, -110.83) * mm, "end": v(98.68, -110.85) * mm});
            skLineSegment(sketch, "E2805", {"start": v(98.68, -110.85) * mm, "end": v(97.5, -110.73) * mm});
            skLineSegment(sketch, "E2806", {"start": v(97.5, -110.73) * mm, "end": v(97.11, -110.66) * mm});
            skLineSegment(sketch, "E2807", {"start": v(97.11, -110.66) * mm, "end": v(96.65, -110.57) * mm});
            skLineSegment(sketch, "E2808", {"start": v(96.65, -110.57) * mm, "end": v(95.28, -110.26) * mm});
            skLineSegment(sketch, "E2809", {"start": v(95.28, -110.26) * mm, "end": v(93.56, -109.8) * mm});
            skLineSegment(sketch, "E2810", {"start": v(93.56, -109.8) * mm, "end": v(91.96, -109.31) * mm});
            skLineSegment(sketch, "E2811", {"start": v(91.96, -109.31) * mm, "end": v(90.53, -108.8) * mm});
            skLineSegment(sketch, "E2812", {"start": v(90.53, -108.8) * mm, "end": v(89.3, -108.32) * mm});
            skLineSegment(sketch, "E2813", {"start": v(89.3, -108.32) * mm, "end": v(88.26, -107.88) * mm});
            skLineSegment(sketch, "E2814", {"start": v(88.26, -107.88) * mm, "end": v(87.48, -107.51) * mm});
            skLineSegment(sketch, "E2815", {"start": v(87.48, -107.51) * mm, "end": v(87.08, -107.31) * mm});
            skLineSegment(sketch, "E2816", {"start": v(87.08, -107.31) * mm, "end": v(86.96, -107.24) * mm});
            skLineSegment(sketch, "E2817", {"start": v(86.96, -107.24) * mm, "end": v(87.32, -107.03) * mm});
            skLineSegment(sketch, "E2818", {"start": v(87.32, -107.03) * mm, "end": v(88.43, -106.43) * mm});
            skLineSegment(sketch, "E2819", {"start": v(88.43, -106.43) * mm, "end": v(90.12, -105.55) * mm});
            skLineSegment(sketch, "E2820", {"start": v(90.12, -105.55) * mm, "end": v(92.01, -104.64) * mm});
            skLineSegment(sketch, "E2821", {"start": v(92.01, -104.64) * mm, "end": v(94.06, -103.69) * mm});
            skLineSegment(sketch, "E2822", {"start": v(94.06, -103.69) * mm, "end": v(96.25, -102.71) * mm});
            skLineSegment(sketch, "E2823", {"start": v(96.25, -102.71) * mm, "end": v(98.53, -101.73) * mm});
            skLineSegment(sketch, "E2824", {"start": v(98.53, -101.73) * mm, "end": v(100.88, -100.75) * mm});
            skLineSegment(sketch, "E2825", {"start": v(100.88, -100.75) * mm, "end": v(103.26, -99.77) * mm});
            skLineSegment(sketch, "E2826", {"start": v(103.26, -99.77) * mm, "end": v(105.64, -98.82) * mm});
            skLineSegment(sketch, "E2827", {"start": v(105.64, -98.82) * mm, "end": v(108, -97.9) * mm});
            skLineSegment(sketch, "E2828", {"start": v(108, -97.9) * mm, "end": v(110.3, -97.02) * mm});
            skLineSegment(sketch, "E2829", {"start": v(110.3, -97.02) * mm, "end": v(112.5, -96.2) * mm});
            skLineSegment(sketch, "E2830", {"start": v(-12.46, -128.21) * mm, "end": v(-12.14, -128) * mm});
            skLineSegment(sketch, "E2831", {"start": v(-13.43, -128.8) * mm, "end": v(-12.46, -128.21) * mm});
            skLineSegment(sketch, "E2832", {"start": v(-14.61, -129.45) * mm, "end": v(-13.43, -128.8) * mm});
            skLineSegment(sketch, "E2833", {"start": v(-15.58, -129.9) * mm, "end": v(-14.61, -129.45) * mm});
            skLineSegment(sketch, "E2834", {"start": v(-16.07, -130.07) * mm, "end": v(-15.58, -129.9) * mm});
            skLineSegment(sketch, "E2835", {"start": v(-16.23, -130.1) * mm, "end": v(-16.07, -130.07) * mm});
            skLineSegment(sketch, "E2836", {"start": v(-16.35, -130.1) * mm, "end": v(-16.23, -130.1) * mm});
            skLineSegment(sketch, "E2837", {"start": v(-16.72, -130.12) * mm, "end": v(-16.35, -130.1) * mm});
            skLineSegment(sketch, "E2838", {"start": v(-17.44, -130.12) * mm, "end": v(-16.72, -130.12) * mm});
            skLineSegment(sketch, "E2839", {"start": v(-18.34, -130.05) * mm, "end": v(-17.44, -130.12) * mm});
            skLineSegment(sketch, "E2840", {"start": v(-19.14, -129.95) * mm, "end": v(-18.34, -130.05) * mm});
            skLineSegment(sketch, "E2841", {"start": v(-19.4, -129.9) * mm, "end": v(-19.14, -129.95) * mm});
            skLineSegment(sketch, "E2842", {"start": v(-19.62, -129.87) * mm, "end": v(-19.4, -129.9) * mm});
            skLineSegment(sketch, "E2843", {"start": v(-20.27, -129.75) * mm, "end": v(-19.62, -129.87) * mm});
            skLineSegment(sketch, "E2844", {"start": v(-21.15, -129.57) * mm, "end": v(-20.27, -129.75) * mm});
            skLineSegment(sketch, "E2845", {"start": v(-22, -129.39) * mm, "end": v(-21.15, -129.57) * mm});
            skLineSegment(sketch, "E2846", {"start": v(-22.77, -129.21) * mm, "end": v(-22, -129.39) * mm});
            skLineSegment(sketch, "E2847", {"start": v(-23.44, -129.05) * mm, "end": v(-22.77, -129.21) * mm});
            skLineSegment(sketch, "E2848", {"start": v(-23.96, -128.93) * mm, "end": v(-23.44, -129.05) * mm});
            skLineSegment(sketch, "E2849", {"start": v(-24.3, -128.84) * mm, "end": v(-23.96, -128.93) * mm});
            skLineSegment(sketch, "E2850", {"start": v(-24.43, -128.8) * mm, "end": v(-24.3, -128.84) * mm});
            skLineSegment(sketch, "E2851", {"start": v(-24.22, -128.77) * mm, "end": v(-24.43, -128.8) * mm});
            skLineSegment(sketch, "E2852", {"start": v(-23.62, -128.66) * mm, "end": v(-24.22, -128.77) * mm});
            skLineSegment(sketch, "E2853", {"start": v(-22.72, -128.5) * mm, "end": v(-23.62, -128.66) * mm});
            skLineSegment(sketch, "E2854", {"start": v(-21.56, -128.28) * mm, "end": v(-22.72, -128.5) * mm});
            skLineSegment(sketch, "E2855", {"start": v(-20.23, -128.02) * mm, "end": v(-21.56, -128.28) * mm});
            skLineSegment(sketch, "E2856", {"start": v(-18.77, -127.72) * mm, "end": v(-20.23, -128.02) * mm});
            skLineSegment(sketch, "E2857", {"start": v(-17.26, -127.41) * mm, "end": v(-18.77, -127.72) * mm});
            skLineSegment(sketch, "E2858", {"start": v(-16.13, -127.17) * mm, "end": v(-17.26, -127.41) * mm});
            skLineSegment(sketch, "E2859", {"start": v(-15.76, -127.08) * mm, "end": v(-16.13, -127.17) * mm});
            skLineSegment(sketch, "E2860", {"start": v(-15.4, -127) * mm, "end": v(-15.76, -127.08) * mm});
            skLineSegment(sketch, "E2861", {"start": v(-14.28, -126.74) * mm, "end": v(-15.4, -127) * mm});
            skLineSegment(sketch, "E2862", {"start": v(-12.9, -126.41) * mm, "end": v(-14.28, -126.74) * mm});
            skLineSegment(sketch, "E2863", {"start": v(-11.67, -126.1) * mm, "end": v(-12.9, -126.41) * mm});
            skLineSegment(sketch, "E2864", {"start": v(-10.6, -125.82) * mm, "end": v(-11.67, -126.1) * mm});
            skLineSegment(sketch, "E2865", {"start": v(-9.7, -125.58) * mm, "end": v(-10.6, -125.82) * mm});
            skLineSegment(sketch, "E2866", {"start": v(-9.03, -125.4) * mm, "end": v(-9.7, -125.58) * mm});
            skLineSegment(sketch, "E2867", {"start": v(-8.61, -125.27) * mm, "end": v(-9.03, -125.4) * mm});
            skLineSegment(sketch, "E2868", {"start": v(-8.46, -125.23) * mm, "end": v(-8.61, -125.27) * mm});
            skLineSegment(sketch, "E2869", {"start": v(-8.55, -125.3) * mm, "end": v(-8.46, -125.23) * mm});
            skLineSegment(sketch, "E2870", {"start": v(-8.78, -125.49) * mm, "end": v(-8.55, -125.3) * mm});
            skLineSegment(sketch, "E2871", {"start": v(-9.14, -125.78) * mm, "end": v(-8.78, -125.49) * mm});
            skLineSegment(sketch, "E2872", {"start": v(-9.61, -126.16) * mm, "end": v(-9.14, -125.78) * mm});
            skLineSegment(sketch, "E2873", {"start": v(-10.17, -126.59) * mm, "end": v(-9.61, -126.16) * mm});
            skLineSegment(sketch, "E2874", {"start": v(-10.8, -127.05) * mm, "end": v(-10.17, -126.59) * mm});
            skLineSegment(sketch, "E2875", {"start": v(-11.46, -127.53) * mm, "end": v(-10.8, -127.05) * mm});
            skLineSegment(sketch, "E2876", {"start": v(-11.97, -127.89) * mm, "end": v(-11.46, -127.53) * mm});
            skLineSegment(sketch, "E2877", {"start": v(-12.14, -128) * mm, "end": v(-11.97, -127.89) * mm});
            skLineSegment(sketch, "E2878", {"start": v(-8.94, -108.31) * mm, "end": v(-9.05, -107.7) * mm});
            skLineSegment(sketch, "E2879", {"start": v(-8.61, -110.15) * mm, "end": v(-8.94, -108.31) * mm});
            skLineSegment(sketch, "E2880", {"start": v(-8.2, -112.49) * mm, "end": v(-8.61, -110.15) * mm});
            skLineSegment(sketch, "E2881", {"start": v(-7.81, -114.66) * mm, "end": v(-8.2, -112.49) * mm});
            skLineSegment(sketch, "E2882", {"start": v(-7.4, -116.63) * mm, "end": v(-7.81, -114.66) * mm});
            skLineSegment(sketch, "E2883", {"start": v(-6.98, -118.34) * mm, "end": v(-7.4, -116.63) * mm});
            skLineSegment(sketch, "E2884", {"start": v(-6.5, -119.74) * mm, "end": v(-6.98, -118.34) * mm});
            skLineSegment(sketch, "E2885", {"start": v(-5.94, -120.77) * mm, "end": v(-6.5, -119.74) * mm});
            skLineSegment(sketch, "E2886", {"start": v(-5.48, -121.29) * mm, "end": v(-5.94, -120.77) * mm});
            skLineSegment(sketch, "E2887", {"start": v(-5.29, -121.4) * mm, "end": v(-5.48, -121.29) * mm});
            skLineSegment(sketch, "E2888", {"start": v(-5.18, -121.46) * mm, "end": v(-5.29, -121.4) * mm});
            skLineSegment(sketch, "E2889", {"start": v(-4.8, -121.51) * mm, "end": v(-5.18, -121.46) * mm});
            skLineSegment(sketch, "E2890", {"start": v(-4, -121.52) * mm, "end": v(-4.8, -121.51) * mm});
            skLineSegment(sketch, "E2891", {"start": v(-2.98, -121.43) * mm, "end": v(-4, -121.52) * mm});
            skLineSegment(sketch, "E2892", {"start": v(-1.8, -121.27) * mm, "end": v(-2.98, -121.43) * mm});
            skLineSegment(sketch, "E2893", {"start": v(-0.55, -121.06) * mm, "end": v(-1.8, -121.27) * mm});
            skLineSegment(sketch, "E2894", {"start": v(0.7, -120.8) * mm, "end": v(-0.55, -121.06) * mm});
            skLineSegment(sketch, "E2895", {"start": v(1.85, -120.53) * mm, "end": v(0.7, -120.8) * mm});
            skLineSegment(sketch, "E2896", {"start": v(2.6, -120.32) * mm, "end": v(1.85, -120.53) * mm});
            skLineSegment(sketch, "E2897", {"start": v(2.84, -120.25) * mm, "end": v(2.6, -120.32) * mm});
            skLineSegment(sketch, "E2898", {"start": v(2.48, -120.56) * mm, "end": v(2.84, -120.25) * mm});
            skLineSegment(sketch, "E2899", {"start": v(1.28, -121.37) * mm, "end": v(2.48, -120.56) * mm});
            skLineSegment(sketch, "E2900", {"start": v(-0.56, -122.38) * mm, "end": v(1.28, -121.37) * mm});
            skLineSegment(sketch, "E2901", {"start": v(-2.56, -123.2) * mm, "end": v(-0.56, -122.38) * mm});
            skLineSegment(sketch, "E2902", {"start": v(-4.06, -123.67) * mm, "end": v(-2.56, -123.2) * mm});
            skLineSegment(sketch, "E2903", {"start": v(-4.57, -123.79) * mm, "end": v(-4.06, -123.67) * mm});
            skLineSegment(sketch, "E2904", {"start": v(-5.05, -123.9) * mm, "end": v(-4.57, -123.79) * mm});
            skLineSegment(sketch, "E2905", {"start": v(-6.52, -124.1) * mm, "end": v(-5.05, -123.9) * mm});
            skLineSegment(sketch, "E2906", {"start": v(-8.49, -124.28) * mm, "end": v(-6.52, -124.1) * mm});
            skLineSegment(sketch, "E2907", {"start": v(-10.36, -124.36) * mm, "end": v(-8.49, -124.28) * mm});
            skLineSegment(sketch, "E2908", {"start": v(-11.62, -124.37) * mm, "end": v(-10.36, -124.36) * mm});
            skLineSegment(sketch, "E2909", {"start": v(-12.03, -124.37) * mm, "end": v(-11.62, -124.37) * mm});
            skLineSegment(sketch, "E2910", {"start": v(-12.48, -124.37) * mm, "end": v(-12.03, -124.37) * mm});
            skLineSegment(sketch, "E2911", {"start": v(-13.83, -124.35) * mm, "end": v(-12.48, -124.37) * mm});
            skLineSegment(sketch, "E2912", {"start": v(-15.2, -124.36) * mm, "end": v(-13.83, -124.35) * mm});
            skLineSegment(sketch, "E2913", {"start": v(-16.18, -124.47) * mm, "end": v(-15.2, -124.36) * mm});
            skLineSegment(sketch, "E2914", {"start": v(-16.67, -124.64) * mm, "end": v(-16.18, -124.47) * mm});
            skLineSegment(sketch, "E2915", {"start": v(-16.78, -124.74) * mm, "end": v(-16.67, -124.64) * mm});
            skLineSegment(sketch, "E2916", {"start": v(-16.66, -124.53) * mm, "end": v(-16.78, -124.74) * mm});
            skLineSegment(sketch, "E2917", {"start": v(-16.14, -123.98) * mm, "end": v(-16.66, -124.53) * mm});
            skLineSegment(sketch, "E2918", {"start": v(-15.2, -123.18) * mm, "end": v(-16.14, -123.98) * mm});
            skLineSegment(sketch, "E2919", {"start": v(-14.06, -122.37) * mm, "end": v(-15.2, -123.18) * mm});
            skLineSegment(sketch, "E2920", {"start": v(-12.86, -121.57) * mm, "end": v(-14.06, -122.37) * mm});
            skLineSegment(sketch, "E2921", {"start": v(-11.72, -120.8) * mm, "end": v(-12.86, -121.57) * mm});
            skLineSegment(sketch, "E2922", {"start": v(-10.74, -120.09) * mm, "end": v(-11.72, -120.8) * mm});
            skLineSegment(sketch, "E2923", {"start": v(-10.06, -119.44) * mm, "end": v(-10.74, -120.09) * mm});
            skLineSegment(sketch, "E2924", {"start": v(-9.8, -119.02) * mm, "end": v(-10.06, -119.44) * mm});
            skLineSegment(sketch, "E2925", {"start": v(-9.8, -118.87) * mm, "end": v(-9.8, -119.02) * mm});
            skLineSegment(sketch, "E2926", {"start": v(-9.83, -118.66) * mm, "end": v(-9.8, -118.87) * mm});
            skLineSegment(sketch, "E2927", {"start": v(-9.94, -118.02) * mm, "end": v(-9.83, -118.66) * mm});
            skLineSegment(sketch, "E2928", {"start": v(-10.16, -116.98) * mm, "end": v(-9.94, -118.02) * mm});
            skLineSegment(sketch, "E2929", {"start": v(-10.43, -115.78) * mm, "end": v(-10.16, -116.98) * mm});
            skLineSegment(sketch, "E2930", {"start": v(-10.76, -114.46) * mm, "end": v(-10.43, -115.78) * mm});
            skLineSegment(sketch, "E2931", {"start": v(-11.13, -113.04) * mm, "end": v(-10.76, -114.46) * mm});
            skLineSegment(sketch, "E2932", {"start": v(-11.54, -111.55) * mm, "end": v(-11.13, -113.04) * mm});
            skLineSegment(sketch, "E2933", {"start": v(-11.97, -110.02) * mm, "end": v(-11.54, -111.55) * mm});
            skLineSegment(sketch, "E2934", {"start": v(-12.3, -108.86) * mm, "end": v(-11.97, -110.02) * mm});
            skLineSegment(sketch, "E2935", {"start": v(-12.42, -108.48) * mm, "end": v(-12.3, -108.86) * mm});
            skLineSegment(sketch, "E2936", {"start": v(-12.54, -108.06) * mm, "end": v(-12.42, -108.48) * mm});
            skLineSegment(sketch, "E2937", {"start": v(-12.92, -106.8) * mm, "end": v(-12.54, -108.06) * mm});
            skLineSegment(sketch, "E2938", {"start": v(-13.41, -105.2) * mm, "end": v(-12.92, -106.8) * mm});
            skLineSegment(sketch, "E2939", {"start": v(-13.88, -103.68) * mm, "end": v(-13.41, -105.2) * mm});
            skLineSegment(sketch, "E2940", {"start": v(-14.32, -102.3) * mm, "end": v(-13.88, -103.68) * mm});
            skLineSegment(sketch, "E2941", {"start": v(-4.43, -85.1) * mm, "end": v(-4.39, -83.06) * mm});
            skLineSegment(sketch, "E2942", {"start": v(-4.45, -87.3) * mm, "end": v(-4.43, -85.1) * mm});
            skLineSegment(sketch, "E2943", {"start": v(-6.21, -76.29) * mm, "end": v(-6.44, -76.18) * mm});
            skLineSegment(sketch, "E2944", {"start": v(-6.44, -76.18) * mm, "end": v(-6.46, -76.28) * mm});
            skLineSegment(sketch, "E2945", {"start": v(-6.46, -76.28) * mm, "end": v(-6.5, -76.58) * mm});
            skLineSegment(sketch, "E2946", {"start": v(-6.5, -76.58) * mm, "end": v(-6.56, -77.21) * mm});
            skLineSegment(sketch, "E2947", {"start": v(-6.56, -77.21) * mm, "end": v(-6.64, -78.06) * mm});
            skLineSegment(sketch, "E2948", {"start": v(-6.64, -78.06) * mm, "end": v(-6.73, -79.1) * mm});
            skLineSegment(sketch, "E2949", {"start": v(-6.73, -79.1) * mm, "end": v(-6.82, -80.34) * mm});
            skLineSegment(sketch, "E2950", {"start": v(-6.82, -80.34) * mm, "end": v(-6.9, -81.73) * mm});
            skLineSegment(sketch, "E2951", {"start": v(-6.9, -81.73) * mm, "end": v(-6.98, -83.26) * mm});
            skLineSegment(sketch, "E2952", {"start": v(-6.98, -83.26) * mm, "end": v(-7.04, -84.5) * mm});
            skLineSegment(sketch, "E2953", {"start": v(-7.04, -84.5) * mm, "end": v(-7.06, -84.92) * mm});
            skLineSegment(sketch, "E2954", {"start": v(-7.06, -84.92) * mm, "end": v(-7.09, -85.67) * mm});
            skLineSegment(sketch, "E2955", {"start": v(-7.09, -85.67) * mm, "end": v(-7.15, -87.92) * mm});
            skLineSegment(sketch, "E2956", {"start": v(-7.15, -87.92) * mm, "end": v(-7.2, -91.14) * mm});
            skLineSegment(sketch, "E2957", {"start": v(-7.2, -91.14) * mm, "end": v(-7.2, -94.53) * mm});
            skLineSegment(sketch, "E2958", {"start": v(-7.2, -94.53) * mm, "end": v(-7.15, -97.15) * mm});
            skLineSegment(sketch, "E2959", {"start": v(-7.15, -97.15) * mm, "end": v(-7.13, -98.02) * mm});
            skLineSegment(sketch, "E2960", {"start": v(-7.13, -98.02) * mm, "end": v(-7.1, -98.97) * mm});
            skLineSegment(sketch, "E2961", {"start": v(-7.1, -98.97) * mm, "end": v(-6.9, -103.48) * mm});
            skLineSegment(sketch, "E2962", {"start": v(-6.9, -103.48) * mm, "end": v(-6.63, -107.8) * mm});
            skLineSegment(sketch, "E2963", {"start": v(-6.63, -107.8) * mm, "end": v(-6.56, -108.64) * mm});
            skLineSegment(sketch, "E2964", {"start": v(-9.05, -107.7) * mm, "end": v(-9.1, -107.5) * mm});
            skLineSegment(sketch, "E2965", {"start": v(-9.1, -107.5) * mm, "end": v(-9.2, -106.86) * mm});
            skLineSegment(sketch, "E2966", {"start": v(-9.2, -106.86) * mm, "end": v(-9.4, -105.74) * mm});
            skLineSegment(sketch, "E2967", {"start": v(-9.4, -105.74) * mm, "end": v(-9.63, -104.36) * mm});
            skLineSegment(sketch, "E2968", {"start": v(-9.63, -104.36) * mm, "end": v(-9.88, -102.75) * mm});
            skLineSegment(sketch, "E2969", {"start": v(-9.88, -102.75) * mm, "end": v(-10.13, -100.94) * mm});
            skLineSegment(sketch, "E2970", {"start": v(-10.13, -100.94) * mm, "end": v(-10.37, -98.95) * mm});
            skLineSegment(sketch, "E2971", {"start": v(-10.37, -98.95) * mm, "end": v(-10.6, -96.81) * mm});
            skLineSegment(sketch, "E2972", {"start": v(-10.6, -96.81) * mm, "end": v(-10.78, -94.55) * mm});
            skLineSegment(sketch, "E2973", {"start": v(-10.78, -94.55) * mm, "end": v(-10.93, -92.2) * mm});
            skLineSegment(sketch, "E2974", {"start": v(-10.93, -92.2) * mm, "end": v(-11.02, -89.78) * mm});
            skLineSegment(sketch, "E2975", {"start": v(-11.02, -89.78) * mm, "end": v(-11.05, -87.32) * mm});
            skLineSegment(sketch, "E2976", {"start": v(-11.05, -87.32) * mm, "end": v(-10.99, -84.85) * mm});
            skLineSegment(sketch, "E2977", {"start": v(-10.99, -84.85) * mm, "end": v(-10.84, -82.4) * mm});
            skLineSegment(sketch, "E2978", {"start": v(-10.84, -82.4) * mm, "end": v(-10.58, -79.99) * mm});
            skLineSegment(sketch, "E2979", {"start": v(-10.58, -79.99) * mm, "end": v(-10.2, -77.64) * mm});
            skLineSegment(sketch, "E2980", {"start": v(-10.2, -77.64) * mm, "end": v(-9.84, -75.95) * mm});
            skLineSegment(sketch, "E2981", {"start": v(-9.84, -75.95) * mm, "end": v(-9.7, -75.4) * mm});
            skLineSegment(sketch, "E2982", {"start": v(-9.7, -75.4) * mm, "end": v(-9.95, -75.76) * mm});
            skLineSegment(sketch, "E2983", {"start": v(-9.95, -75.76) * mm, "end": v(-10.66, -76.86) * mm});
            skLineSegment(sketch, "E2984", {"start": v(-10.66, -76.86) * mm, "end": v(-11.52, -78.36) * mm});
            skLineSegment(sketch, "E2985", {"start": v(-11.52, -78.36) * mm, "end": v(-12.3, -79.88) * mm});
            skLineSegment(sketch, "E2986", {"start": v(-12.3, -79.88) * mm, "end": v(-13, -81.4) * mm});
            skLineSegment(sketch, "E2987", {"start": v(-13, -81.4) * mm, "end": v(-13.62, -82.9) * mm});
            skLineSegment(sketch, "E2988", {"start": v(-13.62, -82.9) * mm, "end": v(-14.16, -84.37) * mm});
            skLineSegment(sketch, "E2989", {"start": v(-14.16, -84.37) * mm, "end": v(-14.63, -85.8) * mm});
            skLineSegment(sketch, "E2990", {"start": v(-14.63, -85.8) * mm, "end": v(-15.04, -87.15) * mm});
            skLineSegment(sketch, "E2991", {"start": v(-15.04, -87.15) * mm, "end": v(-15.38, -88.42) * mm});
            skLineSegment(sketch, "E2992", {"start": v(-15.38, -88.42) * mm, "end": v(-15.66, -89.59) * mm});
            skLineSegment(sketch, "E2993", {"start": v(-15.98, -96.36) * mm, "end": v(-15.82, -97.14) * mm});
            skLineSegment(sketch, "E2994", {"start": v(-15.82, -97.14) * mm, "end": v(-15.66, -97.85) * mm});
            skLineSegment(sketch, "E2995", {"start": v(-15.66, -97.85) * mm, "end": v(-15.52, -98.44) * mm});
            skLineSegment(sketch, "E2996", {"start": v(-15.52, -98.44) * mm, "end": v(-15.44, -98.75) * mm});
            skLineSegment(sketch, "E2997", {"start": v(-5.57, -117.9) * mm, "end": v(-5.4, -119.06) * mm});
            skLineSegment(sketch, "E2998", {"start": v(-5.4, -119.06) * mm, "end": v(-5.27, -119.9) * mm});
            skLineSegment(sketch, "E2999", {"start": v(-5.27, -119.9) * mm, "end": v(-5.2, -120.26) * mm});
            skLineSegment(sketch, "E3000", {"start": v(-6.37, -110.84) * mm, "end": v(-6.16, -112.9) * mm});
            skLineSegment(sketch, "E3001", {"start": v(-15.38, -98.97) * mm, "end": v(-15.26, -99.33) * mm});
            skLineSegment(sketch, "E3002", {"start": v(-5.2, -120.26) * mm, "end": v(-5.16, -120.38) * mm});
            skLineSegment(sketch, "E3003", {"start": v(-6.16, -112.9) * mm, "end": v(-5.96, -114.79) * mm});
            skLineSegment(sketch, "E3004", {"start": v(-15.26, -99.33) * mm, "end": v(-15.02, -100.09) * mm});
            skLineSegment(sketch, "E3005", {"start": v(-5.16, -120.38) * mm, "end": v(-4.9, -120.23) * mm});
            skLineSegment(sketch, "E3006", {"start": v(-5.96, -114.79) * mm, "end": v(-5.76, -116.47) * mm});
            skLineSegment(sketch, "E3007", {"start": v(-15.02, -100.09) * mm, "end": v(-14.7, -101.1) * mm});
            skLineSegment(sketch, "E3008", {"start": v(-4.9, -120.23) * mm, "end": v(-4.19, -119.7) * mm});
            skLineSegment(sketch, "E3009", {"start": v(-5.76, -116.47) * mm, "end": v(-5.57, -117.9) * mm});
            skLineSegment(sketch, "E3010", {"start": v(-14.7, -101.1) * mm, "end": v(-14.32, -102.3) * mm});
            skLineSegment(sketch, "E3011", {"start": v(-6.56, -108.64) * mm, "end": v(-6.51, -109.2) * mm});
            skLineSegment(sketch, "E3012", {"start": v(-4.19, -119.7) * mm, "end": v(-3, -118.73) * mm});
            skLineSegment(sketch, "E3013", {"start": v(-3, -118.73) * mm, "end": v(-1.66, -117.5) * mm});
            skLineSegment(sketch, "E3014", {"start": v(5.79, -108.96) * mm, "end": v(5.95, -108.73) * mm});
            skLineSegment(sketch, "E3015", {"start": v(5.95, -108.73) * mm, "end": v(6.44, -108.03) * mm});
            skLineSegment(sketch, "E3016", {"start": v(6.44, -108.03) * mm, "end": v(7.1, -107.05) * mm});
            skLineSegment(sketch, "E3017", {"start": v(7.1, -107.05) * mm, "end": v(7.71, -106.07) * mm});
            skLineSegment(sketch, "E3018", {"start": v(5.44, -109.44) * mm, "end": v(5.79, -108.96) * mm});
            skLineSegment(sketch, "E3019", {"start": v(4.37, -110.83) * mm, "end": v(5.44, -109.44) * mm});
            skLineSegment(sketch, "E3020", {"start": v(2.87, -112.67) * mm, "end": v(4.37, -110.83) * mm});
            skLineSegment(sketch, "E3021", {"start": v(1.33, -114.42) * mm, "end": v(2.87, -112.67) * mm});
            skLineSegment(sketch, "E3022", {"start": v(-0.2, -116.04) * mm, "end": v(1.33, -114.42) * mm});
            skLineSegment(sketch, "E3023", {"start": v(-1.66, -117.5) * mm, "end": v(-0.2, -116.04) * mm});
            skLineSegment(sketch, "E3024", {"start": v(-15.4, -98.86) * mm, "end": v(-15.38, -98.97) * mm});
            skLineSegment(sketch, "E3025", {"start": v(-6.51, -109.2) * mm, "end": v(-6.37, -110.84) * mm});
            skLineSegment(sketch, "E3026", {"start": v(-16.13, -95.56) * mm, "end": v(-15.98, -96.36) * mm});
            skLineSegment(sketch, "E3027", {"start": v(-15.44, -98.75) * mm, "end": v(-15.4, -98.86) * mm});
            skLineSegment(sketch, "E3028", {"start": v(-16.25, -94.8) * mm, "end": v(-16.13, -95.56) * mm});
            skLineSegment(sketch, "E3029", {"start": v(-16.33, -94.1) * mm, "end": v(-16.25, -94.8) * mm});
            skLineSegment(sketch, "E3030", {"start": v(-16.36, -93.7) * mm, "end": v(-16.33, -94.1) * mm});
            skLineSegment(sketch, "E3031", {"start": v(-16.36, -93.56) * mm, "end": v(-16.36, -93.7) * mm});
            skLineSegment(sketch, "E3032", {"start": v(-16.36, -93.5) * mm, "end": v(-16.36, -93.56) * mm});
            skLineSegment(sketch, "E3033", {"start": v(-16.34, -93.35) * mm, "end": v(-16.36, -93.5) * mm});
            skLineSegment(sketch, "E3034", {"start": v(-16.3, -92.93) * mm, "end": v(-16.34, -93.35) * mm});
            skLineSegment(sketch, "E3035", {"start": v(-16.2, -92.33) * mm, "end": v(-16.3, -92.93) * mm});
            skLineSegment(sketch, "E3036", {"start": v(-16.07, -91.56) * mm, "end": v(-16.2, -92.33) * mm});
            skLineSegment(sketch, "E3037", {"start": v(-15.9, -90.64) * mm, "end": v(-16.07, -91.56) * mm});
            skLineSegment(sketch, "E3038", {"start": v(-15.66, -89.59) * mm, "end": v(-15.9, -90.64) * mm});
            skLineSegment(sketch, "E3039", {"start": v(-5.6, -76.74) * mm, "end": v(-6.21, -76.29) * mm});
            skLineSegment(sketch, "E3040", {"start": v(-4.88, -77.54) * mm, "end": v(-5.6, -76.74) * mm});
            skLineSegment(sketch, "E3041", {"start": v(-4.4, -78.52) * mm, "end": v(-4.88, -77.54) * mm});
            skLineSegment(sketch, "E3042", {"start": v(-4.24, -79.37) * mm, "end": v(-4.4, -78.52) * mm});
            skLineSegment(sketch, "E3043", {"start": v(-4.26, -79.64) * mm, "end": v(-4.24, -79.37) * mm});
            skLineSegment(sketch, "E3044", {"start": v(-4.28, -80.04) * mm, "end": v(-4.26, -79.64) * mm});
            skLineSegment(sketch, "E3045", {"start": v(-4.33, -81.23) * mm, "end": v(-4.28, -80.04) * mm});
            skLineSegment(sketch, "E3046", {"start": v(-4.39, -83.06) * mm, "end": v(-4.33, -81.23) * mm});
            skLineSegment(sketch, "E3047", {"start": v(-2.46, -108.27) * mm, "end": v(-2.38, -109.58) * mm});
            skLineSegment(sketch, "E3048", {"start": v(-2.55, -106.68) * mm, "end": v(-2.46, -108.27) * mm});
            skLineSegment(sketch, "E3049", {"start": v(-2.65, -104.84) * mm, "end": v(-2.55, -106.68) * mm});
            skLineSegment(sketch, "E3050", {"start": v(-2.75, -102.79) * mm, "end": v(-2.65, -104.84) * mm});
            skLineSegment(sketch, "E3051", {"start": v(-2.84, -100.56) * mm, "end": v(-2.75, -102.79) * mm});
            skLineSegment(sketch, "E3052", {"start": v(-2.93, -98.2) * mm, "end": v(-2.84, -100.56) * mm});
            skLineSegment(sketch, "E3053", {"start": v(-3, -95.73) * mm, "end": v(-2.93, -98.2) * mm});
            skLineSegment(sketch, "E3054", {"start": v(-3.06, -93.2) * mm, "end": v(-3, -95.73) * mm});
            skLineSegment(sketch, "E3055", {"start": v(-3.1, -90.65) * mm, "end": v(-3.06, -93.2) * mm});
            skLineSegment(sketch, "E3056", {"start": v(-3.11, -88.12) * mm, "end": v(-3.1, -90.65) * mm});
            skLineSegment(sketch, "E3057", {"start": v(-3.1, -85.63) * mm, "end": v(-3.11, -88.12) * mm});
            skLineSegment(sketch, "E3058", {"start": v(-3.03, -83.24) * mm, "end": v(-3.1, -85.63) * mm});
            skLineSegment(sketch, "E3059", {"start": v(-2.97, -81.54) * mm, "end": v(-3.03, -83.24) * mm});
            skLineSegment(sketch, "E3060", {"start": v(-2.93, -80.98) * mm, "end": v(-2.97, -81.54) * mm});
            skLineSegment(sketch, "E3061", {"start": v(-2.83, -81.06) * mm, "end": v(-2.93, -80.98) * mm});
            skLineSegment(sketch, "E3062", {"start": v(-2.52, -81.33) * mm, "end": v(-2.83, -81.06) * mm});
            skLineSegment(sketch, "E3063", {"start": v(-1.96, -81.88) * mm, "end": v(-2.52, -81.33) * mm});
            skLineSegment(sketch, "E3064", {"start": v(-1.27, -82.6) * mm, "end": v(-1.96, -81.88) * mm});
            skLineSegment(sketch, "E3065", {"start": v(-0.48, -83.47) * mm, "end": v(-1.27, -82.6) * mm});
            skLineSegment(sketch, "E3066", {"start": v(0.39, -84.47) * mm, "end": v(-0.48, -83.47) * mm});
            skLineSegment(sketch, "E3067", {"start": v(1.32, -85.58) * mm, "end": v(0.39, -84.47) * mm});
            skLineSegment(sketch, "E3068", {"start": v(2.28, -86.78) * mm, "end": v(1.32, -85.58) * mm});
            skLineSegment(sketch, "E3069", {"start": v(3, -87.71) * mm, "end": v(2.28, -86.78) * mm});
            skLineSegment(sketch, "E3070", {"start": v(3.25, -88.03) * mm, "end": v(3, -87.71) * mm});
            skLineSegment(sketch, "E3071", {"start": v(9.66, -101.7) * mm, "end": v(9.63, -100.99) * mm});
            skLineSegment(sketch, "E3072", {"start": v(9.64, -102.2) * mm, "end": v(9.66, -101.7) * mm});
            skLineSegment(sketch, "E3073", {"start": v(9.61, -102.43) * mm, "end": v(9.64, -102.2) * mm});
            skLineSegment(sketch, "E3074", {"start": v(9.6, -102.5) * mm, "end": v(9.61, -102.43) * mm});
            skLineSegment(sketch, "E3075", {"start": v(9.57, -102.6) * mm, "end": v(9.6, -102.5) * mm});
            skLineSegment(sketch, "E3076", {"start": v(9.46, -102.9) * mm, "end": v(9.57, -102.6) * mm});
            skLineSegment(sketch, "E3077", {"start": v(7.71, -106.07) * mm, "end": v(8.28, -105.12) * mm});
            skLineSegment(sketch, "E3078", {"start": v(8.28, -105.12) * mm, "end": v(8.78, -104.25) * mm});
            skLineSegment(sketch, "E3079", {"start": v(8.78, -104.25) * mm, "end": v(9.17, -103.5) * mm});
            skLineSegment(sketch, "E3080", {"start": v(9.17, -103.5) * mm, "end": v(9.46, -102.9) * mm});
            skLineSegment(sketch, "E3081", {"start": v(9.63, -100.99) * mm, "end": v(9.5, -100.08) * mm});
            skLineSegment(sketch, "E3082", {"start": v(9.5, -100.08) * mm, "end": v(9.26, -98.96) * mm});
            skLineSegment(sketch, "E3083", {"start": v(9.26, -98.96) * mm, "end": v(8.84, -97.66) * mm});
            skLineSegment(sketch, "E3084", {"start": v(8.84, -97.66) * mm, "end": v(8.23, -96.17) * mm});
            skLineSegment(sketch, "E3085", {"start": v(8.23, -96.17) * mm, "end": v(7.6, -94.91) * mm});
            skLineSegment(sketch, "E3086", {"start": v(7.6, -94.91) * mm, "end": v(7.38, -94.5) * mm});
            skLineSegment(sketch, "E3087", {"start": v(7.38, -94.5) * mm, "end": v(7.16, -94.1) * mm});
            skLineSegment(sketch, "E3088", {"start": v(7.16, -94.1) * mm, "end": v(6.48, -92.94) * mm});
            skLineSegment(sketch, "E3089", {"start": v(6.48, -92.94) * mm, "end": v(5.49, -91.3) * mm});
            skLineSegment(sketch, "E3090", {"start": v(5.49, -91.3) * mm, "end": v(4.4, -89.64) * mm});
            skLineSegment(sketch, "E3091", {"start": v(4.4, -89.64) * mm, "end": v(3.55, -88.43) * mm});
            skLineSegment(sketch, "E3092", {"start": v(3.55, -88.43) * mm, "end": v(3.25, -88.03) * mm});
            skLineSegment(sketch, "E3093", {"start": v(-2.38, -109.58) * mm, "end": v(-2.32, -110.56) * mm});
            skLineSegment(sketch, "E3094", {"start": v(-2.32, -110.56) * mm, "end": v(-2.28, -111.17) * mm});
            skLineSegment(sketch, "E3095", {"start": v(-2.28, -111.17) * mm, "end": v(-2.27, -111.38) * mm});
            skLineSegment(sketch, "E3096", {"start": v(-2.27, -111.38) * mm, "end": v(-0.66, -91.53) * mm});
            skLineSegment(sketch, "E3097", {"start": v(-0.66, -91.53) * mm, "end": v(-0.55, -91.65) * mm});
            skLineSegment(sketch, "E3098", {"start": v(-0.55, -91.65) * mm, "end": v(-0.25, -91.98) * mm});
            skLineSegment(sketch, "E3099", {"start": v(-0.25, -91.98) * mm, "end": v(0.2, -92.5) * mm});
            skLineSegment(sketch, "E3100", {"start": v(0.2, -92.5) * mm, "end": v(0.76, -93.2) * mm});
            skLineSegment(sketch, "E3101", {"start": v(0.76, -93.2) * mm, "end": v(1.4, -94.02) * mm});
            skLineSegment(sketch, "E3102", {"start": v(1.4, -94.02) * mm, "end": v(2.08, -94.95) * mm});
            skLineSegment(sketch, "E3103", {"start": v(2.08, -94.95) * mm, "end": v(2.76, -95.96) * mm});
            skLineSegment(sketch, "E3104", {"start": v(2.76, -95.96) * mm, "end": v(3.25, -96.75) * mm});
            skLineSegment(sketch, "E3105", {"start": v(3.25, -96.75) * mm, "end": v(3.4, -97.02) * mm});
            skLineSegment(sketch, "E3106", {"start": v(3.4, -97.02) * mm, "end": v(3.62, -97.4) * mm});
            skLineSegment(sketch, "E3107", {"start": v(3.62, -97.4) * mm, "end": v(4.19, -98.58) * mm});
            skLineSegment(sketch, "E3108", {"start": v(4.19, -98.58) * mm, "end": v(4.71, -100) * mm});
            skLineSegment(sketch, "E3109", {"start": v(4.71, -100) * mm, "end": v(5, -101.29) * mm});
            skLineSegment(sketch, "E3110", {"start": v(5, -101.29) * mm, "end": v(5.08, -102.13) * mm});
            skLineSegment(sketch, "E3111", {"start": v(5.08, -102.13) * mm, "end": v(5.08, -102.4) * mm});
            skLineSegment(sketch, "E3112", {"start": v(5.08, -102.4) * mm, "end": v(5.07, -102.61) * mm});
            skLineSegment(sketch, "E3113", {"start": v(5.07, -102.61) * mm, "end": v(5.02, -103.22) * mm});
            skLineSegment(sketch, "E3114", {"start": v(5.02, -103.22) * mm, "end": v(4.83, -104.22) * mm});
            skLineSegment(sketch, "E3115", {"start": v(4.83, -104.22) * mm, "end": v(4.4, -105.4) * mm});
            skLineSegment(sketch, "E3116", {"start": v(4.4, -105.4) * mm, "end": v(3.87, -106.46) * mm});
            skLineSegment(sketch, "E3117", {"start": v(3.87, -106.46) * mm, "end": v(3.67, -106.8) * mm});
            skLineSegment(sketch, "E3118", {"start": v(3.67, -106.8) * mm, "end": v(3.43, -107.2) * mm});
            skLineSegment(sketch, "E3119", {"start": v(3.43, -107.2) * mm, "end": v(2.66, -108.37) * mm});
            skLineSegment(sketch, "E3120", {"start": v(2.66, -108.37) * mm, "end": v(1.62, -109.83) * mm});
            skLineSegment(sketch, "E3121", {"start": v(1.62, -109.83) * mm, "end": v(0.6, -111.14) * mm});
            skLineSegment(sketch, "E3122", {"start": v(0.6, -111.14) * mm, "end": v(-0.37, -112.3) * mm});
            skLineSegment(sketch, "E3123", {"start": v(-0.37, -112.3) * mm, "end": v(-1.26, -113.3) * mm});
            skLineSegment(sketch, "E3124", {"start": v(-1.26, -113.3) * mm, "end": v(-2.04, -114.1) * mm});
            skLineSegment(sketch, "E3125", {"start": v(-2.04, -114.1) * mm, "end": v(-2.66, -114.71) * mm});
            skLineSegment(sketch, "E3126", {"start": v(-2.66, -114.71) * mm, "end": v(-2.99, -115) * mm});
            skLineSegment(sketch, "E3127", {"start": v(-2.99, -115) * mm, "end": v(-3.1, -115.1) * mm});
            skLineSegment(sketch, "E3128", {"start": v(-3.1, -115.1) * mm, "end": v(-3.17, -114.69) * mm});
            skLineSegment(sketch, "E3129", {"start": v(-3.17, -114.69) * mm, "end": v(-3.34, -113.44) * mm});
            skLineSegment(sketch, "E3130", {"start": v(-3.34, -113.44) * mm, "end": v(-3.56, -111.55) * mm});
            skLineSegment(sketch, "E3131", {"start": v(-3.56, -111.55) * mm, "end": v(-3.76, -109.45) * mm});
            skLineSegment(sketch, "E3132", {"start": v(-3.76, -109.45) * mm, "end": v(-3.92, -107.2) * mm});
            skLineSegment(sketch, "E3133", {"start": v(-3.92, -107.2) * mm, "end": v(-4.07, -104.81) * mm});
            skLineSegment(sketch, "E3134", {"start": v(-4.07, -104.81) * mm, "end": v(-4.19, -102.33) * mm});
            skLineSegment(sketch, "E3135", {"start": v(-4.19, -102.33) * mm, "end": v(-4.28, -99.79) * mm});
            skLineSegment(sketch, "E3136", {"start": v(-4.28, -99.79) * mm, "end": v(-4.36, -97.21) * mm});
            skLineSegment(sketch, "E3137", {"start": v(-4.36, -97.21) * mm, "end": v(-4.41, -94.65) * mm});
            skLineSegment(sketch, "E3138", {"start": v(-4.41, -94.65) * mm, "end": v(-4.44, -92.12) * mm});
            skLineSegment(sketch, "E3139", {"start": v(-4.44, -92.12) * mm, "end": v(-4.46, -89.66) * mm});
            skLineSegment(sketch, "E3140", {"start": v(-4.46, -89.66) * mm, "end": v(-4.45, -87.3) * mm});
            skLineSegment(sketch, "E3141", {"start": v(71.55, -2.79) * mm, "end": v(71.27, -3.04) * mm});
            skLineSegment(sketch, "E3142", {"start": v(72.43, -2.07) * mm, "end": v(71.55, -2.79) * mm});
            skLineSegment(sketch, "E3143", {"start": v(73.52, -1.27) * mm, "end": v(72.43, -2.07) * mm});
            skLineSegment(sketch, "E3144", {"start": v(74.41, -0.7) * mm, "end": v(73.52, -1.27) * mm});
            skLineSegment(sketch, "E3145", {"start": v(74.88, -0.46) * mm, "end": v(74.41, -0.7) * mm});
            skLineSegment(sketch, "E3146", {"start": v(75.03, -0.42) * mm, "end": v(74.88, -0.46) * mm});
            skLineSegment(sketch, "E3147", {"start": v(75.15, -0.39) * mm, "end": v(75.03, -0.42) * mm});
            skLineSegment(sketch, "E3148", {"start": v(75.51, -0.32) * mm, "end": v(75.15, -0.39) * mm});
            skLineSegment(sketch, "E3149", {"start": v(76.23, -0.23) * mm, "end": v(75.51, -0.32) * mm});
            skLineSegment(sketch, "E3150", {"start": v(77.13, -0.18) * mm, "end": v(76.23, -0.23) * mm});
            skLineSegment(sketch, "E3151", {"start": v(77.94, -0.17) * mm, "end": v(77.13, -0.18) * mm});
            skLineSegment(sketch, "E3152", {"start": v(78.2, -0.18) * mm, "end": v(77.94, -0.17) * mm});
            skLineSegment(sketch, "E3153", {"start": v(78.42, -0.19) * mm, "end": v(78.2, -0.18) * mm});
            skLineSegment(sketch, "E3154", {"start": v(79.09, -0.22) * mm, "end": v(78.42, -0.19) * mm});
            skLineSegment(sketch, "E3155", {"start": v(79.98, -0.27) * mm, "end": v(79.09, -0.22) * mm});
            skLineSegment(sketch, "E3156", {"start": v(80.84, -0.34) * mm, "end": v(79.98, -0.27) * mm});
            skLineSegment(sketch, "E3157", {"start": v(81.63, -0.4) * mm, "end": v(80.84, -0.34) * mm});
            skLineSegment(sketch, "E3158", {"start": v(82.32, -0.47) * mm, "end": v(81.63, -0.4) * mm});
            skLineSegment(sketch, "E3159", {"start": v(82.85, -0.53) * mm, "end": v(82.32, -0.47) * mm});
            skLineSegment(sketch, "E3160", {"start": v(83.2, -0.57) * mm, "end": v(82.85, -0.53) * mm});
            skLineSegment(sketch, "E3161", {"start": v(83.33, -0.58) * mm, "end": v(83.2, -0.57) * mm});
            skLineSegment(sketch, "E3162", {"start": v(83.12, -0.65) * mm, "end": v(83.33, -0.58) * mm});
            skLineSegment(sketch, "E3163", {"start": v(82.55, -0.84) * mm, "end": v(83.12, -0.65) * mm});
            skLineSegment(sketch, "E3164", {"start": v(81.68, -1.13) * mm, "end": v(82.55, -0.84) * mm});
            skLineSegment(sketch, "E3165", {"start": v(80.56, -1.5) * mm, "end": v(81.68, -1.13) * mm});
            skLineSegment(sketch, "E3166", {"start": v(79.27, -1.94) * mm, "end": v(80.56, -1.5) * mm});
            skLineSegment(sketch, "E3167", {"start": v(77.87, -2.42) * mm, "end": v(79.27, -1.94) * mm});
            skLineSegment(sketch, "E3168", {"start": v(76.41, -2.94) * mm, "end": v(77.87, -2.42) * mm});
            skLineSegment(sketch, "E3169", {"start": v(75.33, -3.33) * mm, "end": v(76.41, -2.94) * mm});
            skLineSegment(sketch, "E3170", {"start": v(74.97, -3.46) * mm, "end": v(75.33, -3.33) * mm});
            skLineSegment(sketch, "E3171", {"start": v(74.62, -3.6) * mm, "end": v(74.97, -3.46) * mm});
            skLineSegment(sketch, "E3172", {"start": v(73.55, -4) * mm, "end": v(74.62, -3.6) * mm});
            skLineSegment(sketch, "E3173", {"start": v(72.24, -4.51) * mm, "end": v(73.55, -4) * mm});
            skLineSegment(sketch, "E3174", {"start": v(71.05, -5) * mm, "end": v(72.24, -4.51) * mm});
            skLineSegment(sketch, "E3175", {"start": v(70.02, -5.42) * mm, "end": v(71.05, -5) * mm});
            skLineSegment(sketch, "E3176", {"start": v(69.17, -5.77) * mm, "end": v(70.02, -5.42) * mm});
            skLineSegment(sketch, "E3177", {"start": v(68.54, -6.05) * mm, "end": v(69.17, -5.77) * mm});
            skLineSegment(sketch, "E3178", {"start": v(68.13, -6.22) * mm, "end": v(68.54, -6.05) * mm});
            skLineSegment(sketch, "E3179", {"start": v(68, -6.28) * mm, "end": v(68.13, -6.22) * mm});
            skLineSegment(sketch, "E3180", {"start": v(68.06, -6.2) * mm, "end": v(68, -6.28) * mm});
            skLineSegment(sketch, "E3181", {"start": v(68.27, -5.98) * mm, "end": v(68.06, -6.2) * mm});
            skLineSegment(sketch, "E3182", {"start": v(68.6, -5.64) * mm, "end": v(68.27, -5.98) * mm});
            skLineSegment(sketch, "E3183", {"start": v(69, -5.2) * mm, "end": v(68.6, -5.64) * mm});
            skLineSegment(sketch, "E3184", {"start": v(69.5, -4.7) * mm, "end": v(69, -5.2) * mm});
            skLineSegment(sketch, "E3185", {"start": v(70.06, -4.16) * mm, "end": v(69.5, -4.7) * mm});
            skLineSegment(sketch, "E3186", {"start": v(70.65, -3.6) * mm, "end": v(70.06, -4.16) * mm});
            skLineSegment(sketch, "E3187", {"start": v(71.1, -3.18) * mm, "end": v(70.65, -3.6) * mm});
            skLineSegment(sketch, "E3188", {"start": v(71.27, -3.04) * mm, "end": v(71.1, -3.18) * mm});
            skLineSegment(sketch, "E3189", {"start": v(70.74, -22.98) * mm, "end": v(70.94, -23.57) * mm});
            skLineSegment(sketch, "E3190", {"start": v(70.17, -21.2) * mm, "end": v(70.74, -22.98) * mm});
            skLineSegment(sketch, "E3191", {"start": v(69.46, -18.94) * mm, "end": v(70.17, -21.2) * mm});
            skLineSegment(sketch, "E3192", {"start": v(68.77, -16.84) * mm, "end": v(69.46, -18.94) * mm});
            skLineSegment(sketch, "E3193", {"start": v(68.1, -14.94) * mm, "end": v(68.77, -16.84) * mm});
            skLineSegment(sketch, "E3194", {"start": v(67.45, -13.3) * mm, "end": v(68.1, -14.94) * mm});
            skLineSegment(sketch, "E3195", {"start": v(66.78, -12) * mm, "end": v(67.45, -13.3) * mm});
            skLineSegment(sketch, "E3196", {"start": v(66.1, -11.04) * mm, "end": v(66.78, -12) * mm});
            skLineSegment(sketch, "E3197", {"start": v(65.56, -10.59) * mm, "end": v(66.1, -11.04) * mm});
            skLineSegment(sketch, "E3198", {"start": v(65.36, -10.5) * mm, "end": v(65.56, -10.59) * mm});
            skLineSegment(sketch, "E3199", {"start": v(65.25, -10.46) * mm, "end": v(65.36, -10.5) * mm});
            skLineSegment(sketch, "E3200", {"start": v(64.87, -10.46) * mm, "end": v(65.25, -10.46) * mm});
            skLineSegment(sketch, "E3201", {"start": v(64.08, -10.56) * mm, "end": v(64.87, -10.46) * mm});
            skLineSegment(sketch, "E3202", {"start": v(63.07, -10.78) * mm, "end": v(64.08, -10.56) * mm});
            skLineSegment(sketch, "E3203", {"start": v(61.93, -11.1) * mm, "end": v(63.07, -10.78) * mm});
            skLineSegment(sketch, "E3204", {"start": v(60.72, -11.48) * mm, "end": v(61.93, -11.1) * mm});
            skLineSegment(sketch, "E3205", {"start": v(59.52, -11.9) * mm, "end": v(60.72, -11.48) * mm});
            skLineSegment(sketch, "E3206", {"start": v(58.4, -12.33) * mm, "end": v(59.52, -11.9) * mm});
            skLineSegment(sketch, "E3207", {"start": v(57.7, -12.63) * mm, "end": v(58.4, -12.33) * mm});
            skLineSegment(sketch, "E3208", {"start": v(57.46, -12.74) * mm, "end": v(57.7, -12.63) * mm});
            skLineSegment(sketch, "E3209", {"start": v(57.78, -12.39) * mm, "end": v(57.46, -12.74) * mm});
            skLineSegment(sketch, "E3210", {"start": v(58.86, -11.42) * mm, "end": v(57.78, -12.39) * mm});
            skLineSegment(sketch, "E3211", {"start": v(60.55, -10.17) * mm, "end": v(58.86, -11.42) * mm});
            skLineSegment(sketch, "E3212", {"start": v(62.41, -9.08) * mm, "end": v(60.55, -10.17) * mm});
            skLineSegment(sketch, "E3213", {"start": v(63.84, -8.42) * mm, "end": v(62.41, -9.08) * mm});
            skLineSegment(sketch, "E3214", {"start": v(64.33, -8.24) * mm, "end": v(63.84, -8.42) * mm});
            skLineSegment(sketch, "E3215", {"start": v(64.8, -8.07) * mm, "end": v(64.33, -8.24) * mm});
            skLineSegment(sketch, "E3216", {"start": v(66.21, -7.66) * mm, "end": v(64.8, -8.07) * mm});
            skLineSegment(sketch, "E3217", {"start": v(68.14, -7.22) * mm, "end": v(66.21, -7.66) * mm});
            skLineSegment(sketch, "E3218", {"start": v(70, -6.9) * mm, "end": v(68.14, -7.22) * mm});
            skLineSegment(sketch, "E3219", {"start": v(71.23, -6.71) * mm, "end": v(70, -6.9) * mm});
            skLineSegment(sketch, "E3220", {"start": v(71.65, -6.66) * mm, "end": v(71.23, -6.71) * mm});
            skLineSegment(sketch, "E3221", {"start": v(72.1, -6.6) * mm, "end": v(71.65, -6.66) * mm});
            skLineSegment(sketch, "E3222", {"start": v(73.43, -6.43) * mm, "end": v(72.1, -6.6) * mm});
            skLineSegment(sketch, "E3223", {"start": v(74.8, -6.24) * mm, "end": v(73.43, -6.43) * mm});
            skLineSegment(sketch, "E3224", {"start": v(75.74, -6) * mm, "end": v(74.8, -6.24) * mm});
            skLineSegment(sketch, "E3225", {"start": v(76.2, -5.76) * mm, "end": v(75.74, -6) * mm});
            skLineSegment(sketch, "E3226", {"start": v(76.3, -5.64) * mm, "end": v(76.2, -5.76) * mm});
            skLineSegment(sketch, "E3227", {"start": v(76.2, -5.87) * mm, "end": v(76.3, -5.64) * mm});
            skLineSegment(sketch, "E3228", {"start": v(75.77, -6.49) * mm, "end": v(76.2, -5.87) * mm});
            skLineSegment(sketch, "E3229", {"start": v(74.94, -7.4) * mm, "end": v(75.77, -6.49) * mm});
            skLineSegment(sketch, "E3230", {"start": v(73.93, -8.36) * mm, "end": v(74.94, -7.4) * mm});
            skLineSegment(sketch, "E3231", {"start": v(72.84, -9.31) * mm, "end": v(73.93, -8.36) * mm});
            skLineSegment(sketch, "E3232", {"start": v(71.81, -10.23) * mm, "end": v(72.84, -9.31) * mm});
            skLineSegment(sketch, "E3233", {"start": v(70.94, -11.07) * mm, "end": v(71.81, -10.23) * mm});
            skLineSegment(sketch, "E3234", {"start": v(70.36, -11.8) * mm, "end": v(70.94, -11.07) * mm});
            skLineSegment(sketch, "E3235", {"start": v(70.16, -12.26) * mm, "end": v(70.36, -11.8) * mm});
            skLineSegment(sketch, "E3236", {"start": v(70.17, -12.4) * mm, "end": v(70.16, -12.26) * mm});
            skLineSegment(sketch, "E3237", {"start": v(70.23, -12.6) * mm, "end": v(70.17, -12.4) * mm});
            skLineSegment(sketch, "E3238", {"start": v(70.43, -13.23) * mm, "end": v(70.23, -12.6) * mm});
            skLineSegment(sketch, "E3239", {"start": v(70.78, -14.23) * mm, "end": v(70.43, -13.23) * mm});
            skLineSegment(sketch, "E3240", {"start": v(71.22, -15.38) * mm, "end": v(70.78, -14.23) * mm});
            skLineSegment(sketch, "E3241", {"start": v(71.72, -16.65) * mm, "end": v(71.22, -15.38) * mm});
            skLineSegment(sketch, "E3242", {"start": v(72.28, -18) * mm, "end": v(71.72, -16.65) * mm});
            skLineSegment(sketch, "E3243", {"start": v(72.88, -19.43) * mm, "end": v(72.28, -18) * mm});
            skLineSegment(sketch, "E3244", {"start": v(73.52, -20.88) * mm, "end": v(72.88, -19.43) * mm});
            skLineSegment(sketch, "E3245", {"start": v(74, -21.98) * mm, "end": v(73.52, -20.88) * mm});
            skLineSegment(sketch, "E3246", {"start": v(74.17, -22.35) * mm, "end": v(74, -21.98) * mm});
            skLineSegment(sketch, "E3247", {"start": v(74.35, -22.75) * mm, "end": v(74.17, -22.35) * mm});
            skLineSegment(sketch, "E3248", {"start": v(74.9, -23.94) * mm, "end": v(74.35, -22.75) * mm});
            skLineSegment(sketch, "E3249", {"start": v(75.6, -25.47) * mm, "end": v(74.9, -23.94) * mm});
            skLineSegment(sketch, "E3250", {"start": v(76.27, -26.9) * mm, "end": v(75.6, -25.47) * mm});
            skLineSegment(sketch, "E3251", {"start": v(76.88, -28.21) * mm, "end": v(76.27, -26.9) * mm});
            skLineSegment(sketch, "E3252", {"start": v(69.4, -46.6) * mm, "end": v(69.64, -48.62) * mm});
            skLineSegment(sketch, "E3253", {"start": v(69.13, -44.4) * mm, "end": v(69.4, -46.6) * mm});
            skLineSegment(sketch, "E3254", {"start": v(72.36, -55.08) * mm, "end": v(72.6, -55.16) * mm});
            skLineSegment(sketch, "E3255", {"start": v(72.6, -55.16) * mm, "end": v(72.6, -55.06) * mm});
            skLineSegment(sketch, "E3256", {"start": v(72.6, -55.06) * mm, "end": v(72.6, -54.76) * mm});
            skLineSegment(sketch, "E3257", {"start": v(72.6, -54.76) * mm, "end": v(72.58, -54.12) * mm});
            skLineSegment(sketch, "E3258", {"start": v(72.58, -54.12) * mm, "end": v(72.55, -53.27) * mm});
            skLineSegment(sketch, "E3259", {"start": v(72.55, -53.27) * mm, "end": v(72.49, -52.22) * mm});
            skLineSegment(sketch, "E3260", {"start": v(72.49, -52.22) * mm, "end": v(72.41, -50.99) * mm});
            skLineSegment(sketch, "E3261", {"start": v(72.41, -50.99) * mm, "end": v(72.3, -49.6) * mm});
            skLineSegment(sketch, "E3262", {"start": v(72.3, -49.6) * mm, "end": v(72.18, -48.07) * mm});
            skLineSegment(sketch, "E3263", {"start": v(72.18, -48.07) * mm, "end": v(72.07, -46.83) * mm});
            skLineSegment(sketch, "E3264", {"start": v(72.07, -46.83) * mm, "end": v(72.03, -46.41) * mm});
            skLineSegment(sketch, "E3265", {"start": v(72.03, -46.41) * mm, "end": v(71.96, -45.67) * mm});
            skLineSegment(sketch, "E3266", {"start": v(71.96, -45.67) * mm, "end": v(71.72, -43.43) * mm});
            skLineSegment(sketch, "E3267", {"start": v(71.72, -43.43) * mm, "end": v(71.33, -40.23) * mm});
            skLineSegment(sketch, "E3268", {"start": v(71.33, -40.23) * mm, "end": v(70.87, -36.87) * mm});
            skLineSegment(sketch, "E3269", {"start": v(70.87, -36.87) * mm, "end": v(70.48, -34.28) * mm});
            skLineSegment(sketch, "E3270", {"start": v(70.48, -34.28) * mm, "end": v(70.34, -33.42) * mm});
            skLineSegment(sketch, "E3271", {"start": v(70.34, -33.42) * mm, "end": v(70.18, -32.5) * mm});
            skLineSegment(sketch, "E3272", {"start": v(70.18, -32.5) * mm, "end": v(69.38, -28.04) * mm});
            skLineSegment(sketch, "E3273", {"start": v(69.38, -28.04) * mm, "end": v(68.52, -23.8) * mm});
            skLineSegment(sketch, "E3274", {"start": v(68.52, -23.8) * mm, "end": v(68.34, -22.98) * mm});
            skLineSegment(sketch, "E3275", {"start": v(70.94, -23.57) * mm, "end": v(71, -23.77) * mm});
            skLineSegment(sketch, "E3276", {"start": v(71, -23.77) * mm, "end": v(71.2, -24.38) * mm});
            skLineSegment(sketch, "E3277", {"start": v(71.2, -24.38) * mm, "end": v(71.55, -25.47) * mm});
            skLineSegment(sketch, "E3278", {"start": v(71.55, -25.47) * mm, "end": v(71.96, -26.8) * mm});
            skLineSegment(sketch, "E3279", {"start": v(71.96, -26.8) * mm, "end": v(72.42, -28.37) * mm});
            skLineSegment(sketch, "E3280", {"start": v(72.42, -28.37) * mm, "end": v(72.91, -30.13) * mm});
            skLineSegment(sketch, "E3281", {"start": v(72.91, -30.13) * mm, "end": v(73.42, -32.07) * mm});
            skLineSegment(sketch, "E3282", {"start": v(73.42, -32.07) * mm, "end": v(73.93, -34.15) * mm});
            skLineSegment(sketch, "E3283", {"start": v(73.93, -34.15) * mm, "end": v(74.43, -36.37) * mm});
            skLineSegment(sketch, "E3284", {"start": v(74.43, -36.37) * mm, "end": v(74.9, -38.68) * mm});
            skLineSegment(sketch, "E3285", {"start": v(74.9, -38.68) * mm, "end": v(75.3, -41.06) * mm});
            skLineSegment(sketch, "E3286", {"start": v(75.3, -41.06) * mm, "end": v(75.66, -43.5) * mm});
            skLineSegment(sketch, "E3287", {"start": v(75.66, -43.5) * mm, "end": v(75.94, -45.95) * mm});
            skLineSegment(sketch, "E3288", {"start": v(75.94, -45.95) * mm, "end": v(76.12, -48.4) * mm});
            skLineSegment(sketch, "E3289", {"start": v(76.12, -48.4) * mm, "end": v(76.19, -50.83) * mm});
            skLineSegment(sketch, "E3290", {"start": v(76.19, -50.83) * mm, "end": v(76.13, -53.2) * mm});
            skLineSegment(sketch, "E3291", {"start": v(76.13, -53.2) * mm, "end": v(76, -54.92) * mm});
            skLineSegment(sketch, "E3292", {"start": v(76, -54.92) * mm, "end": v(75.93, -55.5) * mm});
            skLineSegment(sketch, "E3293", {"start": v(75.93, -55.5) * mm, "end": v(76.13, -55.1) * mm});
            skLineSegment(sketch, "E3294", {"start": v(76.13, -55.1) * mm, "end": v(76.68, -53.91) * mm});
            skLineSegment(sketch, "E3295", {"start": v(76.68, -53.91) * mm, "end": v(77.34, -52.3) * mm});
            skLineSegment(sketch, "E3296", {"start": v(77.34, -52.3) * mm, "end": v(77.9, -50.7) * mm});
            skLineSegment(sketch, "E3297", {"start": v(77.9, -50.7) * mm, "end": v(78.4, -49.1) * mm});
            skLineSegment(sketch, "E3298", {"start": v(78.4, -49.1) * mm, "end": v(78.8, -47.53) * mm});
            skLineSegment(sketch, "E3299", {"start": v(78.8, -47.53) * mm, "end": v(79.14, -46) * mm});
            skLineSegment(sketch, "E3300", {"start": v(79.14, -46) * mm, "end": v(79.42, -44.53) * mm});
            skLineSegment(sketch, "E3301", {"start": v(79.42, -44.53) * mm, "end": v(79.64, -43.13) * mm});
            skLineSegment(sketch, "E3302", {"start": v(79.64, -43.13) * mm, "end": v(79.8, -41.82) * mm});
            skLineSegment(sketch, "E3303", {"start": v(79.8, -41.82) * mm, "end": v(79.93, -40.63) * mm});
            skLineSegment(sketch, "E3304", {"start": v(79.33, -33.87) * mm, "end": v(79.07, -33.12) * mm});
            skLineSegment(sketch, "E3305", {"start": v(79.07, -33.12) * mm, "end": v(78.81, -32.44) * mm});
            skLineSegment(sketch, "E3306", {"start": v(78.81, -32.44) * mm, "end": v(78.6, -31.87) * mm});
            skLineSegment(sketch, "E3307", {"start": v(78.6, -31.87) * mm, "end": v(78.47, -31.58) * mm});
            skLineSegment(sketch, "E3308", {"start": v(66.11, -13.93) * mm, "end": v(65.8, -12.8) * mm});
            skLineSegment(sketch, "E3309", {"start": v(65.8, -12.8) * mm, "end": v(65.54, -12) * mm});
            skLineSegment(sketch, "E3310", {"start": v(65.54, -12) * mm, "end": v(65.43, -11.65) * mm});
            skLineSegment(sketch, "E3311", {"start": v(67.85, -20.83) * mm, "end": v(67.37, -18.81) * mm});
            skLineSegment(sketch, "E3312", {"start": v(78.38, -31.37) * mm, "end": v(78.22, -31.03) * mm});
            skLineSegment(sketch, "E3313", {"start": v(65.43, -11.65) * mm, "end": v(65.38, -11.54) * mm});
            skLineSegment(sketch, "E3314", {"start": v(67.37, -18.81) * mm, "end": v(66.92, -16.97) * mm});
            skLineSegment(sketch, "E3315", {"start": v(78.22, -31.03) * mm, "end": v(77.88, -30.31) * mm});
            skLineSegment(sketch, "E3316", {"start": v(65.38, -11.54) * mm, "end": v(65.14, -11.72) * mm});
            skLineSegment(sketch, "E3317", {"start": v(66.92, -16.97) * mm, "end": v(66.5, -15.33) * mm});
            skLineSegment(sketch, "E3318", {"start": v(77.88, -30.31) * mm, "end": v(77.43, -29.36) * mm});
            skLineSegment(sketch, "E3319", {"start": v(65.14, -11.72) * mm, "end": v(64.5, -12.33) * mm});
            skLineSegment(sketch, "E3320", {"start": v(66.5, -15.33) * mm, "end": v(66.11, -13.93) * mm});
            skLineSegment(sketch, "E3321", {"start": v(77.43, -29.36) * mm, "end": v(76.88, -28.21) * mm});
            skLineSegment(sketch, "E3322", {"start": v(68.34, -22.98) * mm, "end": v(68.22, -22.44) * mm});
            skLineSegment(sketch, "E3323", {"start": v(64.5, -12.33) * mm, "end": v(63.46, -13.46) * mm});
            skLineSegment(sketch, "E3324", {"start": v(63.46, -13.46) * mm, "end": v(62.29, -14.86) * mm});
            skLineSegment(sketch, "E3325", {"start": v(56.06, -24.32) * mm, "end": v(55.93, -24.57) * mm});
            skLineSegment(sketch, "E3326", {"start": v(55.93, -24.57) * mm, "end": v(55.54, -25.33) * mm});
            skLineSegment(sketch, "E3327", {"start": v(55.54, -25.33) * mm, "end": v(55.03, -26.4) * mm});
            skLineSegment(sketch, "E3328", {"start": v(55.03, -26.4) * mm, "end": v(54.55, -27.45) * mm});
            skLineSegment(sketch, "E3329", {"start": v(56.34, -23.8) * mm, "end": v(56.06, -24.32) * mm});
            skLineSegment(sketch, "E3330", {"start": v(57.22, -22.28) * mm, "end": v(56.34, -23.8) * mm});
            skLineSegment(sketch, "E3331", {"start": v(58.46, -20.26) * mm, "end": v(57.22, -22.28) * mm});
            skLineSegment(sketch, "E3332", {"start": v(59.75, -18.31) * mm, "end": v(58.46, -20.26) * mm});
            skLineSegment(sketch, "E3333", {"start": v(61.04, -16.5) * mm, "end": v(59.75, -18.31) * mm});
            skLineSegment(sketch, "E3334", {"start": v(62.29, -14.86) * mm, "end": v(61.04, -16.5) * mm});
            skLineSegment(sketch, "E3335", {"start": v(78.43, -31.48) * mm, "end": v(78.38, -31.37) * mm});
            skLineSegment(sketch, "E3336", {"start": v(68.22, -22.44) * mm, "end": v(67.85, -20.83) * mm});
            skLineSegment(sketch, "E3337", {"start": v(79.58, -34.65) * mm, "end": v(79.33, -33.87) * mm});
            skLineSegment(sketch, "E3338", {"start": v(78.47, -31.58) * mm, "end": v(78.43, -31.48) * mm});
            skLineSegment(sketch, "E3339", {"start": v(79.8, -35.4) * mm, "end": v(79.58, -34.65) * mm});
            skLineSegment(sketch, "E3340", {"start": v(79.98, -36.06) * mm, "end": v(79.8, -35.4) * mm});
            skLineSegment(sketch, "E3341", {"start": v(80.07, -36.46) * mm, "end": v(79.98, -36.06) * mm});
            skLineSegment(sketch, "E3342", {"start": v(80.08, -36.6) * mm, "end": v(80.07, -36.46) * mm});
            skLineSegment(sketch, "E3343", {"start": v(80.1, -36.65) * mm, "end": v(80.08, -36.6) * mm});
            skLineSegment(sketch, "E3344", {"start": v(80.1, -36.81) * mm, "end": v(80.1, -36.65) * mm});
            skLineSegment(sketch, "E3345", {"start": v(80.1, -37.23) * mm, "end": v(80.1, -36.81) * mm});
            skLineSegment(sketch, "E3346", {"start": v(80.1, -37.84) * mm, "end": v(80.1, -37.23) * mm});
            skLineSegment(sketch, "E3347", {"start": v(80.07, -38.62) * mm, "end": v(80.1, -37.84) * mm});
            skLineSegment(sketch, "E3348", {"start": v(80.02, -39.55) * mm, "end": v(80.07, -38.62) * mm});
            skLineSegment(sketch, "E3349", {"start": v(79.93, -40.63) * mm, "end": v(80.02, -39.55) * mm});
            skLineSegment(sketch, "E3350", {"start": v(71.69, -54.72) * mm, "end": v(72.36, -55.08) * mm});
            skLineSegment(sketch, "E3351", {"start": v(70.87, -54.02) * mm, "end": v(71.69, -54.72) * mm});
            skLineSegment(sketch, "E3352", {"start": v(70.26, -53.11) * mm, "end": v(70.87, -54.02) * mm});
            skLineSegment(sketch, "E3353", {"start": v(70, -52.3) * mm, "end": v(70.26, -53.11) * mm});
            skLineSegment(sketch, "E3354", {"start": v(69.97, -52.02) * mm, "end": v(70, -52.3) * mm});
            skLineSegment(sketch, "E3355", {"start": v(69.94, -51.62) * mm, "end": v(69.97, -52.02) * mm});
            skLineSegment(sketch, "E3356", {"start": v(69.83, -50.44) * mm, "end": v(69.94, -51.62) * mm});
            skLineSegment(sketch, "E3357", {"start": v(69.64, -48.62) * mm, "end": v(69.83, -50.44) * mm});
            skLineSegment(sketch, "E3358", {"start": v(64.33, -23.9) * mm, "end": v(64.08, -22.61) * mm});
            skLineSegment(sketch, "E3359", {"start": v(64.63, -25.46) * mm, "end": v(64.33, -23.9) * mm});
            skLineSegment(sketch, "E3360", {"start": v(64.98, -27.27) * mm, "end": v(64.63, -25.46) * mm});
            skLineSegment(sketch, "E3361", {"start": v(65.35, -29.3) * mm, "end": v(64.98, -27.27) * mm});
            skLineSegment(sketch, "E3362", {"start": v(65.75, -31.49) * mm, "end": v(65.35, -29.3) * mm});
            skLineSegment(sketch, "E3363", {"start": v(66.15, -33.82) * mm, "end": v(65.75, -31.49) * mm});
            skLineSegment(sketch, "E3364", {"start": v(66.56, -36.25) * mm, "end": v(66.15, -33.82) * mm});
            skLineSegment(sketch, "E3365", {"start": v(66.96, -38.75) * mm, "end": v(66.56, -36.25) * mm});
            skLineSegment(sketch, "E3366", {"start": v(67.34, -41.27) * mm, "end": v(66.96, -38.75) * mm});
            skLineSegment(sketch, "E3367", {"start": v(67.7, -43.78) * mm, "end": v(67.34, -41.27) * mm});
            skLineSegment(sketch, "E3368", {"start": v(68, -46.24) * mm, "end": v(67.7, -43.78) * mm});
            skLineSegment(sketch, "E3369", {"start": v(68.27, -48.62) * mm, "end": v(68, -46.24) * mm});
            skLineSegment(sketch, "E3370", {"start": v(68.43, -50.31) * mm, "end": v(68.27, -48.62) * mm});
            skLineSegment(sketch, "E3371", {"start": v(68.48, -50.88) * mm, "end": v(68.43, -50.31) * mm});
            skLineSegment(sketch, "E3372", {"start": v(68.36, -50.81) * mm, "end": v(68.48, -50.88) * mm});
            skLineSegment(sketch, "E3373", {"start": v(68.02, -50.59) * mm, "end": v(68.36, -50.81) * mm});
            skLineSegment(sketch, "E3374", {"start": v(67.39, -50.12) * mm, "end": v(68.02, -50.59) * mm});
            skLineSegment(sketch, "E3375", {"start": v(66.61, -49.5) * mm, "end": v(67.39, -50.12) * mm});
            skLineSegment(sketch, "E3376", {"start": v(65.71, -48.74) * mm, "end": v(66.61, -49.5) * mm});
            skLineSegment(sketch, "E3377", {"start": v(64.71, -47.86) * mm, "end": v(65.71, -48.74) * mm});
            skLineSegment(sketch, "E3378", {"start": v(63.65, -46.89) * mm, "end": v(64.71, -47.86) * mm});
            skLineSegment(sketch, "E3379", {"start": v(62.53, -45.83) * mm, "end": v(63.65, -46.89) * mm});
            skLineSegment(sketch, "E3380", {"start": v(61.68, -45) * mm, "end": v(62.53, -45.83) * mm});
            skLineSegment(sketch, "E3381", {"start": v(61.4, -44.72) * mm, "end": v(61.68, -45) * mm});
            skLineSegment(sketch, "E3382", {"start": v(53.2, -32.04) * mm, "end": v(53.33, -32.74) * mm});
            skLineSegment(sketch, "E3383", {"start": v(53.16, -31.53) * mm, "end": v(53.2, -32.04) * mm});
            skLineSegment(sketch, "E3384", {"start": v(53.16, -31.31) * mm, "end": v(53.16, -31.53) * mm});
            skLineSegment(sketch, "E3385", {"start": v(53.16, -31.24) * mm, "end": v(53.16, -31.31) * mm});
            skLineSegment(sketch, "E3386", {"start": v(53.17, -31.13) * mm, "end": v(53.16, -31.24) * mm});
            skLineSegment(sketch, "E3387", {"start": v(53.25, -30.83) * mm, "end": v(53.17, -31.13) * mm});
            skLineSegment(sketch, "E3388", {"start": v(54.55, -27.45) * mm, "end": v(54.11, -28.47) * mm});
            skLineSegment(sketch, "E3389", {"start": v(54.11, -28.47) * mm, "end": v(53.74, -29.4) * mm});
            skLineSegment(sketch, "E3390", {"start": v(53.74, -29.4) * mm, "end": v(53.44, -30.2) * mm});
            skLineSegment(sketch, "E3391", {"start": v(53.44, -30.2) * mm, "end": v(53.25, -30.83) * mm});
            skLineSegment(sketch, "E3392", {"start": v(53.33, -32.74) * mm, "end": v(53.57, -33.63) * mm});
            skLineSegment(sketch, "E3393", {"start": v(53.57, -33.63) * mm, "end": v(53.97, -34.7) * mm});
            skLineSegment(sketch, "E3394", {"start": v(53.97, -34.7) * mm, "end": v(54.56, -35.93) * mm});
            skLineSegment(sketch, "E3395", {"start": v(54.56, -35.93) * mm, "end": v(55.37, -37.32) * mm});
            skLineSegment(sketch, "E3396", {"start": v(55.37, -37.32) * mm, "end": v(56.16, -38.49) * mm});
            skLineSegment(sketch, "E3397", {"start": v(56.16, -38.49) * mm, "end": v(56.44, -38.86) * mm});
            skLineSegment(sketch, "E3398", {"start": v(56.44, -38.86) * mm, "end": v(56.71, -39.22) * mm});
            skLineSegment(sketch, "E3399", {"start": v(56.71, -39.22) * mm, "end": v(57.54, -40.3) * mm});
            skLineSegment(sketch, "E3400", {"start": v(57.54, -40.3) * mm, "end": v(58.74, -41.79) * mm});
            skLineSegment(sketch, "E3401", {"start": v(58.74, -41.79) * mm, "end": v(60.04, -43.28) * mm});
            skLineSegment(sketch, "E3402", {"start": v(60.04, -43.28) * mm, "end": v(61.05, -44.37) * mm});
            skLineSegment(sketch, "E3403", {"start": v(61.05, -44.37) * mm, "end": v(61.4, -44.72) * mm});
            skLineSegment(sketch, "E3404", {"start": v(64.08, -22.61) * mm, "end": v(63.88, -21.65) * mm});
            skLineSegment(sketch, "E3405", {"start": v(63.88, -21.65) * mm, "end": v(63.76, -21.05) * mm});
            skLineSegment(sketch, "E3406", {"start": v(63.76, -21.05) * mm, "end": v(63.72, -20.84) * mm});
            skLineSegment(sketch, "E3407", {"start": v(63.72, -20.84) * mm, "end": v(64.8, -40.73) * mm});
            skLineSegment(sketch, "E3408", {"start": v(64.8, -40.73) * mm, "end": v(64.68, -40.62) * mm});
            skLineSegment(sketch, "E3409", {"start": v(64.68, -40.62) * mm, "end": v(64.34, -40.33) * mm});
            skLineSegment(sketch, "E3410", {"start": v(64.34, -40.33) * mm, "end": v(63.82, -39.87) * mm});
            skLineSegment(sketch, "E3411", {"start": v(63.82, -39.87) * mm, "end": v(63.17, -39.27) * mm});
            skLineSegment(sketch, "E3412", {"start": v(63.17, -39.27) * mm, "end": v(62.42, -38.54) * mm});
            skLineSegment(sketch, "E3413", {"start": v(62.42, -38.54) * mm, "end": v(61.63, -37.7) * mm});
            skLineSegment(sketch, "E3414", {"start": v(61.63, -37.7) * mm, "end": v(60.82, -36.8) * mm});
            skLineSegment(sketch, "E3415", {"start": v(60.82, -36.8) * mm, "end": v(60.22, -36.08) * mm});
            skLineSegment(sketch, "E3416", {"start": v(60.22, -36.08) * mm, "end": v(60.03, -35.84) * mm});
            skLineSegment(sketch, "E3417", {"start": v(60.03, -35.84) * mm, "end": v(59.77, -35.49) * mm});
            skLineSegment(sketch, "E3418", {"start": v(59.77, -35.49) * mm, "end": v(59.05, -34.4) * mm});
            skLineSegment(sketch, "E3419", {"start": v(59.05, -34.4) * mm, "end": v(58.34, -33.05) * mm});
            skLineSegment(sketch, "E3420", {"start": v(58.34, -33.05) * mm, "end": v(57.88, -31.82) * mm});
            skLineSegment(sketch, "E3421", {"start": v(57.88, -31.82) * mm, "end": v(57.69, -31) * mm});
            skLineSegment(sketch, "E3422", {"start": v(57.69, -31) * mm, "end": v(57.65, -30.72) * mm});
            skLineSegment(sketch, "E3423", {"start": v(57.65, -30.72) * mm, "end": v(57.63, -30.52) * mm});
            skLineSegment(sketch, "E3424", {"start": v(57.63, -30.52) * mm, "end": v(57.6, -29.9) * mm});
            skLineSegment(sketch, "E3425", {"start": v(57.6, -29.9) * mm, "end": v(57.66, -28.9) * mm});
            skLineSegment(sketch, "E3426", {"start": v(57.66, -28.9) * mm, "end": v(57.92, -27.67) * mm});
            skLineSegment(sketch, "E3427", {"start": v(57.92, -27.67) * mm, "end": v(58.3, -26.55) * mm});
            skLineSegment(sketch, "E3428", {"start": v(58.3, -26.55) * mm, "end": v(58.45, -26.19) * mm});
            skLineSegment(sketch, "E3429", {"start": v(58.45, -26.19) * mm, "end": v(58.64, -25.76) * mm});
            skLineSegment(sketch, "E3430", {"start": v(58.64, -25.76) * mm, "end": v(59.25, -24.49) * mm});
            skLineSegment(sketch, "E3431", {"start": v(59.25, -24.49) * mm, "end": v(60.07, -22.9) * mm});
            skLineSegment(sketch, "E3432", {"start": v(60.07, -22.9) * mm, "end": v(60.9, -21.46) * mm});
            skLineSegment(sketch, "E3433", {"start": v(60.9, -21.46) * mm, "end": v(61.72, -20.18) * mm});
            skLineSegment(sketch, "E3434", {"start": v(61.72, -20.18) * mm, "end": v(62.46, -19.08) * mm});
            skLineSegment(sketch, "E3435", {"start": v(62.46, -19.08) * mm, "end": v(63.12, -18.17) * mm});
            skLineSegment(sketch, "E3436", {"start": v(63.12, -18.17) * mm, "end": v(63.66, -17.49) * mm});
            skLineSegment(sketch, "E3437", {"start": v(63.66, -17.49) * mm, "end": v(63.94, -17.15) * mm});
            skLineSegment(sketch, "E3438", {"start": v(63.94, -17.15) * mm, "end": v(64.04, -17.04) * mm});
            skLineSegment(sketch, "E3439", {"start": v(64.04, -17.04) * mm, "end": v(64.17, -17.44) * mm});
            skLineSegment(sketch, "E3440", {"start": v(64.17, -17.44) * mm, "end": v(64.5, -18.66) * mm});
            skLineSegment(sketch, "E3441", {"start": v(64.5, -18.66) * mm, "end": v(64.98, -20.5) * mm});
            skLineSegment(sketch, "E3442", {"start": v(64.98, -20.5) * mm, "end": v(65.45, -22.55) * mm});
            skLineSegment(sketch, "E3443", {"start": v(65.45, -22.55) * mm, "end": v(65.92, -24.76) * mm});
            skLineSegment(sketch, "E3444", {"start": v(65.92, -24.76) * mm, "end": v(66.39, -27.1) * mm});
            skLineSegment(sketch, "E3445", {"start": v(66.39, -27.1) * mm, "end": v(66.84, -29.55) * mm});
            skLineSegment(sketch, "E3446", {"start": v(66.84, -29.55) * mm, "end": v(67.28, -32.06) * mm});
            skLineSegment(sketch, "E3447", {"start": v(67.28, -32.06) * mm, "end": v(67.7, -34.6) * mm});
            skLineSegment(sketch, "E3448", {"start": v(67.7, -34.6) * mm, "end": v(68.1, -37.13) * mm});
            skLineSegment(sketch, "E3449", {"start": v(68.1, -37.13) * mm, "end": v(68.47, -39.64) * mm});
            skLineSegment(sketch, "E3450", {"start": v(68.47, -39.64) * mm, "end": v(68.82, -42.07) * mm});
            skLineSegment(sketch, "E3451", {"start": v(68.82, -42.07) * mm, "end": v(69.13, -44.4) * mm});
            skLineSegment(sketch, "E3452", {"start": v(84.27, -58.52) * mm, "end": v(84.52, -58.8) * mm});
            skLineSegment(sketch, "E3453", {"start": v(83.55, -57.63) * mm, "end": v(84.27, -58.52) * mm});
            skLineSegment(sketch, "E3454", {"start": v(82.75, -56.55) * mm, "end": v(83.55, -57.63) * mm});
            skLineSegment(sketch, "E3455", {"start": v(82.19, -55.65) * mm, "end": v(82.75, -56.55) * mm});
            skLineSegment(sketch, "E3456", {"start": v(81.94, -55.19) * mm, "end": v(82.19, -55.65) * mm});
            skLineSegment(sketch, "E3457", {"start": v(81.9, -55.04) * mm, "end": v(81.94, -55.19) * mm});
            skLineSegment(sketch, "E3458", {"start": v(81.87, -54.92) * mm, "end": v(81.9, -55.04) * mm});
            skLineSegment(sketch, "E3459", {"start": v(81.8, -54.55) * mm, "end": v(81.87, -54.92) * mm});
            skLineSegment(sketch, "E3460", {"start": v(81.72, -53.84) * mm, "end": v(81.8, -54.55) * mm});
            skLineSegment(sketch, "E3461", {"start": v(81.66, -52.93) * mm, "end": v(81.72, -53.84) * mm});
            skLineSegment(sketch, "E3462", {"start": v(81.66, -52.13) * mm, "end": v(81.66, -52.93) * mm});
            skLineSegment(sketch, "E3463", {"start": v(81.66, -51.87) * mm, "end": v(81.66, -52.13) * mm});
            skLineSegment(sketch, "E3464", {"start": v(81.67, -51.64) * mm, "end": v(81.66, -51.87) * mm});
            skLineSegment(sketch, "E3465", {"start": v(81.7, -50.98) * mm, "end": v(81.67, -51.64) * mm});
            skLineSegment(sketch, "E3466", {"start": v(81.76, -50.09) * mm, "end": v(81.7, -50.98) * mm});
            skLineSegment(sketch, "E3467", {"start": v(81.82, -49.23) * mm, "end": v(81.76, -50.09) * mm});
            skLineSegment(sketch, "E3468", {"start": v(81.9, -48.43) * mm, "end": v(81.82, -49.23) * mm});
            skLineSegment(sketch, "E3469", {"start": v(81.96, -47.75) * mm, "end": v(81.9, -48.43) * mm});
            skLineSegment(sketch, "E3470", {"start": v(82.02, -47.21) * mm, "end": v(81.96, -47.75) * mm});
            skLineSegment(sketch, "E3471", {"start": v(82.05, -46.86) * mm, "end": v(82.02, -47.21) * mm});
            skLineSegment(sketch, "E3472", {"start": v(82.07, -46.74) * mm, "end": v(82.05, -46.86) * mm});
            skLineSegment(sketch, "E3473", {"start": v(82.14, -46.94) * mm, "end": v(82.07, -46.74) * mm});
            skLineSegment(sketch, "E3474", {"start": v(82.32, -47.51) * mm, "end": v(82.14, -46.94) * mm});
            skLineSegment(sketch, "E3475", {"start": v(82.61, -48.39) * mm, "end": v(82.32, -47.51) * mm});
            skLineSegment(sketch, "E3476", {"start": v(82.98, -49.5) * mm, "end": v(82.61, -48.39) * mm});
            skLineSegment(sketch, "E3477", {"start": v(83.42, -50.8) * mm, "end": v(82.98, -49.5) * mm});
            skLineSegment(sketch, "E3478", {"start": v(83.9, -52.2) * mm, "end": v(83.42, -50.8) * mm});
            skLineSegment(sketch, "E3479", {"start": v(84.42, -53.65) * mm, "end": v(83.9, -52.2) * mm});
            skLineSegment(sketch, "E3480", {"start": v(84.81, -54.74) * mm, "end": v(84.42, -53.65) * mm});
            skLineSegment(sketch, "E3481", {"start": v(84.95, -55.1) * mm, "end": v(84.81, -54.74) * mm});
            skLineSegment(sketch, "E3482", {"start": v(85.08, -55.45) * mm, "end": v(84.95, -55.1) * mm});
            skLineSegment(sketch, "E3483", {"start": v(85.48, -56.51) * mm, "end": v(85.08, -55.45) * mm});
            skLineSegment(sketch, "E3484", {"start": v(86, -57.83) * mm, "end": v(85.48, -56.51) * mm});
            skLineSegment(sketch, "E3485", {"start": v(86.48, -59.02) * mm, "end": v(86, -57.83) * mm});
            skLineSegment(sketch, "E3486", {"start": v(86.9, -60.05) * mm, "end": v(86.48, -59.02) * mm});
            skLineSegment(sketch, "E3487", {"start": v(87.26, -60.9) * mm, "end": v(86.9, -60.05) * mm});
            skLineSegment(sketch, "E3488", {"start": v(87.53, -61.53) * mm, "end": v(87.26, -60.9) * mm});
            skLineSegment(sketch, "E3489", {"start": v(87.7, -61.93) * mm, "end": v(87.53, -61.53) * mm});
            skLineSegment(sketch, "E3490", {"start": v(87.77, -62.07) * mm, "end": v(87.7, -61.93) * mm});
            skLineSegment(sketch, "E3491", {"start": v(87.69, -62) * mm, "end": v(87.77, -62.07) * mm});
            skLineSegment(sketch, "E3492", {"start": v(87.47, -61.8) * mm, "end": v(87.69, -62) * mm});
            skLineSegment(sketch, "E3493", {"start": v(87.13, -61.48) * mm, "end": v(87.47, -61.8) * mm});
            skLineSegment(sketch, "E3494", {"start": v(86.7, -61.06) * mm, "end": v(87.13, -61.48) * mm});
            skLineSegment(sketch, "E3495", {"start": v(86.2, -60.57) * mm, "end": v(86.7, -61.06) * mm});
            skLineSegment(sketch, "E3496", {"start": v(85.65, -60.01) * mm, "end": v(86.2, -60.57) * mm});
            skLineSegment(sketch, "E3497", {"start": v(85.08, -59.42) * mm, "end": v(85.65, -60.01) * mm});
            skLineSegment(sketch, "E3498", {"start": v(84.66, -58.96) * mm, "end": v(85.08, -59.42) * mm});
            skLineSegment(sketch, "E3499", {"start": v(84.52, -58.8) * mm, "end": v(84.66, -58.96) * mm});
            skLineSegment(sketch, "E3500", {"start": v(104.47, -59.32) * mm, "end": v(105.06, -59.13) * mm});
            skLineSegment(sketch, "E3501", {"start": v(102.7, -59.9) * mm, "end": v(104.47, -59.32) * mm});
            skLineSegment(sketch, "E3502", {"start": v(100.43, -60.61) * mm, "end": v(102.7, -59.9) * mm});
            skLineSegment(sketch, "E3503", {"start": v(98.32, -61.3) * mm, "end": v(100.43, -60.61) * mm});
            skLineSegment(sketch, "E3504", {"start": v(96.43, -61.96) * mm, "end": v(98.32, -61.3) * mm});
            skLineSegment(sketch, "E3505", {"start": v(94.8, -62.62) * mm, "end": v(96.43, -61.96) * mm});
            skLineSegment(sketch, "E3506", {"start": v(93.48, -63.29) * mm, "end": v(94.8, -62.62) * mm});
            skLineSegment(sketch, "E3507", {"start": v(92.52, -63.98) * mm, "end": v(93.48, -63.29) * mm});
            skLineSegment(sketch, "E3508", {"start": v(92.07, -64.5) * mm, "end": v(92.52, -63.98) * mm});
            skLineSegment(sketch, "E3509", {"start": v(92, -64.7) * mm, "end": v(92.07, -64.5) * mm});
            skLineSegment(sketch, "E3510", {"start": v(91.95, -64.82) * mm, "end": v(92, -64.7) * mm});
            skLineSegment(sketch, "E3511", {"start": v(91.95, -65.2) * mm, "end": v(91.95, -64.82) * mm});
            skLineSegment(sketch, "E3512", {"start": v(92.05, -65.99) * mm, "end": v(91.95, -65.2) * mm});
            skLineSegment(sketch, "E3513", {"start": v(92.27, -67) * mm, "end": v(92.05, -65.99) * mm});
            skLineSegment(sketch, "E3514", {"start": v(92.59, -68.14) * mm, "end": v(92.27, -67) * mm});
            skLineSegment(sketch, "E3515", {"start": v(92.97, -69.35) * mm, "end": v(92.59, -68.14) * mm});
            skLineSegment(sketch, "E3516", {"start": v(93.39, -70.55) * mm, "end": v(92.97, -69.35) * mm});
            skLineSegment(sketch, "E3517", {"start": v(93.82, -71.66) * mm, "end": v(93.39, -70.55) * mm});
            skLineSegment(sketch, "E3518", {"start": v(94.12, -72.37) * mm, "end": v(93.82, -71.66) * mm});
            skLineSegment(sketch, "E3519", {"start": v(94.23, -72.6) * mm, "end": v(94.12, -72.37) * mm});
            skLineSegment(sketch, "E3520", {"start": v(93.87, -72.29) * mm, "end": v(94.23, -72.6) * mm});
            skLineSegment(sketch, "E3521", {"start": v(92.9, -71.21) * mm, "end": v(93.87, -72.29) * mm});
            skLineSegment(sketch, "E3522", {"start": v(91.65, -69.52) * mm, "end": v(92.9, -71.21) * mm});
            skLineSegment(sketch, "E3523", {"start": v(90.57, -67.66) * mm, "end": v(91.65, -69.52) * mm});
            skLineSegment(sketch, "E3524", {"start": v(89.9, -66.23) * mm, "end": v(90.57, -67.66) * mm});
            skLineSegment(sketch, "E3525", {"start": v(89.72, -65.74) * mm, "end": v(89.9, -66.23) * mm});
            skLineSegment(sketch, "E3526", {"start": v(89.56, -65.28) * mm, "end": v(89.72, -65.74) * mm});
            skLineSegment(sketch, "E3527", {"start": v(89.14, -63.85) * mm, "end": v(89.56, -65.28) * mm});
            skLineSegment(sketch, "E3528", {"start": v(88.7, -61.92) * mm, "end": v(89.14, -63.85) * mm});
            skLineSegment(sketch, "E3529", {"start": v(88.38, -60.07) * mm, "end": v(88.7, -61.92) * mm});
            skLineSegment(sketch, "E3530", {"start": v(88.2, -58.83) * mm, "end": v(88.38, -60.07) * mm});
            skLineSegment(sketch, "E3531", {"start": v(88.14, -58.42) * mm, "end": v(88.2, -58.83) * mm});
            skLineSegment(sketch, "E3532", {"start": v(88.08, -57.97) * mm, "end": v(88.14, -58.42) * mm});
            skLineSegment(sketch, "E3533", {"start": v(87.91, -56.63) * mm, "end": v(88.08, -57.97) * mm});
            skLineSegment(sketch, "E3534", {"start": v(87.72, -55.28) * mm, "end": v(87.91, -56.63) * mm});
            skLineSegment(sketch, "E3535", {"start": v(87.49, -54.33) * mm, "end": v(87.72, -55.28) * mm});
            skLineSegment(sketch, "E3536", {"start": v(87.25, -53.87) * mm, "end": v(87.49, -54.33) * mm});
            skLineSegment(sketch, "E3537", {"start": v(87.13, -53.76) * mm, "end": v(87.25, -53.87) * mm});
            skLineSegment(sketch, "E3538", {"start": v(87.35, -53.86) * mm, "end": v(87.13, -53.76) * mm});
            skLineSegment(sketch, "E3539", {"start": v(87.97, -54.3) * mm, "end": v(87.35, -53.86) * mm});
            skLineSegment(sketch, "E3540", {"start": v(88.9, -55.13) * mm, "end": v(87.97, -54.3) * mm});
            skLineSegment(sketch, "E3541", {"start": v(89.85, -56.14) * mm, "end": v(88.9, -55.13) * mm});
            skLineSegment(sketch, "E3542", {"start": v(90.8, -57.22) * mm, "end": v(89.85, -56.14) * mm});
            skLineSegment(sketch, "E3543", {"start": v(91.71, -58.26) * mm, "end": v(90.8, -57.22) * mm});
            skLineSegment(sketch, "E3544", {"start": v(92.56, -59.12) * mm, "end": v(91.71, -58.26) * mm});
            skLineSegment(sketch, "E3545", {"start": v(93.3, -59.7) * mm, "end": v(92.56, -59.12) * mm});
            skLineSegment(sketch, "E3546", {"start": v(93.74, -59.9) * mm, "end": v(93.3, -59.7) * mm});
            skLineSegment(sketch, "E3547", {"start": v(93.89, -59.9) * mm, "end": v(93.74, -59.9) * mm});
            skLineSegment(sketch, "E3548", {"start": v(94.1, -59.83) * mm, "end": v(93.89, -59.9) * mm});
            skLineSegment(sketch, "E3549", {"start": v(94.71, -59.64) * mm, "end": v(94.1, -59.83) * mm});
            skLineSegment(sketch, "E3550", {"start": v(95.72, -59.28) * mm, "end": v(94.71, -59.64) * mm});
            skLineSegment(sketch, "E3551", {"start": v(96.87, -58.85) * mm, "end": v(95.72, -59.28) * mm});
            skLineSegment(sketch, "E3552", {"start": v(98.13, -58.35) * mm, "end": v(96.87, -58.85) * mm});
            skLineSegment(sketch, "E3553", {"start": v(99.49, -57.79) * mm, "end": v(98.13, -58.35) * mm});
            skLineSegment(sketch, "E3554", {"start": v(100.91, -57.18) * mm, "end": v(99.49, -57.79) * mm});
            skLineSegment(sketch, "E3555", {"start": v(102.37, -56.55) * mm, "end": v(100.91, -57.18) * mm});
            skLineSegment(sketch, "E3556", {"start": v(103.47, -56.06) * mm, "end": v(102.37, -56.55) * mm});
            skLineSegment(sketch, "E3557", {"start": v(103.84, -55.9) * mm, "end": v(103.47, -56.06) * mm});
            skLineSegment(sketch, "E3558", {"start": v(104.23, -55.72) * mm, "end": v(103.84, -55.9) * mm});
            skLineSegment(sketch, "E3559", {"start": v(105.42, -55.18) * mm, "end": v(104.23, -55.72) * mm});
            skLineSegment(sketch, "E3560", {"start": v(106.95, -54.47) * mm, "end": v(105.42, -55.18) * mm});
            skLineSegment(sketch, "E3561", {"start": v(108.39, -53.8) * mm, "end": v(106.95, -54.47) * mm});
            skLineSegment(sketch, "E3562", {"start": v(109.7, -53.18) * mm, "end": v(108.39, -53.8) * mm});
            skLineSegment(sketch, "E3563", {"start": v(128.08, -60.66) * mm, "end": v(130.1, -60.43) * mm});
            skLineSegment(sketch, "E3564", {"start": v(125.88, -60.94) * mm, "end": v(128.08, -60.66) * mm});
            skLineSegment(sketch, "E3565", {"start": v(136.57, -57.7) * mm, "end": v(136.65, -57.47) * mm});
            skLineSegment(sketch, "E3566", {"start": v(136.65, -57.47) * mm, "end": v(136.55, -57.47) * mm});
            skLineSegment(sketch, "E3567", {"start": v(136.55, -57.47) * mm, "end": v(136.24, -57.47) * mm});
            skLineSegment(sketch, "E3568", {"start": v(136.24, -57.47) * mm, "end": v(135.6, -57.48) * mm});
            skLineSegment(sketch, "E3569", {"start": v(135.6, -57.48) * mm, "end": v(134.75, -57.52) * mm});
            skLineSegment(sketch, "E3570", {"start": v(134.75, -57.52) * mm, "end": v(133.7, -57.58) * mm});
            skLineSegment(sketch, "E3571", {"start": v(133.7, -57.58) * mm, "end": v(132.47, -57.66) * mm});
            skLineSegment(sketch, "E3572", {"start": v(132.47, -57.66) * mm, "end": v(131.08, -57.76) * mm});
            skLineSegment(sketch, "E3573", {"start": v(131.08, -57.76) * mm, "end": v(129.55, -57.88) * mm});
            skLineSegment(sketch, "E3574", {"start": v(129.55, -57.88) * mm, "end": v(128.31, -58) * mm});
            skLineSegment(sketch, "E3575", {"start": v(128.31, -58) * mm, "end": v(127.9, -58.03) * mm});
            skLineSegment(sketch, "E3576", {"start": v(127.9, -58.03) * mm, "end": v(127.15, -58.1) * mm});
            skLineSegment(sketch, "E3577", {"start": v(127.15, -58.1) * mm, "end": v(124.92, -58.35) * mm});
            skLineSegment(sketch, "E3578", {"start": v(124.92, -58.35) * mm, "end": v(121.72, -58.73) * mm});
            skLineSegment(sketch, "E3579", {"start": v(121.72, -58.73) * mm, "end": v(118.36, -59.2) * mm});
            skLineSegment(sketch, "E3580", {"start": v(118.36, -59.2) * mm, "end": v(115.77, -59.59) * mm});
            skLineSegment(sketch, "E3581", {"start": v(115.77, -59.59) * mm, "end": v(114.9, -59.73) * mm});
            skLineSegment(sketch, "E3582", {"start": v(114.9, -59.73) * mm, "end": v(113.98, -59.88) * mm});
            skLineSegment(sketch, "E3583", {"start": v(113.98, -59.88) * mm, "end": v(109.53, -60.68) * mm});
            skLineSegment(sketch, "E3584", {"start": v(109.53, -60.68) * mm, "end": v(105.29, -61.54) * mm});
            skLineSegment(sketch, "E3585", {"start": v(105.29, -61.54) * mm, "end": v(104.46, -61.73) * mm});
            skLineSegment(sketch, "E3586", {"start": v(105.06, -59.13) * mm, "end": v(105.26, -59.06) * mm});
            skLineSegment(sketch, "E3587", {"start": v(105.26, -59.06) * mm, "end": v(105.87, -58.86) * mm});
            skLineSegment(sketch, "E3588", {"start": v(105.87, -58.86) * mm, "end": v(106.95, -58.52) * mm});
            skLineSegment(sketch, "E3589", {"start": v(106.95, -58.52) * mm, "end": v(108.29, -58.1) * mm});
            skLineSegment(sketch, "E3590", {"start": v(108.29, -58.1) * mm, "end": v(109.85, -57.65) * mm});
            skLineSegment(sketch, "E3591", {"start": v(109.85, -57.65) * mm, "end": v(111.61, -57.15) * mm});
            skLineSegment(sketch, "E3592", {"start": v(111.61, -57.15) * mm, "end": v(113.55, -56.64) * mm});
            skLineSegment(sketch, "E3593", {"start": v(113.55, -56.64) * mm, "end": v(115.64, -56.13) * mm});
            skLineSegment(sketch, "E3594", {"start": v(115.64, -56.13) * mm, "end": v(117.85, -55.64) * mm});
            skLineSegment(sketch, "E3595", {"start": v(117.85, -55.64) * mm, "end": v(120.16, -55.18) * mm});
            skLineSegment(sketch, "E3596", {"start": v(120.16, -55.18) * mm, "end": v(122.55, -54.76) * mm});
            skLineSegment(sketch, "E3597", {"start": v(122.55, -54.76) * mm, "end": v(124.98, -54.4) * mm});
            skLineSegment(sketch, "E3598", {"start": v(124.98, -54.4) * mm, "end": v(127.43, -54.13) * mm});
            skLineSegment(sketch, "E3599", {"start": v(127.43, -54.13) * mm, "end": v(129.89, -53.95) * mm});
            skLineSegment(sketch, "E3600", {"start": v(129.89, -53.95) * mm, "end": v(132.31, -53.88) * mm});
            skLineSegment(sketch, "E3601", {"start": v(132.31, -53.88) * mm, "end": v(134.69, -53.94) * mm});
            skLineSegment(sketch, "E3602", {"start": v(134.69, -53.94) * mm, "end": v(136.4, -54.06) * mm});
            skLineSegment(sketch, "E3603", {"start": v(136.4, -54.06) * mm, "end": v(136.98, -54.13) * mm});
            skLineSegment(sketch, "E3604", {"start": v(136.98, -54.13) * mm, "end": v(136.59, -53.93) * mm});
            skLineSegment(sketch, "E3605", {"start": v(136.59, -53.93) * mm, "end": v(135.4, -53.38) * mm});
            skLineSegment(sketch, "E3606", {"start": v(135.4, -53.38) * mm, "end": v(133.8, -52.73) * mm});
            skLineSegment(sketch, "E3607", {"start": v(133.8, -52.73) * mm, "end": v(132.18, -52.16) * mm});
            skLineSegment(sketch, "E3608", {"start": v(132.18, -52.16) * mm, "end": v(130.58, -51.67) * mm});
            skLineSegment(sketch, "E3609", {"start": v(130.58, -51.67) * mm, "end": v(129.01, -51.26) * mm});
            skLineSegment(sketch, "E3610", {"start": v(129.01, -51.26) * mm, "end": v(127.48, -50.92) * mm});
            skLineSegment(sketch, "E3611", {"start": v(127.48, -50.92) * mm, "end": v(126.01, -50.65) * mm});
            skLineSegment(sketch, "E3612", {"start": v(126.01, -50.65) * mm, "end": v(124.62, -50.43) * mm});
            skLineSegment(sketch, "E3613", {"start": v(124.62, -50.43) * mm, "end": v(123.31, -50.26) * mm});
            skLineSegment(sketch, "E3614", {"start": v(123.31, -50.26) * mm, "end": v(122.11, -50.14) * mm});
            skLineSegment(sketch, "E3615", {"start": v(115.36, -50.74) * mm, "end": v(114.6, -51) * mm});
            skLineSegment(sketch, "E3616", {"start": v(114.6, -51) * mm, "end": v(113.92, -51.25) * mm});
            skLineSegment(sketch, "E3617", {"start": v(113.92, -51.25) * mm, "end": v(113.36, -51.47) * mm});
            skLineSegment(sketch, "E3618", {"start": v(113.36, -51.47) * mm, "end": v(113.06, -51.6) * mm});
            skLineSegment(sketch, "E3619", {"start": v(95.41, -63.95) * mm, "end": v(94.3, -64.27) * mm});
            skLineSegment(sketch, "E3620", {"start": v(94.3, -64.27) * mm, "end": v(93.48, -64.52) * mm});
            skLineSegment(sketch, "E3621", {"start": v(93.48, -64.52) * mm, "end": v(93.13, -64.64) * mm});
            skLineSegment(sketch, "E3622", {"start": v(102.31, -62.21) * mm, "end": v(100.3, -62.7) * mm});
            skLineSegment(sketch, "E3623", {"start": v(112.85, -51.69) * mm, "end": v(112.51, -51.85) * mm});
            skLineSegment(sketch, "E3624", {"start": v(93.13, -64.64) * mm, "end": v(93.02, -64.7) * mm});
            skLineSegment(sketch, "E3625", {"start": v(100.3, -62.7) * mm, "end": v(98.45, -63.15) * mm});
            skLineSegment(sketch, "E3626", {"start": v(112.51, -51.85) * mm, "end": v(111.8, -52.19) * mm});
            skLineSegment(sketch, "E3627", {"start": v(93.02, -64.7) * mm, "end": v(93.2, -64.92) * mm});
            skLineSegment(sketch, "E3628", {"start": v(98.45, -63.15) * mm, "end": v(96.81, -63.57) * mm});
            skLineSegment(sketch, "E3629", {"start": v(111.8, -52.19) * mm, "end": v(110.84, -52.64) * mm});
            skLineSegment(sketch, "E3630", {"start": v(93.2, -64.92) * mm, "end": v(93.81, -65.57) * mm});
            skLineSegment(sketch, "E3631", {"start": v(96.81, -63.57) * mm, "end": v(95.41, -63.95) * mm});
            skLineSegment(sketch, "E3632", {"start": v(110.84, -52.64) * mm, "end": v(109.7, -53.18) * mm});
            skLineSegment(sketch, "E3633", {"start": v(104.46, -61.73) * mm, "end": v(103.92, -61.85) * mm});
            skLineSegment(sketch, "E3634", {"start": v(93.81, -65.57) * mm, "end": v(94.94, -66.6) * mm});
            skLineSegment(sketch, "E3635", {"start": v(94.94, -66.6) * mm, "end": v(96.35, -67.78) * mm});
            skLineSegment(sketch, "E3636", {"start": v(105.8, -74) * mm, "end": v(106.06, -74.14) * mm});
            skLineSegment(sketch, "E3637", {"start": v(106.06, -74.14) * mm, "end": v(106.82, -74.53) * mm});
            skLineSegment(sketch, "E3638", {"start": v(106.82, -74.53) * mm, "end": v(107.88, -75.04) * mm});
            skLineSegment(sketch, "E3639", {"start": v(107.88, -75.04) * mm, "end": v(108.94, -75.52) * mm});
            skLineSegment(sketch, "E3640", {"start": v(105.29, -73.72) * mm, "end": v(105.8, -74) * mm});
            skLineSegment(sketch, "E3641", {"start": v(103.76, -72.85) * mm, "end": v(105.29, -73.72) * mm});
            skLineSegment(sketch, "E3642", {"start": v(101.74, -71.6) * mm, "end": v(103.76, -72.85) * mm});
            skLineSegment(sketch, "E3643", {"start": v(99.8, -70.32) * mm, "end": v(101.74, -71.6) * mm});
            skLineSegment(sketch, "E3644", {"start": v(97.98, -69.03) * mm, "end": v(99.8, -70.32) * mm});
            skLineSegment(sketch, "E3645", {"start": v(96.35, -67.78) * mm, "end": v(97.98, -69.03) * mm});
            skLineSegment(sketch, "E3646", {"start": v(112.97, -51.64) * mm, "end": v(112.85, -51.69) * mm});
            skLineSegment(sketch, "E3647", {"start": v(103.92, -61.85) * mm, "end": v(102.31, -62.21) * mm});
            skLineSegment(sketch, "E3648", {"start": v(116.13, -50.48) * mm, "end": v(115.36, -50.74) * mm});
            skLineSegment(sketch, "E3649", {"start": v(113.06, -51.6) * mm, "end": v(112.97, -51.64) * mm});
            skLineSegment(sketch, "E3650", {"start": v(116.88, -50.26) * mm, "end": v(116.13, -50.48) * mm});
            skLineSegment(sketch, "E3651", {"start": v(117.54, -50.08) * mm, "end": v(116.88, -50.26) * mm});
            skLineSegment(sketch, "E3652", {"start": v(117.95, -50) * mm, "end": v(117.54, -50.08) * mm});
            skLineSegment(sketch, "E3653", {"start": v(118.08, -49.98) * mm, "end": v(117.95, -50) * mm});
            skLineSegment(sketch, "E3654", {"start": v(118.14, -49.97) * mm, "end": v(118.08, -49.98) * mm});
            skLineSegment(sketch, "E3655", {"start": v(118.3, -49.97) * mm, "end": v(118.14, -49.97) * mm});
            skLineSegment(sketch, "E3656", {"start": v(118.72, -49.96) * mm, "end": v(118.3, -49.97) * mm});
            skLineSegment(sketch, "E3657", {"start": v(119.32, -49.97) * mm, "end": v(118.72, -49.96) * mm});
            skLineSegment(sketch, "E3658", {"start": v(120.1, -50) * mm, "end": v(119.32, -49.97) * mm});
            skLineSegment(sketch, "E3659", {"start": v(121.04, -50.05) * mm, "end": v(120.1, -50) * mm});
            skLineSegment(sketch, "E3660", {"start": v(122.11, -50.14) * mm, "end": v(121.04, -50.05) * mm});
            skLineSegment(sketch, "E3661", {"start": v(136.2, -58.38) * mm, "end": v(136.57, -57.7) * mm});
            skLineSegment(sketch, "E3662", {"start": v(135.5, -59.2) * mm, "end": v(136.2, -58.38) * mm});
            skLineSegment(sketch, "E3663", {"start": v(134.6, -59.8) * mm, "end": v(135.5, -59.2) * mm});
            skLineSegment(sketch, "E3664", {"start": v(133.78, -60.08) * mm, "end": v(134.6, -59.8) * mm});
            skLineSegment(sketch, "E3665", {"start": v(133.5, -60.1) * mm, "end": v(133.78, -60.08) * mm});
            skLineSegment(sketch, "E3666", {"start": v(133.1, -60.13) * mm, "end": v(133.5, -60.1) * mm});
            skLineSegment(sketch, "E3667", {"start": v(131.92, -60.24) * mm, "end": v(133.1, -60.13) * mm});
            skLineSegment(sketch, "E3668", {"start": v(130.1, -60.43) * mm, "end": v(131.92, -60.24) * mm});
            skLineSegment(sketch, "E3669", {"start": v(105.38, -65.74) * mm, "end": v(104.1, -66) * mm});
            skLineSegment(sketch, "E3670", {"start": v(106.94, -65.43) * mm, "end": v(105.38, -65.74) * mm});
            skLineSegment(sketch, "E3671", {"start": v(108.76, -65.09) * mm, "end": v(106.94, -65.43) * mm});
            skLineSegment(sketch, "E3672", {"start": v(110.78, -64.71) * mm, "end": v(108.76, -65.09) * mm});
            skLineSegment(sketch, "E3673", {"start": v(112.97, -64.32) * mm, "end": v(110.78, -64.71) * mm});
            skLineSegment(sketch, "E3674", {"start": v(115.3, -63.91) * mm, "end": v(112.97, -64.32) * mm});
            skLineSegment(sketch, "E3675", {"start": v(117.74, -63.5) * mm, "end": v(115.3, -63.91) * mm});
            skLineSegment(sketch, "E3676", {"start": v(120.23, -63.1) * mm, "end": v(117.74, -63.5) * mm});
            skLineSegment(sketch, "E3677", {"start": v(122.75, -62.73) * mm, "end": v(120.23, -63.1) * mm});
            skLineSegment(sketch, "E3678", {"start": v(125.26, -62.37) * mm, "end": v(122.75, -62.73) * mm});
            skLineSegment(sketch, "E3679", {"start": v(127.73, -62.06) * mm, "end": v(125.26, -62.37) * mm});
            skLineSegment(sketch, "E3680", {"start": v(130.1, -61.8) * mm, "end": v(127.73, -62.06) * mm});
            skLineSegment(sketch, "E3681", {"start": v(131.8, -61.63) * mm, "end": v(130.1, -61.8) * mm});
            skLineSegment(sketch, "E3682", {"start": v(132.36, -61.59) * mm, "end": v(131.8, -61.63) * mm});
            skLineSegment(sketch, "E3683", {"start": v(132.3, -61.7) * mm, "end": v(132.36, -61.59) * mm});
            skLineSegment(sketch, "E3684", {"start": v(132.07, -62.05) * mm, "end": v(132.3, -61.7) * mm});
            skLineSegment(sketch, "E3685", {"start": v(131.6, -62.68) * mm, "end": v(132.07, -62.05) * mm});
            skLineSegment(sketch, "E3686", {"start": v(130.98, -63.46) * mm, "end": v(131.6, -62.68) * mm});
            skLineSegment(sketch, "E3687", {"start": v(130.22, -64.36) * mm, "end": v(130.98, -63.46) * mm});
            skLineSegment(sketch, "E3688", {"start": v(129.35, -65.35) * mm, "end": v(130.22, -64.36) * mm});
            skLineSegment(sketch, "E3689", {"start": v(128.37, -66.42) * mm, "end": v(129.35, -65.35) * mm});
            skLineSegment(sketch, "E3690", {"start": v(127.32, -67.53) * mm, "end": v(128.37, -66.42) * mm});
            skLineSegment(sketch, "E3691", {"start": v(126.49, -68.39) * mm, "end": v(127.32, -67.53) * mm});
            skLineSegment(sketch, "E3692", {"start": v(126.2, -68.67) * mm, "end": v(126.49, -68.39) * mm});
            skLineSegment(sketch, "E3693", {"start": v(113.52, -76.86) * mm, "end": v(114.23, -76.74) * mm});
            skLineSegment(sketch, "E3694", {"start": v(113.02, -76.9) * mm, "end": v(113.52, -76.86) * mm});
            skLineSegment(sketch, "E3695", {"start": v(112.8, -76.91) * mm, "end": v(113.02, -76.9) * mm});
            skLineSegment(sketch, "E3696", {"start": v(112.72, -76.9) * mm, "end": v(112.8, -76.91) * mm});
            skLineSegment(sketch, "E3697", {"start": v(112.62, -76.9) * mm, "end": v(112.72, -76.9) * mm});
            skLineSegment(sketch, "E3698", {"start": v(112.31, -76.82) * mm, "end": v(112.62, -76.9) * mm});
            skLineSegment(sketch, "E3699", {"start": v(108.94, -75.52) * mm, "end": v(109.95, -75.96) * mm});
            skLineSegment(sketch, "E3700", {"start": v(109.95, -75.96) * mm, "end": v(110.88, -76.33) * mm});
            skLineSegment(sketch, "E3701", {"start": v(110.88, -76.33) * mm, "end": v(111.68, -76.62) * mm});
            skLineSegment(sketch, "E3702", {"start": v(111.68, -76.62) * mm, "end": v(112.31, -76.82) * mm});
            skLineSegment(sketch, "E3703", {"start": v(114.23, -76.74) * mm, "end": v(115.12, -76.5) * mm});
            skLineSegment(sketch, "E3704", {"start": v(115.12, -76.5) * mm, "end": v(116.18, -76.1) * mm});
            skLineSegment(sketch, "E3705", {"start": v(116.18, -76.1) * mm, "end": v(117.42, -75.5) * mm});
            skLineSegment(sketch, "E3706", {"start": v(117.42, -75.5) * mm, "end": v(118.8, -74.7) * mm});
            skLineSegment(sketch, "E3707", {"start": v(118.8, -74.7) * mm, "end": v(119.98, -73.9) * mm});
            skLineSegment(sketch, "E3708", {"start": v(119.98, -73.9) * mm, "end": v(120.35, -73.63) * mm});
            skLineSegment(sketch, "E3709", {"start": v(120.35, -73.63) * mm, "end": v(120.7, -73.36) * mm});
            skLineSegment(sketch, "E3710", {"start": v(120.7, -73.36) * mm, "end": v(121.78, -72.53) * mm});
            skLineSegment(sketch, "E3711", {"start": v(121.78, -72.53) * mm, "end": v(123.27, -71.32) * mm});
            skLineSegment(sketch, "E3712", {"start": v(123.27, -71.32) * mm, "end": v(124.77, -70.03) * mm});
            skLineSegment(sketch, "E3713", {"start": v(124.77, -70.03) * mm, "end": v(125.86, -69.02) * mm});
            skLineSegment(sketch, "E3714", {"start": v(125.86, -69.02) * mm, "end": v(126.2, -68.67) * mm});
            skLineSegment(sketch, "E3715", {"start": v(104.1, -66) * mm, "end": v(103.14, -66.18) * mm});
            skLineSegment(sketch, "E3716", {"start": v(103.14, -66.18) * mm, "end": v(102.53, -66.3) * mm});
            skLineSegment(sketch, "E3717", {"start": v(102.53, -66.3) * mm, "end": v(102.32, -66.35) * mm});
            skLineSegment(sketch, "E3718", {"start": v(102.32, -66.35) * mm, "end": v(122.21, -65.26) * mm});
            skLineSegment(sketch, "E3719", {"start": v(122.21, -65.26) * mm, "end": v(122.1, -65.39) * mm});
            skLineSegment(sketch, "E3720", {"start": v(122.1, -65.39) * mm, "end": v(121.82, -65.73) * mm});
            skLineSegment(sketch, "E3721", {"start": v(121.82, -65.73) * mm, "end": v(121.36, -66.24) * mm});
            skLineSegment(sketch, "E3722", {"start": v(121.36, -66.24) * mm, "end": v(120.75, -66.9) * mm});
            skLineSegment(sketch, "E3723", {"start": v(120.75, -66.9) * mm, "end": v(120.02, -67.64) * mm});
            skLineSegment(sketch, "E3724", {"start": v(120.02, -67.64) * mm, "end": v(119.2, -68.44) * mm});
            skLineSegment(sketch, "E3725", {"start": v(119.2, -68.44) * mm, "end": v(118.28, -69.25) * mm});
            skLineSegment(sketch, "E3726", {"start": v(118.28, -69.25) * mm, "end": v(117.57, -69.84) * mm});
            skLineSegment(sketch, "E3727", {"start": v(117.57, -69.84) * mm, "end": v(117.32, -70.03) * mm});
            skLineSegment(sketch, "E3728", {"start": v(117.32, -70.03) * mm, "end": v(116.97, -70.3) * mm});
            skLineSegment(sketch, "E3729", {"start": v(116.97, -70.3) * mm, "end": v(115.88, -71.02) * mm});
            skLineSegment(sketch, "E3730", {"start": v(115.88, -71.02) * mm, "end": v(114.54, -71.73) * mm});
            skLineSegment(sketch, "E3731", {"start": v(114.54, -71.73) * mm, "end": v(113.3, -72.19) * mm});
            skLineSegment(sketch, "E3732", {"start": v(113.3, -72.19) * mm, "end": v(112.48, -72.38) * mm});
            skLineSegment(sketch, "E3733", {"start": v(112.48, -72.38) * mm, "end": v(112.2, -72.42) * mm});
            skLineSegment(sketch, "E3734", {"start": v(112.2, -72.42) * mm, "end": v(112, -72.44) * mm});
            skLineSegment(sketch, "E3735", {"start": v(112, -72.44) * mm, "end": v(111.39, -72.47) * mm});
            skLineSegment(sketch, "E3736", {"start": v(111.39, -72.47) * mm, "end": v(110.38, -72.41) * mm});
            skLineSegment(sketch, "E3737", {"start": v(110.38, -72.41) * mm, "end": v(109.15, -72.15) * mm});
            skLineSegment(sketch, "E3738", {"start": v(109.15, -72.15) * mm, "end": v(108.03, -71.77) * mm});
            skLineSegment(sketch, "E3739", {"start": v(108.03, -71.77) * mm, "end": v(107.67, -71.61) * mm});
            skLineSegment(sketch, "E3740", {"start": v(107.67, -71.61) * mm, "end": v(107.24, -71.43) * mm});
            skLineSegment(sketch, "E3741", {"start": v(107.24, -71.43) * mm, "end": v(105.97, -70.82) * mm});
            skLineSegment(sketch, "E3742", {"start": v(105.97, -70.82) * mm, "end": v(104.4, -70) * mm});
            skLineSegment(sketch, "E3743", {"start": v(104.4, -70) * mm, "end": v(102.95, -69.16) * mm});
            skLineSegment(sketch, "E3744", {"start": v(102.95, -69.16) * mm, "end": v(101.67, -68.35) * mm});
            skLineSegment(sketch, "E3745", {"start": v(101.67, -68.35) * mm, "end": v(100.56, -67.6) * mm});
            skLineSegment(sketch, "E3746", {"start": v(100.56, -67.6) * mm, "end": v(99.66, -66.94) * mm});
            skLineSegment(sketch, "E3747", {"start": v(99.66, -66.94) * mm, "end": v(98.97, -66.4) * mm});
            skLineSegment(sketch, "E3748", {"start": v(98.97, -66.4) * mm, "end": v(98.63, -66.13) * mm});
            skLineSegment(sketch, "E3749", {"start": v(98.63, -66.13) * mm, "end": v(98.53, -66.03) * mm});
            skLineSegment(sketch, "E3750", {"start": v(98.53, -66.03) * mm, "end": v(98.93, -65.9) * mm});
            skLineSegment(sketch, "E3751", {"start": v(98.93, -65.9) * mm, "end": v(100.14, -65.56) * mm});
            skLineSegment(sketch, "E3752", {"start": v(100.14, -65.56) * mm, "end": v(101.99, -65.09) * mm});
            skLineSegment(sketch, "E3753", {"start": v(101.99, -65.09) * mm, "end": v(104.03, -64.61) * mm});
            skLineSegment(sketch, "E3754", {"start": v(104.03, -64.61) * mm, "end": v(106.25, -64.14) * mm});
            skLineSegment(sketch, "E3755", {"start": v(106.25, -64.14) * mm, "end": v(108.59, -63.68) * mm});
            skLineSegment(sketch, "E3756", {"start": v(108.59, -63.68) * mm, "end": v(111.03, -63.23) * mm});
            skLineSegment(sketch, "E3757", {"start": v(111.03, -63.23) * mm, "end": v(113.54, -62.79) * mm});
            skLineSegment(sketch, "E3758", {"start": v(113.54, -62.79) * mm, "end": v(116.08, -62.37) * mm});
            skLineSegment(sketch, "E3759", {"start": v(116.08, -62.37) * mm, "end": v(118.62, -61.97) * mm});
            skLineSegment(sketch, "E3760", {"start": v(118.62, -61.97) * mm, "end": v(121.12, -61.6) * mm});
            skLineSegment(sketch, "E3761", {"start": v(121.12, -61.6) * mm, "end": v(123.55, -61.25) * mm});
            skLineSegment(sketch, "E3762", {"start": v(123.55, -61.25) * mm, "end": v(125.88, -60.94) * mm});
            skSolve(sketch);
        }
        {
            var Q0;
            Q0 = qSketchRegion(id + "F4", true);
            extrude(context, id + "F5", {"entities" : qUnion([Q0]), "operationType" : NewBodyOperationType.REMOVE, "oppositeDirection" : true, "depth" : 1 * mm, "offsetDistance" : 25 * mm});
        }
        {
            var Q0;
            {var subQ0=sQuery(id+"F0.wireOp",EDGE,"E30.filletArc");var subQ1=sQuery(id+"F0.wireOp",EDGE,"E29.filletArc");var subQ2=sQuery(id+"F0.wireOp",EDGE,"E28.filletArc");var subQ3=sQuery(id+"F0.wireOp",EDGE,"E27.filletArc");var subQ4=sQuery(id+"F0.wireOp",EDGE,"E26.filletArc");var subQ5=sQuery(id+"F0.wireOp",EDGE,"E25.filletArc");var subQ6=sQuery(id+"F0.wireOp",EDGE,"E24.filletArc");var subQ7=sQuery(id+"F0.wireOp",EDGE,"E23.filletArc");var subQ8=sQuery(id+"F0.wireOp",EDGE,"E22");var subQ9=sQuery(id+"F0.wireOp",EDGE,"E21");var subQ10=sQuery(id+"F0.wireOp",EDGE,"E20");var subQ11=sQuery(id+"F0.wireOp",EDGE,"E19");var subQ12=sQuery(id+"F0.wireOp",EDGE,"E16");var subQ13=sQuery(id+"F0.wireOp",EDGE,"E15");var subQ14=sQuery(id+"F0.wireOp",EDGE,"E14");var subQ15=sQuery(id+"F0.wireOp",EDGE,"E13");var subQ16=sQuery(id+"F0.wireOp",EDGE,"E12");var subQ17=sQuery(id+"F0.wireOp",EDGE,"E10");var subQ18=sQuery(id+"F0.wireOp",EDGE,"E9");var subQ19=sQuery(id+"F0.wireOp",EDGE,"E8");var subQ20=sQuery(id+"F0.wireOp",EDGE,"E6");var subQ21=sQuery(id+"F0.wireOp",EDGE,"E5");var subQ22=sQuery(id+"F0.wireOp",EDGE,"E4");var subQ23=sQuery(id+"F0.wireOp",EDGE,"E2");var subQ24=sQuery(id+"F0.wireOp",EDGE,"E1");var subQ25=sQuery(id+"F0.wireOp",EDGE,"E0");var subQ26=sQuery(id+"F0.wireOp",EDGE,"E18");Q0=makeQuery(id+"F5.boolean.opBoolean","SPLIT",FACE,{"disambiguationData":[TD([makeQuery(id+"F1.opExtrude","SWEPT_FACE",FACE,{"disambiguationData":[OSD([subQ25])]})])],"derivedFrom":makeQuery(id+"F1.opExtrude","CAP_FACE",FACE,{"disambiguationData":[OSD([subQ25,subQ24,subQ23,subQ22,subQ21,subQ20,subQ19,subQ18,subQ17,subQ16,subQ15,subQ14,subQ13,subQ12,subQ26,subQ11,subQ10,subQ9,subQ8,subQ7,subQ6,subQ5,subQ4,subQ3,subQ2,subQ1,subQ0])],"isStart":false})});}
            var sketch = newSketch(context, id + "F6", { "sketchPlane" : qUnion([Q0])});
            skLineSegment(sketch, "E3763", {"start": v(21.48, -70.4) * mm, "end": v(21.73, -70.68) * mm});
            skLineSegment(sketch, "E3764", {"start": v(20.76, -69.51) * mm, "end": v(21.48, -70.4) * mm});
            skLineSegment(sketch, "E3765", {"start": v(19.96, -68.43) * mm, "end": v(20.76, -69.51) * mm});
            skLineSegment(sketch, "E3766", {"start": v(19.4, -67.54) * mm, "end": v(19.96, -68.43) * mm});
            skLineSegment(sketch, "E3767", {"start": v(19.15, -67.07) * mm, "end": v(19.4, -67.54) * mm});
            skLineSegment(sketch, "E3768", {"start": v(19.1, -66.92) * mm, "end": v(19.15, -67.07) * mm});
            skLineSegment(sketch, "E3769", {"start": v(19.08, -66.8) * mm, "end": v(19.1, -66.92) * mm});
            skLineSegment(sketch, "E3770", {"start": v(19, -66.43) * mm, "end": v(19.08, -66.8) * mm});
            skLineSegment(sketch, "E3771", {"start": v(18.92, -65.72) * mm, "end": v(19, -66.43) * mm});
            skLineSegment(sketch, "E3772", {"start": v(18.87, -64.81) * mm, "end": v(18.92, -65.72) * mm});
            skLineSegment(sketch, "E3773", {"start": v(18.86, -64.01) * mm, "end": v(18.87, -64.81) * mm});
            skLineSegment(sketch, "E3774", {"start": v(18.87, -63.75) * mm, "end": v(18.86, -64.01) * mm});
            skLineSegment(sketch, "E3775", {"start": v(18.87, -63.53) * mm, "end": v(18.87, -63.75) * mm});
            skLineSegment(sketch, "E3776", {"start": v(18.9, -62.86) * mm, "end": v(18.87, -63.53) * mm});
            skLineSegment(sketch, "E3777", {"start": v(18.96, -61.97) * mm, "end": v(18.9, -62.86) * mm});
            skLineSegment(sketch, "E3778", {"start": v(19.03, -61.1) * mm, "end": v(18.96, -61.97) * mm});
            skLineSegment(sketch, "E3779", {"start": v(19.1, -60.32) * mm, "end": v(19.03, -61.1) * mm});
            skLineSegment(sketch, "E3780", {"start": v(19.16, -59.63) * mm, "end": v(19.1, -60.32) * mm});
            skLineSegment(sketch, "E3781", {"start": v(19.22, -59.1) * mm, "end": v(19.16, -59.63) * mm});
            skLineSegment(sketch, "E3782", {"start": v(19.26, -58.75) * mm, "end": v(19.22, -59.1) * mm});
            skLineSegment(sketch, "E3783", {"start": v(19.27, -58.62) * mm, "end": v(19.26, -58.75) * mm});
            skLineSegment(sketch, "E3784", {"start": v(19.34, -58.83) * mm, "end": v(19.27, -58.62) * mm});
            skLineSegment(sketch, "E3785", {"start": v(19.53, -59.4) * mm, "end": v(19.34, -58.83) * mm});
            skLineSegment(sketch, "E3786", {"start": v(19.81, -60.27) * mm, "end": v(19.53, -59.4) * mm});
            skLineSegment(sketch, "E3787", {"start": v(20.19, -61.39) * mm, "end": v(19.81, -60.27) * mm});
            skLineSegment(sketch, "E3788", {"start": v(20.63, -62.68) * mm, "end": v(20.19, -61.39) * mm});
            skLineSegment(sketch, "E3789", {"start": v(21.11, -64.08) * mm, "end": v(20.63, -62.68) * mm});
            skLineSegment(sketch, "E3790", {"start": v(21.63, -65.54) * mm, "end": v(21.11, -64.08) * mm});
            skLineSegment(sketch, "E3791", {"start": v(22.02, -66.62) * mm, "end": v(21.63, -65.54) * mm});
            skLineSegment(sketch, "E3792", {"start": v(22.15, -66.98) * mm, "end": v(22.02, -66.62) * mm});
            skLineSegment(sketch, "E3793", {"start": v(22.28, -67.33) * mm, "end": v(22.15, -66.98) * mm});
            skLineSegment(sketch, "E3794", {"start": v(22.69, -68.4) * mm, "end": v(22.28, -67.33) * mm});
            skLineSegment(sketch, "E3795", {"start": v(23.2, -69.71) * mm, "end": v(22.69, -68.4) * mm});
            skLineSegment(sketch, "E3796", {"start": v(23.68, -70.9) * mm, "end": v(23.2, -69.71) * mm});
            skLineSegment(sketch, "E3797", {"start": v(24.1, -71.93) * mm, "end": v(23.68, -70.9) * mm});
            skLineSegment(sketch, "E3798", {"start": v(24.46, -72.78) * mm, "end": v(24.1, -71.93) * mm});
            skLineSegment(sketch, "E3799", {"start": v(24.74, -73.41) * mm, "end": v(24.46, -72.78) * mm});
            skLineSegment(sketch, "E3800", {"start": v(24.91, -73.82) * mm, "end": v(24.74, -73.41) * mm});
            skLineSegment(sketch, "E3801", {"start": v(24.97, -73.96) * mm, "end": v(24.91, -73.82) * mm});
            skLineSegment(sketch, "E3802", {"start": v(24.9, -73.88) * mm, "end": v(24.97, -73.96) * mm});
            skLineSegment(sketch, "E3803", {"start": v(24.67, -73.68) * mm, "end": v(24.9, -73.88) * mm});
            skLineSegment(sketch, "E3804", {"start": v(24.33, -73.36) * mm, "end": v(24.67, -73.68) * mm});
            skLineSegment(sketch, "E3805", {"start": v(23.9, -72.94) * mm, "end": v(24.33, -73.36) * mm});
            skLineSegment(sketch, "E3806", {"start": v(23.4, -72.45) * mm, "end": v(23.9, -72.94) * mm});
            skLineSegment(sketch, "E3807", {"start": v(22.85, -71.9) * mm, "end": v(23.4, -72.45) * mm});
            skLineSegment(sketch, "E3808", {"start": v(22.29, -71.3) * mm, "end": v(22.85, -71.9) * mm});
            skLineSegment(sketch, "E3809", {"start": v(21.87, -70.84) * mm, "end": v(22.29, -71.3) * mm});
            skLineSegment(sketch, "E3810", {"start": v(21.73, -70.68) * mm, "end": v(21.87, -70.84) * mm});
            skLineSegment(sketch, "E3811", {"start": v(41.67, -71.2) * mm, "end": v(42.26, -71) * mm});
            skLineSegment(sketch, "E3812", {"start": v(39.9, -71.77) * mm, "end": v(41.67, -71.2) * mm});
            skLineSegment(sketch, "E3813", {"start": v(37.63, -72.5) * mm, "end": v(39.9, -71.77) * mm});
            skLineSegment(sketch, "E3814", {"start": v(35.53, -73.18) * mm, "end": v(37.63, -72.5) * mm});
            skLineSegment(sketch, "E3815", {"start": v(33.63, -73.84) * mm, "end": v(35.53, -73.18) * mm});
            skLineSegment(sketch, "E3816", {"start": v(32, -74.5) * mm, "end": v(33.63, -73.84) * mm});
            skLineSegment(sketch, "E3817", {"start": v(30.68, -75.17) * mm, "end": v(32, -74.5) * mm});
            skLineSegment(sketch, "E3818", {"start": v(29.73, -75.86) * mm, "end": v(30.68, -75.17) * mm});
            skLineSegment(sketch, "E3819", {"start": v(29.28, -76.38) * mm, "end": v(29.73, -75.86) * mm});
            skLineSegment(sketch, "E3820", {"start": v(29.2, -76.59) * mm, "end": v(29.28, -76.38) * mm});
            skLineSegment(sketch, "E3821", {"start": v(29.15, -76.7) * mm, "end": v(29.2, -76.59) * mm});
            skLineSegment(sketch, "E3822", {"start": v(29.15, -77.08) * mm, "end": v(29.15, -76.7) * mm});
            skLineSegment(sketch, "E3823", {"start": v(29.25, -77.87) * mm, "end": v(29.15, -77.08) * mm});
            skLineSegment(sketch, "E3824", {"start": v(29.47, -78.87) * mm, "end": v(29.25, -77.87) * mm});
            skLineSegment(sketch, "E3825", {"start": v(29.8, -80.02) * mm, "end": v(29.47, -78.87) * mm});
            skLineSegment(sketch, "E3826", {"start": v(30.17, -81.23) * mm, "end": v(29.8, -80.02) * mm});
            skLineSegment(sketch, "E3827", {"start": v(30.6, -82.43) * mm, "end": v(30.17, -81.23) * mm});
            skLineSegment(sketch, "E3828", {"start": v(31.02, -83.54) * mm, "end": v(30.6, -82.43) * mm});
            skLineSegment(sketch, "E3829", {"start": v(31.32, -84.26) * mm, "end": v(31.02, -83.54) * mm});
            skLineSegment(sketch, "E3830", {"start": v(31.43, -84.49) * mm, "end": v(31.32, -84.26) * mm});
            skLineSegment(sketch, "E3831", {"start": v(31.08, -84.17) * mm, "end": v(31.43, -84.49) * mm});
            skLineSegment(sketch, "E3832", {"start": v(30.1, -83.1) * mm, "end": v(31.08, -84.17) * mm});
            skLineSegment(sketch, "E3833", {"start": v(28.86, -81.4) * mm, "end": v(30.1, -83.1) * mm});
            skLineSegment(sketch, "E3834", {"start": v(27.77, -79.54) * mm, "end": v(28.86, -81.4) * mm});
            skLineSegment(sketch, "E3835", {"start": v(27.1, -78.11) * mm, "end": v(27.77, -79.54) * mm});
            skLineSegment(sketch, "E3836", {"start": v(26.93, -77.62) * mm, "end": v(27.1, -78.11) * mm});
            skLineSegment(sketch, "E3837", {"start": v(26.76, -77.16) * mm, "end": v(26.93, -77.62) * mm});
            skLineSegment(sketch, "E3838", {"start": v(26.34, -75.73) * mm, "end": v(26.76, -77.16) * mm});
            skLineSegment(sketch, "E3839", {"start": v(25.9, -73.8) * mm, "end": v(26.34, -75.73) * mm});
            skLineSegment(sketch, "E3840", {"start": v(25.58, -71.96) * mm, "end": v(25.9, -73.8) * mm});
            skLineSegment(sketch, "E3841", {"start": v(25.4, -70.72) * mm, "end": v(25.58, -71.96) * mm});
            skLineSegment(sketch, "E3842", {"start": v(25.35, -70.3) * mm, "end": v(25.4, -70.72) * mm});
            skLineSegment(sketch, "E3843", {"start": v(25.29, -69.86) * mm, "end": v(25.35, -70.3) * mm});
            skLineSegment(sketch, "E3844", {"start": v(25.12, -68.52) * mm, "end": v(25.29, -69.86) * mm});
            skLineSegment(sketch, "E3845", {"start": v(24.93, -67.16) * mm, "end": v(25.12, -68.52) * mm});
            skLineSegment(sketch, "E3846", {"start": v(24.69, -66.2) * mm, "end": v(24.93, -67.16) * mm});
            skLineSegment(sketch, "E3847", {"start": v(24.45, -65.75) * mm, "end": v(24.69, -66.2) * mm});
            skLineSegment(sketch, "E3848", {"start": v(24.33, -65.65) * mm, "end": v(24.45, -65.75) * mm});
            skLineSegment(sketch, "E3849", {"start": v(24.56, -65.74) * mm, "end": v(24.33, -65.65) * mm});
            skLineSegment(sketch, "E3850", {"start": v(25.18, -66.18) * mm, "end": v(24.56, -65.74) * mm});
            skLineSegment(sketch, "E3851", {"start": v(26.1, -67) * mm, "end": v(25.18, -66.18) * mm});
            skLineSegment(sketch, "E3852", {"start": v(27.05, -68.02) * mm, "end": v(26.1, -67) * mm});
            skLineSegment(sketch, "E3853", {"start": v(28, -69.1) * mm, "end": v(27.05, -68.02) * mm});
            skLineSegment(sketch, "E3854", {"start": v(28.92, -70.14) * mm, "end": v(28, -69.1) * mm});
            skLineSegment(sketch, "E3855", {"start": v(29.76, -71) * mm, "end": v(28.92, -70.14) * mm});
            skLineSegment(sketch, "E3856", {"start": v(30.5, -71.59) * mm, "end": v(29.76, -71) * mm});
            skLineSegment(sketch, "E3857", {"start": v(30.95, -71.79) * mm, "end": v(30.5, -71.59) * mm});
            skLineSegment(sketch, "E3858", {"start": v(31.09, -71.77) * mm, "end": v(30.95, -71.79) * mm});
            skLineSegment(sketch, "E3859", {"start": v(31.3, -71.72) * mm, "end": v(31.09, -71.77) * mm});
            skLineSegment(sketch, "E3860", {"start": v(31.92, -71.52) * mm, "end": v(31.3, -71.72) * mm});
            skLineSegment(sketch, "E3861", {"start": v(32.92, -71.17) * mm, "end": v(31.92, -71.52) * mm});
            skLineSegment(sketch, "E3862", {"start": v(34.07, -70.73) * mm, "end": v(32.92, -71.17) * mm});
            skLineSegment(sketch, "E3863", {"start": v(35.34, -70.23) * mm, "end": v(34.07, -70.73) * mm});
            skLineSegment(sketch, "E3864", {"start": v(36.7, -69.67) * mm, "end": v(35.34, -70.23) * mm});
            skLineSegment(sketch, "E3865", {"start": v(38.12, -69.06) * mm, "end": v(36.7, -69.67) * mm});
            skLineSegment(sketch, "E3866", {"start": v(39.57, -68.43) * mm, "end": v(38.12, -69.06) * mm});
            skLineSegment(sketch, "E3867", {"start": v(40.67, -67.94) * mm, "end": v(39.57, -68.43) * mm});
            skLineSegment(sketch, "E3868", {"start": v(41.04, -67.78) * mm, "end": v(40.67, -67.94) * mm});
            skLineSegment(sketch, "E3869", {"start": v(41.44, -67.6) * mm, "end": v(41.04, -67.78) * mm});
            skLineSegment(sketch, "E3870", {"start": v(42.63, -67.06) * mm, "end": v(41.44, -67.6) * mm});
            skLineSegment(sketch, "E3871", {"start": v(44.16, -66.35) * mm, "end": v(42.63, -67.06) * mm});
            skLineSegment(sketch, "E3872", {"start": v(45.6, -65.68) * mm, "end": v(44.16, -66.35) * mm});
            skLineSegment(sketch, "E3873", {"start": v(46.9, -65.06) * mm, "end": v(45.6, -65.68) * mm});
            skLineSegment(sketch, "E3874", {"start": v(65.28, -72.55) * mm, "end": v(67.3, -72.31) * mm});
            skLineSegment(sketch, "E3875", {"start": v(63.09, -72.82) * mm, "end": v(65.28, -72.55) * mm});
            skLineSegment(sketch, "E3876", {"start": v(73.77, -69.59) * mm, "end": v(73.85, -69.35) * mm});
            skLineSegment(sketch, "E3877", {"start": v(73.85, -69.35) * mm, "end": v(73.75, -69.35) * mm});
            skLineSegment(sketch, "E3878", {"start": v(73.75, -69.35) * mm, "end": v(73.45, -69.35) * mm});
            skLineSegment(sketch, "E3879", {"start": v(73.45, -69.35) * mm, "end": v(72.8, -69.37) * mm});
            skLineSegment(sketch, "E3880", {"start": v(72.8, -69.37) * mm, "end": v(71.95, -69.4) * mm});
            skLineSegment(sketch, "E3881", {"start": v(71.95, -69.4) * mm, "end": v(70.9, -69.46) * mm});
            skLineSegment(sketch, "E3882", {"start": v(70.9, -69.46) * mm, "end": v(69.68, -69.54) * mm});
            skLineSegment(sketch, "E3883", {"start": v(69.68, -69.54) * mm, "end": v(68.29, -69.64) * mm});
            skLineSegment(sketch, "E3884", {"start": v(68.29, -69.64) * mm, "end": v(66.76, -69.76) * mm});
            skLineSegment(sketch, "E3885", {"start": v(66.76, -69.76) * mm, "end": v(65.52, -69.88) * mm});
            skLineSegment(sketch, "E3886", {"start": v(65.52, -69.88) * mm, "end": v(65.1, -69.92) * mm});
            skLineSegment(sketch, "E3887", {"start": v(65.1, -69.92) * mm, "end": v(64.36, -69.99) * mm});
            skLineSegment(sketch, "E3888", {"start": v(64.36, -69.99) * mm, "end": v(62.12, -70.23) * mm});
            skLineSegment(sketch, "E3889", {"start": v(62.12, -70.23) * mm, "end": v(58.92, -70.61) * mm});
            skLineSegment(sketch, "E3890", {"start": v(58.92, -70.61) * mm, "end": v(55.56, -71.08) * mm});
            skLineSegment(sketch, "E3891", {"start": v(55.56, -71.08) * mm, "end": v(52.97, -71.47) * mm});
            skLineSegment(sketch, "E3892", {"start": v(52.97, -71.47) * mm, "end": v(52.11, -71.61) * mm});
            skLineSegment(sketch, "E3893", {"start": v(52.11, -71.61) * mm, "end": v(51.18, -71.76) * mm});
            skLineSegment(sketch, "E3894", {"start": v(51.18, -71.76) * mm, "end": v(46.73, -72.57) * mm});
            skLineSegment(sketch, "E3895", {"start": v(46.73, -72.57) * mm, "end": v(42.5, -73.43) * mm});
            skLineSegment(sketch, "E3896", {"start": v(42.5, -73.43) * mm, "end": v(41.66, -73.6) * mm});
            skLineSegment(sketch, "E3897", {"start": v(42.26, -71) * mm, "end": v(42.46, -70.94) * mm});
            skLineSegment(sketch, "E3898", {"start": v(42.46, -70.94) * mm, "end": v(43.07, -70.74) * mm});
            skLineSegment(sketch, "E3899", {"start": v(43.07, -70.74) * mm, "end": v(44.16, -70.4) * mm});
            skLineSegment(sketch, "E3900", {"start": v(44.16, -70.4) * mm, "end": v(45.5, -69.99) * mm});
            skLineSegment(sketch, "E3901", {"start": v(45.5, -69.99) * mm, "end": v(47.06, -69.53) * mm});
            skLineSegment(sketch, "E3902", {"start": v(47.06, -69.53) * mm, "end": v(48.82, -69.03) * mm});
            skLineSegment(sketch, "E3903", {"start": v(48.82, -69.03) * mm, "end": v(50.76, -68.53) * mm});
            skLineSegment(sketch, "E3904", {"start": v(50.76, -68.53) * mm, "end": v(52.84, -68.02) * mm});
            skLineSegment(sketch, "E3905", {"start": v(52.84, -68.02) * mm, "end": v(55.06, -67.52) * mm});
            skLineSegment(sketch, "E3906", {"start": v(55.06, -67.52) * mm, "end": v(57.37, -67.06) * mm});
            skLineSegment(sketch, "E3907", {"start": v(57.37, -67.06) * mm, "end": v(59.75, -66.64) * mm});
            skLineSegment(sketch, "E3908", {"start": v(59.75, -66.64) * mm, "end": v(62.18, -66.29) * mm});
            skLineSegment(sketch, "E3909", {"start": v(62.18, -66.29) * mm, "end": v(64.64, -66.01) * mm});
            skLineSegment(sketch, "E3910", {"start": v(64.64, -66.01) * mm, "end": v(67.1, -65.83) * mm});
            skLineSegment(sketch, "E3911", {"start": v(67.1, -65.83) * mm, "end": v(69.52, -65.76) * mm});
            skLineSegment(sketch, "E3912", {"start": v(69.52, -65.76) * mm, "end": v(71.89, -65.82) * mm});
            skLineSegment(sketch, "E3913", {"start": v(71.89, -65.82) * mm, "end": v(73.61, -65.95) * mm});
            skLineSegment(sketch, "E3914", {"start": v(73.61, -65.95) * mm, "end": v(74.18, -66.02) * mm});
            skLineSegment(sketch, "E3915", {"start": v(74.18, -66.02) * mm, "end": v(73.8, -65.82) * mm});
            skLineSegment(sketch, "E3916", {"start": v(73.8, -65.82) * mm, "end": v(72.6, -65.26) * mm});
            skLineSegment(sketch, "E3917", {"start": v(72.6, -65.26) * mm, "end": v(71, -64.6) * mm});
            skLineSegment(sketch, "E3918", {"start": v(71, -64.6) * mm, "end": v(69.39, -64.04) * mm});
            skLineSegment(sketch, "E3919", {"start": v(69.39, -64.04) * mm, "end": v(67.79, -63.55) * mm});
            skLineSegment(sketch, "E3920", {"start": v(67.79, -63.55) * mm, "end": v(66.22, -63.14) * mm});
            skLineSegment(sketch, "E3921", {"start": v(66.22, -63.14) * mm, "end": v(64.69, -62.8) * mm});
            skLineSegment(sketch, "E3922", {"start": v(64.69, -62.8) * mm, "end": v(63.22, -62.53) * mm});
            skLineSegment(sketch, "E3923", {"start": v(63.22, -62.53) * mm, "end": v(61.82, -62.3) * mm});
            skLineSegment(sketch, "E3924", {"start": v(61.82, -62.3) * mm, "end": v(60.51, -62.14) * mm});
            skLineSegment(sketch, "E3925", {"start": v(60.51, -62.14) * mm, "end": v(59.32, -62.02) * mm});
            skLineSegment(sketch, "E3926", {"start": v(52.56, -62.62) * mm, "end": v(51.81, -62.88) * mm});
            skLineSegment(sketch, "E3927", {"start": v(51.81, -62.88) * mm, "end": v(51.13, -63.13) * mm});
            skLineSegment(sketch, "E3928", {"start": v(51.13, -63.13) * mm, "end": v(50.56, -63.35) * mm});
            skLineSegment(sketch, "E3929", {"start": v(50.56, -63.35) * mm, "end": v(50.27, -63.47) * mm});
            skLineSegment(sketch, "E3930", {"start": v(32.62, -75.83) * mm, "end": v(31.5, -76.16) * mm});
            skLineSegment(sketch, "E3931", {"start": v(31.5, -76.16) * mm, "end": v(30.69, -76.4) * mm});
            skLineSegment(sketch, "E3932", {"start": v(30.69, -76.4) * mm, "end": v(30.34, -76.52) * mm});
            skLineSegment(sketch, "E3933", {"start": v(39.52, -74.1) * mm, "end": v(37.5, -74.57) * mm});
            skLineSegment(sketch, "E3934", {"start": v(50.06, -63.57) * mm, "end": v(49.72, -63.73) * mm});
            skLineSegment(sketch, "E3935", {"start": v(30.34, -76.52) * mm, "end": v(30.22, -76.57) * mm});
            skLineSegment(sketch, "E3936", {"start": v(37.5, -74.57) * mm, "end": v(35.66, -75.03) * mm});
            skLineSegment(sketch, "E3937", {"start": v(49.72, -63.73) * mm, "end": v(49, -64.07) * mm});
            skLineSegment(sketch, "E3938", {"start": v(30.22, -76.57) * mm, "end": v(30.4, -76.8) * mm});
            skLineSegment(sketch, "E3939", {"start": v(35.66, -75.03) * mm, "end": v(34.02, -75.46) * mm});
            skLineSegment(sketch, "E3940", {"start": v(49, -64.07) * mm, "end": v(48.05, -64.52) * mm});
            skLineSegment(sketch, "E3941", {"start": v(30.4, -76.8) * mm, "end": v(31.02, -77.45) * mm});
            skLineSegment(sketch, "E3942", {"start": v(34.02, -75.46) * mm, "end": v(32.62, -75.83) * mm});
            skLineSegment(sketch, "E3943", {"start": v(48.05, -64.52) * mm, "end": v(46.9, -65.06) * mm});
            skLineSegment(sketch, "E3944", {"start": v(41.66, -73.6) * mm, "end": v(41.13, -73.73) * mm});
            skLineSegment(sketch, "E3945", {"start": v(31.02, -77.45) * mm, "end": v(32.14, -78.5) * mm});
            skLineSegment(sketch, "E3946", {"start": v(32.14, -78.5) * mm, "end": v(33.55, -79.66) * mm});
            skLineSegment(sketch, "E3947", {"start": v(43.01, -85.88) * mm, "end": v(43.26, -86.02) * mm});
            skLineSegment(sketch, "E3948", {"start": v(43.26, -86.02) * mm, "end": v(44.02, -86.4) * mm});
            skLineSegment(sketch, "E3949", {"start": v(44.02, -86.4) * mm, "end": v(45.08, -86.92) * mm});
            skLineSegment(sketch, "E3950", {"start": v(45.08, -86.92) * mm, "end": v(46.14, -87.4) * mm});
            skLineSegment(sketch, "E3951", {"start": v(42.5, -85.6) * mm, "end": v(43.01, -85.88) * mm});
            skLineSegment(sketch, "E3952", {"start": v(40.97, -84.73) * mm, "end": v(42.5, -85.6) * mm});
            skLineSegment(sketch, "E3953", {"start": v(38.95, -83.49) * mm, "end": v(40.97, -84.73) * mm});
            skLineSegment(sketch, "E3954", {"start": v(37, -82.2) * mm, "end": v(38.95, -83.49) * mm});
            skLineSegment(sketch, "E3955", {"start": v(35.19, -80.91) * mm, "end": v(37, -82.2) * mm});
            skLineSegment(sketch, "E3956", {"start": v(33.55, -79.66) * mm, "end": v(35.19, -80.91) * mm});
            skLineSegment(sketch, "E3957", {"start": v(50.17, -63.52) * mm, "end": v(50.06, -63.57) * mm});
            skLineSegment(sketch, "E3958", {"start": v(41.13, -73.73) * mm, "end": v(39.52, -74.1) * mm});
            skLineSegment(sketch, "E3959", {"start": v(53.34, -62.36) * mm, "end": v(52.56, -62.62) * mm});
            skLineSegment(sketch, "E3960", {"start": v(50.27, -63.47) * mm, "end": v(50.17, -63.52) * mm});
            skLineSegment(sketch, "E3961", {"start": v(54.08, -62.14) * mm, "end": v(53.34, -62.36) * mm});
            skLineSegment(sketch, "E3962", {"start": v(54.75, -61.97) * mm, "end": v(54.08, -62.14) * mm});
            skLineSegment(sketch, "E3963", {"start": v(55.15, -61.88) * mm, "end": v(54.75, -61.97) * mm});
            skLineSegment(sketch, "E3964", {"start": v(55.29, -61.86) * mm, "end": v(55.15, -61.88) * mm});
            skLineSegment(sketch, "E3965", {"start": v(55.34, -61.86) * mm, "end": v(55.29, -61.86) * mm});
            skLineSegment(sketch, "E3966", {"start": v(55.5, -61.85) * mm, "end": v(55.34, -61.86) * mm});
            skLineSegment(sketch, "E3967", {"start": v(55.92, -61.84) * mm, "end": v(55.5, -61.85) * mm});
            skLineSegment(sketch, "E3968", {"start": v(56.53, -61.85) * mm, "end": v(55.92, -61.84) * mm});
            skLineSegment(sketch, "E3969", {"start": v(57.3, -61.88) * mm, "end": v(56.53, -61.85) * mm});
            skLineSegment(sketch, "E3970", {"start": v(58.24, -61.93) * mm, "end": v(57.3, -61.88) * mm});
            skLineSegment(sketch, "E3971", {"start": v(59.32, -62.02) * mm, "end": v(58.24, -61.93) * mm});
            skLineSegment(sketch, "E3972", {"start": v(73.4, -70.26) * mm, "end": v(73.77, -69.59) * mm});
            skLineSegment(sketch, "E3973", {"start": v(72.71, -71.08) * mm, "end": v(73.4, -70.26) * mm});
            skLineSegment(sketch, "E3974", {"start": v(71.8, -71.69) * mm, "end": v(72.71, -71.08) * mm});
            skLineSegment(sketch, "E3975", {"start": v(70.99, -71.96) * mm, "end": v(71.8, -71.69) * mm});
            skLineSegment(sketch, "E3976", {"start": v(70.7, -71.98) * mm, "end": v(70.99, -71.96) * mm});
            skLineSegment(sketch, "E3977", {"start": v(70.31, -72.01) * mm, "end": v(70.7, -71.98) * mm});
            skLineSegment(sketch, "E3978", {"start": v(69.13, -72.12) * mm, "end": v(70.31, -72.01) * mm});
            skLineSegment(sketch, "E3979", {"start": v(67.3, -72.31) * mm, "end": v(69.13, -72.12) * mm});
            skLineSegment(sketch, "E3980", {"start": v(42.58, -77.62) * mm, "end": v(41.3, -77.87) * mm});
            skLineSegment(sketch, "E3981", {"start": v(44.15, -77.31) * mm, "end": v(42.58, -77.62) * mm});
            skLineSegment(sketch, "E3982", {"start": v(45.96, -76.97) * mm, "end": v(44.15, -77.31) * mm});
            skLineSegment(sketch, "E3983", {"start": v(47.98, -76.6) * mm, "end": v(45.96, -76.97) * mm});
            skLineSegment(sketch, "E3984", {"start": v(50.18, -76.2) * mm, "end": v(47.98, -76.6) * mm});
            skLineSegment(sketch, "E3985", {"start": v(52.51, -75.8) * mm, "end": v(50.18, -76.2) * mm});
            skLineSegment(sketch, "E3986", {"start": v(54.94, -75.39) * mm, "end": v(52.51, -75.8) * mm});
            skLineSegment(sketch, "E3987", {"start": v(57.44, -74.99) * mm, "end": v(54.94, -75.39) * mm});
            skLineSegment(sketch, "E3988", {"start": v(59.96, -74.6) * mm, "end": v(57.44, -74.99) * mm});
            skLineSegment(sketch, "E3989", {"start": v(62.47, -74.26) * mm, "end": v(59.96, -74.6) * mm});
            skLineSegment(sketch, "E3990", {"start": v(64.93, -73.94) * mm, "end": v(62.47, -74.26) * mm});
            skLineSegment(sketch, "E3991", {"start": v(67.31, -73.68) * mm, "end": v(64.93, -73.94) * mm});
            skLineSegment(sketch, "E3992", {"start": v(69, -73.52) * mm, "end": v(67.31, -73.68) * mm});
            skLineSegment(sketch, "E3993", {"start": v(69.57, -73.47) * mm, "end": v(69, -73.52) * mm});
            skLineSegment(sketch, "E3994", {"start": v(69.5, -73.59) * mm, "end": v(69.57, -73.47) * mm});
            skLineSegment(sketch, "E3995", {"start": v(69.27, -73.93) * mm, "end": v(69.5, -73.59) * mm});
            skLineSegment(sketch, "E3996", {"start": v(68.8, -74.56) * mm, "end": v(69.27, -73.93) * mm});
            skLineSegment(sketch, "E3997", {"start": v(68.18, -75.34) * mm, "end": v(68.8, -74.56) * mm});
            skLineSegment(sketch, "E3998", {"start": v(67.43, -76.24) * mm, "end": v(68.18, -75.34) * mm});
            skLineSegment(sketch, "E3999", {"start": v(66.55, -77.23) * mm, "end": v(67.43, -76.24) * mm});
            skLineSegment(sketch, "E4000", {"start": v(65.58, -78.3) * mm, "end": v(66.55, -77.23) * mm});
            skLineSegment(sketch, "E4001", {"start": v(64.52, -79.41) * mm, "end": v(65.58, -78.3) * mm});
            skLineSegment(sketch, "E4002", {"start": v(63.7, -80.27) * mm, "end": v(64.52, -79.41) * mm});
            skLineSegment(sketch, "E4003", {"start": v(63.41, -80.55) * mm, "end": v(63.7, -80.27) * mm});
            skLineSegment(sketch, "E4004", {"start": v(50.73, -88.75) * mm, "end": v(51.43, -88.62) * mm});
            skLineSegment(sketch, "E4005", {"start": v(50.22, -88.8) * mm, "end": v(50.73, -88.75) * mm});
            skLineSegment(sketch, "E4006", {"start": v(50, -88.8) * mm, "end": v(50.22, -88.8) * mm});
            skLineSegment(sketch, "E4007", {"start": v(49.93, -88.79) * mm, "end": v(50, -88.8) * mm});
            skLineSegment(sketch, "E4008", {"start": v(49.82, -88.78) * mm, "end": v(49.93, -88.79) * mm});
            skLineSegment(sketch, "E4009", {"start": v(49.52, -88.7) * mm, "end": v(49.82, -88.78) * mm});
            skLineSegment(sketch, "E4010", {"start": v(46.14, -87.4) * mm, "end": v(47.16, -87.84) * mm});
            skLineSegment(sketch, "E4011", {"start": v(47.16, -87.84) * mm, "end": v(48.09, -88.2) * mm});
            skLineSegment(sketch, "E4012", {"start": v(48.09, -88.2) * mm, "end": v(48.89, -88.5) * mm});
            skLineSegment(sketch, "E4013", {"start": v(48.89, -88.5) * mm, "end": v(49.52, -88.7) * mm});
            skLineSegment(sketch, "E4014", {"start": v(51.43, -88.62) * mm, "end": v(52.32, -88.37) * mm});
            skLineSegment(sketch, "E4015", {"start": v(52.32, -88.37) * mm, "end": v(53.39, -87.98) * mm});
            skLineSegment(sketch, "E4016", {"start": v(53.39, -87.98) * mm, "end": v(54.62, -87.4) * mm});
            skLineSegment(sketch, "E4017", {"start": v(54.62, -87.4) * mm, "end": v(56.01, -86.58) * mm});
            skLineSegment(sketch, "E4018", {"start": v(56.01, -86.58) * mm, "end": v(57.18, -85.8) * mm});
            skLineSegment(sketch, "E4019", {"start": v(57.18, -85.8) * mm, "end": v(57.55, -85.5) * mm});
            skLineSegment(sketch, "E4020", {"start": v(57.55, -85.5) * mm, "end": v(57.91, -85.24) * mm});
            skLineSegment(sketch, "E4021", {"start": v(57.91, -85.24) * mm, "end": v(58.99, -84.41) * mm});
            skLineSegment(sketch, "E4022", {"start": v(58.99, -84.41) * mm, "end": v(60.48, -83.2) * mm});
            skLineSegment(sketch, "E4023", {"start": v(60.48, -83.2) * mm, "end": v(61.97, -81.91) * mm});
            skLineSegment(sketch, "E4024", {"start": v(61.97, -81.91) * mm, "end": v(63.06, -80.9) * mm});
            skLineSegment(sketch, "E4025", {"start": v(63.06, -80.9) * mm, "end": v(63.41, -80.55) * mm});
            skLineSegment(sketch, "E4026", {"start": v(41.3, -77.87) * mm, "end": v(40.34, -78.06) * mm});
            skLineSegment(sketch, "E4027", {"start": v(40.34, -78.06) * mm, "end": v(39.74, -78.19) * mm});
            skLineSegment(sketch, "E4028", {"start": v(39.74, -78.19) * mm, "end": v(39.53, -78.23) * mm});
            skLineSegment(sketch, "E4029", {"start": v(39.53, -78.23) * mm, "end": v(59.42, -77.15) * mm});
            skLineSegment(sketch, "E4030", {"start": v(59.42, -77.15) * mm, "end": v(59.31, -77.27) * mm});
            skLineSegment(sketch, "E4031", {"start": v(59.31, -77.27) * mm, "end": v(59.02, -77.6) * mm});
            skLineSegment(sketch, "E4032", {"start": v(59.02, -77.6) * mm, "end": v(58.56, -78.13) * mm});
            skLineSegment(sketch, "E4033", {"start": v(58.56, -78.13) * mm, "end": v(57.96, -78.78) * mm});
            skLineSegment(sketch, "E4034", {"start": v(57.96, -78.78) * mm, "end": v(57.23, -79.52) * mm});
            skLineSegment(sketch, "E4035", {"start": v(57.23, -79.52) * mm, "end": v(56.4, -80.32) * mm});
            skLineSegment(sketch, "E4036", {"start": v(56.4, -80.32) * mm, "end": v(55.49, -81.13) * mm});
            skLineSegment(sketch, "E4037", {"start": v(55.49, -81.13) * mm, "end": v(54.77, -81.73) * mm});
            skLineSegment(sketch, "E4038", {"start": v(54.77, -81.73) * mm, "end": v(54.53, -81.91) * mm});
            skLineSegment(sketch, "E4039", {"start": v(54.53, -81.91) * mm, "end": v(54.18, -82.18) * mm});
            skLineSegment(sketch, "E4040", {"start": v(54.18, -82.18) * mm, "end": v(53.08, -82.9) * mm});
            skLineSegment(sketch, "E4041", {"start": v(53.08, -82.9) * mm, "end": v(51.74, -83.61) * mm});
            skLineSegment(sketch, "E4042", {"start": v(51.74, -83.61) * mm, "end": v(50.51, -84.07) * mm});
            skLineSegment(sketch, "E4043", {"start": v(50.51, -84.07) * mm, "end": v(49.69, -84.26) * mm});
            skLineSegment(sketch, "E4044", {"start": v(49.69, -84.26) * mm, "end": v(49.41, -84.3) * mm});
            skLineSegment(sketch, "E4045", {"start": v(49.41, -84.3) * mm, "end": v(49.2, -84.32) * mm});
            skLineSegment(sketch, "E4046", {"start": v(49.2, -84.32) * mm, "end": v(48.6, -84.35) * mm});
            skLineSegment(sketch, "E4047", {"start": v(48.6, -84.35) * mm, "end": v(47.59, -84.3) * mm});
            skLineSegment(sketch, "E4048", {"start": v(47.59, -84.3) * mm, "end": v(46.36, -84.03) * mm});
            skLineSegment(sketch, "E4049", {"start": v(46.36, -84.03) * mm, "end": v(45.24, -83.65) * mm});
            skLineSegment(sketch, "E4050", {"start": v(45.24, -83.65) * mm, "end": v(44.88, -83.5) * mm});
            skLineSegment(sketch, "E4051", {"start": v(44.88, -83.5) * mm, "end": v(44.45, -83.3) * mm});
            skLineSegment(sketch, "E4052", {"start": v(44.45, -83.3) * mm, "end": v(43.18, -82.7) * mm});
            skLineSegment(sketch, "E4053", {"start": v(43.18, -82.7) * mm, "end": v(41.6, -81.87) * mm});
            skLineSegment(sketch, "E4054", {"start": v(41.6, -81.87) * mm, "end": v(40.15, -81.04) * mm});
            skLineSegment(sketch, "E4055", {"start": v(40.15, -81.04) * mm, "end": v(38.87, -80.23) * mm});
            skLineSegment(sketch, "E4056", {"start": v(38.87, -80.23) * mm, "end": v(37.77, -79.48) * mm});
            skLineSegment(sketch, "E4057", {"start": v(37.77, -79.48) * mm, "end": v(36.86, -78.83) * mm});
            skLineSegment(sketch, "E4058", {"start": v(36.86, -78.83) * mm, "end": v(36.18, -78.29) * mm});
            skLineSegment(sketch, "E4059", {"start": v(36.18, -78.29) * mm, "end": v(35.84, -78) * mm});
            skLineSegment(sketch, "E4060", {"start": v(35.84, -78) * mm, "end": v(35.73, -77.9) * mm});
            skLineSegment(sketch, "E4061", {"start": v(35.73, -77.9) * mm, "end": v(36.13, -77.78) * mm});
            skLineSegment(sketch, "E4062", {"start": v(36.13, -77.78) * mm, "end": v(37.35, -77.44) * mm});
            skLineSegment(sketch, "E4063", {"start": v(37.35, -77.44) * mm, "end": v(39.2, -76.97) * mm});
            skLineSegment(sketch, "E4064", {"start": v(39.2, -76.97) * mm, "end": v(41.24, -76.5) * mm});
            skLineSegment(sketch, "E4065", {"start": v(41.24, -76.5) * mm, "end": v(43.45, -76.02) * mm});
            skLineSegment(sketch, "E4066", {"start": v(43.45, -76.02) * mm, "end": v(45.8, -75.56) * mm});
            skLineSegment(sketch, "E4067", {"start": v(45.8, -75.56) * mm, "end": v(48.24, -75.1) * mm});
            skLineSegment(sketch, "E4068", {"start": v(48.24, -75.1) * mm, "end": v(50.75, -74.67) * mm});
            skLineSegment(sketch, "E4069", {"start": v(50.75, -74.67) * mm, "end": v(53.29, -74.25) * mm});
            skLineSegment(sketch, "E4070", {"start": v(53.29, -74.25) * mm, "end": v(55.82, -73.85) * mm});
            skLineSegment(sketch, "E4071", {"start": v(55.82, -73.85) * mm, "end": v(58.33, -73.48) * mm});
            skLineSegment(sketch, "E4072", {"start": v(58.33, -73.48) * mm, "end": v(60.76, -73.13) * mm});
            skLineSegment(sketch, "E4073", {"start": v(60.76, -73.13) * mm, "end": v(63.09, -72.82) * mm});
            skSolve(sketch);
        }
        {
            var Q0;
            Q0 = qSketchRegion(id + "F6", true);
            extrude(context, id + "F7", {"entities" : qUnion([Q0]), "operationType" : NewBodyOperationType.REMOVE, "endBound" : BoundingType.THROUGH_ALL, "oppositeDirection" : true, "depth" : 25 * mm, "offsetDistance" : 25 * mm});
        }
    });
